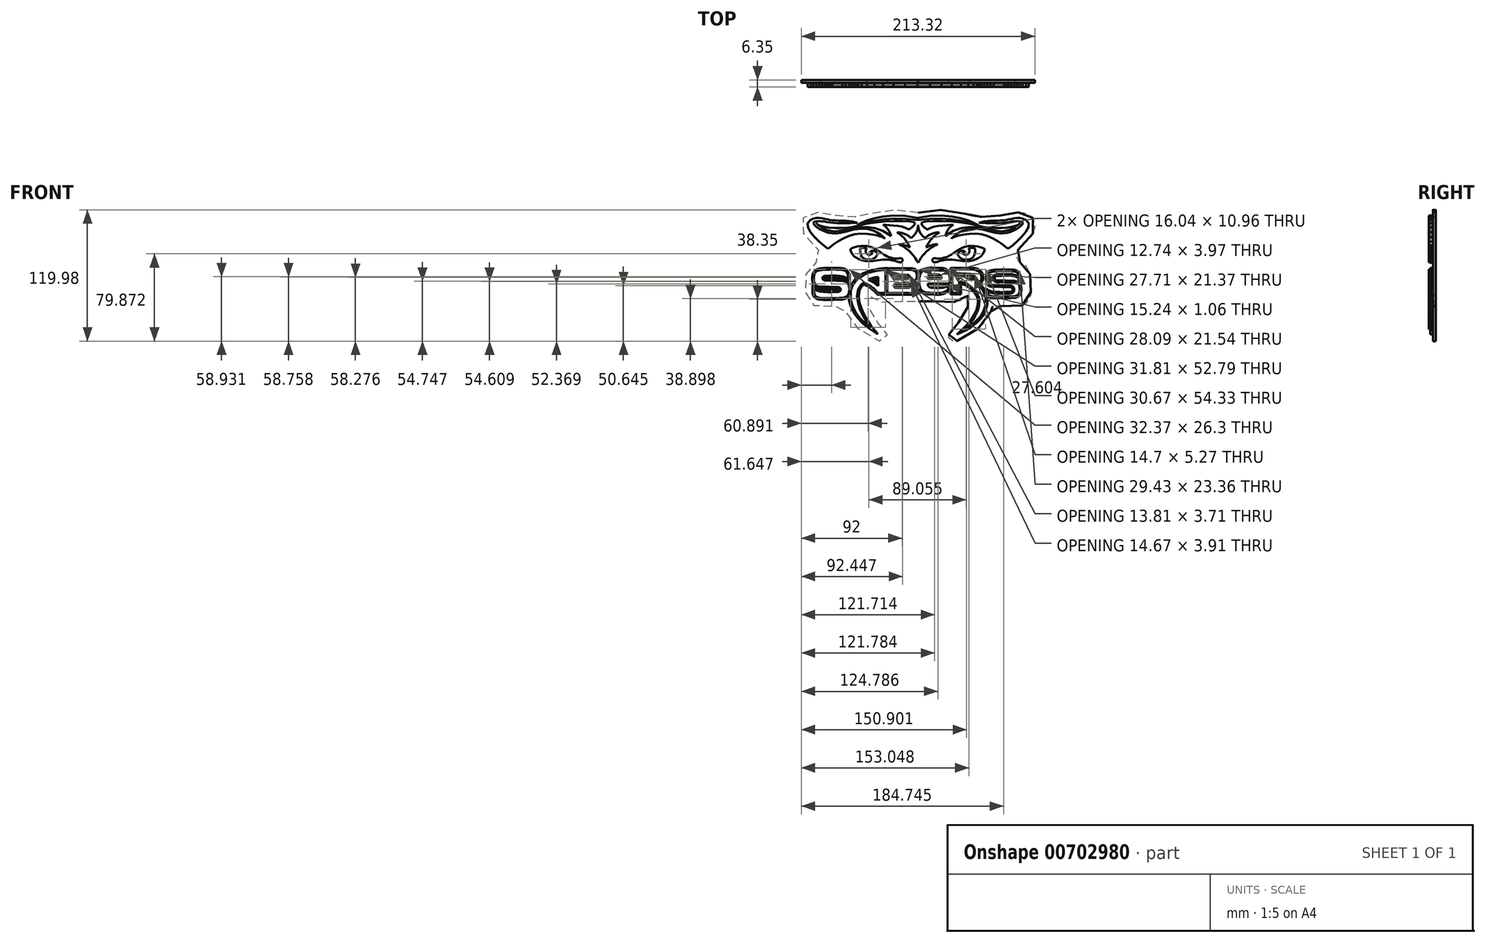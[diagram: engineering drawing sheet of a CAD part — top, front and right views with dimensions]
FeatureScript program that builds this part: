
annotation { "Feature Type Name" : "Feature", "Feature Type Description" : "" }
export const myFeature = defineFeature(function(context is Context, id is Id, definition is map)
    precondition{}
    {
        {
            var Q0;
            Q0=qCreatedBy(makeId("Front.planeOp"),FACE);
            var sketch = newSketch(context, id + "F0", { "sketchPlane" : qUnion([Q0])});
            skLineSegment(sketch, "E0", {"start": v(29.59, -9.42) * mm, "end": v(29.59, -9.4) * mm});
            skLineSegment(sketch, "E1", {"start": v(29.59, -9.4) * mm, "end": v(29.56, -9.4) * mm});
            skLineSegment(sketch, "E2", {"start": v(29.56, -9.4) * mm, "end": v(29.59, -9.42) * mm});
            skLineSegment(sketch, "E3", {"start": v(-61.99, 23.2) * mm, "end": v(-61.75, 23.63) * mm});
            skLineSegment(sketch, "E4", {"start": v(-61.75, 23.63) * mm, "end": v(-60.92, 24.2) * mm});
            skLineSegment(sketch, "E5", {"start": v(-60.92, 24.2) * mm, "end": v(-59.55, 24.82) * mm});
            skLineSegment(sketch, "E6", {"start": v(-59.55, 24.82) * mm, "end": v(-57.7, 25.43) * mm});
            skLineSegment(sketch, "E7", {"start": v(-57.7, 25.43) * mm, "end": v(-55.43, 25.95) * mm});
            skLineSegment(sketch, "E8", {"start": v(-55.43, 25.95) * mm, "end": v(-52.8, 26.3) * mm});
            skLineSegment(sketch, "E9", {"start": v(-52.8, 26.3) * mm, "end": v(-49.86, 26.41) * mm});
            skLineSegment(sketch, "E10", {"start": v(-49.86, 26.41) * mm, "end": v(-46.69, 26.2) * mm});
            skLineSegment(sketch, "E11", {"start": v(-46.69, 26.2) * mm, "end": v(-43.85, 25.66) * mm});
            skLineSegment(sketch, "E12", {"start": v(-43.85, 25.66) * mm, "end": v(-41.25, 24.77) * mm});
            skLineSegment(sketch, "E13", {"start": v(-41.25, 24.77) * mm, "end": v(-38.87, 23.64) * mm});
            skLineSegment(sketch, "E14", {"start": v(-38.87, 23.64) * mm, "end": v(-36.69, 22.36) * mm});
            skLineSegment(sketch, "E15", {"start": v(-36.69, 22.36) * mm, "end": v(-34.7, 21.02) * mm});
            skLineSegment(sketch, "E16", {"start": v(-34.7, 21.02) * mm, "end": v(-32.86, 19.73) * mm});
            skLineSegment(sketch, "E17", {"start": v(-32.86, 19.73) * mm, "end": v(-31.17, 18.56) * mm});
            skLineSegment(sketch, "E18", {"start": v(-31.17, 18.56) * mm, "end": v(-29.62, 17.63) * mm});
            skLineSegment(sketch, "E19", {"start": v(-29.62, 17.63) * mm, "end": v(-28.22, 16.96) * mm});
            skLineSegment(sketch, "E20", {"start": v(-28.22, 16.96) * mm, "end": v(-26.63, 16.34) * mm});
            skLineSegment(sketch, "E21", {"start": v(-26.63, 16.34) * mm, "end": v(-24.9, 15.8) * mm});
            skLineSegment(sketch, "E22", {"start": v(-24.9, 15.8) * mm, "end": v(-23.13, 15.35) * mm});
            skLineSegment(sketch, "E23", {"start": v(-23.13, 15.35) * mm, "end": v(-21.36, 15.03) * mm});
            skLineSegment(sketch, "E24", {"start": v(-21.36, 15.03) * mm, "end": v(-19.67, 14.88) * mm});
            skLineSegment(sketch, "E25", {"start": v(-19.67, 14.88) * mm, "end": v(-18.13, 14.9) * mm});
            skLineSegment(sketch, "E26", {"start": v(-18.13, 14.9) * mm, "end": v(-16.8, 15.15) * mm});
            skLineSegment(sketch, "E27", {"start": v(-16.8, 15.15) * mm, "end": v(-15.76, 15.32) * mm});
            skLineSegment(sketch, "E28", {"start": v(-15.76, 15.32) * mm, "end": v(-15, 15.16) * mm});
            skLineSegment(sketch, "E29", {"start": v(-15, 15.16) * mm, "end": v(-14.49, 14.75) * mm});
            skLineSegment(sketch, "E30", {"start": v(-14.49, 14.75) * mm, "end": v(-14.2, 14.18) * mm});
            skLineSegment(sketch, "E31", {"start": v(-14.2, 14.18) * mm, "end": v(-14.11, 13.54) * mm});
            skLineSegment(sketch, "E32", {"start": v(-14.11, 13.54) * mm, "end": v(-14.19, 12.9) * mm});
            skLineSegment(sketch, "E33", {"start": v(-14.19, 12.9) * mm, "end": v(-14.4, 12.34) * mm});
            skLineSegment(sketch, "E34", {"start": v(-14.4, 12.34) * mm, "end": v(-14.72, 11.97) * mm});
            skLineSegment(sketch, "E35", {"start": v(-14.72, 11.97) * mm, "end": v(-15.07, 11.73) * mm});
            skLineSegment(sketch, "E36", {"start": v(-15.07, 11.73) * mm, "end": v(-15.44, 11.57) * mm});
            skLineSegment(sketch, "E37", {"start": v(-15.44, 11.57) * mm, "end": v(-15.86, 11.48) * mm});
            skLineSegment(sketch, "E38", {"start": v(-15.86, 11.48) * mm, "end": v(-16.38, 11.48) * mm});
            skLineSegment(sketch, "E39", {"start": v(-16.38, 11.48) * mm, "end": v(-17.07, 11.59) * mm});
            skLineSegment(sketch, "E40", {"start": v(-17.07, 11.59) * mm, "end": v(-17.96, 11.81) * mm});
            skLineSegment(sketch, "E41", {"start": v(-17.96, 11.81) * mm, "end": v(-19.1, 12.16) * mm});
            skLineSegment(sketch, "E42", {"start": v(-19.1, 12.16) * mm, "end": v(-20.54, 12.66) * mm});
            skLineSegment(sketch, "E43", {"start": v(-20.54, 12.66) * mm, "end": v(-21.26, 12.89) * mm});
            skLineSegment(sketch, "E44", {"start": v(-21.26, 12.89) * mm, "end": v(-22.02, 13.1) * mm});
            skLineSegment(sketch, "E45", {"start": v(-22.02, 13.1) * mm, "end": v(-22.84, 13.27) * mm});
            skLineSegment(sketch, "E46", {"start": v(-22.84, 13.27) * mm, "end": v(-23.69, 13.44) * mm});
            skLineSegment(sketch, "E47", {"start": v(-23.69, 13.44) * mm, "end": v(-24.57, 13.59) * mm});
            skLineSegment(sketch, "E48", {"start": v(-24.57, 13.59) * mm, "end": v(-25.46, 13.72) * mm});
            skLineSegment(sketch, "E49", {"start": v(-25.46, 13.72) * mm, "end": v(-26.37, 13.84) * mm});
            skLineSegment(sketch, "E50", {"start": v(-26.37, 13.84) * mm, "end": v(-27.28, 13.95) * mm});
            skLineSegment(sketch, "E51", {"start": v(-27.28, 13.95) * mm, "end": v(-29.77, 14.12) * mm});
            skLineSegment(sketch, "E52", {"start": v(-29.77, 14.12) * mm, "end": v(-32.23, 14.04) * mm});
            skLineSegment(sketch, "E53", {"start": v(-32.23, 14.04) * mm, "end": v(-34.65, 13.8) * mm});
            skLineSegment(sketch, "E54", {"start": v(-34.65, 13.8) * mm, "end": v(-37, 13.45) * mm});
            skLineSegment(sketch, "E55", {"start": v(-37, 13.45) * mm, "end": v(-39.23, 13.08) * mm});
            skLineSegment(sketch, "E56", {"start": v(-39.23, 13.08) * mm, "end": v(-41.33, 12.75) * mm});
            skLineSegment(sketch, "E57", {"start": v(-41.33, 12.75) * mm, "end": v(-43.27, 12.54) * mm});
            skLineSegment(sketch, "E58", {"start": v(-43.27, 12.54) * mm, "end": v(-45.02, 12.5) * mm});
            skLineSegment(sketch, "E59", {"start": v(-45.02, 12.5) * mm, "end": v(-48.22, 12.8) * mm});
            skLineSegment(sketch, "E60", {"start": v(-48.22, 12.8) * mm, "end": v(-51.17, 13.4) * mm});
            skLineSegment(sketch, "E61", {"start": v(-51.17, 13.4) * mm, "end": v(-53.83, 14.28) * mm});
            skLineSegment(sketch, "E62", {"start": v(-53.83, 14.28) * mm, "end": v(-56.2, 15.46) * mm});
            skLineSegment(sketch, "E63", {"start": v(-56.2, 15.46) * mm, "end": v(-58.2, 16.93) * mm});
            skLineSegment(sketch, "E64", {"start": v(-58.2, 16.93) * mm, "end": v(-59.87, 18.71) * mm});
            skLineSegment(sketch, "E65", {"start": v(-59.87, 18.71) * mm, "end": v(-61.14, 20.8) * mm});
            skLineSegment(sketch, "E66", {"start": v(-61.14, 20.8) * mm, "end": v(-61.99, 23.2) * mm});
            skLineSegment(sketch, "E67", {"start": v(-47, 24.3) * mm, "end": v(-47.18, 24.33) * mm});
            skLineSegment(sketch, "E68", {"start": v(-47.18, 24.33) * mm, "end": v(-47.65, 24.44) * mm});
            skLineSegment(sketch, "E69", {"start": v(-47.65, 24.44) * mm, "end": v(-48.36, 24.57) * mm});
            skLineSegment(sketch, "E70", {"start": v(-48.36, 24.57) * mm, "end": v(-49.23, 24.69) * mm});
            skLineSegment(sketch, "E71", {"start": v(-49.23, 24.69) * mm, "end": v(-50.18, 24.77) * mm});
            skLineSegment(sketch, "E72", {"start": v(-50.18, 24.77) * mm, "end": v(-51.16, 24.77) * mm});
            skLineSegment(sketch, "E73", {"start": v(-51.16, 24.77) * mm, "end": v(-52.09, 24.67) * mm});
            skLineSegment(sketch, "E74", {"start": v(-52.09, 24.67) * mm, "end": v(-52.9, 24.42) * mm});
            skLineSegment(sketch, "E75", {"start": v(-52.9, 24.42) * mm, "end": v(-52.95, 24.02) * mm});
            skLineSegment(sketch, "E76", {"start": v(-52.95, 24.02) * mm, "end": v(-53.03, 22.94) * mm});
            skLineSegment(sketch, "E77", {"start": v(-53.03, 22.94) * mm, "end": v(-53, 21.4) * mm});
            skLineSegment(sketch, "E78", {"start": v(-53, 21.4) * mm, "end": v(-52.71, 19.6) * mm});
            skLineSegment(sketch, "E79", {"start": v(-52.71, 19.6) * mm, "end": v(-52.04, 17.74) * mm});
            skLineSegment(sketch, "E80", {"start": v(-52.04, 17.74) * mm, "end": v(-50.83, 16.03) * mm});
            skLineSegment(sketch, "E81", {"start": v(-50.83, 16.03) * mm, "end": v(-48.96, 14.68) * mm});
            skLineSegment(sketch, "E82", {"start": v(-48.96, 14.68) * mm, "end": v(-46.29, 13.88) * mm});
            skLineSegment(sketch, "E83", {"start": v(-46.29, 13.88) * mm, "end": v(-43.65, 13.81) * mm});
            skLineSegment(sketch, "E84", {"start": v(-43.65, 13.81) * mm, "end": v(-41.55, 14.3) * mm});
            skLineSegment(sketch, "E85", {"start": v(-41.55, 14.3) * mm, "end": v(-39.92, 15.2) * mm});
            skLineSegment(sketch, "E86", {"start": v(-39.92, 15.2) * mm, "end": v(-38.72, 16.31) * mm});
            skLineSegment(sketch, "E87", {"start": v(-38.72, 16.31) * mm, "end": v(-37.88, 17.48) * mm});
            skLineSegment(sketch, "E88", {"start": v(-37.88, 17.48) * mm, "end": v(-37.35, 18.53) * mm});
            skLineSegment(sketch, "E89", {"start": v(-37.35, 18.53) * mm, "end": v(-37.07, 19.28) * mm});
            skLineSegment(sketch, "E90", {"start": v(-37.07, 19.28) * mm, "end": v(-37, 19.57) * mm});
            skLineSegment(sketch, "E91", {"start": v(-37, 19.57) * mm, "end": v(-37.09, 19.7) * mm});
            skLineSegment(sketch, "E92", {"start": v(-37.09, 19.7) * mm, "end": v(-37.36, 20.04) * mm});
            skLineSegment(sketch, "E93", {"start": v(-37.36, 20.04) * mm, "end": v(-37.83, 20.5) * mm});
            skLineSegment(sketch, "E94", {"start": v(-37.83, 20.5) * mm, "end": v(-38.5, 21) * mm});
            skLineSegment(sketch, "E95", {"start": v(-38.5, 21) * mm, "end": v(-39.37, 21.47) * mm});
            skLineSegment(sketch, "E96", {"start": v(-39.37, 21.47) * mm, "end": v(-40.44, 21.8) * mm});
            skLineSegment(sketch, "E97", {"start": v(-40.44, 21.8) * mm, "end": v(-41.73, 21.94) * mm});
            skLineSegment(sketch, "E98", {"start": v(-41.73, 21.94) * mm, "end": v(-43.24, 21.78) * mm});
            skLineSegment(sketch, "E99", {"start": v(-43.24, 21.78) * mm, "end": v(-43.28, 21.74) * mm});
            skLineSegment(sketch, "E100", {"start": v(-43.28, 21.74) * mm, "end": v(-43.36, 21.63) * mm});
            skLineSegment(sketch, "E101", {"start": v(-43.36, 21.63) * mm, "end": v(-43.45, 21.47) * mm});
            skLineSegment(sketch, "E102", {"start": v(-43.45, 21.47) * mm, "end": v(-43.5, 21.28) * mm});
            skLineSegment(sketch, "E103", {"start": v(-43.5, 21.28) * mm, "end": v(-43.46, 21.08) * mm});
            skLineSegment(sketch, "E104", {"start": v(-43.46, 21.08) * mm, "end": v(-43.29, 20.9) * mm});
            skLineSegment(sketch, "E105", {"start": v(-43.29, 20.9) * mm, "end": v(-42.95, 20.72) * mm});
            skLineSegment(sketch, "E106", {"start": v(-42.95, 20.72) * mm, "end": v(-42.4, 20.6) * mm});
            skLineSegment(sketch, "E107", {"start": v(-42.4, 20.6) * mm, "end": v(-41.88, 20.42) * mm});
            skLineSegment(sketch, "E108", {"start": v(-41.88, 20.42) * mm, "end": v(-41.7, 20.12) * mm});
            skLineSegment(sketch, "E109", {"start": v(-41.7, 20.12) * mm, "end": v(-41.78, 19.74) * mm});
            skLineSegment(sketch, "E110", {"start": v(-41.78, 19.74) * mm, "end": v(-42.11, 19.33) * mm});
            skLineSegment(sketch, "E111", {"start": v(-42.11, 19.33) * mm, "end": v(-42.64, 18.95) * mm});
            skLineSegment(sketch, "E112", {"start": v(-42.64, 18.95) * mm, "end": v(-43.32, 18.65) * mm});
            skLineSegment(sketch, "E113", {"start": v(-43.32, 18.65) * mm, "end": v(-44.12, 18.47) * mm});
            skLineSegment(sketch, "E114", {"start": v(-44.12, 18.47) * mm, "end": v(-45, 18.47) * mm});
            skLineSegment(sketch, "E115", {"start": v(-45, 18.47) * mm, "end": v(-45.77, 18.66) * mm});
            skLineSegment(sketch, "E116", {"start": v(-45.77, 18.66) * mm, "end": v(-46.5, 19.03) * mm});
            skLineSegment(sketch, "E117", {"start": v(-46.5, 19.03) * mm, "end": v(-47.12, 19.58) * mm});
            skLineSegment(sketch, "E118", {"start": v(-47.12, 19.58) * mm, "end": v(-47.6, 20.27) * mm});
            skLineSegment(sketch, "E119", {"start": v(-47.6, 20.27) * mm, "end": v(-47.87, 21.1) * mm});
            skLineSegment(sketch, "E120", {"start": v(-47.87, 21.1) * mm, "end": v(-47.9, 22.06) * mm});
            skLineSegment(sketch, "E121", {"start": v(-47.9, 22.06) * mm, "end": v(-47.62, 23.13) * mm});
            skLineSegment(sketch, "E122", {"start": v(-47.62, 23.13) * mm, "end": v(-47, 24.3) * mm});
            skLineSegment(sketch, "E123", {"start": v(61.02, 23.2) * mm, "end": v(60.78, 23.63) * mm});
            skLineSegment(sketch, "E124", {"start": v(60.78, 23.63) * mm, "end": v(59.95, 24.2) * mm});
            skLineSegment(sketch, "E125", {"start": v(59.95, 24.2) * mm, "end": v(58.58, 24.82) * mm});
            skLineSegment(sketch, "E126", {"start": v(58.58, 24.82) * mm, "end": v(56.73, 25.43) * mm});
            skLineSegment(sketch, "E127", {"start": v(56.73, 25.43) * mm, "end": v(54.46, 25.95) * mm});
            skLineSegment(sketch, "E128", {"start": v(54.46, 25.95) * mm, "end": v(51.82, 26.3) * mm});
            skLineSegment(sketch, "E129", {"start": v(51.82, 26.3) * mm, "end": v(48.9, 26.41) * mm});
            skLineSegment(sketch, "E130", {"start": v(48.9, 26.41) * mm, "end": v(45.71, 26.2) * mm});
            skLineSegment(sketch, "E131", {"start": v(45.71, 26.2) * mm, "end": v(42.88, 25.66) * mm});
            skLineSegment(sketch, "E132", {"start": v(42.88, 25.66) * mm, "end": v(40.28, 24.77) * mm});
            skLineSegment(sketch, "E133", {"start": v(40.28, 24.77) * mm, "end": v(37.9, 23.64) * mm});
            skLineSegment(sketch, "E134", {"start": v(37.9, 23.64) * mm, "end": v(35.72, 22.36) * mm});
            skLineSegment(sketch, "E135", {"start": v(35.72, 22.36) * mm, "end": v(33.72, 21.02) * mm});
            skLineSegment(sketch, "E136", {"start": v(33.72, 21.02) * mm, "end": v(31.89, 19.73) * mm});
            skLineSegment(sketch, "E137", {"start": v(31.89, 19.73) * mm, "end": v(30.2, 18.56) * mm});
            skLineSegment(sketch, "E138", {"start": v(30.2, 18.56) * mm, "end": v(28.65, 17.63) * mm});
            skLineSegment(sketch, "E139", {"start": v(28.65, 17.63) * mm, "end": v(27.25, 16.96) * mm});
            skLineSegment(sketch, "E140", {"start": v(27.25, 16.96) * mm, "end": v(25.66, 16.34) * mm});
            skLineSegment(sketch, "E141", {"start": v(25.66, 16.34) * mm, "end": v(23.93, 15.8) * mm});
            skLineSegment(sketch, "E142", {"start": v(23.93, 15.8) * mm, "end": v(22.15, 15.35) * mm});
            skLineSegment(sketch, "E143", {"start": v(22.15, 15.35) * mm, "end": v(20.39, 15.03) * mm});
            skLineSegment(sketch, "E144", {"start": v(20.39, 15.03) * mm, "end": v(18.7, 14.88) * mm});
            skLineSegment(sketch, "E145", {"start": v(18.7, 14.88) * mm, "end": v(17.15, 14.9) * mm});
            skLineSegment(sketch, "E146", {"start": v(17.15, 14.9) * mm, "end": v(15.83, 15.15) * mm});
            skLineSegment(sketch, "E147", {"start": v(15.83, 15.15) * mm, "end": v(14.78, 15.32) * mm});
            skLineSegment(sketch, "E148", {"start": v(14.78, 15.32) * mm, "end": v(14.02, 15.16) * mm});
            skLineSegment(sketch, "E149", {"start": v(14.02, 15.16) * mm, "end": v(13.51, 14.75) * mm});
            skLineSegment(sketch, "E150", {"start": v(13.51, 14.75) * mm, "end": v(13.23, 14.18) * mm});
            skLineSegment(sketch, "E151", {"start": v(13.23, 14.18) * mm, "end": v(13.14, 13.54) * mm});
            skLineSegment(sketch, "E152", {"start": v(13.14, 13.54) * mm, "end": v(13.22, 12.9) * mm});
            skLineSegment(sketch, "E153", {"start": v(13.22, 12.9) * mm, "end": v(13.43, 12.34) * mm});
            skLineSegment(sketch, "E154", {"start": v(13.43, 12.34) * mm, "end": v(13.75, 11.97) * mm});
            skLineSegment(sketch, "E155", {"start": v(13.75, 11.97) * mm, "end": v(14.1, 11.73) * mm});
            skLineSegment(sketch, "E156", {"start": v(14.1, 11.73) * mm, "end": v(14.46, 11.57) * mm});
            skLineSegment(sketch, "E157", {"start": v(14.46, 11.57) * mm, "end": v(14.88, 11.48) * mm});
            skLineSegment(sketch, "E158", {"start": v(14.88, 11.48) * mm, "end": v(15.41, 11.48) * mm});
            skLineSegment(sketch, "E159", {"start": v(15.41, 11.48) * mm, "end": v(16.1, 11.59) * mm});
            skLineSegment(sketch, "E160", {"start": v(16.1, 11.59) * mm, "end": v(16.99, 11.81) * mm});
            skLineSegment(sketch, "E161", {"start": v(16.99, 11.81) * mm, "end": v(18.13, 12.16) * mm});
            skLineSegment(sketch, "E162", {"start": v(18.13, 12.16) * mm, "end": v(19.57, 12.66) * mm});
            skLineSegment(sketch, "E163", {"start": v(19.57, 12.66) * mm, "end": v(20.28, 12.89) * mm});
            skLineSegment(sketch, "E164", {"start": v(20.28, 12.89) * mm, "end": v(21.05, 13.1) * mm});
            skLineSegment(sketch, "E165", {"start": v(21.05, 13.1) * mm, "end": v(21.86, 13.27) * mm});
            skLineSegment(sketch, "E166", {"start": v(21.86, 13.27) * mm, "end": v(22.72, 13.44) * mm});
            skLineSegment(sketch, "E167", {"start": v(22.72, 13.44) * mm, "end": v(23.6, 13.59) * mm});
            skLineSegment(sketch, "E168", {"start": v(23.6, 13.59) * mm, "end": v(24.5, 13.72) * mm});
            skLineSegment(sketch, "E169", {"start": v(24.5, 13.72) * mm, "end": v(25.4, 13.84) * mm});
            skLineSegment(sketch, "E170", {"start": v(25.4, 13.84) * mm, "end": v(26.3, 13.95) * mm});
            skLineSegment(sketch, "E171", {"start": v(26.3, 13.95) * mm, "end": v(28.8, 14.12) * mm});
            skLineSegment(sketch, "E172", {"start": v(28.8, 14.12) * mm, "end": v(31.26, 14.04) * mm});
            skLineSegment(sketch, "E173", {"start": v(31.26, 14.04) * mm, "end": v(33.68, 13.8) * mm});
            skLineSegment(sketch, "E174", {"start": v(33.68, 13.8) * mm, "end": v(36.02, 13.45) * mm});
            skLineSegment(sketch, "E175", {"start": v(36.02, 13.45) * mm, "end": v(38.26, 13.08) * mm});
            skLineSegment(sketch, "E176", {"start": v(38.26, 13.08) * mm, "end": v(40.36, 12.75) * mm});
            skLineSegment(sketch, "E177", {"start": v(40.36, 12.75) * mm, "end": v(42.3, 12.54) * mm});
            skLineSegment(sketch, "E178", {"start": v(42.3, 12.54) * mm, "end": v(44.05, 12.5) * mm});
            skLineSegment(sketch, "E179", {"start": v(44.05, 12.5) * mm, "end": v(47.25, 12.8) * mm});
            skLineSegment(sketch, "E180", {"start": v(47.25, 12.8) * mm, "end": v(50.2, 13.4) * mm});
            skLineSegment(sketch, "E181", {"start": v(50.2, 13.4) * mm, "end": v(52.86, 14.28) * mm});
            skLineSegment(sketch, "E182", {"start": v(52.86, 14.28) * mm, "end": v(55.22, 15.46) * mm});
            skLineSegment(sketch, "E183", {"start": v(55.22, 15.46) * mm, "end": v(57.24, 16.93) * mm});
            skLineSegment(sketch, "E184", {"start": v(57.24, 16.93) * mm, "end": v(58.9, 18.71) * mm});
            skLineSegment(sketch, "E185", {"start": v(58.9, 18.71) * mm, "end": v(60.16, 20.8) * mm});
            skLineSegment(sketch, "E186", {"start": v(60.16, 20.8) * mm, "end": v(61.02, 23.2) * mm});
            skLineSegment(sketch, "E187", {"start": v(46.03, 24.3) * mm, "end": v(46.2, 24.33) * mm});
            skLineSegment(sketch, "E188", {"start": v(46.2, 24.33) * mm, "end": v(46.68, 24.44) * mm});
            skLineSegment(sketch, "E189", {"start": v(46.68, 24.44) * mm, "end": v(47.39, 24.57) * mm});
            skLineSegment(sketch, "E190", {"start": v(47.39, 24.57) * mm, "end": v(48.25, 24.69) * mm});
            skLineSegment(sketch, "E191", {"start": v(48.25, 24.69) * mm, "end": v(49.21, 24.77) * mm});
            skLineSegment(sketch, "E192", {"start": v(49.21, 24.77) * mm, "end": v(50.19, 24.77) * mm});
            skLineSegment(sketch, "E193", {"start": v(50.19, 24.77) * mm, "end": v(51.12, 24.67) * mm});
            skLineSegment(sketch, "E194", {"start": v(51.12, 24.67) * mm, "end": v(51.92, 24.42) * mm});
            skLineSegment(sketch, "E195", {"start": v(51.92, 24.42) * mm, "end": v(51.98, 24.02) * mm});
            skLineSegment(sketch, "E196", {"start": v(51.98, 24.02) * mm, "end": v(52.06, 22.94) * mm});
            skLineSegment(sketch, "E197", {"start": v(52.06, 22.94) * mm, "end": v(52.03, 21.4) * mm});
            skLineSegment(sketch, "E198", {"start": v(52.03, 21.4) * mm, "end": v(51.74, 19.6) * mm});
            skLineSegment(sketch, "E199", {"start": v(51.74, 19.6) * mm, "end": v(51.07, 17.74) * mm});
            skLineSegment(sketch, "E200", {"start": v(51.07, 17.74) * mm, "end": v(49.86, 16.03) * mm});
            skLineSegment(sketch, "E201", {"start": v(49.86, 16.03) * mm, "end": v(47.99, 14.68) * mm});
            skLineSegment(sketch, "E202", {"start": v(47.99, 14.68) * mm, "end": v(45.31, 13.88) * mm});
            skLineSegment(sketch, "E203", {"start": v(45.31, 13.88) * mm, "end": v(42.68, 13.81) * mm});
            skLineSegment(sketch, "E204", {"start": v(42.68, 13.81) * mm, "end": v(40.58, 14.3) * mm});
            skLineSegment(sketch, "E205", {"start": v(40.58, 14.3) * mm, "end": v(38.95, 15.2) * mm});
            skLineSegment(sketch, "E206", {"start": v(38.95, 15.2) * mm, "end": v(37.75, 16.31) * mm});
            skLineSegment(sketch, "E207", {"start": v(37.75, 16.31) * mm, "end": v(36.91, 17.48) * mm});
            skLineSegment(sketch, "E208", {"start": v(36.91, 17.48) * mm, "end": v(36.38, 18.53) * mm});
            skLineSegment(sketch, "E209", {"start": v(36.38, 18.53) * mm, "end": v(36.1, 19.28) * mm});
            skLineSegment(sketch, "E210", {"start": v(36.1, 19.28) * mm, "end": v(36.02, 19.57) * mm});
            skLineSegment(sketch, "E211", {"start": v(36.02, 19.57) * mm, "end": v(36.11, 19.7) * mm});
            skLineSegment(sketch, "E212", {"start": v(36.11, 19.7) * mm, "end": v(36.4, 20.04) * mm});
            skLineSegment(sketch, "E213", {"start": v(36.4, 20.04) * mm, "end": v(36.86, 20.5) * mm});
            skLineSegment(sketch, "E214", {"start": v(36.86, 20.5) * mm, "end": v(37.53, 21) * mm});
            skLineSegment(sketch, "E215", {"start": v(37.53, 21) * mm, "end": v(38.4, 21.47) * mm});
            skLineSegment(sketch, "E216", {"start": v(38.4, 21.47) * mm, "end": v(39.47, 21.8) * mm});
            skLineSegment(sketch, "E217", {"start": v(39.47, 21.8) * mm, "end": v(40.76, 21.94) * mm});
            skLineSegment(sketch, "E218", {"start": v(40.76, 21.94) * mm, "end": v(42.27, 21.78) * mm});
            skLineSegment(sketch, "E219", {"start": v(42.27, 21.78) * mm, "end": v(42.3, 21.74) * mm});
            skLineSegment(sketch, "E220", {"start": v(42.3, 21.74) * mm, "end": v(42.4, 21.63) * mm});
            skLineSegment(sketch, "E221", {"start": v(42.4, 21.63) * mm, "end": v(42.48, 21.47) * mm});
            skLineSegment(sketch, "E222", {"start": v(42.48, 21.47) * mm, "end": v(42.52, 21.28) * mm});
            skLineSegment(sketch, "E223", {"start": v(42.52, 21.28) * mm, "end": v(42.49, 21.08) * mm});
            skLineSegment(sketch, "E224", {"start": v(42.49, 21.08) * mm, "end": v(42.32, 20.9) * mm});
            skLineSegment(sketch, "E225", {"start": v(42.32, 20.9) * mm, "end": v(41.98, 20.72) * mm});
            skLineSegment(sketch, "E226", {"start": v(41.98, 20.72) * mm, "end": v(41.42, 20.6) * mm});
            skLineSegment(sketch, "E227", {"start": v(41.42, 20.6) * mm, "end": v(40.91, 20.42) * mm});
            skLineSegment(sketch, "E228", {"start": v(40.91, 20.42) * mm, "end": v(40.72, 20.12) * mm});
            skLineSegment(sketch, "E229", {"start": v(40.72, 20.12) * mm, "end": v(40.81, 19.74) * mm});
            skLineSegment(sketch, "E230", {"start": v(40.81, 19.74) * mm, "end": v(41.14, 19.33) * mm});
            skLineSegment(sketch, "E231", {"start": v(41.14, 19.33) * mm, "end": v(41.67, 18.95) * mm});
            skLineSegment(sketch, "E232", {"start": v(41.67, 18.95) * mm, "end": v(42.35, 18.65) * mm});
            skLineSegment(sketch, "E233", {"start": v(42.35, 18.65) * mm, "end": v(43.15, 18.47) * mm});
            skLineSegment(sketch, "E234", {"start": v(43.15, 18.47) * mm, "end": v(44.03, 18.47) * mm});
            skLineSegment(sketch, "E235", {"start": v(44.03, 18.47) * mm, "end": v(44.8, 18.66) * mm});
            skLineSegment(sketch, "E236", {"start": v(44.8, 18.66) * mm, "end": v(45.52, 19.03) * mm});
            skLineSegment(sketch, "E237", {"start": v(45.52, 19.03) * mm, "end": v(46.15, 19.58) * mm});
            skLineSegment(sketch, "E238", {"start": v(46.15, 19.58) * mm, "end": v(46.62, 20.27) * mm});
            skLineSegment(sketch, "E239", {"start": v(46.62, 20.27) * mm, "end": v(46.9, 21.1) * mm});
            skLineSegment(sketch, "E240", {"start": v(46.9, 21.1) * mm, "end": v(46.92, 22.06) * mm});
            skLineSegment(sketch, "E241", {"start": v(46.92, 22.06) * mm, "end": v(46.65, 23.13) * mm});
            skLineSegment(sketch, "E242", {"start": v(46.65, 23.13) * mm, "end": v(46.03, 24.3) * mm});
            skLineSegment(sketch, "E243", {"start": v(-55.59, 47.59) * mm, "end": v(-57.95, 48.29) * mm});
            skLineSegment(sketch, "E244", {"start": v(-57.95, 48.29) * mm, "end": v(-60.51, 48.8) * mm});
            skLineSegment(sketch, "E245", {"start": v(-60.51, 48.8) * mm, "end": v(-63.26, 49.16) * mm});
            skLineSegment(sketch, "E246", {"start": v(-63.26, 49.16) * mm, "end": v(-66.14, 49.4) * mm});
            skLineSegment(sketch, "E247", {"start": v(-66.14, 49.4) * mm, "end": v(-69.13, 49.57) * mm});
            skLineSegment(sketch, "E248", {"start": v(-69.13, 49.57) * mm, "end": v(-72.2, 49.68) * mm});
            skLineSegment(sketch, "E249", {"start": v(-72.2, 49.68) * mm, "end": v(-75.32, 49.78) * mm});
            skLineSegment(sketch, "E250", {"start": v(-75.32, 49.78) * mm, "end": v(-78.45, 49.9) * mm});
            skLineSegment(sketch, "E251", {"start": v(-78.45, 49.9) * mm, "end": v(-80.5, 50.17) * mm});
            skLineSegment(sketch, "E252", {"start": v(-80.5, 50.17) * mm, "end": v(-82.72, 50.67) * mm});
            skLineSegment(sketch, "E253", {"start": v(-82.72, 50.67) * mm, "end": v(-85.1, 51.25) * mm});
            skLineSegment(sketch, "E254", {"start": v(-85.1, 51.25) * mm, "end": v(-87.6, 51.77) * mm});
            skLineSegment(sketch, "E255", {"start": v(-87.6, 51.77) * mm, "end": v(-90.21, 52.08) * mm});
            skLineSegment(sketch, "E256", {"start": v(-90.21, 52.08) * mm, "end": v(-92.9, 52.03) * mm});
            skLineSegment(sketch, "E257", {"start": v(-92.9, 52.03) * mm, "end": v(-95.65, 51.47) * mm});
            skLineSegment(sketch, "E258", {"start": v(-95.65, 51.47) * mm, "end": v(-98.44, 50.25) * mm});
            skLineSegment(sketch, "E259", {"start": v(-98.44, 50.25) * mm, "end": v(-100.97, 47.25) * mm});
            skLineSegment(sketch, "E260", {"start": v(-100.97, 47.25) * mm, "end": v(-100.64, 43.38) * mm});
            skLineSegment(sketch, "E261", {"start": v(-100.64, 43.38) * mm, "end": v(-98.23, 39.02) * mm});
            skLineSegment(sketch, "E262", {"start": v(-98.23, 39.02) * mm, "end": v(-94.52, 34.57) * mm});
            skLineSegment(sketch, "E263", {"start": v(-94.52, 34.57) * mm, "end": v(-90.29, 30.43) * mm});
            skLineSegment(sketch, "E264", {"start": v(-90.29, 30.43) * mm, "end": v(-86.3, 26.98) * mm});
            skLineSegment(sketch, "E265", {"start": v(-86.3, 26.98) * mm, "end": v(-83.34, 24.62) * mm});
            skLineSegment(sketch, "E266", {"start": v(-83.34, 24.62) * mm, "end": v(-82.18, 23.75) * mm});
            skLineSegment(sketch, "E267", {"start": v(-82.18, 23.75) * mm, "end": v(-81.5, 24.36) * mm});
            skLineSegment(sketch, "E268", {"start": v(-81.5, 24.36) * mm, "end": v(-79.6, 25.96) * mm});
            skLineSegment(sketch, "E269", {"start": v(-79.6, 25.96) * mm, "end": v(-76.64, 28.23) * mm});
            skLineSegment(sketch, "E270", {"start": v(-76.64, 28.23) * mm, "end": v(-72.82, 30.82) * mm});
            skLineSegment(sketch, "E271", {"start": v(-72.82, 30.82) * mm, "end": v(-68.34, 33.4) * mm});
            skLineSegment(sketch, "E272", {"start": v(-68.34, 33.4) * mm, "end": v(-63.38, 35.65) * mm});
            skLineSegment(sketch, "E273", {"start": v(-63.38, 35.65) * mm, "end": v(-58.12, 37.22) * mm});
            skLineSegment(sketch, "E274", {"start": v(-58.12, 37.22) * mm, "end": v(-52.76, 37.78) * mm});
            skLineSegment(sketch, "E275", {"start": v(-52.76, 37.78) * mm, "end": v(-46.6, 37.52) * mm});
            skLineSegment(sketch, "E276", {"start": v(-46.6, 37.52) * mm, "end": v(-41.63, 36.97) * mm});
            skLineSegment(sketch, "E277", {"start": v(-41.63, 36.97) * mm, "end": v(-37.73, 36.22) * mm});
            skLineSegment(sketch, "E278", {"start": v(-37.73, 36.22) * mm, "end": v(-34.79, 35.38) * mm});
            skLineSegment(sketch, "E279", {"start": v(-34.79, 35.38) * mm, "end": v(-32.7, 34.54) * mm});
            skLineSegment(sketch, "E280", {"start": v(-32.7, 34.54) * mm, "end": v(-31.35, 33.82) * mm});
            skLineSegment(sketch, "E281", {"start": v(-31.35, 33.82) * mm, "end": v(-30.62, 33.31) * mm});
            skLineSegment(sketch, "E282", {"start": v(-30.62, 33.31) * mm, "end": v(-30.4, 33.12) * mm});
            skLineSegment(sketch, "E283", {"start": v(-30.4, 33.12) * mm, "end": v(-30.82, 33.64) * mm});
            skLineSegment(sketch, "E284", {"start": v(-30.82, 33.64) * mm, "end": v(-32.09, 35) * mm});
            skLineSegment(sketch, "E285", {"start": v(-32.09, 35) * mm, "end": v(-34.22, 36.82) * mm});
            skLineSegment(sketch, "E286", {"start": v(-34.22, 36.82) * mm, "end": v(-37.24, 38.8) * mm});
            skLineSegment(sketch, "E287", {"start": v(-37.24, 38.8) * mm, "end": v(-41.16, 40.6) * mm});
            skLineSegment(sketch, "E288", {"start": v(-41.16, 40.6) * mm, "end": v(-46.02, 41.86) * mm});
            skLineSegment(sketch, "E289", {"start": v(-46.02, 41.86) * mm, "end": v(-51.81, 42.25) * mm});
            skLineSegment(sketch, "E290", {"start": v(-51.81, 42.25) * mm, "end": v(-58.57, 41.44) * mm});
            skLineSegment(sketch, "E291", {"start": v(-58.57, 41.44) * mm, "end": v(-62.24, 40.6) * mm});
            skLineSegment(sketch, "E292", {"start": v(-62.24, 40.6) * mm, "end": v(-65.44, 39.78) * mm});
            skLineSegment(sketch, "E293", {"start": v(-65.44, 39.78) * mm, "end": v(-68.3, 39.03) * mm});
            skLineSegment(sketch, "E294", {"start": v(-68.3, 39.03) * mm, "end": v(-70.9, 38.43) * mm});
            skLineSegment(sketch, "E295", {"start": v(-70.9, 38.43) * mm, "end": v(-73.4, 38.01) * mm});
            skLineSegment(sketch, "E296", {"start": v(-73.4, 38.01) * mm, "end": v(-75.9, 37.84) * mm});
            skLineSegment(sketch, "E297", {"start": v(-75.9, 37.84) * mm, "end": v(-78.52, 37.98) * mm});
            skLineSegment(sketch, "E298", {"start": v(-78.52, 37.98) * mm, "end": v(-81.38, 38.49) * mm});
            skLineSegment(sketch, "E299", {"start": v(-81.38, 38.49) * mm, "end": v(-84.39, 39.39) * mm});
            skLineSegment(sketch, "E300", {"start": v(-84.39, 39.39) * mm, "end": v(-87.29, 40.6) * mm});
            skLineSegment(sketch, "E301", {"start": v(-87.29, 40.6) * mm, "end": v(-89.96, 42.01) * mm});
            skLineSegment(sketch, "E302", {"start": v(-89.96, 42.01) * mm, "end": v(-92.27, 43.51) * mm});
            skLineSegment(sketch, "E303", {"start": v(-92.27, 43.51) * mm, "end": v(-94.09, 44.99) * mm});
            skLineSegment(sketch, "E304", {"start": v(-94.09, 44.99) * mm, "end": v(-95.29, 46.33) * mm});
            skLineSegment(sketch, "E305", {"start": v(-95.29, 46.33) * mm, "end": v(-95.74, 47.41) * mm});
            skLineSegment(sketch, "E306", {"start": v(-95.74, 47.41) * mm, "end": v(-95.32, 48.14) * mm});
            skLineSegment(sketch, "E307", {"start": v(-95.32, 48.14) * mm, "end": v(-94.32, 48.57) * mm});
            skLineSegment(sketch, "E308", {"start": v(-94.32, 48.57) * mm, "end": v(-93.13, 48.88) * mm});
            skLineSegment(sketch, "E309", {"start": v(-93.13, 48.88) * mm, "end": v(-91.7, 49.05) * mm});
            skLineSegment(sketch, "E310", {"start": v(-91.7, 49.05) * mm, "end": v(-90.03, 49.08) * mm});
            skLineSegment(sketch, "E311", {"start": v(-90.03, 49.08) * mm, "end": v(-88.08, 48.98) * mm});
            skLineSegment(sketch, "E312", {"start": v(-88.08, 48.98) * mm, "end": v(-85.83, 48.75) * mm});
            skLineSegment(sketch, "E313", {"start": v(-85.83, 48.75) * mm, "end": v(-83.25, 48.38) * mm});
            skLineSegment(sketch, "E314", {"start": v(-83.25, 48.38) * mm, "end": v(-80.3, 47.87) * mm});
            skLineSegment(sketch, "E315", {"start": v(-80.3, 47.87) * mm, "end": v(-77.58, 47.55) * mm});
            skLineSegment(sketch, "E316", {"start": v(-77.58, 47.55) * mm, "end": v(-74, 47.37) * mm});
            skLineSegment(sketch, "E317", {"start": v(-74, 47.37) * mm, "end": v(-69.93, 47.3) * mm});
            skLineSegment(sketch, "E318", {"start": v(-69.93, 47.3) * mm, "end": v(-65.77, 47.33) * mm});
            skLineSegment(sketch, "E319", {"start": v(-65.77, 47.33) * mm, "end": v(-61.88, 47.4) * mm});
            skLineSegment(sketch, "E320", {"start": v(-61.88, 47.4) * mm, "end": v(-58.63, 47.48) * mm});
            skLineSegment(sketch, "E321", {"start": v(-58.63, 47.48) * mm, "end": v(-56.41, 47.55) * mm});
            skLineSegment(sketch, "E322", {"start": v(-56.41, 47.55) * mm, "end": v(-55.59, 47.59) * mm});
            skLineSegment(sketch, "E323", {"start": v(-0.49, 50.01) * mm, "end": v(10.33, 51.25) * mm});
            skLineSegment(sketch, "E324", {"start": v(10.33, 51.25) * mm, "end": v(20.56, 51.42) * mm});
            skLineSegment(sketch, "E325", {"start": v(20.56, 51.42) * mm, "end": v(29.95, 50.8) * mm});
            skLineSegment(sketch, "E326", {"start": v(29.95, 50.8) * mm, "end": v(38.22, 49.66) * mm});
            skLineSegment(sketch, "E327", {"start": v(38.22, 49.66) * mm, "end": v(45.12, 48.3) * mm});
            skLineSegment(sketch, "E328", {"start": v(45.12, 48.3) * mm, "end": v(50.37, 46.97) * mm});
            skLineSegment(sketch, "E329", {"start": v(50.37, 46.97) * mm, "end": v(53.72, 45.97) * mm});
            skLineSegment(sketch, "E330", {"start": v(53.72, 45.97) * mm, "end": v(54.9, 45.58) * mm});
            skLineSegment(sketch, "E331", {"start": v(54.9, 45.58) * mm, "end": v(53.8, 46.18) * mm});
            skLineSegment(sketch, "E332", {"start": v(53.8, 46.18) * mm, "end": v(50.67, 47.69) * mm});
            skLineSegment(sketch, "E333", {"start": v(50.67, 47.69) * mm, "end": v(45.68, 49.7) * mm});
            skLineSegment(sketch, "E334", {"start": v(45.68, 49.7) * mm, "end": v(39.02, 51.76) * mm});
            skLineSegment(sketch, "E335", {"start": v(39.02, 51.76) * mm, "end": v(30.88, 53.46) * mm});
            skLineSegment(sketch, "E336", {"start": v(30.88, 53.46) * mm, "end": v(21.46, 54.39) * mm});
            skLineSegment(sketch, "E337", {"start": v(21.46, 54.39) * mm, "end": v(10.94, 54.1) * mm});
            skLineSegment(sketch, "E338", {"start": v(10.94, 54.1) * mm, "end": v(-0.49, 52.18) * mm});
            skLineSegment(sketch, "E339", {"start": v(-0.49, 52.18) * mm, "end": v(-11.9, 54.1) * mm});
            skLineSegment(sketch, "E340", {"start": v(-11.9, 54.1) * mm, "end": v(-22.43, 54.39) * mm});
            skLineSegment(sketch, "E341", {"start": v(-22.43, 54.39) * mm, "end": v(-31.85, 53.46) * mm});
            skLineSegment(sketch, "E342", {"start": v(-31.85, 53.46) * mm, "end": v(-39.99, 51.76) * mm});
            skLineSegment(sketch, "E343", {"start": v(-39.99, 51.76) * mm, "end": v(-46.65, 49.7) * mm});
            skLineSegment(sketch, "E344", {"start": v(-46.65, 49.7) * mm, "end": v(-51.64, 47.69) * mm});
            skLineSegment(sketch, "E345", {"start": v(-51.64, 47.69) * mm, "end": v(-54.78, 46.18) * mm});
            skLineSegment(sketch, "E346", {"start": v(-54.78, 46.18) * mm, "end": v(-55.87, 45.58) * mm});
            skLineSegment(sketch, "E347", {"start": v(-55.87, 45.58) * mm, "end": v(-54.7, 45.97) * mm});
            skLineSegment(sketch, "E348", {"start": v(-54.7, 45.97) * mm, "end": v(-51.34, 46.97) * mm});
            skLineSegment(sketch, "E349", {"start": v(-51.34, 46.97) * mm, "end": v(-46.09, 48.3) * mm});
            skLineSegment(sketch, "E350", {"start": v(-46.09, 48.3) * mm, "end": v(-39.2, 49.66) * mm});
            skLineSegment(sketch, "E351", {"start": v(-39.2, 49.66) * mm, "end": v(-30.92, 50.8) * mm});
            skLineSegment(sketch, "E352", {"start": v(-30.92, 50.8) * mm, "end": v(-21.53, 51.42) * mm});
            skLineSegment(sketch, "E353", {"start": v(-21.53, 51.42) * mm, "end": v(-11.3, 51.25) * mm});
            skLineSegment(sketch, "E354", {"start": v(-11.3, 51.25) * mm, "end": v(-0.49, 50.01) * mm});
            skLineSegment(sketch, "E355", {"start": v(-93.42, 47.34) * mm, "end": v(-93.1, 47.03) * mm});
            skLineSegment(sketch, "E356", {"start": v(-93.1, 47.03) * mm, "end": v(-92.14, 46.2) * mm});
            skLineSegment(sketch, "E357", {"start": v(-92.14, 46.2) * mm, "end": v(-90.6, 45.02) * mm});
            skLineSegment(sketch, "E358", {"start": v(-90.6, 45.02) * mm, "end": v(-88.55, 43.66) * mm});
            skLineSegment(sketch, "E359", {"start": v(-88.55, 43.66) * mm, "end": v(-86.03, 42.29) * mm});
            skLineSegment(sketch, "E360", {"start": v(-86.03, 42.29) * mm, "end": v(-83.1, 41.08) * mm});
            skLineSegment(sketch, "E361", {"start": v(-83.1, 41.08) * mm, "end": v(-79.79, 40.2) * mm});
            skLineSegment(sketch, "E362", {"start": v(-79.79, 40.2) * mm, "end": v(-76.18, 39.8) * mm});
            skLineSegment(sketch, "E363", {"start": v(-76.18, 39.8) * mm, "end": v(-71.92, 40.22) * mm});
            skLineSegment(sketch, "E364", {"start": v(-71.92, 40.22) * mm, "end": v(-66.75, 41.3) * mm});
            skLineSegment(sketch, "E365", {"start": v(-66.75, 41.3) * mm, "end": v(-60.82, 42.6) * mm});
            skLineSegment(sketch, "E366", {"start": v(-60.82, 42.6) * mm, "end": v(-54.26, 43.62) * mm});
            skLineSegment(sketch, "E367", {"start": v(-54.26, 43.62) * mm, "end": v(-47.23, 43.9) * mm});
            skLineSegment(sketch, "E368", {"start": v(-47.23, 43.9) * mm, "end": v(-39.86, 43) * mm});
            skLineSegment(sketch, "E369", {"start": v(-39.86, 43) * mm, "end": v(-32.31, 40.4) * mm});
            skLineSegment(sketch, "E370", {"start": v(-32.31, 40.4) * mm, "end": v(-24.72, 35.65) * mm});
            skLineSegment(sketch, "E371", {"start": v(-24.72, 35.65) * mm, "end": v(-24.82, 35.99) * mm});
            skLineSegment(sketch, "E372", {"start": v(-24.82, 35.99) * mm, "end": v(-25.12, 36.9) * mm});
            skLineSegment(sketch, "E373", {"start": v(-25.12, 36.9) * mm, "end": v(-25.65, 38.23) * mm});
            skLineSegment(sketch, "E374", {"start": v(-25.65, 38.23) * mm, "end": v(-26.4, 39.82) * mm});
            skLineSegment(sketch, "E375", {"start": v(-26.4, 39.82) * mm, "end": v(-27.4, 41.52) * mm});
            skLineSegment(sketch, "E376", {"start": v(-27.4, 41.52) * mm, "end": v(-28.67, 43.16) * mm});
            skLineSegment(sketch, "E377", {"start": v(-28.67, 43.16) * mm, "end": v(-30.2, 44.6) * mm});
            skLineSegment(sketch, "E378", {"start": v(-30.2, 44.6) * mm, "end": v(-32, 45.65) * mm});
            skLineSegment(sketch, "E379", {"start": v(-32, 45.65) * mm, "end": v(-31.22, 45.66) * mm});
            skLineSegment(sketch, "E380", {"start": v(-31.22, 45.66) * mm, "end": v(-29.12, 45.62) * mm});
            skLineSegment(sketch, "E381", {"start": v(-29.12, 45.62) * mm, "end": v(-26.05, 45.5) * mm});
            skLineSegment(sketch, "E382", {"start": v(-26.05, 45.5) * mm, "end": v(-22.38, 45.21) * mm});
            skLineSegment(sketch, "E383", {"start": v(-22.38, 45.21) * mm, "end": v(-18.44, 44.73) * mm});
            skLineSegment(sketch, "E384", {"start": v(-18.44, 44.73) * mm, "end": v(-14.6, 43.99) * mm});
            skLineSegment(sketch, "E385", {"start": v(-14.6, 43.99) * mm, "end": v(-11.22, 42.93) * mm});
            skLineSegment(sketch, "E386", {"start": v(-11.22, 42.93) * mm, "end": v(-8.64, 41.5) * mm});
            skLineSegment(sketch, "E387", {"start": v(-8.64, 41.5) * mm, "end": v(-8.41, 41.62) * mm});
            skLineSegment(sketch, "E388", {"start": v(-8.41, 41.62) * mm, "end": v(-7.8, 41.98) * mm});
            skLineSegment(sketch, "E389", {"start": v(-7.8, 41.98) * mm, "end": v(-6.94, 42.53) * mm});
            skLineSegment(sketch, "E390", {"start": v(-6.94, 42.53) * mm, "end": v(-5.93, 43.26) * mm});
            skLineSegment(sketch, "E391", {"start": v(-5.93, 43.26) * mm, "end": v(-4.9, 44.14) * mm});
            skLineSegment(sketch, "E392", {"start": v(-4.9, 44.14) * mm, "end": v(-3.95, 45.13) * mm});
            skLineSegment(sketch, "E393", {"start": v(-3.95, 45.13) * mm, "end": v(-3.22, 46.2) * mm});
            skLineSegment(sketch, "E394", {"start": v(-3.22, 46.2) * mm, "end": v(-2.82, 47.34) * mm});
            skLineSegment(sketch, "E395", {"start": v(-2.82, 47.34) * mm, "end": v(-4.14, 48.34) * mm});
            skLineSegment(sketch, "E396", {"start": v(-4.14, 48.34) * mm, "end": v(-8.12, 49) * mm});
            skLineSegment(sketch, "E397", {"start": v(-8.12, 49) * mm, "end": v(-14.17, 49.3) * mm});
            skLineSegment(sketch, "E398", {"start": v(-14.17, 49.3) * mm, "end": v(-21.73, 49.24) * mm});
            skLineSegment(sketch, "E399", {"start": v(-21.73, 49.24) * mm, "end": v(-30.23, 48.78) * mm});
            skLineSegment(sketch, "E400", {"start": v(-30.23, 48.78) * mm, "end": v(-39.08, 47.9) * mm});
            skLineSegment(sketch, "E401", {"start": v(-39.08, 47.9) * mm, "end": v(-47.73, 46.58) * mm});
            skLineSegment(sketch, "E402", {"start": v(-47.73, 46.58) * mm, "end": v(-55.59, 44.81) * mm});
            skLineSegment(sketch, "E403", {"start": v(-55.59, 44.81) * mm, "end": v(-59.53, 43.97) * mm});
            skLineSegment(sketch, "E404", {"start": v(-59.53, 43.97) * mm, "end": v(-64.47, 43.31) * mm});
            skLineSegment(sketch, "E405", {"start": v(-64.47, 43.31) * mm, "end": v(-70.03, 42.91) * mm});
            skLineSegment(sketch, "E406", {"start": v(-70.03, 42.91) * mm, "end": v(-75.81, 42.85) * mm});
            skLineSegment(sketch, "E407", {"start": v(-75.81, 42.85) * mm, "end": v(-81.44, 43.19) * mm});
            skLineSegment(sketch, "E408", {"start": v(-81.44, 43.19) * mm, "end": v(-86.5, 44) * mm});
            skLineSegment(sketch, "E409", {"start": v(-86.5, 44) * mm, "end": v(-90.63, 45.36) * mm});
            skLineSegment(sketch, "E410", {"start": v(-90.63, 45.36) * mm, "end": v(-93.42, 47.34) * mm});
            skLineSegment(sketch, "E411", {"start": v(55.59, 47.59) * mm, "end": v(57.95, 48.29) * mm});
            skLineSegment(sketch, "E412", {"start": v(57.95, 48.29) * mm, "end": v(60.51, 48.8) * mm});
            skLineSegment(sketch, "E413", {"start": v(60.51, 48.8) * mm, "end": v(63.26, 49.16) * mm});
            skLineSegment(sketch, "E414", {"start": v(63.26, 49.16) * mm, "end": v(66.14, 49.4) * mm});
            skLineSegment(sketch, "E415", {"start": v(66.14, 49.4) * mm, "end": v(69.13, 49.57) * mm});
            skLineSegment(sketch, "E416", {"start": v(69.13, 49.57) * mm, "end": v(72.2, 49.68) * mm});
            skLineSegment(sketch, "E417", {"start": v(72.2, 49.68) * mm, "end": v(75.32, 49.78) * mm});
            skLineSegment(sketch, "E418", {"start": v(75.32, 49.78) * mm, "end": v(78.45, 49.9) * mm});
            skLineSegment(sketch, "E419", {"start": v(78.45, 49.9) * mm, "end": v(80.5, 50.17) * mm});
            skLineSegment(sketch, "E420", {"start": v(80.5, 50.17) * mm, "end": v(82.72, 50.67) * mm});
            skLineSegment(sketch, "E421", {"start": v(82.72, 50.67) * mm, "end": v(85.1, 51.25) * mm});
            skLineSegment(sketch, "E422", {"start": v(85.1, 51.25) * mm, "end": v(87.6, 51.77) * mm});
            skLineSegment(sketch, "E423", {"start": v(87.6, 51.77) * mm, "end": v(90.21, 52.08) * mm});
            skLineSegment(sketch, "E424", {"start": v(90.21, 52.08) * mm, "end": v(92.9, 52.03) * mm});
            skLineSegment(sketch, "E425", {"start": v(92.9, 52.03) * mm, "end": v(95.65, 51.47) * mm});
            skLineSegment(sketch, "E426", {"start": v(95.65, 51.47) * mm, "end": v(98.44, 50.25) * mm});
            skLineSegment(sketch, "E427", {"start": v(98.44, 50.25) * mm, "end": v(100.97, 47.25) * mm});
            skLineSegment(sketch, "E428", {"start": v(100.97, 47.25) * mm, "end": v(100.64, 43.38) * mm});
            skLineSegment(sketch, "E429", {"start": v(100.64, 43.38) * mm, "end": v(98.23, 39.02) * mm});
            skLineSegment(sketch, "E430", {"start": v(98.23, 39.02) * mm, "end": v(94.52, 34.57) * mm});
            skLineSegment(sketch, "E431", {"start": v(94.52, 34.57) * mm, "end": v(90.29, 30.43) * mm});
            skLineSegment(sketch, "E432", {"start": v(90.29, 30.43) * mm, "end": v(86.3, 26.98) * mm});
            skLineSegment(sketch, "E433", {"start": v(86.3, 26.98) * mm, "end": v(83.34, 24.62) * mm});
            skLineSegment(sketch, "E434", {"start": v(83.34, 24.62) * mm, "end": v(82.18, 23.75) * mm});
            skLineSegment(sketch, "E435", {"start": v(82.18, 23.75) * mm, "end": v(81.5, 24.36) * mm});
            skLineSegment(sketch, "E436", {"start": v(81.5, 24.36) * mm, "end": v(79.6, 25.96) * mm});
            skLineSegment(sketch, "E437", {"start": v(79.6, 25.96) * mm, "end": v(76.64, 28.23) * mm});
            skLineSegment(sketch, "E438", {"start": v(76.64, 28.23) * mm, "end": v(72.82, 30.82) * mm});
            skLineSegment(sketch, "E439", {"start": v(72.82, 30.82) * mm, "end": v(68.34, 33.4) * mm});
            skLineSegment(sketch, "E440", {"start": v(68.34, 33.4) * mm, "end": v(63.38, 35.65) * mm});
            skLineSegment(sketch, "E441", {"start": v(63.38, 35.65) * mm, "end": v(58.12, 37.22) * mm});
            skLineSegment(sketch, "E442", {"start": v(58.12, 37.22) * mm, "end": v(52.76, 37.78) * mm});
            skLineSegment(sketch, "E443", {"start": v(52.76, 37.78) * mm, "end": v(46.6, 37.52) * mm});
            skLineSegment(sketch, "E444", {"start": v(46.6, 37.52) * mm, "end": v(41.63, 36.97) * mm});
            skLineSegment(sketch, "E445", {"start": v(41.63, 36.97) * mm, "end": v(37.73, 36.22) * mm});
            skLineSegment(sketch, "E446", {"start": v(37.73, 36.22) * mm, "end": v(34.79, 35.38) * mm});
            skLineSegment(sketch, "E447", {"start": v(34.79, 35.38) * mm, "end": v(32.7, 34.54) * mm});
            skLineSegment(sketch, "E448", {"start": v(32.7, 34.54) * mm, "end": v(31.35, 33.82) * mm});
            skLineSegment(sketch, "E449", {"start": v(31.35, 33.82) * mm, "end": v(30.62, 33.31) * mm});
            skLineSegment(sketch, "E450", {"start": v(30.62, 33.31) * mm, "end": v(30.4, 33.12) * mm});
            skLineSegment(sketch, "E451", {"start": v(30.4, 33.12) * mm, "end": v(30.82, 33.64) * mm});
            skLineSegment(sketch, "E452", {"start": v(30.82, 33.64) * mm, "end": v(32.09, 35) * mm});
            skLineSegment(sketch, "E453", {"start": v(32.09, 35) * mm, "end": v(34.22, 36.82) * mm});
            skLineSegment(sketch, "E454", {"start": v(34.22, 36.82) * mm, "end": v(37.24, 38.8) * mm});
            skLineSegment(sketch, "E455", {"start": v(37.24, 38.8) * mm, "end": v(41.16, 40.6) * mm});
            skLineSegment(sketch, "E456", {"start": v(41.16, 40.6) * mm, "end": v(46.02, 41.86) * mm});
            skLineSegment(sketch, "E457", {"start": v(46.02, 41.86) * mm, "end": v(51.81, 42.25) * mm});
            skLineSegment(sketch, "E458", {"start": v(51.81, 42.25) * mm, "end": v(58.57, 41.44) * mm});
            skLineSegment(sketch, "E459", {"start": v(58.57, 41.44) * mm, "end": v(62.24, 40.6) * mm});
            skLineSegment(sketch, "E460", {"start": v(62.24, 40.6) * mm, "end": v(65.44, 39.78) * mm});
            skLineSegment(sketch, "E461", {"start": v(65.44, 39.78) * mm, "end": v(68.3, 39.03) * mm});
            skLineSegment(sketch, "E462", {"start": v(68.3, 39.03) * mm, "end": v(70.9, 38.43) * mm});
            skLineSegment(sketch, "E463", {"start": v(70.9, 38.43) * mm, "end": v(73.4, 38.01) * mm});
            skLineSegment(sketch, "E464", {"start": v(73.4, 38.01) * mm, "end": v(75.9, 37.84) * mm});
            skLineSegment(sketch, "E465", {"start": v(75.9, 37.84) * mm, "end": v(78.52, 37.98) * mm});
            skLineSegment(sketch, "E466", {"start": v(78.52, 37.98) * mm, "end": v(81.38, 38.49) * mm});
            skLineSegment(sketch, "E467", {"start": v(81.38, 38.49) * mm, "end": v(84.39, 39.39) * mm});
            skLineSegment(sketch, "E468", {"start": v(84.39, 39.39) * mm, "end": v(87.29, 40.6) * mm});
            skLineSegment(sketch, "E469", {"start": v(87.29, 40.6) * mm, "end": v(89.96, 42.01) * mm});
            skLineSegment(sketch, "E470", {"start": v(89.96, 42.01) * mm, "end": v(92.27, 43.51) * mm});
            skLineSegment(sketch, "E471", {"start": v(92.27, 43.51) * mm, "end": v(94.09, 44.99) * mm});
            skLineSegment(sketch, "E472", {"start": v(94.09, 44.99) * mm, "end": v(95.29, 46.33) * mm});
            skLineSegment(sketch, "E473", {"start": v(95.29, 46.33) * mm, "end": v(95.74, 47.41) * mm});
            skLineSegment(sketch, "E474", {"start": v(95.74, 47.41) * mm, "end": v(95.32, 48.14) * mm});
            skLineSegment(sketch, "E475", {"start": v(95.32, 48.14) * mm, "end": v(94.32, 48.57) * mm});
            skLineSegment(sketch, "E476", {"start": v(94.32, 48.57) * mm, "end": v(93.13, 48.88) * mm});
            skLineSegment(sketch, "E477", {"start": v(93.13, 48.88) * mm, "end": v(91.7, 49.05) * mm});
            skLineSegment(sketch, "E478", {"start": v(91.7, 49.05) * mm, "end": v(90.03, 49.08) * mm});
            skLineSegment(sketch, "E479", {"start": v(90.03, 49.08) * mm, "end": v(88.08, 48.98) * mm});
            skLineSegment(sketch, "E480", {"start": v(88.08, 48.98) * mm, "end": v(85.83, 48.75) * mm});
            skLineSegment(sketch, "E481", {"start": v(85.83, 48.75) * mm, "end": v(83.25, 48.38) * mm});
            skLineSegment(sketch, "E482", {"start": v(83.25, 48.38) * mm, "end": v(80.3, 47.87) * mm});
            skLineSegment(sketch, "E483", {"start": v(80.3, 47.87) * mm, "end": v(77.58, 47.55) * mm});
            skLineSegment(sketch, "E484", {"start": v(77.58, 47.55) * mm, "end": v(74, 47.37) * mm});
            skLineSegment(sketch, "E485", {"start": v(74, 47.37) * mm, "end": v(69.93, 47.3) * mm});
            skLineSegment(sketch, "E486", {"start": v(69.93, 47.3) * mm, "end": v(65.77, 47.33) * mm});
            skLineSegment(sketch, "E487", {"start": v(65.77, 47.33) * mm, "end": v(61.88, 47.4) * mm});
            skLineSegment(sketch, "E488", {"start": v(61.88, 47.4) * mm, "end": v(58.63, 47.48) * mm});
            skLineSegment(sketch, "E489", {"start": v(58.63, 47.48) * mm, "end": v(56.41, 47.55) * mm});
            skLineSegment(sketch, "E490", {"start": v(56.41, 47.55) * mm, "end": v(55.59, 47.59) * mm});
            skLineSegment(sketch, "E491", {"start": v(93.42, 47.34) * mm, "end": v(93.1, 47.03) * mm});
            skLineSegment(sketch, "E492", {"start": v(93.1, 47.03) * mm, "end": v(92.14, 46.2) * mm});
            skLineSegment(sketch, "E493", {"start": v(92.14, 46.2) * mm, "end": v(90.6, 45.02) * mm});
            skLineSegment(sketch, "E494", {"start": v(90.6, 45.02) * mm, "end": v(88.55, 43.66) * mm});
            skLineSegment(sketch, "E495", {"start": v(88.55, 43.66) * mm, "end": v(86.03, 42.29) * mm});
            skLineSegment(sketch, "E496", {"start": v(86.03, 42.29) * mm, "end": v(83.09, 41.08) * mm});
            skLineSegment(sketch, "E497", {"start": v(83.09, 41.08) * mm, "end": v(79.79, 40.2) * mm});
            skLineSegment(sketch, "E498", {"start": v(79.79, 40.2) * mm, "end": v(76.18, 39.8) * mm});
            skLineSegment(sketch, "E499", {"start": v(76.18, 39.8) * mm, "end": v(71.92, 40.22) * mm});
            skLineSegment(sketch, "E500", {"start": v(71.92, 40.22) * mm, "end": v(66.75, 41.3) * mm});
            skLineSegment(sketch, "E501", {"start": v(66.75, 41.3) * mm, "end": v(60.82, 42.6) * mm});
            skLineSegment(sketch, "E502", {"start": v(60.82, 42.6) * mm, "end": v(54.26, 43.62) * mm});
            skLineSegment(sketch, "E503", {"start": v(54.26, 43.62) * mm, "end": v(47.23, 43.9) * mm});
            skLineSegment(sketch, "E504", {"start": v(47.23, 43.9) * mm, "end": v(39.86, 43) * mm});
            skLineSegment(sketch, "E505", {"start": v(39.86, 43) * mm, "end": v(32.31, 40.4) * mm});
            skLineSegment(sketch, "E506", {"start": v(32.31, 40.4) * mm, "end": v(24.72, 35.65) * mm});
            skLineSegment(sketch, "E507", {"start": v(24.72, 35.65) * mm, "end": v(24.82, 35.99) * mm});
            skLineSegment(sketch, "E508", {"start": v(24.82, 35.99) * mm, "end": v(25.12, 36.9) * mm});
            skLineSegment(sketch, "E509", {"start": v(25.12, 36.9) * mm, "end": v(25.65, 38.23) * mm});
            skLineSegment(sketch, "E510", {"start": v(25.65, 38.23) * mm, "end": v(26.4, 39.82) * mm});
            skLineSegment(sketch, "E511", {"start": v(26.4, 39.82) * mm, "end": v(27.4, 41.52) * mm});
            skLineSegment(sketch, "E512", {"start": v(27.4, 41.52) * mm, "end": v(28.67, 43.16) * mm});
            skLineSegment(sketch, "E513", {"start": v(28.67, 43.16) * mm, "end": v(30.2, 44.6) * mm});
            skLineSegment(sketch, "E514", {"start": v(30.2, 44.6) * mm, "end": v(32, 45.65) * mm});
            skLineSegment(sketch, "E515", {"start": v(32, 45.65) * mm, "end": v(31.22, 45.66) * mm});
            skLineSegment(sketch, "E516", {"start": v(31.22, 45.66) * mm, "end": v(29.12, 45.62) * mm});
            skLineSegment(sketch, "E517", {"start": v(29.12, 45.62) * mm, "end": v(26.05, 45.5) * mm});
            skLineSegment(sketch, "E518", {"start": v(26.05, 45.5) * mm, "end": v(22.38, 45.21) * mm});
            skLineSegment(sketch, "E519", {"start": v(22.38, 45.21) * mm, "end": v(18.44, 44.73) * mm});
            skLineSegment(sketch, "E520", {"start": v(18.44, 44.73) * mm, "end": v(14.6, 43.99) * mm});
            skLineSegment(sketch, "E521", {"start": v(14.6, 43.99) * mm, "end": v(11.22, 42.93) * mm});
            skLineSegment(sketch, "E522", {"start": v(11.22, 42.93) * mm, "end": v(8.64, 41.5) * mm});
            skLineSegment(sketch, "E523", {"start": v(8.64, 41.5) * mm, "end": v(8.4, 41.62) * mm});
            skLineSegment(sketch, "E524", {"start": v(8.4, 41.62) * mm, "end": v(7.8, 41.98) * mm});
            skLineSegment(sketch, "E525", {"start": v(7.8, 41.98) * mm, "end": v(6.94, 42.53) * mm});
            skLineSegment(sketch, "E526", {"start": v(6.94, 42.53) * mm, "end": v(5.93, 43.26) * mm});
            skLineSegment(sketch, "E527", {"start": v(5.93, 43.26) * mm, "end": v(4.9, 44.14) * mm});
            skLineSegment(sketch, "E528", {"start": v(4.9, 44.14) * mm, "end": v(3.95, 45.13) * mm});
            skLineSegment(sketch, "E529", {"start": v(3.95, 45.13) * mm, "end": v(3.22, 46.2) * mm});
            skLineSegment(sketch, "E530", {"start": v(3.22, 46.2) * mm, "end": v(2.82, 47.34) * mm});
            skLineSegment(sketch, "E531", {"start": v(2.82, 47.34) * mm, "end": v(4.14, 48.34) * mm});
            skLineSegment(sketch, "E532", {"start": v(4.14, 48.34) * mm, "end": v(8.12, 49) * mm});
            skLineSegment(sketch, "E533", {"start": v(8.12, 49) * mm, "end": v(14.17, 49.3) * mm});
            skLineSegment(sketch, "E534", {"start": v(14.17, 49.3) * mm, "end": v(21.73, 49.24) * mm});
            skLineSegment(sketch, "E535", {"start": v(21.73, 49.24) * mm, "end": v(30.23, 48.78) * mm});
            skLineSegment(sketch, "E536", {"start": v(30.23, 48.78) * mm, "end": v(39.08, 47.9) * mm});
            skLineSegment(sketch, "E537", {"start": v(39.08, 47.9) * mm, "end": v(47.73, 46.58) * mm});
            skLineSegment(sketch, "E538", {"start": v(47.73, 46.58) * mm, "end": v(55.59, 44.81) * mm});
            skLineSegment(sketch, "E539", {"start": v(55.59, 44.81) * mm, "end": v(59.53, 43.97) * mm});
            skLineSegment(sketch, "E540", {"start": v(59.53, 43.97) * mm, "end": v(64.47, 43.31) * mm});
            skLineSegment(sketch, "E541", {"start": v(64.47, 43.31) * mm, "end": v(70.03, 42.91) * mm});
            skLineSegment(sketch, "E542", {"start": v(70.03, 42.91) * mm, "end": v(75.82, 42.85) * mm});
            skLineSegment(sketch, "E543", {"start": v(75.82, 42.85) * mm, "end": v(81.44, 43.19) * mm});
            skLineSegment(sketch, "E544", {"start": v(81.44, 43.19) * mm, "end": v(86.5, 44) * mm});
            skLineSegment(sketch, "E545", {"start": v(86.5, 44) * mm, "end": v(90.63, 45.36) * mm});
            skLineSegment(sketch, "E546", {"start": v(90.63, 45.36) * mm, "end": v(93.42, 47.34) * mm});
            skLineSegment(sketch, "E547", {"start": v(-7.79, 4.71) * mm, "end": v(-7.01, 4.7) * mm});
            skLineSegment(sketch, "E548", {"start": v(-7.01, 4.7) * mm, "end": v(-6.28, 4.64) * mm});
            skLineSegment(sketch, "E549", {"start": v(-6.28, 4.64) * mm, "end": v(-5.6, 4.54) * mm});
            skLineSegment(sketch, "E550", {"start": v(-5.6, 4.54) * mm, "end": v(-4.96, 4.4) * mm});
            skLineSegment(sketch, "E551", {"start": v(-4.96, 4.4) * mm, "end": v(-4.37, 4.24) * mm});
            skLineSegment(sketch, "E552", {"start": v(-4.37, 4.24) * mm, "end": v(-3.83, 4.03) * mm});
            skLineSegment(sketch, "E553", {"start": v(-3.83, 4.03) * mm, "end": v(-3.34, 3.78) * mm});
            skLineSegment(sketch, "E554", {"start": v(-3.34, 3.78) * mm, "end": v(-2.89, 3.5) * mm});
            skLineSegment(sketch, "E555", {"start": v(-2.89, 3.5) * mm, "end": v(-2.5, 3.16) * mm});
            skLineSegment(sketch, "E556", {"start": v(-2.5, 3.16) * mm, "end": v(-2.15, 2.77) * mm});
            skLineSegment(sketch, "E557", {"start": v(-2.15, 2.77) * mm, "end": v(-1.85, 2.32) * mm});
            skLineSegment(sketch, "E558", {"start": v(-1.85, 2.32) * mm, "end": v(-1.61, 1.81) * mm});
            skLineSegment(sketch, "E559", {"start": v(-1.61, 1.81) * mm, "end": v(-1.43, 1.25) * mm});
            skLineSegment(sketch, "E560", {"start": v(-1.43, 1.25) * mm, "end": v(-1.3, 0.63) * mm});
            skLineSegment(sketch, "E561", {"start": v(-1.3, 0.63) * mm, "end": v(-1.21, -0.06) * mm});
            skLineSegment(sketch, "E562", {"start": v(-1.21, -0.06) * mm, "end": v(-1.19, -0.8) * mm});
            skLineSegment(sketch, "E563", {"start": v(-1.19, -0.8) * mm, "end": v(-1.2, -1.13) * mm});
            skLineSegment(sketch, "E564", {"start": v(-1.2, -1.13) * mm, "end": v(-1.2, -1.44) * mm});
            skLineSegment(sketch, "E565", {"start": v(-1.2, -1.44) * mm, "end": v(-1.22, -1.75) * mm});
            skLineSegment(sketch, "E566", {"start": v(-1.22, -1.75) * mm, "end": v(-1.25, -2.04) * mm});
            skLineSegment(sketch, "E567", {"start": v(-1.25, -2.04) * mm, "end": v(-1.28, -2.32) * mm});
            skLineSegment(sketch, "E568", {"start": v(-1.28, -2.32) * mm, "end": v(-1.32, -2.6) * mm});
            skLineSegment(sketch, "E569", {"start": v(-1.32, -2.6) * mm, "end": v(-1.37, -2.85) * mm});
            skLineSegment(sketch, "E570", {"start": v(-1.37, -2.85) * mm, "end": v(-1.43, -3.09) * mm});
            skLineSegment(sketch, "E571", {"start": v(-1.43, -3.09) * mm, "end": v(-1.5, -3.32) * mm});
            skLineSegment(sketch, "E572", {"start": v(-1.5, -3.32) * mm, "end": v(-1.57, -3.54) * mm});
            skLineSegment(sketch, "E573", {"start": v(-1.57, -3.54) * mm, "end": v(-1.66, -3.74) * mm});
            skLineSegment(sketch, "E574", {"start": v(-1.66, -3.74) * mm, "end": v(-1.77, -3.93) * mm});
            skLineSegment(sketch, "E575", {"start": v(-1.77, -3.93) * mm, "end": v(-1.88, -4.11) * mm});
            skLineSegment(sketch, "E576", {"start": v(-1.88, -4.11) * mm, "end": v(-2, -4.28) * mm});
            skLineSegment(sketch, "E577", {"start": v(-2, -4.28) * mm, "end": v(-2.14, -4.43) * mm});
            skLineSegment(sketch, "E578", {"start": v(-2.14, -4.43) * mm, "end": v(-2.3, -4.58) * mm});
            skLineSegment(sketch, "E579", {"start": v(-2.3, -4.58) * mm, "end": v(-2.45, -4.7) * mm});
            skLineSegment(sketch, "E580", {"start": v(-2.45, -4.7) * mm, "end": v(-2.6, -4.83) * mm});
            skLineSegment(sketch, "E581", {"start": v(-2.6, -4.83) * mm, "end": v(-2.75, -4.94) * mm});
            skLineSegment(sketch, "E582", {"start": v(-2.75, -4.94) * mm, "end": v(-2.9, -5.03) * mm});
            skLineSegment(sketch, "E583", {"start": v(-2.9, -5.03) * mm, "end": v(-3.04, -5.12) * mm});
            skLineSegment(sketch, "E584", {"start": v(-3.04, -5.12) * mm, "end": v(-3.18, -5.2) * mm});
            skLineSegment(sketch, "E585", {"start": v(-3.18, -5.2) * mm, "end": v(-3.32, -5.26) * mm});
            skLineSegment(sketch, "E586", {"start": v(-3.32, -5.26) * mm, "end": v(-3.45, -5.31) * mm});
            skLineSegment(sketch, "E587", {"start": v(-3.45, -5.31) * mm, "end": v(-3.59, -5.36) * mm});
            skLineSegment(sketch, "E588", {"start": v(-3.59, -5.36) * mm, "end": v(-3.74, -5.41) * mm});
            skLineSegment(sketch, "E589", {"start": v(-3.74, -5.41) * mm, "end": v(-3.9, -5.47) * mm});
            skLineSegment(sketch, "E590", {"start": v(-3.9, -5.47) * mm, "end": v(-4.09, -5.52) * mm});
            skLineSegment(sketch, "E591", {"start": v(-4.09, -5.52) * mm, "end": v(-4.28, -5.58) * mm});
            skLineSegment(sketch, "E592", {"start": v(-4.28, -5.58) * mm, "end": v(-4.48, -5.64) * mm});
            skLineSegment(sketch, "E593", {"start": v(-4.48, -5.64) * mm, "end": v(-4.7, -5.7) * mm});
            skLineSegment(sketch, "E594", {"start": v(-4.7, -5.7) * mm, "end": v(-4.94, -5.76) * mm});
            skLineSegment(sketch, "E595", {"start": v(-4.94, -5.76) * mm, "end": v(-4.31, -5.87) * mm});
            skLineSegment(sketch, "E596", {"start": v(-4.31, -5.87) * mm, "end": v(-3.74, -6) * mm});
            skLineSegment(sketch, "E597", {"start": v(-3.74, -6) * mm, "end": v(-3.22, -6.14) * mm});
            skLineSegment(sketch, "E598", {"start": v(-3.22, -6.14) * mm, "end": v(-2.74, -6.3) * mm});
            skLineSegment(sketch, "E599", {"start": v(-2.74, -6.3) * mm, "end": v(-2.32, -6.47) * mm});
            skLineSegment(sketch, "E600", {"start": v(-2.32, -6.47) * mm, "end": v(-1.95, -6.66) * mm});
            skLineSegment(sketch, "E601", {"start": v(-1.95, -6.66) * mm, "end": v(-1.62, -6.86) * mm});
            skLineSegment(sketch, "E602", {"start": v(-1.62, -6.86) * mm, "end": v(-1.35, -7.08) * mm});
            skLineSegment(sketch, "E603", {"start": v(-1.35, -7.08) * mm, "end": v(-1.12, -7.33) * mm});
            skLineSegment(sketch, "E604", {"start": v(-1.12, -7.33) * mm, "end": v(-0.92, -7.63) * mm});
            skLineSegment(sketch, "E605", {"start": v(-0.92, -7.63) * mm, "end": v(-0.75, -7.98) * mm});
            skLineSegment(sketch, "E606", {"start": v(-0.75, -7.98) * mm, "end": v(-0.6, -8.38) * mm});
            skLineSegment(sketch, "E607", {"start": v(-0.6, -8.38) * mm, "end": v(-0.5, -8.84) * mm});
            skLineSegment(sketch, "E608", {"start": v(-0.5, -8.84) * mm, "end": v(-0.42, -9.34) * mm});
            skLineSegment(sketch, "E609", {"start": v(-0.42, -9.34) * mm, "end": v(-0.37, -9.9) * mm});
            skLineSegment(sketch, "E610", {"start": v(-0.37, -9.9) * mm, "end": v(-0.36, -10.5) * mm});
            skLineSegment(sketch, "E611", {"start": v(-0.36, -10.5) * mm, "end": v(-0.38, -11.36) * mm});
            skLineSegment(sketch, "E612", {"start": v(-0.38, -11.36) * mm, "end": v(-0.46, -12.14) * mm});
            skLineSegment(sketch, "E613", {"start": v(-0.46, -12.14) * mm, "end": v(-0.6, -12.85) * mm});
            skLineSegment(sketch, "E614", {"start": v(-0.6, -12.85) * mm, "end": v(-0.79, -13.5) * mm});
            skLineSegment(sketch, "E615", {"start": v(-0.79, -13.5) * mm, "end": v(-1.03, -14.07) * mm});
            skLineSegment(sketch, "E616", {"start": v(-1.03, -14.07) * mm, "end": v(-1.32, -14.57) * mm});
            skLineSegment(sketch, "E617", {"start": v(-1.32, -14.57) * mm, "end": v(-1.67, -15) * mm});
            skLineSegment(sketch, "E618", {"start": v(-1.67, -15) * mm, "end": v(-2.07, -15.36) * mm});
            skLineSegment(sketch, "E619", {"start": v(-2.07, -15.36) * mm, "end": v(-2.53, -15.66) * mm});
            skLineSegment(sketch, "E620", {"start": v(-2.53, -15.66) * mm, "end": v(-3.05, -15.93) * mm});
            skLineSegment(sketch, "E621", {"start": v(-3.05, -15.93) * mm, "end": v(-3.63, -16.15) * mm});
            skLineSegment(sketch, "E622", {"start": v(-3.63, -16.15) * mm, "end": v(-4.28, -16.33) * mm});
            skLineSegment(sketch, "E623", {"start": v(-4.28, -16.33) * mm, "end": v(-4.98, -16.47) * mm});
            skLineSegment(sketch, "E624", {"start": v(-4.98, -16.47) * mm, "end": v(-5.75, -16.57) * mm});
            skLineSegment(sketch, "E625", {"start": v(-5.75, -16.57) * mm, "end": v(-6.58, -16.64) * mm});
            skLineSegment(sketch, "E626", {"start": v(-6.58, -16.64) * mm, "end": v(-7.47, -16.66) * mm});
            skLineSegment(sketch, "E627", {"start": v(-7.47, -16.66) * mm, "end": v(-10.04, -16.66) * mm});
            skLineSegment(sketch, "E628", {"start": v(-10.04, -16.66) * mm, "end": v(-12.62, -16.66) * mm});
            skLineSegment(sketch, "E629", {"start": v(-12.62, -16.66) * mm, "end": v(-15.2, -16.66) * mm});
            skLineSegment(sketch, "E630", {"start": v(-15.2, -16.66) * mm, "end": v(-17.77, -16.66) * mm});
            skLineSegment(sketch, "E631", {"start": v(-17.77, -16.66) * mm, "end": v(-20.34, -16.66) * mm});
            skLineSegment(sketch, "E632", {"start": v(-20.34, -16.66) * mm, "end": v(-22.92, -16.66) * mm});
            skLineSegment(sketch, "E633", {"start": v(-22.92, -16.66) * mm, "end": v(-25.5, -16.66) * mm});
            skLineSegment(sketch, "E634", {"start": v(-25.5, -16.66) * mm, "end": v(-28.07, -16.66) * mm});
            skLineSegment(sketch, "E635", {"start": v(-28.07, -16.66) * mm, "end": v(-28.07, -13.98) * mm});
            skLineSegment(sketch, "E636", {"start": v(-28.07, -13.98) * mm, "end": v(-28.07, -11.31) * mm});
            skLineSegment(sketch, "E637", {"start": v(-28.07, -11.31) * mm, "end": v(-28.07, -8.64) * mm});
            skLineSegment(sketch, "E638", {"start": v(-28.07, -8.64) * mm, "end": v(-28.07, -5.97) * mm});
            skLineSegment(sketch, "E639", {"start": v(-28.07, -5.97) * mm, "end": v(-28.07, -3.3) * mm});
            skLineSegment(sketch, "E640", {"start": v(-28.07, -3.3) * mm, "end": v(-28.07, -0.63) * mm});
            skLineSegment(sketch, "E641", {"start": v(-28.07, -0.63) * mm, "end": v(-28.07, 2.04) * mm});
            skLineSegment(sketch, "E642", {"start": v(-28.07, 2.04) * mm, "end": v(-28.07, 4.71) * mm});
            skLineSegment(sketch, "E643", {"start": v(-28.07, 4.71) * mm, "end": v(-25.53, 4.71) * mm});
            skLineSegment(sketch, "E644", {"start": v(-25.53, 4.71) * mm, "end": v(-23, 4.71) * mm});
            skLineSegment(sketch, "E645", {"start": v(-23, 4.71) * mm, "end": v(-20.46, 4.71) * mm});
            skLineSegment(sketch, "E646", {"start": v(-20.46, 4.71) * mm, "end": v(-17.93, 4.71) * mm});
            skLineSegment(sketch, "E647", {"start": v(-17.93, 4.71) * mm, "end": v(-15.4, 4.71) * mm});
            skLineSegment(sketch, "E648", {"start": v(-15.4, 4.71) * mm, "end": v(-12.86, 4.71) * mm});
            skLineSegment(sketch, "E649", {"start": v(-12.86, 4.71) * mm, "end": v(-10.32, 4.71) * mm});
            skLineSegment(sketch, "E650", {"start": v(-10.32, 4.71) * mm, "end": v(-7.79, 4.71) * mm});
            skLineSegment(sketch, "E651", {"start": v(-7.76, -1.76) * mm, "end": v(-7.77, -1.5) * mm});
            skLineSegment(sketch, "E652", {"start": v(-7.77, -1.5) * mm, "end": v(-7.8, -1.26) * mm});
            skLineSegment(sketch, "E653", {"start": v(-7.8, -1.26) * mm, "end": v(-7.84, -1.05) * mm});
            skLineSegment(sketch, "E654", {"start": v(-7.84, -1.05) * mm, "end": v(-7.91, -0.85) * mm});
            skLineSegment(sketch, "E655", {"start": v(-7.91, -0.85) * mm, "end": v(-8, -0.68) * mm});
            skLineSegment(sketch, "E656", {"start": v(-8, -0.68) * mm, "end": v(-8.1, -0.54) * mm});
            skLineSegment(sketch, "E657", {"start": v(-8.1, -0.54) * mm, "end": v(-8.24, -0.42) * mm});
            skLineSegment(sketch, "E658", {"start": v(-8.24, -0.42) * mm, "end": v(-8.38, -0.32) * mm});
            skLineSegment(sketch, "E659", {"start": v(-8.38, -0.32) * mm, "end": v(-8.55, -0.23) * mm});
            skLineSegment(sketch, "E660", {"start": v(-8.55, -0.23) * mm, "end": v(-8.73, -0.16) * mm});
            skLineSegment(sketch, "E661", {"start": v(-8.73, -0.16) * mm, "end": v(-8.93, -0.1) * mm});
            skLineSegment(sketch, "E662", {"start": v(-8.93, -0.1) * mm, "end": v(-9.16, -0.05) * mm});
            skLineSegment(sketch, "E663", {"start": v(-9.16, -0.05) * mm, "end": v(-9.4, -0.01) * mm});
            skLineSegment(sketch, "E664", {"start": v(-9.4, -0.01) * mm, "end": v(-9.65, 0.01) * mm});
            skLineSegment(sketch, "E665", {"start": v(-9.65, 0.01) * mm, "end": v(-9.93, 0.03) * mm});
            skLineSegment(sketch, "E666", {"start": v(-9.93, 0.03) * mm, "end": v(-10.23, 0.04) * mm});
            skLineSegment(sketch, "E667", {"start": v(-10.23, 0.04) * mm, "end": v(-11.64, 0.04) * mm});
            skLineSegment(sketch, "E668", {"start": v(-11.64, 0.04) * mm, "end": v(-13.06, 0.04) * mm});
            skLineSegment(sketch, "E669", {"start": v(-13.06, 0.04) * mm, "end": v(-14.48, 0.04) * mm});
            skLineSegment(sketch, "E670", {"start": v(-14.48, 0.04) * mm, "end": v(-15.9, 0.04) * mm});
            skLineSegment(sketch, "E671", {"start": v(-15.9, 0.04) * mm, "end": v(-17.31, 0.04) * mm});
            skLineSegment(sketch, "E672", {"start": v(-17.31, 0.04) * mm, "end": v(-18.73, 0.04) * mm});
            skLineSegment(sketch, "E673", {"start": v(-18.73, 0.04) * mm, "end": v(-20.15, 0.04) * mm});
            skLineSegment(sketch, "E674", {"start": v(-20.15, 0.04) * mm, "end": v(-21.56, 0.04) * mm});
            skLineSegment(sketch, "E675", {"start": v(-21.56, 0.04) * mm, "end": v(-21.56, -0.43) * mm});
            skLineSegment(sketch, "E676", {"start": v(-21.56, -0.43) * mm, "end": v(-21.56, -0.9) * mm});
            skLineSegment(sketch, "E677", {"start": v(-21.56, -0.9) * mm, "end": v(-21.56, -1.36) * mm});
            skLineSegment(sketch, "E678", {"start": v(-21.56, -1.36) * mm, "end": v(-21.56, -1.82) * mm});
            skLineSegment(sketch, "E679", {"start": v(-21.56, -1.82) * mm, "end": v(-21.56, -2.29) * mm});
            skLineSegment(sketch, "E680", {"start": v(-21.56, -2.29) * mm, "end": v(-21.56, -2.75) * mm});
            skLineSegment(sketch, "E681", {"start": v(-21.56, -2.75) * mm, "end": v(-21.56, -3.21) * mm});
            skLineSegment(sketch, "E682", {"start": v(-21.56, -3.21) * mm, "end": v(-21.56, -3.68) * mm});
            skLineSegment(sketch, "E683", {"start": v(-21.56, -3.68) * mm, "end": v(-20.16, -3.68) * mm});
            skLineSegment(sketch, "E684", {"start": v(-20.16, -3.68) * mm, "end": v(-18.76, -3.68) * mm});
            skLineSegment(sketch, "E685", {"start": v(-18.76, -3.68) * mm, "end": v(-17.36, -3.68) * mm});
            skLineSegment(sketch, "E686", {"start": v(-17.36, -3.68) * mm, "end": v(-15.96, -3.68) * mm});
            skLineSegment(sketch, "E687", {"start": v(-15.96, -3.68) * mm, "end": v(-14.56, -3.68) * mm});
            skLineSegment(sketch, "E688", {"start": v(-14.56, -3.68) * mm, "end": v(-13.16, -3.68) * mm});
            skLineSegment(sketch, "E689", {"start": v(-13.16, -3.68) * mm, "end": v(-11.76, -3.68) * mm});
            skLineSegment(sketch, "E690", {"start": v(-11.76, -3.68) * mm, "end": v(-10.35, -3.68) * mm});
            skLineSegment(sketch, "E691", {"start": v(-10.35, -3.68) * mm, "end": v(-10.04, -3.67) * mm});
            skLineSegment(sketch, "E692", {"start": v(-10.04, -3.67) * mm, "end": v(-9.75, -3.66) * mm});
            skLineSegment(sketch, "E693", {"start": v(-9.75, -3.66) * mm, "end": v(-9.48, -3.63) * mm});
            skLineSegment(sketch, "E694", {"start": v(-9.48, -3.63) * mm, "end": v(-9.23, -3.6) * mm});
            skLineSegment(sketch, "E695", {"start": v(-9.23, -3.6) * mm, "end": v(-9, -3.54) * mm});
            skLineSegment(sketch, "E696", {"start": v(-9, -3.54) * mm, "end": v(-8.78, -3.48) * mm});
            skLineSegment(sketch, "E697", {"start": v(-8.78, -3.48) * mm, "end": v(-8.59, -3.4) * mm});
            skLineSegment(sketch, "E698", {"start": v(-8.59, -3.4) * mm, "end": v(-8.41, -3.33) * mm});
            skLineSegment(sketch, "E699", {"start": v(-8.41, -3.33) * mm, "end": v(-8.26, -3.23) * mm});
            skLineSegment(sketch, "E700", {"start": v(-8.26, -3.23) * mm, "end": v(-8.13, -3.1) * mm});
            skLineSegment(sketch, "E701", {"start": v(-8.13, -3.1) * mm, "end": v(-8.01, -2.94) * mm});
            skLineSegment(sketch, "E702", {"start": v(-8.01, -2.94) * mm, "end": v(-7.92, -2.76) * mm});
            skLineSegment(sketch, "E703", {"start": v(-7.92, -2.76) * mm, "end": v(-7.85, -2.55) * mm});
            skLineSegment(sketch, "E704", {"start": v(-7.85, -2.55) * mm, "end": v(-7.8, -2.31) * mm});
            skLineSegment(sketch, "E705", {"start": v(-7.8, -2.31) * mm, "end": v(-7.77, -2.05) * mm});
            skLineSegment(sketch, "E706", {"start": v(-7.77, -2.05) * mm, "end": v(-7.76, -1.76) * mm});
            skLineSegment(sketch, "E707", {"start": v(-6.9, -9.74) * mm, "end": v(-6.9, -9.53) * mm});
            skLineSegment(sketch, "E708", {"start": v(-6.9, -9.53) * mm, "end": v(-6.93, -9.33) * mm});
            skLineSegment(sketch, "E709", {"start": v(-6.93, -9.33) * mm, "end": v(-6.97, -9.14) * mm});
            skLineSegment(sketch, "E710", {"start": v(-6.97, -9.14) * mm, "end": v(-7.03, -8.97) * mm});
            skLineSegment(sketch, "E711", {"start": v(-7.03, -8.97) * mm, "end": v(-7.11, -8.8) * mm});
            skLineSegment(sketch, "E712", {"start": v(-7.11, -8.8) * mm, "end": v(-7.2, -8.66) * mm});
            skLineSegment(sketch, "E713", {"start": v(-7.2, -8.66) * mm, "end": v(-7.32, -8.52) * mm});
            skLineSegment(sketch, "E714", {"start": v(-7.32, -8.52) * mm, "end": v(-7.45, -8.4) * mm});
            skLineSegment(sketch, "E715", {"start": v(-7.45, -8.4) * mm, "end": v(-7.61, -8.28) * mm});
            skLineSegment(sketch, "E716", {"start": v(-7.61, -8.28) * mm, "end": v(-7.8, -8.18) * mm});
            skLineSegment(sketch, "E717", {"start": v(-7.8, -8.18) * mm, "end": v(-8.03, -8.1) * mm});
            skLineSegment(sketch, "E718", {"start": v(-8.03, -8.1) * mm, "end": v(-8.28, -8.03) * mm});
            skLineSegment(sketch, "E719", {"start": v(-8.28, -8.03) * mm, "end": v(-8.57, -7.98) * mm});
            skLineSegment(sketch, "E720", {"start": v(-8.57, -7.98) * mm, "end": v(-8.9, -7.94) * mm});
            skLineSegment(sketch, "E721", {"start": v(-8.9, -7.94) * mm, "end": v(-9.26, -7.92) * mm});
            skLineSegment(sketch, "E722", {"start": v(-9.26, -7.92) * mm, "end": v(-9.65, -7.9) * mm});
            skLineSegment(sketch, "E723", {"start": v(-9.65, -7.9) * mm, "end": v(-11.14, -7.9) * mm});
            skLineSegment(sketch, "E724", {"start": v(-11.14, -7.9) * mm, "end": v(-12.63, -7.9) * mm});
            skLineSegment(sketch, "E725", {"start": v(-12.63, -7.9) * mm, "end": v(-14.12, -7.9) * mm});
            skLineSegment(sketch, "E726", {"start": v(-14.12, -7.9) * mm, "end": v(-15.6, -7.9) * mm});
            skLineSegment(sketch, "E727", {"start": v(-15.6, -7.9) * mm, "end": v(-17.1, -7.9) * mm});
            skLineSegment(sketch, "E728", {"start": v(-17.1, -7.9) * mm, "end": v(-18.58, -7.9) * mm});
            skLineSegment(sketch, "E729", {"start": v(-18.58, -7.9) * mm, "end": v(-20.07, -7.9) * mm});
            skLineSegment(sketch, "E730", {"start": v(-20.07, -7.9) * mm, "end": v(-21.56, -7.9) * mm});
            skLineSegment(sketch, "E731", {"start": v(-21.56, -7.9) * mm, "end": v(-21.56, -8.4) * mm});
            skLineSegment(sketch, "E732", {"start": v(-21.56, -8.4) * mm, "end": v(-21.56, -8.89) * mm});
            skLineSegment(sketch, "E733", {"start": v(-21.56, -8.89) * mm, "end": v(-21.56, -9.38) * mm});
            skLineSegment(sketch, "E734", {"start": v(-21.56, -9.38) * mm, "end": v(-21.56, -9.86) * mm});
            skLineSegment(sketch, "E735", {"start": v(-21.56, -9.86) * mm, "end": v(-21.56, -10.35) * mm});
            skLineSegment(sketch, "E736", {"start": v(-21.56, -10.35) * mm, "end": v(-21.56, -10.84) * mm});
            skLineSegment(sketch, "E737", {"start": v(-21.56, -10.84) * mm, "end": v(-21.56, -11.33) * mm});
            skLineSegment(sketch, "E738", {"start": v(-21.56, -11.33) * mm, "end": v(-21.56, -11.82) * mm});
            skLineSegment(sketch, "E739", {"start": v(-21.56, -11.82) * mm, "end": v(-20.09, -11.82) * mm});
            skLineSegment(sketch, "E740", {"start": v(-20.09, -11.82) * mm, "end": v(-18.6, -11.82) * mm});
            skLineSegment(sketch, "E741", {"start": v(-18.6, -11.82) * mm, "end": v(-17.13, -11.82) * mm});
            skLineSegment(sketch, "E742", {"start": v(-17.13, -11.82) * mm, "end": v(-15.65, -11.82) * mm});
            skLineSegment(sketch, "E743", {"start": v(-15.65, -11.82) * mm, "end": v(-14.18, -11.82) * mm});
            skLineSegment(sketch, "E744", {"start": v(-14.18, -11.82) * mm, "end": v(-12.7, -11.82) * mm});
            skLineSegment(sketch, "E745", {"start": v(-12.7, -11.82) * mm, "end": v(-11.22, -11.82) * mm});
            skLineSegment(sketch, "E746", {"start": v(-11.22, -11.82) * mm, "end": v(-9.74, -11.82) * mm});
            skLineSegment(sketch, "E747", {"start": v(-9.74, -11.82) * mm, "end": v(-9.47, -11.82) * mm});
            skLineSegment(sketch, "E748", {"start": v(-9.47, -11.82) * mm, "end": v(-9.2, -11.8) * mm});
            skLineSegment(sketch, "E749", {"start": v(-9.2, -11.8) * mm, "end": v(-8.94, -11.79) * mm});
            skLineSegment(sketch, "E750", {"start": v(-8.94, -11.79) * mm, "end": v(-8.69, -11.76) * mm});
            skLineSegment(sketch, "E751", {"start": v(-8.69, -11.76) * mm, "end": v(-8.44, -11.72) * mm});
            skLineSegment(sketch, "E752", {"start": v(-8.44, -11.72) * mm, "end": v(-8.2, -11.68) * mm});
            skLineSegment(sketch, "E753", {"start": v(-8.2, -11.68) * mm, "end": v(-7.98, -11.63) * mm});
            skLineSegment(sketch, "E754", {"start": v(-7.98, -11.63) * mm, "end": v(-7.76, -11.58) * mm});
            skLineSegment(sketch, "E755", {"start": v(-7.76, -11.58) * mm, "end": v(-7.55, -11.5) * mm});
            skLineSegment(sketch, "E756", {"start": v(-7.55, -11.5) * mm, "end": v(-7.38, -11.37) * mm});
            skLineSegment(sketch, "E757", {"start": v(-7.38, -11.37) * mm, "end": v(-7.23, -11.2) * mm});
            skLineSegment(sketch, "E758", {"start": v(-7.23, -11.2) * mm, "end": v(-7.1, -11) * mm});
            skLineSegment(sketch, "E759", {"start": v(-7.1, -11) * mm, "end": v(-7.02, -10.75) * mm});
            skLineSegment(sketch, "E760", {"start": v(-7.02, -10.75) * mm, "end": v(-6.95, -10.45) * mm});
            skLineSegment(sketch, "E761", {"start": v(-6.95, -10.45) * mm, "end": v(-6.9, -10.12) * mm});
            skLineSegment(sketch, "E762", {"start": v(-6.9, -10.12) * mm, "end": v(-6.9, -9.74) * mm});
            skLineSegment(sketch, "E763", {"start": v(-7.47, -18.12) * mm, "end": v(-10.23, -18.12) * mm});
            skLineSegment(sketch, "E764", {"start": v(-10.23, -18.12) * mm, "end": v(-12.99, -18.12) * mm});
            skLineSegment(sketch, "E765", {"start": v(-12.99, -18.12) * mm, "end": v(-15.74, -18.12) * mm});
            skLineSegment(sketch, "E766", {"start": v(-15.74, -18.12) * mm, "end": v(-18.5, -18.12) * mm});
            skLineSegment(sketch, "E767", {"start": v(-18.5, -18.12) * mm, "end": v(-21.26, -18.12) * mm});
            skLineSegment(sketch, "E768", {"start": v(-21.26, -18.12) * mm, "end": v(-24.02, -18.12) * mm});
            skLineSegment(sketch, "E769", {"start": v(-24.02, -18.12) * mm, "end": v(-26.78, -18.12) * mm});
            skLineSegment(sketch, "E770", {"start": v(-26.78, -18.12) * mm, "end": v(-29.54, -18.12) * mm});
            skLineSegment(sketch, "E771", {"start": v(-29.54, -18.12) * mm, "end": v(-29.54, -15.08) * mm});
            skLineSegment(sketch, "E772", {"start": v(-29.54, -15.08) * mm, "end": v(-29.54, -12.05) * mm});
            skLineSegment(sketch, "E773", {"start": v(-29.54, -12.05) * mm, "end": v(-29.54, -9) * mm});
            skLineSegment(sketch, "E774", {"start": v(-29.54, -9) * mm, "end": v(-29.54, -5.97) * mm});
            skLineSegment(sketch, "E775", {"start": v(-29.54, -5.97) * mm, "end": v(-29.54, -2.93) * mm});
            skLineSegment(sketch, "E776", {"start": v(-29.54, -2.93) * mm, "end": v(-29.54, 0.1) * mm});
            skLineSegment(sketch, "E777", {"start": v(-29.54, 0.1) * mm, "end": v(-29.54, 3.14) * mm});
            skLineSegment(sketch, "E778", {"start": v(-29.54, 3.14) * mm, "end": v(-29.54, 6.18) * mm});
            skLineSegment(sketch, "E779", {"start": v(-29.54, 6.18) * mm, "end": v(-26.82, 6.18) * mm});
            skLineSegment(sketch, "E780", {"start": v(-26.82, 6.18) * mm, "end": v(-24.1, 6.18) * mm});
            skLineSegment(sketch, "E781", {"start": v(-24.1, 6.18) * mm, "end": v(-21.38, 6.18) * mm});
            skLineSegment(sketch, "E782", {"start": v(-21.38, 6.18) * mm, "end": v(-18.66, 6.18) * mm});
            skLineSegment(sketch, "E783", {"start": v(-18.66, 6.18) * mm, "end": v(-15.94, 6.18) * mm});
            skLineSegment(sketch, "E784", {"start": v(-15.94, 6.18) * mm, "end": v(-13.23, 6.18) * mm});
            skLineSegment(sketch, "E785", {"start": v(-13.23, 6.18) * mm, "end": v(-10.5, 6.18) * mm});
            skLineSegment(sketch, "E786", {"start": v(-10.5, 6.18) * mm, "end": v(-7.79, 6.18) * mm});
            skLineSegment(sketch, "E787", {"start": v(-7.79, 6.18) * mm, "end": v(-6.9, 6.16) * mm});
            skLineSegment(sketch, "E788", {"start": v(-6.9, 6.16) * mm, "end": v(-6.06, 6.09) * mm});
            skLineSegment(sketch, "E789", {"start": v(-6.06, 6.09) * mm, "end": v(-5.26, 5.97) * mm});
            skLineSegment(sketch, "E790", {"start": v(-5.26, 5.97) * mm, "end": v(-4.52, 5.8) * mm});
            skLineSegment(sketch, "E791", {"start": v(-4.52, 5.8) * mm, "end": v(-3.82, 5.6) * mm});
            skLineSegment(sketch, "E792", {"start": v(-3.82, 5.6) * mm, "end": v(-3.17, 5.34) * mm});
            skLineSegment(sketch, "E793", {"start": v(-3.17, 5.34) * mm, "end": v(-2.58, 5.04) * mm});
            skLineSegment(sketch, "E794", {"start": v(-2.58, 5.04) * mm, "end": v(-2.03, 4.69) * mm});
            skLineSegment(sketch, "E795", {"start": v(-2.03, 4.69) * mm, "end": v(-1.5, 4.24) * mm});
            skLineSegment(sketch, "E796", {"start": v(-1.5, 4.24) * mm, "end": v(-1.03, 3.73) * mm});
            skLineSegment(sketch, "E797", {"start": v(-1.03, 3.73) * mm, "end": v(-0.63, 3.14) * mm});
            skLineSegment(sketch, "E798", {"start": v(-0.63, 3.14) * mm, "end": v(-0.3, 2.49) * mm});
            skLineSegment(sketch, "E799", {"start": v(-0.3, 2.49) * mm, "end": v(-0.05, 1.77) * mm});
            skLineSegment(sketch, "E800", {"start": v(-0.05, 1.77) * mm, "end": v(0.13, 0.98) * mm});
            skLineSegment(sketch, "E801", {"start": v(0.13, 0.98) * mm, "end": v(0.24, 0.12) * mm});
            skLineSegment(sketch, "E802", {"start": v(0.24, 0.12) * mm, "end": v(0.28, -0.8) * mm});
            skLineSegment(sketch, "E803", {"start": v(0.28, -0.8) * mm, "end": v(0.27, -1.17) * mm});
            skLineSegment(sketch, "E804", {"start": v(0.27, -1.17) * mm, "end": v(0.26, -1.53) * mm});
            skLineSegment(sketch, "E805", {"start": v(0.26, -1.53) * mm, "end": v(0.24, -1.88) * mm});
            skLineSegment(sketch, "E806", {"start": v(0.24, -1.88) * mm, "end": v(0.2, -2.22) * mm});
            skLineSegment(sketch, "E807", {"start": v(0.2, -2.22) * mm, "end": v(0.17, -2.54) * mm});
            skLineSegment(sketch, "E808", {"start": v(0.17, -2.54) * mm, "end": v(0.12, -2.86) * mm});
            skLineSegment(sketch, "E809", {"start": v(0.12, -2.86) * mm, "end": v(0.06, -3.16) * mm});
            skLineSegment(sketch, "E810", {"start": v(0.06, -3.16) * mm, "end": v(0, -3.45) * mm});
            skLineSegment(sketch, "E811", {"start": v(0, -3.45) * mm, "end": v(-0.1, -3.74) * mm});
            skLineSegment(sketch, "E812", {"start": v(-0.1, -3.74) * mm, "end": v(-0.2, -4.03) * mm});
            skLineSegment(sketch, "E813", {"start": v(-0.2, -4.03) * mm, "end": v(-0.3, -4.3) * mm});
            skLineSegment(sketch, "E814", {"start": v(-0.3, -4.3) * mm, "end": v(-0.43, -4.56) * mm});
            skLineSegment(sketch, "E815", {"start": v(-0.43, -4.56) * mm, "end": v(-0.58, -4.8) * mm});
            skLineSegment(sketch, "E816", {"start": v(-0.58, -4.8) * mm, "end": v(-0.74, -5.03) * mm});
            skLineSegment(sketch, "E817", {"start": v(-0.74, -5.03) * mm, "end": v(-0.9, -5.25) * mm});
            skLineSegment(sketch, "E818", {"start": v(-0.9, -5.25) * mm, "end": v(-1.1, -5.46) * mm});
            skLineSegment(sketch, "E819", {"start": v(-1.1, -5.46) * mm, "end": v(-1, -5.52) * mm});
            skLineSegment(sketch, "E820", {"start": v(-1, -5.52) * mm, "end": v(-0.9, -5.58) * mm});
            skLineSegment(sketch, "E821", {"start": v(-0.9, -5.58) * mm, "end": v(-0.8, -5.65) * mm});
            skLineSegment(sketch, "E822", {"start": v(-0.8, -5.65) * mm, "end": v(-0.7, -5.71) * mm});
            skLineSegment(sketch, "E823", {"start": v(-0.7, -5.71) * mm, "end": v(-0.62, -5.78) * mm});
            skLineSegment(sketch, "E824", {"start": v(-0.62, -5.78) * mm, "end": v(-0.53, -5.85) * mm});
            skLineSegment(sketch, "E825", {"start": v(-0.53, -5.85) * mm, "end": v(-0.45, -5.92) * mm});
            skLineSegment(sketch, "E826", {"start": v(-0.45, -5.92) * mm, "end": v(-0.37, -5.99) * mm});
            skLineSegment(sketch, "E827", {"start": v(-0.37, -5.99) * mm, "end": v(-0.02, -6.35) * mm});
            skLineSegment(sketch, "E828", {"start": v(-0.02, -6.35) * mm, "end": v(0.28, -6.77) * mm});
            skLineSegment(sketch, "E829", {"start": v(0.28, -6.77) * mm, "end": v(0.54, -7.25) * mm});
            skLineSegment(sketch, "E830", {"start": v(0.54, -7.25) * mm, "end": v(0.74, -7.78) * mm});
            skLineSegment(sketch, "E831", {"start": v(0.74, -7.78) * mm, "end": v(0.9, -8.37) * mm});
            skLineSegment(sketch, "E832", {"start": v(0.9, -8.37) * mm, "end": v(1.02, -9.02) * mm});
            skLineSegment(sketch, "E833", {"start": v(1.02, -9.02) * mm, "end": v(1.09, -9.73) * mm});
            skLineSegment(sketch, "E834", {"start": v(1.09, -9.73) * mm, "end": v(1.11, -10.5) * mm});
            skLineSegment(sketch, "E835", {"start": v(1.11, -10.5) * mm, "end": v(1.07, -11.53) * mm});
            skLineSegment(sketch, "E836", {"start": v(1.07, -11.53) * mm, "end": v(0.97, -12.48) * mm});
            skLineSegment(sketch, "E837", {"start": v(0.97, -12.48) * mm, "end": v(0.79, -13.36) * mm});
            skLineSegment(sketch, "E838", {"start": v(0.79, -13.36) * mm, "end": v(0.53, -14.15) * mm});
            skLineSegment(sketch, "E839", {"start": v(0.53, -14.15) * mm, "end": v(0.2, -14.87) * mm});
            skLineSegment(sketch, "E840", {"start": v(0.2, -14.87) * mm, "end": v(-0.18, -15.5) * mm});
            skLineSegment(sketch, "E841", {"start": v(-0.18, -15.5) * mm, "end": v(-0.65, -16.06) * mm});
            skLineSegment(sketch, "E842", {"start": v(-0.65, -16.06) * mm, "end": v(-1.18, -16.53) * mm});
            skLineSegment(sketch, "E843", {"start": v(-1.18, -16.53) * mm, "end": v(-1.75, -16.9) * mm});
            skLineSegment(sketch, "E844", {"start": v(-1.75, -16.9) * mm, "end": v(-2.37, -17.23) * mm});
            skLineSegment(sketch, "E845", {"start": v(-2.37, -17.23) * mm, "end": v(-3.06, -17.5) * mm});
            skLineSegment(sketch, "E846", {"start": v(-3.06, -17.5) * mm, "end": v(-3.8, -17.73) * mm});
            skLineSegment(sketch, "E847", {"start": v(-3.8, -17.73) * mm, "end": v(-4.62, -17.9) * mm});
            skLineSegment(sketch, "E848", {"start": v(-4.62, -17.9) * mm, "end": v(-5.5, -18.02) * mm});
            skLineSegment(sketch, "E849", {"start": v(-5.5, -18.02) * mm, "end": v(-6.45, -18.1) * mm});
            skLineSegment(sketch, "E850", {"start": v(-6.45, -18.1) * mm, "end": v(-7.47, -18.12) * mm});
            skLineSegment(sketch, "E851", {"start": v(-26.6, -15.19) * mm, "end": v(-24.21, -15.19) * mm});
            skLineSegment(sketch, "E852", {"start": v(-24.21, -15.19) * mm, "end": v(-21.82, -15.19) * mm});
            skLineSegment(sketch, "E853", {"start": v(-21.82, -15.19) * mm, "end": v(-19.43, -15.19) * mm});
            skLineSegment(sketch, "E854", {"start": v(-19.43, -15.19) * mm, "end": v(-17.04, -15.19) * mm});
            skLineSegment(sketch, "E855", {"start": v(-17.04, -15.19) * mm, "end": v(-14.64, -15.19) * mm});
            skLineSegment(sketch, "E856", {"start": v(-14.64, -15.19) * mm, "end": v(-12.25, -15.19) * mm});
            skLineSegment(sketch, "E857", {"start": v(-12.25, -15.19) * mm, "end": v(-9.86, -15.19) * mm});
            skLineSegment(sketch, "E858", {"start": v(-9.86, -15.19) * mm, "end": v(-7.47, -15.19) * mm});
            skLineSegment(sketch, "E859", {"start": v(-7.47, -15.19) * mm, "end": v(-6.71, -15.17) * mm});
            skLineSegment(sketch, "E860", {"start": v(-6.71, -15.17) * mm, "end": v(-6, -15.12) * mm});
            skLineSegment(sketch, "E861", {"start": v(-6, -15.12) * mm, "end": v(-5.35, -15.04) * mm});
            skLineSegment(sketch, "E862", {"start": v(-5.35, -15.04) * mm, "end": v(-4.75, -14.93) * mm});
            skLineSegment(sketch, "E863", {"start": v(-4.75, -14.93) * mm, "end": v(-4.21, -14.8) * mm});
            skLineSegment(sketch, "E864", {"start": v(-4.21, -14.8) * mm, "end": v(-3.73, -14.62) * mm});
            skLineSegment(sketch, "E865", {"start": v(-3.73, -14.62) * mm, "end": v(-3.31, -14.42) * mm});
            skLineSegment(sketch, "E866", {"start": v(-3.31, -14.42) * mm, "end": v(-2.96, -14.19) * mm});
            skLineSegment(sketch, "E867", {"start": v(-2.96, -14.19) * mm, "end": v(-2.64, -13.88) * mm});
            skLineSegment(sketch, "E868", {"start": v(-2.64, -13.88) * mm, "end": v(-2.38, -13.5) * mm});
            skLineSegment(sketch, "E869", {"start": v(-2.38, -13.5) * mm, "end": v(-2.19, -13.05) * mm});
            skLineSegment(sketch, "E870", {"start": v(-2.19, -13.05) * mm, "end": v(-2.04, -12.56) * mm});
            skLineSegment(sketch, "E871", {"start": v(-2.04, -12.56) * mm, "end": v(-1.94, -12.05) * mm});
            skLineSegment(sketch, "E872", {"start": v(-1.94, -12.05) * mm, "end": v(-1.87, -11.53) * mm});
            skLineSegment(sketch, "E873", {"start": v(-1.87, -11.53) * mm, "end": v(-1.84, -11) * mm});
            skLineSegment(sketch, "E874", {"start": v(-1.84, -11) * mm, "end": v(-1.83, -10.5) * mm});
            skLineSegment(sketch, "E875", {"start": v(-1.83, -10.5) * mm, "end": v(-1.84, -10.02) * mm});
            skLineSegment(sketch, "E876", {"start": v(-1.84, -10.02) * mm, "end": v(-1.87, -9.59) * mm});
            skLineSegment(sketch, "E877", {"start": v(-1.87, -9.59) * mm, "end": v(-1.92, -9.21) * mm});
            skLineSegment(sketch, "E878", {"start": v(-1.92, -9.21) * mm, "end": v(-1.99, -8.9) * mm});
            skLineSegment(sketch, "E879", {"start": v(-1.99, -8.9) * mm, "end": v(-2.06, -8.64) * mm});
            skLineSegment(sketch, "E880", {"start": v(-2.06, -8.64) * mm, "end": v(-2.15, -8.43) * mm});
            skLineSegment(sketch, "E881", {"start": v(-2.15, -8.43) * mm, "end": v(-2.24, -8.27) * mm});
            skLineSegment(sketch, "E882", {"start": v(-2.24, -8.27) * mm, "end": v(-2.33, -8.17) * mm});
            skLineSegment(sketch, "E883", {"start": v(-2.33, -8.17) * mm, "end": v(-2.45, -8.07) * mm});
            skLineSegment(sketch, "E884", {"start": v(-2.45, -8.07) * mm, "end": v(-2.62, -7.96) * mm});
            skLineSegment(sketch, "E885", {"start": v(-2.62, -7.96) * mm, "end": v(-2.84, -7.84) * mm});
            skLineSegment(sketch, "E886", {"start": v(-2.84, -7.84) * mm, "end": v(-3.14, -7.72) * mm});
            skLineSegment(sketch, "E887", {"start": v(-3.14, -7.72) * mm, "end": v(-3.51, -7.59) * mm});
            skLineSegment(sketch, "E888", {"start": v(-3.51, -7.59) * mm, "end": v(-3.97, -7.46) * mm});
            skLineSegment(sketch, "E889", {"start": v(-3.97, -7.46) * mm, "end": v(-4.52, -7.33) * mm});
            skLineSegment(sketch, "E890", {"start": v(-4.52, -7.33) * mm, "end": v(-5.17, -7.21) * mm});
            skLineSegment(sketch, "E891", {"start": v(-5.17, -7.21) * mm, "end": v(-5.19, -6.85) * mm});
            skLineSegment(sketch, "E892", {"start": v(-5.19, -6.85) * mm, "end": v(-5.2, -6.5) * mm});
            skLineSegment(sketch, "E893", {"start": v(-5.2, -6.5) * mm, "end": v(-5.22, -6.14) * mm});
            skLineSegment(sketch, "E894", {"start": v(-5.22, -6.14) * mm, "end": v(-5.24, -5.78) * mm});
            skLineSegment(sketch, "E895", {"start": v(-5.24, -5.78) * mm, "end": v(-5.26, -5.42) * mm});
            skLineSegment(sketch, "E896", {"start": v(-5.26, -5.42) * mm, "end": v(-5.28, -5.06) * mm});
            skLineSegment(sketch, "E897", {"start": v(-5.28, -5.06) * mm, "end": v(-5.3, -4.7) * mm});
            skLineSegment(sketch, "E898", {"start": v(-5.3, -4.7) * mm, "end": v(-5.31, -4.34) * mm});
            skLineSegment(sketch, "E899", {"start": v(-5.31, -4.34) * mm, "end": v(-5.06, -4.28) * mm});
            skLineSegment(sketch, "E900", {"start": v(-5.06, -4.28) * mm, "end": v(-4.83, -4.21) * mm});
            skLineSegment(sketch, "E901", {"start": v(-4.83, -4.21) * mm, "end": v(-4.63, -4.15) * mm});
            skLineSegment(sketch, "E902", {"start": v(-4.63, -4.15) * mm, "end": v(-4.45, -4.1) * mm});
            skLineSegment(sketch, "E903", {"start": v(-4.45, -4.1) * mm, "end": v(-4.3, -4.05) * mm});
            skLineSegment(sketch, "E904", {"start": v(-4.3, -4.05) * mm, "end": v(-4.16, -4) * mm});
            skLineSegment(sketch, "E905", {"start": v(-4.16, -4) * mm, "end": v(-4.04, -3.97) * mm});
            skLineSegment(sketch, "E906", {"start": v(-4.04, -3.97) * mm, "end": v(-3.95, -3.93) * mm});
            skLineSegment(sketch, "E907", {"start": v(-3.95, -3.93) * mm, "end": v(-3.9, -3.92) * mm});
            skLineSegment(sketch, "E908", {"start": v(-3.9, -3.92) * mm, "end": v(-3.85, -3.9) * mm});
            skLineSegment(sketch, "E909", {"start": v(-3.85, -3.9) * mm, "end": v(-3.78, -3.86) * mm});
            skLineSegment(sketch, "E910", {"start": v(-3.78, -3.86) * mm, "end": v(-3.7, -3.8) * mm});
            skLineSegment(sketch, "E911", {"start": v(-3.7, -3.8) * mm, "end": v(-3.61, -3.75) * mm});
            skLineSegment(sketch, "E912", {"start": v(-3.61, -3.75) * mm, "end": v(-3.5, -3.67) * mm});
            skLineSegment(sketch, "E913", {"start": v(-3.5, -3.67) * mm, "end": v(-3.4, -3.58) * mm});
            skLineSegment(sketch, "E914", {"start": v(-3.4, -3.58) * mm, "end": v(-3.26, -3.47) * mm});
            skLineSegment(sketch, "E915", {"start": v(-3.26, -3.47) * mm, "end": v(-3.2, -3.4) * mm});
            skLineSegment(sketch, "E916", {"start": v(-3.2, -3.4) * mm, "end": v(-3.13, -3.33) * mm});
            skLineSegment(sketch, "E917", {"start": v(-3.13, -3.33) * mm, "end": v(-3.07, -3.25) * mm});
            skLineSegment(sketch, "E918", {"start": v(-3.07, -3.25) * mm, "end": v(-3.02, -3.16) * mm});
            skLineSegment(sketch, "E919", {"start": v(-3.02, -3.16) * mm, "end": v(-2.97, -3.06) * mm});
            skLineSegment(sketch, "E920", {"start": v(-2.97, -3.06) * mm, "end": v(-2.92, -2.96) * mm});
            skLineSegment(sketch, "E921", {"start": v(-2.92, -2.96) * mm, "end": v(-2.88, -2.85) * mm});
            skLineSegment(sketch, "E922", {"start": v(-2.88, -2.85) * mm, "end": v(-2.85, -2.72) * mm});
            skLineSegment(sketch, "E923", {"start": v(-2.85, -2.72) * mm, "end": v(-2.8, -2.53) * mm});
            skLineSegment(sketch, "E924", {"start": v(-2.8, -2.53) * mm, "end": v(-2.77, -2.32) * mm});
            skLineSegment(sketch, "E925", {"start": v(-2.77, -2.32) * mm, "end": v(-2.73, -2.1) * mm});
            skLineSegment(sketch, "E926", {"start": v(-2.73, -2.1) * mm, "end": v(-2.7, -1.86) * mm});
            skLineSegment(sketch, "E927", {"start": v(-2.7, -1.86) * mm, "end": v(-2.68, -1.6) * mm});
            skLineSegment(sketch, "E928", {"start": v(-2.68, -1.6) * mm, "end": v(-2.67, -1.35) * mm});
            skLineSegment(sketch, "E929", {"start": v(-2.67, -1.35) * mm, "end": v(-2.66, -1.08) * mm});
            skLineSegment(sketch, "E930", {"start": v(-2.66, -1.08) * mm, "end": v(-2.66, -0.8) * mm});
            skLineSegment(sketch, "E931", {"start": v(-2.66, -0.8) * mm, "end": v(-2.67, -0.24) * mm});
            skLineSegment(sketch, "E932", {"start": v(-2.67, -0.24) * mm, "end": v(-2.72, 0.27) * mm});
            skLineSegment(sketch, "E933", {"start": v(-2.72, 0.27) * mm, "end": v(-2.8, 0.73) * mm});
            skLineSegment(sketch, "E934", {"start": v(-2.8, 0.73) * mm, "end": v(-2.93, 1.14) * mm});
            skLineSegment(sketch, "E935", {"start": v(-2.93, 1.14) * mm, "end": v(-3.08, 1.5) * mm});
            skLineSegment(sketch, "E936", {"start": v(-3.08, 1.5) * mm, "end": v(-3.27, 1.82) * mm});
            skLineSegment(sketch, "E937", {"start": v(-3.27, 1.82) * mm, "end": v(-3.49, 2.08) * mm});
            skLineSegment(sketch, "E938", {"start": v(-3.49, 2.08) * mm, "end": v(-3.74, 2.3) * mm});
            skLineSegment(sketch, "E939", {"start": v(-3.74, 2.3) * mm, "end": v(-4.1, 2.52) * mm});
            skLineSegment(sketch, "E940", {"start": v(-4.1, 2.52) * mm, "end": v(-4.49, 2.71) * mm});
            skLineSegment(sketch, "E941", {"start": v(-4.49, 2.71) * mm, "end": v(-4.93, 2.88) * mm});
            skLineSegment(sketch, "E942", {"start": v(-4.93, 2.88) * mm, "end": v(-5.41, 3) * mm});
            skLineSegment(sketch, "E943", {"start": v(-5.41, 3) * mm, "end": v(-5.94, 3.11) * mm});
            skLineSegment(sketch, "E944", {"start": v(-5.94, 3.11) * mm, "end": v(-6.52, 3.19) * mm});
            skLineSegment(sketch, "E945", {"start": v(-6.52, 3.19) * mm, "end": v(-7.13, 3.23) * mm});
            skLineSegment(sketch, "E946", {"start": v(-7.13, 3.23) * mm, "end": v(-7.79, 3.25) * mm});
            skLineSegment(sketch, "E947", {"start": v(-7.79, 3.25) * mm, "end": v(-10.14, 3.25) * mm});
            skLineSegment(sketch, "E948", {"start": v(-10.14, 3.25) * mm, "end": v(-12.5, 3.25) * mm});
            skLineSegment(sketch, "E949", {"start": v(-12.5, 3.25) * mm, "end": v(-14.84, 3.25) * mm});
            skLineSegment(sketch, "E950", {"start": v(-14.84, 3.25) * mm, "end": v(-17.2, 3.25) * mm});
            skLineSegment(sketch, "E951", {"start": v(-17.2, 3.25) * mm, "end": v(-19.55, 3.25) * mm});
            skLineSegment(sketch, "E952", {"start": v(-19.55, 3.25) * mm, "end": v(-21.9, 3.25) * mm});
            skLineSegment(sketch, "E953", {"start": v(-21.9, 3.25) * mm, "end": v(-24.25, 3.25) * mm});
            skLineSegment(sketch, "E954", {"start": v(-24.25, 3.25) * mm, "end": v(-26.6, 3.25) * mm});
            skLineSegment(sketch, "E955", {"start": v(-26.6, 3.25) * mm, "end": v(-26.6, 0.94) * mm});
            skLineSegment(sketch, "E956", {"start": v(-26.6, 0.94) * mm, "end": v(-26.6, -1.36) * mm});
            skLineSegment(sketch, "E957", {"start": v(-26.6, -1.36) * mm, "end": v(-26.6, -3.67) * mm});
            skLineSegment(sketch, "E958", {"start": v(-26.6, -3.67) * mm, "end": v(-26.6, -5.97) * mm});
            skLineSegment(sketch, "E959", {"start": v(-26.6, -5.97) * mm, "end": v(-26.6, -8.28) * mm});
            skLineSegment(sketch, "E960", {"start": v(-26.6, -8.28) * mm, "end": v(-26.6, -10.58) * mm});
            skLineSegment(sketch, "E961", {"start": v(-26.6, -10.58) * mm, "end": v(-26.6, -12.88) * mm});
            skLineSegment(sketch, "E962", {"start": v(-26.6, -12.88) * mm, "end": v(-26.6, -15.19) * mm});
            skLineSegment(sketch, "E963", {"start": v(-9.74, -13.29) * mm, "end": v(-11.4, -13.29) * mm});
            skLineSegment(sketch, "E964", {"start": v(-11.4, -13.29) * mm, "end": v(-13.07, -13.29) * mm});
            skLineSegment(sketch, "E965", {"start": v(-13.07, -13.29) * mm, "end": v(-14.73, -13.29) * mm});
            skLineSegment(sketch, "E966", {"start": v(-14.73, -13.29) * mm, "end": v(-16.39, -13.29) * mm});
            skLineSegment(sketch, "E967", {"start": v(-16.39, -13.29) * mm, "end": v(-18.05, -13.29) * mm});
            skLineSegment(sketch, "E968", {"start": v(-18.05, -13.29) * mm, "end": v(-19.7, -13.29) * mm});
            skLineSegment(sketch, "E969", {"start": v(-19.7, -13.29) * mm, "end": v(-21.37, -13.29) * mm});
            skLineSegment(sketch, "E970", {"start": v(-21.37, -13.29) * mm, "end": v(-23.03, -13.29) * mm});
            skLineSegment(sketch, "E971", {"start": v(-23.03, -13.29) * mm, "end": v(-23.03, -12.43) * mm});
            skLineSegment(sketch, "E972", {"start": v(-23.03, -12.43) * mm, "end": v(-23.03, -11.58) * mm});
            skLineSegment(sketch, "E973", {"start": v(-23.03, -11.58) * mm, "end": v(-23.03, -10.72) * mm});
            skLineSegment(sketch, "E974", {"start": v(-23.03, -10.72) * mm, "end": v(-23.03, -9.86) * mm});
            skLineSegment(sketch, "E975", {"start": v(-23.03, -9.86) * mm, "end": v(-23.03, -9) * mm});
            skLineSegment(sketch, "E976", {"start": v(-23.03, -9) * mm, "end": v(-23.03, -8.15) * mm});
            skLineSegment(sketch, "E977", {"start": v(-23.03, -8.15) * mm, "end": v(-23.03, -7.3) * mm});
            skLineSegment(sketch, "E978", {"start": v(-23.03, -7.3) * mm, "end": v(-23.03, -6.44) * mm});
            skLineSegment(sketch, "E979", {"start": v(-23.03, -6.44) * mm, "end": v(-21.36, -6.44) * mm});
            skLineSegment(sketch, "E980", {"start": v(-21.36, -6.44) * mm, "end": v(-19.69, -6.44) * mm});
            skLineSegment(sketch, "E981", {"start": v(-19.69, -6.44) * mm, "end": v(-18.01, -6.44) * mm});
            skLineSegment(sketch, "E982", {"start": v(-18.01, -6.44) * mm, "end": v(-16.34, -6.44) * mm});
            skLineSegment(sketch, "E983", {"start": v(-16.34, -6.44) * mm, "end": v(-14.67, -6.44) * mm});
            skLineSegment(sketch, "E984", {"start": v(-14.67, -6.44) * mm, "end": v(-13, -6.44) * mm});
            skLineSegment(sketch, "E985", {"start": v(-13, -6.44) * mm, "end": v(-11.32, -6.44) * mm});
            skLineSegment(sketch, "E986", {"start": v(-11.32, -6.44) * mm, "end": v(-9.65, -6.44) * mm});
            skLineSegment(sketch, "E987", {"start": v(-9.65, -6.44) * mm, "end": v(-9.11, -6.45) * mm});
            skLineSegment(sketch, "E988", {"start": v(-9.11, -6.45) * mm, "end": v(-8.62, -6.5) * mm});
            skLineSegment(sketch, "E989", {"start": v(-8.62, -6.5) * mm, "end": v(-8.17, -6.56) * mm});
            skLineSegment(sketch, "E990", {"start": v(-8.17, -6.56) * mm, "end": v(-7.76, -6.65) * mm});
            skLineSegment(sketch, "E991", {"start": v(-7.76, -6.65) * mm, "end": v(-7.4, -6.76) * mm});
            skLineSegment(sketch, "E992", {"start": v(-7.4, -6.76) * mm, "end": v(-7.06, -6.9) * mm});
            skLineSegment(sketch, "E993", {"start": v(-7.06, -6.9) * mm, "end": v(-6.76, -7.08) * mm});
            skLineSegment(sketch, "E994", {"start": v(-6.76, -7.08) * mm, "end": v(-6.5, -7.28) * mm});
            skLineSegment(sketch, "E995", {"start": v(-6.5, -7.28) * mm, "end": v(-6.31, -7.45) * mm});
            skLineSegment(sketch, "E996", {"start": v(-6.31, -7.45) * mm, "end": v(-6.12, -7.66) * mm});
            skLineSegment(sketch, "E997", {"start": v(-6.12, -7.66) * mm, "end": v(-5.94, -7.9) * mm});
            skLineSegment(sketch, "E998", {"start": v(-5.94, -7.9) * mm, "end": v(-5.78, -8.19) * mm});
            skLineSegment(sketch, "E999", {"start": v(-5.78, -8.19) * mm, "end": v(-5.64, -8.5) * mm});
            skLineSegment(sketch, "E1000", {"start": v(-5.64, -8.5) * mm, "end": v(-5.53, -8.87) * mm});
            skLineSegment(sketch, "E1001", {"start": v(-5.53, -8.87) * mm, "end": v(-5.45, -9.28) * mm});
            skLineSegment(sketch, "E1002", {"start": v(-5.45, -9.28) * mm, "end": v(-5.43, -9.74) * mm});
            skLineSegment(sketch, "E1003", {"start": v(-5.43, -9.74) * mm, "end": v(-5.48, -10.55) * mm});
            skLineSegment(sketch, "E1004", {"start": v(-5.48, -10.55) * mm, "end": v(-5.63, -11.22) * mm});
            skLineSegment(sketch, "E1005", {"start": v(-5.63, -11.22) * mm, "end": v(-5.85, -11.75) * mm});
            skLineSegment(sketch, "E1006", {"start": v(-5.85, -11.75) * mm, "end": v(-6.12, -12.18) * mm});
            skLineSegment(sketch, "E1007", {"start": v(-6.12, -12.18) * mm, "end": v(-6.43, -12.5) * mm});
            skLineSegment(sketch, "E1008", {"start": v(-6.43, -12.5) * mm, "end": v(-6.76, -12.73) * mm});
            skLineSegment(sketch, "E1009", {"start": v(-6.76, -12.73) * mm, "end": v(-7.08, -12.9) * mm});
            skLineSegment(sketch, "E1010", {"start": v(-7.08, -12.9) * mm, "end": v(-7.37, -13) * mm});
            skLineSegment(sketch, "E1011", {"start": v(-7.37, -13) * mm, "end": v(-7.63, -13.06) * mm});
            skLineSegment(sketch, "E1012", {"start": v(-7.63, -13.06) * mm, "end": v(-7.9, -13.12) * mm});
            skLineSegment(sketch, "E1013", {"start": v(-7.9, -13.12) * mm, "end": v(-8.2, -13.17) * mm});
            skLineSegment(sketch, "E1014", {"start": v(-8.2, -13.17) * mm, "end": v(-8.49, -13.21) * mm});
            skLineSegment(sketch, "E1015", {"start": v(-8.49, -13.21) * mm, "end": v(-8.8, -13.25) * mm});
            skLineSegment(sketch, "E1016", {"start": v(-8.8, -13.25) * mm, "end": v(-9.1, -13.27) * mm});
            skLineSegment(sketch, "E1017", {"start": v(-9.1, -13.27) * mm, "end": v(-9.42, -13.28) * mm});
            skLineSegment(sketch, "E1018", {"start": v(-9.42, -13.28) * mm, "end": v(-9.74, -13.29) * mm});
            skLineSegment(sketch, "E1019", {"start": v(-20.1, -10.35) * mm, "end": v(-18.8, -10.35) * mm});
            skLineSegment(sketch, "E1020", {"start": v(-18.8, -10.35) * mm, "end": v(-17.5, -10.35) * mm});
            skLineSegment(sketch, "E1021", {"start": v(-17.5, -10.35) * mm, "end": v(-16.21, -10.35) * mm});
            skLineSegment(sketch, "E1022", {"start": v(-16.21, -10.35) * mm, "end": v(-14.92, -10.35) * mm});
            skLineSegment(sketch, "E1023", {"start": v(-14.92, -10.35) * mm, "end": v(-13.63, -10.35) * mm});
            skLineSegment(sketch, "E1024", {"start": v(-13.63, -10.35) * mm, "end": v(-12.33, -10.35) * mm});
            skLineSegment(sketch, "E1025", {"start": v(-12.33, -10.35) * mm, "end": v(-11.04, -10.35) * mm});
            skLineSegment(sketch, "E1026", {"start": v(-11.04, -10.35) * mm, "end": v(-9.74, -10.35) * mm});
            skLineSegment(sketch, "E1027", {"start": v(-9.74, -10.35) * mm, "end": v(-9.56, -10.35) * mm});
            skLineSegment(sketch, "E1028", {"start": v(-9.56, -10.35) * mm, "end": v(-9.38, -10.34) * mm});
            skLineSegment(sketch, "E1029", {"start": v(-9.38, -10.34) * mm, "end": v(-9.2, -10.33) * mm});
            skLineSegment(sketch, "E1030", {"start": v(-9.2, -10.33) * mm, "end": v(-9.03, -10.32) * mm});
            skLineSegment(sketch, "E1031", {"start": v(-9.03, -10.32) * mm, "end": v(-8.86, -10.3) * mm});
            skLineSegment(sketch, "E1032", {"start": v(-8.86, -10.3) * mm, "end": v(-8.7, -10.28) * mm});
            skLineSegment(sketch, "E1033", {"start": v(-8.7, -10.28) * mm, "end": v(-8.55, -10.25) * mm});
            skLineSegment(sketch, "E1034", {"start": v(-8.55, -10.25) * mm, "end": v(-8.4, -10.22) * mm});
            skLineSegment(sketch, "E1035", {"start": v(-8.4, -10.22) * mm, "end": v(-8.39, -10.18) * mm});
            skLineSegment(sketch, "E1036", {"start": v(-8.39, -10.18) * mm, "end": v(-8.38, -10.14) * mm});
            skLineSegment(sketch, "E1037", {"start": v(-8.38, -10.14) * mm, "end": v(-8.38, -10.09) * mm});
            skLineSegment(sketch, "E1038", {"start": v(-8.38, -10.09) * mm, "end": v(-8.37, -10.03) * mm});
            skLineSegment(sketch, "E1039", {"start": v(-8.37, -10.03) * mm, "end": v(-8.37, -9.97) * mm});
            skLineSegment(sketch, "E1040", {"start": v(-8.37, -9.97) * mm, "end": v(-8.36, -9.9) * mm});
            skLineSegment(sketch, "E1041", {"start": v(-8.36, -9.9) * mm, "end": v(-8.36, -9.82) * mm});
            skLineSegment(sketch, "E1042", {"start": v(-8.36, -9.82) * mm, "end": v(-8.36, -9.74) * mm});
            skLineSegment(sketch, "E1043", {"start": v(-8.36, -9.74) * mm, "end": v(-8.36, -9.71) * mm});
            skLineSegment(sketch, "E1044", {"start": v(-8.36, -9.71) * mm, "end": v(-8.36, -9.69) * mm});
            skLineSegment(sketch, "E1045", {"start": v(-8.36, -9.69) * mm, "end": v(-8.36, -9.66) * mm});
            skLineSegment(sketch, "E1046", {"start": v(-8.36, -9.66) * mm, "end": v(-8.37, -9.63) * mm});
            skLineSegment(sketch, "E1047", {"start": v(-8.37, -9.63) * mm, "end": v(-8.37, -9.6) * mm});
            skLineSegment(sketch, "E1048", {"start": v(-8.37, -9.6) * mm, "end": v(-8.38, -9.57) * mm});
            skLineSegment(sketch, "E1049", {"start": v(-8.38, -9.57) * mm, "end": v(-8.38, -9.54) * mm});
            skLineSegment(sketch, "E1050", {"start": v(-8.38, -9.54) * mm, "end": v(-8.4, -9.52) * mm});
            skLineSegment(sketch, "E1051", {"start": v(-8.4, -9.52) * mm, "end": v(-8.44, -9.5) * mm});
            skLineSegment(sketch, "E1052", {"start": v(-8.44, -9.5) * mm, "end": v(-8.5, -9.48) * mm});
            skLineSegment(sketch, "E1053", {"start": v(-8.5, -9.48) * mm, "end": v(-8.6, -9.46) * mm});
            skLineSegment(sketch, "E1054", {"start": v(-8.6, -9.46) * mm, "end": v(-8.74, -9.44) * mm});
            skLineSegment(sketch, "E1055", {"start": v(-8.74, -9.44) * mm, "end": v(-8.9, -9.41) * mm});
            skLineSegment(sketch, "E1056", {"start": v(-8.9, -9.41) * mm, "end": v(-9.11, -9.4) * mm});
            skLineSegment(sketch, "E1057", {"start": v(-9.11, -9.4) * mm, "end": v(-9.36, -9.38) * mm});
            skLineSegment(sketch, "E1058", {"start": v(-9.36, -9.38) * mm, "end": v(-9.65, -9.38) * mm});
            skLineSegment(sketch, "E1059", {"start": v(-9.65, -9.38) * mm, "end": v(-10.95, -9.38) * mm});
            skLineSegment(sketch, "E1060", {"start": v(-10.95, -9.38) * mm, "end": v(-12.26, -9.38) * mm});
            skLineSegment(sketch, "E1061", {"start": v(-12.26, -9.38) * mm, "end": v(-13.57, -9.38) * mm});
            skLineSegment(sketch, "E1062", {"start": v(-13.57, -9.38) * mm, "end": v(-14.87, -9.38) * mm});
            skLineSegment(sketch, "E1063", {"start": v(-14.87, -9.38) * mm, "end": v(-16.18, -9.38) * mm});
            skLineSegment(sketch, "E1064", {"start": v(-16.18, -9.38) * mm, "end": v(-17.48, -9.38) * mm});
            skLineSegment(sketch, "E1065", {"start": v(-17.48, -9.38) * mm, "end": v(-18.8, -9.38) * mm});
            skLineSegment(sketch, "E1066", {"start": v(-18.8, -9.38) * mm, "end": v(-20.1, -9.38) * mm});
            skLineSegment(sketch, "E1067", {"start": v(-20.1, -9.38) * mm, "end": v(-20.1, -9.5) * mm});
            skLineSegment(sketch, "E1068", {"start": v(-20.1, -9.5) * mm, "end": v(-20.1, -9.62) * mm});
            skLineSegment(sketch, "E1069", {"start": v(-20.1, -9.62) * mm, "end": v(-20.1, -9.74) * mm});
            skLineSegment(sketch, "E1070", {"start": v(-20.1, -9.74) * mm, "end": v(-20.1, -9.86) * mm});
            skLineSegment(sketch, "E1071", {"start": v(-20.1, -9.86) * mm, "end": v(-20.1, -9.99) * mm});
            skLineSegment(sketch, "E1072", {"start": v(-20.1, -9.99) * mm, "end": v(-20.1, -10.1) * mm});
            skLineSegment(sketch, "E1073", {"start": v(-20.1, -10.1) * mm, "end": v(-20.1, -10.23) * mm});
            skLineSegment(sketch, "E1074", {"start": v(-20.1, -10.23) * mm, "end": v(-20.1, -10.35) * mm});
            skLineSegment(sketch, "E1075", {"start": v(-10.35, -5.15) * mm, "end": v(-11.94, -5.15) * mm});
            skLineSegment(sketch, "E1076", {"start": v(-11.94, -5.15) * mm, "end": v(-13.52, -5.15) * mm});
            skLineSegment(sketch, "E1077", {"start": v(-13.52, -5.15) * mm, "end": v(-15.1, -5.15) * mm});
            skLineSegment(sketch, "E1078", {"start": v(-15.1, -5.15) * mm, "end": v(-16.7, -5.15) * mm});
            skLineSegment(sketch, "E1079", {"start": v(-16.7, -5.15) * mm, "end": v(-18.28, -5.15) * mm});
            skLineSegment(sketch, "E1080", {"start": v(-18.28, -5.15) * mm, "end": v(-19.86, -5.15) * mm});
            skLineSegment(sketch, "E1081", {"start": v(-19.86, -5.15) * mm, "end": v(-21.45, -5.15) * mm});
            skLineSegment(sketch, "E1082", {"start": v(-21.45, -5.15) * mm, "end": v(-23.03, -5.15) * mm});
            skLineSegment(sketch, "E1083", {"start": v(-23.03, -5.15) * mm, "end": v(-23.03, -4.32) * mm});
            skLineSegment(sketch, "E1084", {"start": v(-23.03, -4.32) * mm, "end": v(-23.03, -3.49) * mm});
            skLineSegment(sketch, "E1085", {"start": v(-23.03, -3.49) * mm, "end": v(-23.03, -2.65) * mm});
            skLineSegment(sketch, "E1086", {"start": v(-23.03, -2.65) * mm, "end": v(-23.03, -1.82) * mm});
            skLineSegment(sketch, "E1087", {"start": v(-23.03, -1.82) * mm, "end": v(-23.03, -1) * mm});
            skLineSegment(sketch, "E1088", {"start": v(-23.03, -1) * mm, "end": v(-23.03, -0.16) * mm});
            skLineSegment(sketch, "E1089", {"start": v(-23.03, -0.16) * mm, "end": v(-23.03, 0.67) * mm});
            skLineSegment(sketch, "E1090", {"start": v(-23.03, 0.67) * mm, "end": v(-23.03, 1.5) * mm});
            skLineSegment(sketch, "E1091", {"start": v(-23.03, 1.5) * mm, "end": v(-21.43, 1.5) * mm});
            skLineSegment(sketch, "E1092", {"start": v(-21.43, 1.5) * mm, "end": v(-19.83, 1.5) * mm});
            skLineSegment(sketch, "E1093", {"start": v(-19.83, 1.5) * mm, "end": v(-18.23, 1.5) * mm});
            skLineSegment(sketch, "E1094", {"start": v(-18.23, 1.5) * mm, "end": v(-16.63, 1.5) * mm});
            skLineSegment(sketch, "E1095", {"start": v(-16.63, 1.5) * mm, "end": v(-15.03, 1.5) * mm});
            skLineSegment(sketch, "E1096", {"start": v(-15.03, 1.5) * mm, "end": v(-13.43, 1.5) * mm});
            skLineSegment(sketch, "E1097", {"start": v(-13.43, 1.5) * mm, "end": v(-11.83, 1.5) * mm});
            skLineSegment(sketch, "E1098", {"start": v(-11.83, 1.5) * mm, "end": v(-10.23, 1.5) * mm});
            skLineSegment(sketch, "E1099", {"start": v(-10.23, 1.5) * mm, "end": v(-9.83, 1.5) * mm});
            skLineSegment(sketch, "E1100", {"start": v(-9.83, 1.5) * mm, "end": v(-9.46, 1.47) * mm});
            skLineSegment(sketch, "E1101", {"start": v(-9.46, 1.47) * mm, "end": v(-9.11, 1.43) * mm});
            skLineSegment(sketch, "E1102", {"start": v(-9.11, 1.43) * mm, "end": v(-8.78, 1.37) * mm});
            skLineSegment(sketch, "E1103", {"start": v(-8.78, 1.37) * mm, "end": v(-8.47, 1.3) * mm});
            skLineSegment(sketch, "E1104", {"start": v(-8.47, 1.3) * mm, "end": v(-8.18, 1.2) * mm});
            skLineSegment(sketch, "E1105", {"start": v(-8.18, 1.2) * mm, "end": v(-7.91, 1.09) * mm});
            skLineSegment(sketch, "E1106", {"start": v(-7.91, 1.09) * mm, "end": v(-7.66, 0.96) * mm});
            skLineSegment(sketch, "E1107", {"start": v(-7.66, 0.96) * mm, "end": v(-7.42, 0.81) * mm});
            skLineSegment(sketch, "E1108", {"start": v(-7.42, 0.81) * mm, "end": v(-7.18, 0.62) * mm});
            skLineSegment(sketch, "E1109", {"start": v(-7.18, 0.62) * mm, "end": v(-6.95, 0.37) * mm});
            skLineSegment(sketch, "E1110", {"start": v(-6.95, 0.37) * mm, "end": v(-6.74, 0.07) * mm});
            skLineSegment(sketch, "E1111", {"start": v(-6.74, 0.07) * mm, "end": v(-6.56, -0.28) * mm});
            skLineSegment(sketch, "E1112", {"start": v(-6.56, -0.28) * mm, "end": v(-6.42, -0.7) * mm});
            skLineSegment(sketch, "E1113", {"start": v(-6.42, -0.7) * mm, "end": v(-6.32, -1.2) * mm});
            skLineSegment(sketch, "E1114", {"start": v(-6.32, -1.2) * mm, "end": v(-6.29, -1.76) * mm});
            skLineSegment(sketch, "E1115", {"start": v(-6.29, -1.76) * mm, "end": v(-6.32, -2.36) * mm});
            skLineSegment(sketch, "E1116", {"start": v(-6.32, -2.36) * mm, "end": v(-6.42, -2.89) * mm});
            skLineSegment(sketch, "E1117", {"start": v(-6.42, -2.89) * mm, "end": v(-6.57, -3.33) * mm});
            skLineSegment(sketch, "E1118", {"start": v(-6.57, -3.33) * mm, "end": v(-6.76, -3.7) * mm});
            skLineSegment(sketch, "E1119", {"start": v(-6.76, -3.7) * mm, "end": v(-6.98, -4.02) * mm});
            skLineSegment(sketch, "E1120", {"start": v(-6.98, -4.02) * mm, "end": v(-7.22, -4.27) * mm});
            skLineSegment(sketch, "E1121", {"start": v(-7.22, -4.27) * mm, "end": v(-7.47, -4.47) * mm});
            skLineSegment(sketch, "E1122", {"start": v(-7.47, -4.47) * mm, "end": v(-7.72, -4.62) * mm});
            skLineSegment(sketch, "E1123", {"start": v(-7.72, -4.62) * mm, "end": v(-7.98, -4.75) * mm});
            skLineSegment(sketch, "E1124", {"start": v(-7.98, -4.75) * mm, "end": v(-8.25, -4.85) * mm});
            skLineSegment(sketch, "E1125", {"start": v(-8.25, -4.85) * mm, "end": v(-8.55, -4.94) * mm});
            skLineSegment(sketch, "E1126", {"start": v(-8.55, -4.94) * mm, "end": v(-8.87, -5.02) * mm});
            skLineSegment(sketch, "E1127", {"start": v(-8.87, -5.02) * mm, "end": v(-9.2, -5.07) * mm});
            skLineSegment(sketch, "E1128", {"start": v(-9.2, -5.07) * mm, "end": v(-9.57, -5.12) * mm});
            skLineSegment(sketch, "E1129", {"start": v(-9.57, -5.12) * mm, "end": v(-9.95, -5.14) * mm});
            skLineSegment(sketch, "E1130", {"start": v(-9.95, -5.14) * mm, "end": v(-10.35, -5.15) * mm});
            skLineSegment(sketch, "E1131", {"start": v(-20.1, -2.21) * mm, "end": v(-18.88, -2.21) * mm});
            skLineSegment(sketch, "E1132", {"start": v(-18.88, -2.21) * mm, "end": v(-17.66, -2.21) * mm});
            skLineSegment(sketch, "E1133", {"start": v(-17.66, -2.21) * mm, "end": v(-16.44, -2.21) * mm});
            skLineSegment(sketch, "E1134", {"start": v(-16.44, -2.21) * mm, "end": v(-15.23, -2.21) * mm});
            skLineSegment(sketch, "E1135", {"start": v(-15.23, -2.21) * mm, "end": v(-14, -2.21) * mm});
            skLineSegment(sketch, "E1136", {"start": v(-14, -2.21) * mm, "end": v(-12.79, -2.21) * mm});
            skLineSegment(sketch, "E1137", {"start": v(-12.79, -2.21) * mm, "end": v(-11.57, -2.21) * mm});
            skLineSegment(sketch, "E1138", {"start": v(-11.57, -2.21) * mm, "end": v(-10.35, -2.21) * mm});
            skLineSegment(sketch, "E1139", {"start": v(-10.35, -2.21) * mm, "end": v(-10.14, -2.2) * mm});
            skLineSegment(sketch, "E1140", {"start": v(-10.14, -2.2) * mm, "end": v(-9.95, -2.2) * mm});
            skLineSegment(sketch, "E1141", {"start": v(-9.95, -2.2) * mm, "end": v(-9.79, -2.19) * mm});
            skLineSegment(sketch, "E1142", {"start": v(-9.79, -2.19) * mm, "end": v(-9.64, -2.17) * mm});
            skLineSegment(sketch, "E1143", {"start": v(-9.64, -2.17) * mm, "end": v(-9.52, -2.15) * mm});
            skLineSegment(sketch, "E1144", {"start": v(-9.52, -2.15) * mm, "end": v(-9.41, -2.13) * mm});
            skLineSegment(sketch, "E1145", {"start": v(-9.41, -2.13) * mm, "end": v(-9.32, -2.11) * mm});
            skLineSegment(sketch, "E1146", {"start": v(-9.32, -2.11) * mm, "end": v(-9.25, -2.1) * mm});
            skLineSegment(sketch, "E1147", {"start": v(-9.25, -2.1) * mm, "end": v(-9.24, -2.06) * mm});
            skLineSegment(sketch, "E1148", {"start": v(-9.24, -2.06) * mm, "end": v(-9.24, -2.03) * mm});
            skLineSegment(sketch, "E1149", {"start": v(-9.24, -2.03) * mm, "end": v(-9.23, -2) * mm});
            skLineSegment(sketch, "E1150", {"start": v(-9.23, -2) * mm, "end": v(-9.23, -1.96) * mm});
            skLineSegment(sketch, "E1151", {"start": v(-9.23, -1.96) * mm, "end": v(-9.23, -1.91) * mm});
            skLineSegment(sketch, "E1152", {"start": v(-9.23, -1.91) * mm, "end": v(-9.23, -1.87) * mm});
            skLineSegment(sketch, "E1153", {"start": v(-9.23, -1.87) * mm, "end": v(-9.22, -1.81) * mm});
            skLineSegment(sketch, "E1154", {"start": v(-9.22, -1.81) * mm, "end": v(-9.22, -1.76) * mm});
            skLineSegment(sketch, "E1155", {"start": v(-9.22, -1.76) * mm, "end": v(-9.22, -1.72) * mm});
            skLineSegment(sketch, "E1156", {"start": v(-9.22, -1.72) * mm, "end": v(-9.22, -1.7) * mm});
            skLineSegment(sketch, "E1157", {"start": v(-9.22, -1.7) * mm, "end": v(-9.23, -1.66) * mm});
            skLineSegment(sketch, "E1158", {"start": v(-9.23, -1.66) * mm, "end": v(-9.23, -1.63) * mm});
            skLineSegment(sketch, "E1159", {"start": v(-9.23, -1.63) * mm, "end": v(-9.23, -1.6) * mm});
            skLineSegment(sketch, "E1160", {"start": v(-9.23, -1.6) * mm, "end": v(-9.23, -1.58) * mm});
            skLineSegment(sketch, "E1161", {"start": v(-9.23, -1.58) * mm, "end": v(-9.23, -1.56) * mm});
            skLineSegment(sketch, "E1162", {"start": v(-9.23, -1.56) * mm, "end": v(-9.24, -1.54) * mm});
            skLineSegment(sketch, "E1163", {"start": v(-9.24, -1.54) * mm, "end": v(-9.3, -1.52) * mm});
            skLineSegment(sketch, "E1164", {"start": v(-9.3, -1.52) * mm, "end": v(-9.38, -1.5) * mm});
            skLineSegment(sketch, "E1165", {"start": v(-9.38, -1.5) * mm, "end": v(-9.48, -1.48) * mm});
            skLineSegment(sketch, "E1166", {"start": v(-9.48, -1.48) * mm, "end": v(-9.6, -1.47) * mm});
            skLineSegment(sketch, "E1167", {"start": v(-9.6, -1.47) * mm, "end": v(-9.72, -1.45) * mm});
            skLineSegment(sketch, "E1168", {"start": v(-9.72, -1.45) * mm, "end": v(-9.87, -1.44) * mm});
            skLineSegment(sketch, "E1169", {"start": v(-9.87, -1.44) * mm, "end": v(-10.04, -1.43) * mm});
            skLineSegment(sketch, "E1170", {"start": v(-10.04, -1.43) * mm, "end": v(-10.23, -1.43) * mm});
            skLineSegment(sketch, "E1171", {"start": v(-10.23, -1.43) * mm, "end": v(-11.46, -1.43) * mm});
            skLineSegment(sketch, "E1172", {"start": v(-11.46, -1.43) * mm, "end": v(-12.7, -1.43) * mm});
            skLineSegment(sketch, "E1173", {"start": v(-12.7, -1.43) * mm, "end": v(-13.93, -1.43) * mm});
            skLineSegment(sketch, "E1174", {"start": v(-13.93, -1.43) * mm, "end": v(-15.16, -1.43) * mm});
            skLineSegment(sketch, "E1175", {"start": v(-15.16, -1.43) * mm, "end": v(-16.4, -1.43) * mm});
            skLineSegment(sketch, "E1176", {"start": v(-16.4, -1.43) * mm, "end": v(-17.63, -1.43) * mm});
            skLineSegment(sketch, "E1177", {"start": v(-17.63, -1.43) * mm, "end": v(-18.86, -1.43) * mm});
            skLineSegment(sketch, "E1178", {"start": v(-18.86, -1.43) * mm, "end": v(-20.1, -1.43) * mm});
            skLineSegment(sketch, "E1179", {"start": v(-20.1, -1.43) * mm, "end": v(-20.1, -1.53) * mm});
            skLineSegment(sketch, "E1180", {"start": v(-20.1, -1.53) * mm, "end": v(-20.1, -1.63) * mm});
            skLineSegment(sketch, "E1181", {"start": v(-20.1, -1.63) * mm, "end": v(-20.1, -1.72) * mm});
            skLineSegment(sketch, "E1182", {"start": v(-20.1, -1.72) * mm, "end": v(-20.1, -1.82) * mm});
            skLineSegment(sketch, "E1183", {"start": v(-20.1, -1.82) * mm, "end": v(-20.1, -1.92) * mm});
            skLineSegment(sketch, "E1184", {"start": v(-20.1, -1.92) * mm, "end": v(-20.1, -2.02) * mm});
            skLineSegment(sketch, "E1185", {"start": v(-20.1, -2.02) * mm, "end": v(-20.1, -2.11) * mm});
            skLineSegment(sketch, "E1186", {"start": v(-20.1, -2.11) * mm, "end": v(-20.1, -2.21) * mm});
            skLineSegment(sketch, "E1187", {"start": v(-29.86, 4.71) * mm, "end": v(-29.86, 2.04) * mm});
            skLineSegment(sketch, "E1188", {"start": v(-29.86, 2.04) * mm, "end": v(-29.86, -0.63) * mm});
            skLineSegment(sketch, "E1189", {"start": v(-29.86, -0.63) * mm, "end": v(-29.86, -3.3) * mm});
            skLineSegment(sketch, "E1190", {"start": v(-29.86, -3.3) * mm, "end": v(-29.86, -5.97) * mm});
            skLineSegment(sketch, "E1191", {"start": v(-29.86, -5.97) * mm, "end": v(-29.86, -8.64) * mm});
            skLineSegment(sketch, "E1192", {"start": v(-29.86, -8.64) * mm, "end": v(-29.86, -11.31) * mm});
            skLineSegment(sketch, "E1193", {"start": v(-29.86, -11.31) * mm, "end": v(-29.86, -13.98) * mm});
            skLineSegment(sketch, "E1194", {"start": v(-29.86, -13.98) * mm, "end": v(-29.86, -16.66) * mm});
            skLineSegment(sketch, "E1195", {"start": v(-29.86, -16.66) * mm, "end": v(-30.68, -16.66) * mm});
            skLineSegment(sketch, "E1196", {"start": v(-30.68, -16.66) * mm, "end": v(-31.49, -16.66) * mm});
            skLineSegment(sketch, "E1197", {"start": v(-31.49, -16.66) * mm, "end": v(-32.3, -16.66) * mm});
            skLineSegment(sketch, "E1198", {"start": v(-32.3, -16.66) * mm, "end": v(-33.11, -16.66) * mm});
            skLineSegment(sketch, "E1199", {"start": v(-33.11, -16.66) * mm, "end": v(-33.93, -16.66) * mm});
            skLineSegment(sketch, "E1200", {"start": v(-33.93, -16.66) * mm, "end": v(-34.74, -16.66) * mm});
            skLineSegment(sketch, "E1201", {"start": v(-34.74, -16.66) * mm, "end": v(-35.55, -16.66) * mm});
            skLineSegment(sketch, "E1202", {"start": v(-35.55, -16.66) * mm, "end": v(-36.36, -16.66) * mm});
            skLineSegment(sketch, "E1203", {"start": v(-36.36, -16.66) * mm, "end": v(-36.46, -16.53) * mm});
            skLineSegment(sketch, "E1204", {"start": v(-36.46, -16.53) * mm, "end": v(-36.75, -16.17) * mm});
            skLineSegment(sketch, "E1205", {"start": v(-36.75, -16.17) * mm, "end": v(-37.26, -15.6) * mm});
            skLineSegment(sketch, "E1206", {"start": v(-37.26, -15.6) * mm, "end": v(-38, -14.84) * mm});
            skLineSegment(sketch, "E1207", {"start": v(-38, -14.84) * mm, "end": v(-38.99, -13.9) * mm});
            skLineSegment(sketch, "E1208", {"start": v(-38.99, -13.9) * mm, "end": v(-40.22, -12.82) * mm});
            skLineSegment(sketch, "E1209", {"start": v(-40.22, -12.82) * mm, "end": v(-41.73, -11.6) * mm});
            skLineSegment(sketch, "E1210", {"start": v(-41.73, -11.6) * mm, "end": v(-43.52, -10.3) * mm});
            skLineSegment(sketch, "E1211", {"start": v(-43.52, -10.3) * mm, "end": v(-44.57, -9.6) * mm});
            skLineSegment(sketch, "E1212", {"start": v(-44.57, -9.6) * mm, "end": v(-45.64, -8.96) * mm});
            skLineSegment(sketch, "E1213", {"start": v(-45.64, -8.96) * mm, "end": v(-46.67, -8.4) * mm});
            skLineSegment(sketch, "E1214", {"start": v(-46.67, -8.4) * mm, "end": v(-47.63, -7.9) * mm});
            skLineSegment(sketch, "E1215", {"start": v(-47.63, -7.9) * mm, "end": v(-48.45, -7.51) * mm});
            skLineSegment(sketch, "E1216", {"start": v(-48.45, -7.51) * mm, "end": v(-49.1, -7.22) * mm});
            skLineSegment(sketch, "E1217", {"start": v(-49.1, -7.22) * mm, "end": v(-49.52, -7.03) * mm});
            skLineSegment(sketch, "E1218", {"start": v(-49.52, -7.03) * mm, "end": v(-49.68, -6.97) * mm});
            skLineSegment(sketch, "E1219", {"start": v(-49.68, -6.97) * mm, "end": v(-51.26, -8.34) * mm});
            skLineSegment(sketch, "E1220", {"start": v(-51.26, -8.34) * mm, "end": v(-52.5, -9.66) * mm});
            skLineSegment(sketch, "E1221", {"start": v(-52.5, -9.66) * mm, "end": v(-53.42, -10.88) * mm});
            skLineSegment(sketch, "E1222", {"start": v(-53.42, -10.88) * mm, "end": v(-54.08, -11.97) * mm});
            skLineSegment(sketch, "E1223", {"start": v(-54.08, -11.97) * mm, "end": v(-54.52, -12.88) * mm});
            skLineSegment(sketch, "E1224", {"start": v(-54.52, -12.88) * mm, "end": v(-54.78, -13.58) * mm});
            skLineSegment(sketch, "E1225", {"start": v(-54.78, -13.58) * mm, "end": v(-54.9, -14.03) * mm});
            skLineSegment(sketch, "E1226", {"start": v(-54.9, -14.03) * mm, "end": v(-54.94, -14.2) * mm});
            skLineSegment(sketch, "E1227", {"start": v(-54.94, -14.2) * mm, "end": v(-55.7, -19.72) * mm});
            skLineSegment(sketch, "E1228", {"start": v(-55.7, -19.72) * mm, "end": v(-54.99, -25.47) * mm});
            skLineSegment(sketch, "E1229", {"start": v(-54.99, -25.47) * mm, "end": v(-53.23, -31.15) * mm});
            skLineSegment(sketch, "E1230", {"start": v(-53.23, -31.15) * mm, "end": v(-50.84, -36.46) * mm});
            skLineSegment(sketch, "E1231", {"start": v(-50.84, -36.46) * mm, "end": v(-48.25, -41.1) * mm});
            skLineSegment(sketch, "E1232", {"start": v(-48.25, -41.1) * mm, "end": v(-45.88, -44.78) * mm});
            skLineSegment(sketch, "E1233", {"start": v(-45.88, -44.78) * mm, "end": v(-44.15, -47.2) * mm});
            skLineSegment(sketch, "E1234", {"start": v(-44.15, -47.2) * mm, "end": v(-43.47, -48.08) * mm});
            skLineSegment(sketch, "E1235", {"start": v(-43.47, -48.08) * mm, "end": v(-44.34, -47.48) * mm});
            skLineSegment(sketch, "E1236", {"start": v(-44.34, -47.48) * mm, "end": v(-46.6, -45.75) * mm});
            skLineSegment(sketch, "E1237", {"start": v(-46.6, -45.75) * mm, "end": v(-49.77, -42.98) * mm});
            skLineSegment(sketch, "E1238", {"start": v(-49.77, -42.98) * mm, "end": v(-53.34, -39.26) * mm});
            skLineSegment(sketch, "E1239", {"start": v(-53.34, -39.26) * mm, "end": v(-56.8, -34.67) * mm});
            skLineSegment(sketch, "E1240", {"start": v(-56.8, -34.67) * mm, "end": v(-59.69, -29.32) * mm});
            skLineSegment(sketch, "E1241", {"start": v(-59.69, -29.32) * mm, "end": v(-61.47, -23.28) * mm});
            skLineSegment(sketch, "E1242", {"start": v(-61.47, -23.28) * mm, "end": v(-61.67, -16.66) * mm});
            skLineSegment(sketch, "E1243", {"start": v(-61.67, -16.66) * mm, "end": v(-61.45, -15.12) * mm});
            skLineSegment(sketch, "E1244", {"start": v(-61.45, -15.12) * mm, "end": v(-61.07, -13.42) * mm});
            skLineSegment(sketch, "E1245", {"start": v(-61.07, -13.42) * mm, "end": v(-60.48, -11.58) * mm});
            skLineSegment(sketch, "E1246", {"start": v(-60.48, -11.58) * mm, "end": v(-59.63, -9.66) * mm});
            skLineSegment(sketch, "E1247", {"start": v(-59.63, -9.66) * mm, "end": v(-58.47, -7.68) * mm});
            skLineSegment(sketch, "E1248", {"start": v(-58.47, -7.68) * mm, "end": v(-56.95, -5.7) * mm});
            skLineSegment(sketch, "E1249", {"start": v(-56.95, -5.7) * mm, "end": v(-55.01, -3.76) * mm});
            skLineSegment(sketch, "E1250", {"start": v(-55.01, -3.76) * mm, "end": v(-52.62, -1.9) * mm});
            skLineSegment(sketch, "E1251", {"start": v(-52.62, -1.9) * mm, "end": v(-49.02, 0.19) * mm});
            skLineSegment(sketch, "E1252", {"start": v(-49.02, 0.19) * mm, "end": v(-45.21, 1.78) * mm});
            skLineSegment(sketch, "E1253", {"start": v(-45.21, 1.78) * mm, "end": v(-41.4, 2.95) * mm});
            skLineSegment(sketch, "E1254", {"start": v(-41.4, 2.95) * mm, "end": v(-37.82, 3.76) * mm});
            skLineSegment(sketch, "E1255", {"start": v(-37.82, 3.76) * mm, "end": v(-34.66, 4.27) * mm});
            skLineSegment(sketch, "E1256", {"start": v(-34.66, 4.27) * mm, "end": v(-32.14, 4.56) * mm});
            skLineSegment(sketch, "E1257", {"start": v(-32.14, 4.56) * mm, "end": v(-30.47, 4.69) * mm});
            skLineSegment(sketch, "E1258", {"start": v(-30.47, 4.69) * mm, "end": v(-29.86, 4.71) * mm});
            skLineSegment(sketch, "E1259", {"start": v(-36.36, -1.87) * mm, "end": v(-36.88, -1.93) * mm});
            skLineSegment(sketch, "E1260", {"start": v(-36.88, -1.93) * mm, "end": v(-37.4, -2) * mm});
            skLineSegment(sketch, "E1261", {"start": v(-37.4, -2) * mm, "end": v(-37.95, -2.07) * mm});
            skLineSegment(sketch, "E1262", {"start": v(-37.95, -2.07) * mm, "end": v(-38.5, -2.16) * mm});
            skLineSegment(sketch, "E1263", {"start": v(-38.5, -2.16) * mm, "end": v(-39.05, -2.26) * mm});
            skLineSegment(sketch, "E1264", {"start": v(-39.05, -2.26) * mm, "end": v(-39.61, -2.37) * mm});
            skLineSegment(sketch, "E1265", {"start": v(-39.61, -2.37) * mm, "end": v(-40.18, -2.5) * mm});
            skLineSegment(sketch, "E1266", {"start": v(-40.18, -2.5) * mm, "end": v(-40.75, -2.63) * mm});
            skLineSegment(sketch, "E1267", {"start": v(-40.75, -2.63) * mm, "end": v(-41.36, -2.8) * mm});
            skLineSegment(sketch, "E1268", {"start": v(-41.36, -2.8) * mm, "end": v(-41.97, -2.97) * mm});
            skLineSegment(sketch, "E1269", {"start": v(-41.97, -2.97) * mm, "end": v(-42.59, -3.16) * mm});
            skLineSegment(sketch, "E1270", {"start": v(-42.59, -3.16) * mm, "end": v(-43.2, -3.37) * mm});
            skLineSegment(sketch, "E1271", {"start": v(-43.2, -3.37) * mm, "end": v(-43.81, -3.6) * mm});
            skLineSegment(sketch, "E1272", {"start": v(-43.81, -3.6) * mm, "end": v(-44.42, -3.85) * mm});
            skLineSegment(sketch, "E1273", {"start": v(-44.42, -3.85) * mm, "end": v(-45.03, -4.12) * mm});
            skLineSegment(sketch, "E1274", {"start": v(-45.03, -4.12) * mm, "end": v(-45.63, -4.4) * mm});
            skLineSegment(sketch, "E1275", {"start": v(-45.63, -4.4) * mm, "end": v(-45.63, -4.4) * mm});
            skLineSegment(sketch, "E1276", {"start": v(-45.63, -4.4) * mm, "end": v(-45.62, -4.4) * mm});
            skLineSegment(sketch, "E1277", {"start": v(-45.62, -4.4) * mm, "end": v(-45.62, -4.41) * mm});
            skLineSegment(sketch, "E1278", {"start": v(-45.62, -4.41) * mm, "end": v(-45.62, -4.41) * mm});
            skLineSegment(sketch, "E1279", {"start": v(-45.62, -4.41) * mm, "end": v(-45.61, -4.41) * mm});
            skLineSegment(sketch, "E1280", {"start": v(-45.61, -4.41) * mm, "end": v(-45.61, -4.42) * mm});
            skLineSegment(sketch, "E1281", {"start": v(-45.61, -4.42) * mm, "end": v(-44.96, -4.7) * mm});
            skLineSegment(sketch, "E1282", {"start": v(-44.96, -4.7) * mm, "end": v(-44.26, -5.03) * mm});
            skLineSegment(sketch, "E1283", {"start": v(-44.26, -5.03) * mm, "end": v(-43.53, -5.4) * mm});
            skLineSegment(sketch, "E1284", {"start": v(-43.53, -5.4) * mm, "end": v(-42.76, -5.78) * mm});
            skLineSegment(sketch, "E1285", {"start": v(-42.76, -5.78) * mm, "end": v(-41.98, -6.2) * mm});
            skLineSegment(sketch, "E1286", {"start": v(-41.98, -6.2) * mm, "end": v(-41.2, -6.65) * mm});
            skLineSegment(sketch, "E1287", {"start": v(-41.2, -6.65) * mm, "end": v(-40.4, -7.13) * mm});
            skLineSegment(sketch, "E1288", {"start": v(-40.4, -7.13) * mm, "end": v(-39.61, -7.64) * mm});
            skLineSegment(sketch, "E1289", {"start": v(-39.61, -7.64) * mm, "end": v(-39.23, -7.9) * mm});
            skLineSegment(sketch, "E1290", {"start": v(-39.23, -7.9) * mm, "end": v(-38.84, -8.19) * mm});
            skLineSegment(sketch, "E1291", {"start": v(-38.84, -8.19) * mm, "end": v(-38.44, -8.49) * mm});
            skLineSegment(sketch, "E1292", {"start": v(-38.44, -8.49) * mm, "end": v(-38.04, -8.8) * mm});
            skLineSegment(sketch, "E1293", {"start": v(-38.04, -8.8) * mm, "end": v(-37.64, -9.13) * mm});
            skLineSegment(sketch, "E1294", {"start": v(-37.64, -9.13) * mm, "end": v(-37.23, -9.48) * mm});
            skLineSegment(sketch, "E1295", {"start": v(-37.23, -9.48) * mm, "end": v(-36.81, -9.83) * mm});
            skLineSegment(sketch, "E1296", {"start": v(-36.81, -9.83) * mm, "end": v(-36.4, -10.19) * mm});
            skLineSegment(sketch, "E1297", {"start": v(-36.4, -10.19) * mm, "end": v(-36.4, -10.19) * mm});
            skLineSegment(sketch, "E1298", {"start": v(-36.4, -10.19) * mm, "end": v(-36.39, -10.19) * mm});
            skLineSegment(sketch, "E1299", {"start": v(-36.39, -10.19) * mm, "end": v(-36.38, -10.19) * mm});
            skLineSegment(sketch, "E1300", {"start": v(-36.38, -10.19) * mm, "end": v(-36.38, -10.19) * mm});
            skLineSegment(sketch, "E1301", {"start": v(-36.38, -10.19) * mm, "end": v(-36.37, -10.19) * mm});
            skLineSegment(sketch, "E1302", {"start": v(-36.37, -10.19) * mm, "end": v(-36.37, -10.19) * mm});
            skLineSegment(sketch, "E1303", {"start": v(-36.37, -10.19) * mm, "end": v(-36.36, -10.19) * mm});
            skLineSegment(sketch, "E1304", {"start": v(-36.36, -10.19) * mm, "end": v(-36.36, -9.15) * mm});
            skLineSegment(sketch, "E1305", {"start": v(-36.36, -9.15) * mm, "end": v(-36.36, -8.1) * mm});
            skLineSegment(sketch, "E1306", {"start": v(-36.36, -8.1) * mm, "end": v(-36.36, -7.07) * mm});
            skLineSegment(sketch, "E1307", {"start": v(-36.36, -7.07) * mm, "end": v(-36.36, -6.03) * mm});
            skLineSegment(sketch, "E1308", {"start": v(-36.36, -6.03) * mm, "end": v(-36.36, -4.99) * mm});
            skLineSegment(sketch, "E1309", {"start": v(-36.36, -4.99) * mm, "end": v(-36.36, -3.95) * mm});
            skLineSegment(sketch, "E1310", {"start": v(-36.36, -3.95) * mm, "end": v(-36.36, -2.9) * mm});
            skLineSegment(sketch, "E1311", {"start": v(-36.36, -2.9) * mm, "end": v(-36.36, -1.87) * mm});
            skLineSegment(sketch, "E1312", {"start": v(-36.65, -54.22) * mm, "end": v(-37.6, -53.61) * mm});
            skLineSegment(sketch, "E1313", {"start": v(-37.6, -53.61) * mm, "end": v(-38.56, -53) * mm});
            skLineSegment(sketch, "E1314", {"start": v(-38.56, -53) * mm, "end": v(-39.5, -52.38) * mm});
            skLineSegment(sketch, "E1315", {"start": v(-39.5, -52.38) * mm, "end": v(-40.46, -51.77) * mm});
            skLineSegment(sketch, "E1316", {"start": v(-40.46, -51.77) * mm, "end": v(-41.41, -51.15) * mm});
            skLineSegment(sketch, "E1317", {"start": v(-41.41, -51.15) * mm, "end": v(-42.37, -50.54) * mm});
            skLineSegment(sketch, "E1318", {"start": v(-42.37, -50.54) * mm, "end": v(-43.32, -49.92) * mm});
            skLineSegment(sketch, "E1319", {"start": v(-43.32, -49.92) * mm, "end": v(-44.27, -49.31) * mm});
            skLineSegment(sketch, "E1320", {"start": v(-44.27, -49.31) * mm, "end": v(-45.41, -48.52) * mm});
            skLineSegment(sketch, "E1321", {"start": v(-45.41, -48.52) * mm, "end": v(-47.87, -46.63) * mm});
            skLineSegment(sketch, "E1322", {"start": v(-47.87, -46.63) * mm, "end": v(-51.17, -43.7) * mm});
            skLineSegment(sketch, "E1323", {"start": v(-51.17, -43.7) * mm, "end": v(-54.81, -39.84) * mm});
            skLineSegment(sketch, "E1324", {"start": v(-54.81, -39.84) * mm, "end": v(-58.32, -35.1) * mm});
            skLineSegment(sketch, "E1325", {"start": v(-58.32, -35.1) * mm, "end": v(-61.2, -29.58) * mm});
            skLineSegment(sketch, "E1326", {"start": v(-61.2, -29.58) * mm, "end": v(-62.96, -23.35) * mm});
            skLineSegment(sketch, "E1327", {"start": v(-62.96, -23.35) * mm, "end": v(-63.13, -16.5) * mm});
            skLineSegment(sketch, "E1328", {"start": v(-63.13, -16.5) * mm, "end": v(-62.74, -14.09) * mm});
            skLineSegment(sketch, "E1329", {"start": v(-62.74, -14.09) * mm, "end": v(-62.11, -11.8) * mm});
            skLineSegment(sketch, "E1330", {"start": v(-62.11, -11.8) * mm, "end": v(-61.25, -9.63) * mm});
            skLineSegment(sketch, "E1331", {"start": v(-61.25, -9.63) * mm, "end": v(-60.15, -7.6) * mm});
            skLineSegment(sketch, "E1332", {"start": v(-60.15, -7.6) * mm, "end": v(-58.83, -5.67) * mm});
            skLineSegment(sketch, "E1333", {"start": v(-58.83, -5.67) * mm, "end": v(-57.27, -3.88) * mm});
            skLineSegment(sketch, "E1334", {"start": v(-57.27, -3.88) * mm, "end": v(-55.47, -2.22) * mm});
            skLineSegment(sketch, "E1335", {"start": v(-55.47, -2.22) * mm, "end": v(-53.45, -0.69) * mm});
            skLineSegment(sketch, "E1336", {"start": v(-53.45, -0.69) * mm, "end": v(-49.77, 1.45) * mm});
            skLineSegment(sketch, "E1337", {"start": v(-49.77, 1.45) * mm, "end": v(-45.9, 3.1) * mm});
            skLineSegment(sketch, "E1338", {"start": v(-45.9, 3.1) * mm, "end": v(-42.03, 4.31) * mm});
            skLineSegment(sketch, "E1339", {"start": v(-42.03, 4.31) * mm, "end": v(-38.37, 5.16) * mm});
            skLineSegment(sketch, "E1340", {"start": v(-38.37, 5.16) * mm, "end": v(-35.13, 5.7) * mm});
            skLineSegment(sketch, "E1341", {"start": v(-35.13, 5.7) * mm, "end": v(-32.5, 6) * mm});
            skLineSegment(sketch, "E1342", {"start": v(-32.5, 6) * mm, "end": v(-30.7, 6.14) * mm});
            skLineSegment(sketch, "E1343", {"start": v(-30.7, 6.14) * mm, "end": v(-29.9, 6.18) * mm});
            skLineSegment(sketch, "E1344", {"start": v(-29.9, 6.18) * mm, "end": v(-29.71, 6.18) * mm});
            skLineSegment(sketch, "E1345", {"start": v(-29.71, 6.18) * mm, "end": v(-29.53, 6.19) * mm});
            skLineSegment(sketch, "E1346", {"start": v(-29.53, 6.19) * mm, "end": v(-29.34, 6.2) * mm});
            skLineSegment(sketch, "E1347", {"start": v(-29.34, 6.2) * mm, "end": v(-29.15, 6.2) * mm});
            skLineSegment(sketch, "E1348", {"start": v(-29.15, 6.2) * mm, "end": v(-28.96, 6.2) * mm});
            skLineSegment(sketch, "E1349", {"start": v(-28.96, 6.2) * mm, "end": v(-28.77, 6.2) * mm});
            skLineSegment(sketch, "E1350", {"start": v(-28.77, 6.2) * mm, "end": v(-28.59, 6.21) * mm});
            skLineSegment(sketch, "E1351", {"start": v(-28.59, 6.21) * mm, "end": v(-28.4, 6.22) * mm});
            skLineSegment(sketch, "E1352", {"start": v(-28.4, 6.22) * mm, "end": v(-28.4, 3.18) * mm});
            skLineSegment(sketch, "E1353", {"start": v(-28.4, 3.18) * mm, "end": v(-28.4, 0.13) * mm});
            skLineSegment(sketch, "E1354", {"start": v(-28.4, 0.13) * mm, "end": v(-28.4, -2.9) * mm});
            skLineSegment(sketch, "E1355", {"start": v(-28.4, -2.9) * mm, "end": v(-28.4, -5.95) * mm});
            skLineSegment(sketch, "E1356", {"start": v(-28.4, -5.95) * mm, "end": v(-28.4, -9) * mm});
            skLineSegment(sketch, "E1357", {"start": v(-28.4, -9) * mm, "end": v(-28.4, -12.04) * mm});
            skLineSegment(sketch, "E1358", {"start": v(-28.4, -12.04) * mm, "end": v(-28.4, -15.08) * mm});
            skLineSegment(sketch, "E1359", {"start": v(-28.4, -15.08) * mm, "end": v(-28.4, -18.12) * mm});
            skLineSegment(sketch, "E1360", {"start": v(-28.4, -18.12) * mm, "end": v(-29.49, -18.12) * mm});
            skLineSegment(sketch, "E1361", {"start": v(-29.49, -18.12) * mm, "end": v(-30.57, -18.12) * mm});
            skLineSegment(sketch, "E1362", {"start": v(-30.57, -18.12) * mm, "end": v(-31.66, -18.12) * mm});
            skLineSegment(sketch, "E1363", {"start": v(-31.66, -18.12) * mm, "end": v(-32.75, -18.12) * mm});
            skLineSegment(sketch, "E1364", {"start": v(-32.75, -18.12) * mm, "end": v(-33.84, -18.12) * mm});
            skLineSegment(sketch, "E1365", {"start": v(-33.84, -18.12) * mm, "end": v(-34.93, -18.12) * mm});
            skLineSegment(sketch, "E1366", {"start": v(-34.93, -18.12) * mm, "end": v(-36.02, -18.12) * mm});
            skLineSegment(sketch, "E1367", {"start": v(-36.02, -18.12) * mm, "end": v(-37.1, -18.12) * mm});
            skLineSegment(sketch, "E1368", {"start": v(-37.1, -18.12) * mm, "end": v(-37.16, -18.05) * mm});
            skLineSegment(sketch, "E1369", {"start": v(-37.16, -18.05) * mm, "end": v(-37.22, -17.97) * mm});
            skLineSegment(sketch, "E1370", {"start": v(-37.22, -17.97) * mm, "end": v(-37.27, -17.9) * mm});
            skLineSegment(sketch, "E1371", {"start": v(-37.27, -17.9) * mm, "end": v(-37.33, -17.82) * mm});
            skLineSegment(sketch, "E1372", {"start": v(-37.33, -17.82) * mm, "end": v(-37.38, -17.75) * mm});
            skLineSegment(sketch, "E1373", {"start": v(-37.38, -17.75) * mm, "end": v(-37.44, -17.67) * mm});
            skLineSegment(sketch, "E1374", {"start": v(-37.44, -17.67) * mm, "end": v(-37.5, -17.6) * mm});
            skLineSegment(sketch, "E1375", {"start": v(-37.5, -17.6) * mm, "end": v(-37.55, -17.52) * mm});
            skLineSegment(sketch, "E1376", {"start": v(-37.55, -17.52) * mm, "end": v(-37.65, -17.4) * mm});
            skLineSegment(sketch, "E1377", {"start": v(-37.65, -17.4) * mm, "end": v(-37.94, -17.05) * mm});
            skLineSegment(sketch, "E1378", {"start": v(-37.94, -17.05) * mm, "end": v(-38.43, -16.5) * mm});
            skLineSegment(sketch, "E1379", {"start": v(-38.43, -16.5) * mm, "end": v(-39.14, -15.78) * mm});
            skLineSegment(sketch, "E1380", {"start": v(-39.14, -15.78) * mm, "end": v(-40.08, -14.9) * mm});
            skLineSegment(sketch, "E1381", {"start": v(-40.08, -14.9) * mm, "end": v(-41.25, -13.87) * mm});
            skLineSegment(sketch, "E1382", {"start": v(-41.25, -13.87) * mm, "end": v(-42.68, -12.73) * mm});
            skLineSegment(sketch, "E1383", {"start": v(-42.68, -12.73) * mm, "end": v(-44.37, -11.5) * mm});
            skLineSegment(sketch, "E1384", {"start": v(-44.37, -11.5) * mm, "end": v(-45.06, -11.03) * mm});
            skLineSegment(sketch, "E1385", {"start": v(-45.06, -11.03) * mm, "end": v(-45.76, -10.59) * mm});
            skLineSegment(sketch, "E1386", {"start": v(-45.76, -10.59) * mm, "end": v(-46.47, -10.18) * mm});
            skLineSegment(sketch, "E1387", {"start": v(-46.47, -10.18) * mm, "end": v(-47.16, -9.8) * mm});
            skLineSegment(sketch, "E1388", {"start": v(-47.16, -9.8) * mm, "end": v(-47.82, -9.46) * mm});
            skLineSegment(sketch, "E1389", {"start": v(-47.82, -9.46) * mm, "end": v(-48.43, -9.15) * mm});
            skLineSegment(sketch, "E1390", {"start": v(-48.43, -9.15) * mm, "end": v(-48.97, -8.89) * mm});
            skLineSegment(sketch, "E1391", {"start": v(-48.97, -8.89) * mm, "end": v(-49.44, -8.67) * mm});
            skLineSegment(sketch, "E1392", {"start": v(-49.44, -8.67) * mm, "end": v(-50.63, -9.78) * mm});
            skLineSegment(sketch, "E1393", {"start": v(-50.63, -9.78) * mm, "end": v(-51.56, -10.84) * mm});
            skLineSegment(sketch, "E1394", {"start": v(-51.56, -10.84) * mm, "end": v(-52.27, -11.81) * mm});
            skLineSegment(sketch, "E1395", {"start": v(-52.27, -11.81) * mm, "end": v(-52.79, -12.67) * mm});
            skLineSegment(sketch, "E1396", {"start": v(-52.79, -12.67) * mm, "end": v(-53.14, -13.39) * mm});
            skLineSegment(sketch, "E1397", {"start": v(-53.14, -13.39) * mm, "end": v(-53.35, -13.94) * mm});
            skLineSegment(sketch, "E1398", {"start": v(-53.35, -13.94) * mm, "end": v(-53.46, -14.3) * mm});
            skLineSegment(sketch, "E1399", {"start": v(-53.46, -14.3) * mm, "end": v(-53.49, -14.43) * mm});
            skLineSegment(sketch, "E1400", {"start": v(-53.49, -14.43) * mm, "end": v(-53.5, -14.45) * mm});
            skLineSegment(sketch, "E1401", {"start": v(-53.5, -14.45) * mm, "end": v(-53.5, -14.47) * mm});
            skLineSegment(sketch, "E1402", {"start": v(-53.5, -14.47) * mm, "end": v(-53.5, -14.5) * mm});
            skLineSegment(sketch, "E1403", {"start": v(-53.5, -14.5) * mm, "end": v(-53.51, -14.52) * mm});
            skLineSegment(sketch, "E1404", {"start": v(-53.51, -14.52) * mm, "end": v(-53.52, -14.55) * mm});
            skLineSegment(sketch, "E1405", {"start": v(-53.52, -14.55) * mm, "end": v(-53.52, -14.57) * mm});
            skLineSegment(sketch, "E1406", {"start": v(-53.52, -14.57) * mm, "end": v(-53.53, -14.6) * mm});
            skLineSegment(sketch, "E1407", {"start": v(-53.53, -14.6) * mm, "end": v(-53.53, -14.62) * mm});
            skLineSegment(sketch, "E1408", {"start": v(-53.53, -14.62) * mm, "end": v(-54.23, -19.83) * mm});
            skLineSegment(sketch, "E1409", {"start": v(-54.23, -19.83) * mm, "end": v(-53.53, -25.29) * mm});
            skLineSegment(sketch, "E1410", {"start": v(-53.53, -25.29) * mm, "end": v(-51.83, -30.7) * mm});
            skLineSegment(sketch, "E1411", {"start": v(-51.83, -30.7) * mm, "end": v(-49.52, -35.8) * mm});
            skLineSegment(sketch, "E1412", {"start": v(-49.52, -35.8) * mm, "end": v(-47.02, -40.29) * mm});
            skLineSegment(sketch, "E1413", {"start": v(-47.02, -40.29) * mm, "end": v(-44.72, -43.86) * mm});
            skLineSegment(sketch, "E1414", {"start": v(-44.72, -43.86) * mm, "end": v(-43.02, -46.25) * mm});
            skLineSegment(sketch, "E1415", {"start": v(-43.02, -46.25) * mm, "end": v(-42.33, -47.16) * mm});
            skLineSegment(sketch, "E1416", {"start": v(-42.33, -47.16) * mm, "end": v(-41.62, -48.04) * mm});
            skLineSegment(sketch, "E1417", {"start": v(-41.62, -48.04) * mm, "end": v(-40.91, -48.92) * mm});
            skLineSegment(sketch, "E1418", {"start": v(-40.91, -48.92) * mm, "end": v(-40.2, -49.8) * mm});
            skLineSegment(sketch, "E1419", {"start": v(-40.2, -49.8) * mm, "end": v(-39.5, -50.7) * mm});
            skLineSegment(sketch, "E1420", {"start": v(-39.5, -50.7) * mm, "end": v(-38.78, -51.57) * mm});
            skLineSegment(sketch, "E1421", {"start": v(-38.78, -51.57) * mm, "end": v(-38.07, -52.46) * mm});
            skLineSegment(sketch, "E1422", {"start": v(-38.07, -52.46) * mm, "end": v(-37.36, -53.34) * mm});
            skLineSegment(sketch, "E1423", {"start": v(-37.36, -53.34) * mm, "end": v(-36.65, -54.22) * mm});
            skLineSegment(sketch, "E1424", {"start": v(-31.33, 3.15) * mm, "end": v(-33, 3) * mm});
            skLineSegment(sketch, "E1425", {"start": v(-33, 3) * mm, "end": v(-35.12, 2.72) * mm});
            skLineSegment(sketch, "E1426", {"start": v(-35.12, 2.72) * mm, "end": v(-37.61, 2.3) * mm});
            skLineSegment(sketch, "E1427", {"start": v(-37.61, 2.3) * mm, "end": v(-40.36, 1.7) * mm});
            skLineSegment(sketch, "E1428", {"start": v(-40.36, 1.7) * mm, "end": v(-43.26, 0.88) * mm});
            skLineSegment(sketch, "E1429", {"start": v(-43.26, 0.88) * mm, "end": v(-46.2, -0.17) * mm});
            skLineSegment(sketch, "E1430", {"start": v(-46.2, -0.17) * mm, "end": v(-49.08, -1.49) * mm});
            skLineSegment(sketch, "E1431", {"start": v(-49.08, -1.49) * mm, "end": v(-51.8, -3.1) * mm});
            skLineSegment(sketch, "E1432", {"start": v(-51.8, -3.1) * mm, "end": v(-53.55, -4.44) * mm});
            skLineSegment(sketch, "E1433", {"start": v(-53.55, -4.44) * mm, "end": v(-55.11, -5.89) * mm});
            skLineSegment(sketch, "E1434", {"start": v(-55.11, -5.89) * mm, "end": v(-56.47, -7.44) * mm});
            skLineSegment(sketch, "E1435", {"start": v(-56.47, -7.44) * mm, "end": v(-57.63, -9.1) * mm});
            skLineSegment(sketch, "E1436", {"start": v(-57.63, -9.1) * mm, "end": v(-58.58, -10.87) * mm});
            skLineSegment(sketch, "E1437", {"start": v(-58.58, -10.87) * mm, "end": v(-59.33, -12.75) * mm});
            skLineSegment(sketch, "E1438", {"start": v(-59.33, -12.75) * mm, "end": v(-59.87, -14.73) * mm});
            skLineSegment(sketch, "E1439", {"start": v(-59.87, -14.73) * mm, "end": v(-60.21, -16.82) * mm});
            skLineSegment(sketch, "E1440", {"start": v(-60.21, -16.82) * mm, "end": v(-60.32, -20.37) * mm});
            skLineSegment(sketch, "E1441", {"start": v(-60.32, -20.37) * mm, "end": v(-59.88, -23.77) * mm});
            skLineSegment(sketch, "E1442", {"start": v(-59.88, -23.77) * mm, "end": v(-58.99, -27) * mm});
            skLineSegment(sketch, "E1443", {"start": v(-58.99, -27) * mm, "end": v(-57.72, -30.05) * mm});
            skLineSegment(sketch, "E1444", {"start": v(-57.72, -30.05) * mm, "end": v(-56.17, -32.9) * mm});
            skLineSegment(sketch, "E1445", {"start": v(-56.17, -32.9) * mm, "end": v(-54.4, -35.53) * mm});
            skLineSegment(sketch, "E1446", {"start": v(-54.4, -35.53) * mm, "end": v(-52.51, -37.92) * mm});
            skLineSegment(sketch, "E1447", {"start": v(-52.51, -37.92) * mm, "end": v(-50.58, -40.07) * mm});
            skLineSegment(sketch, "E1448", {"start": v(-50.58, -40.07) * mm, "end": v(-52.12, -37.23) * mm});
            skLineSegment(sketch, "E1449", {"start": v(-52.12, -37.23) * mm, "end": v(-53.59, -34.15) * mm});
            skLineSegment(sketch, "E1450", {"start": v(-53.59, -34.15) * mm, "end": v(-54.9, -30.89) * mm});
            skLineSegment(sketch, "E1451", {"start": v(-54.9, -30.89) * mm, "end": v(-56, -27.5) * mm});
            skLineSegment(sketch, "E1452", {"start": v(-56, -27.5) * mm, "end": v(-56.77, -24.05) * mm});
            skLineSegment(sketch, "E1453", {"start": v(-56.77, -24.05) * mm, "end": v(-57.14, -20.58) * mm});
            skLineSegment(sketch, "E1454", {"start": v(-57.14, -20.58) * mm, "end": v(-57.04, -17.16) * mm});
            skLineSegment(sketch, "E1455", {"start": v(-57.04, -17.16) * mm, "end": v(-56.36, -13.84) * mm});
            skLineSegment(sketch, "E1456", {"start": v(-56.36, -13.84) * mm, "end": v(-56.26, -13.43) * mm});
            skLineSegment(sketch, "E1457", {"start": v(-56.26, -13.43) * mm, "end": v(-56.05, -12.78) * mm});
            skLineSegment(sketch, "E1458", {"start": v(-56.05, -12.78) * mm, "end": v(-55.7, -11.93) * mm});
            skLineSegment(sketch, "E1459", {"start": v(-55.7, -11.93) * mm, "end": v(-55.16, -10.9) * mm});
            skLineSegment(sketch, "E1460", {"start": v(-55.16, -10.9) * mm, "end": v(-54.42, -9.75) * mm});
            skLineSegment(sketch, "E1461", {"start": v(-54.42, -9.75) * mm, "end": v(-53.43, -8.5) * mm});
            skLineSegment(sketch, "E1462", {"start": v(-53.43, -8.5) * mm, "end": v(-52.16, -7.17) * mm});
            skLineSegment(sketch, "E1463", {"start": v(-52.16, -7.17) * mm, "end": v(-50.58, -5.81) * mm});
            skLineSegment(sketch, "E1464", {"start": v(-50.58, -5.81) * mm, "end": v(-50.5, -5.75) * mm});
            skLineSegment(sketch, "E1465", {"start": v(-50.5, -5.75) * mm, "end": v(-50.41, -5.68) * mm});
            skLineSegment(sketch, "E1466", {"start": v(-50.41, -5.68) * mm, "end": v(-50.33, -5.62) * mm});
            skLineSegment(sketch, "E1467", {"start": v(-50.33, -5.62) * mm, "end": v(-50.24, -5.55) * mm});
            skLineSegment(sketch, "E1468", {"start": v(-50.24, -5.55) * mm, "end": v(-50.16, -5.49) * mm});
            skLineSegment(sketch, "E1469", {"start": v(-50.16, -5.49) * mm, "end": v(-50.08, -5.42) * mm});
            skLineSegment(sketch, "E1470", {"start": v(-50.08, -5.42) * mm, "end": v(-50, -5.35) * mm});
            skLineSegment(sketch, "E1471", {"start": v(-50, -5.35) * mm, "end": v(-49.9, -5.29) * mm});
            skLineSegment(sketch, "E1472", {"start": v(-49.9, -5.29) * mm, "end": v(-49.81, -5.33) * mm});
            skLineSegment(sketch, "E1473", {"start": v(-49.81, -5.33) * mm, "end": v(-49.71, -5.37) * mm});
            skLineSegment(sketch, "E1474", {"start": v(-49.71, -5.37) * mm, "end": v(-49.61, -5.41) * mm});
            skLineSegment(sketch, "E1475", {"start": v(-49.61, -5.41) * mm, "end": v(-49.52, -5.45) * mm});
            skLineSegment(sketch, "E1476", {"start": v(-49.52, -5.45) * mm, "end": v(-49.42, -5.5) * mm});
            skLineSegment(sketch, "E1477", {"start": v(-49.42, -5.5) * mm, "end": v(-49.32, -5.53) * mm});
            skLineSegment(sketch, "E1478", {"start": v(-49.32, -5.53) * mm, "end": v(-49.22, -5.57) * mm});
            skLineSegment(sketch, "E1479", {"start": v(-49.22, -5.57) * mm, "end": v(-49.12, -5.61) * mm});
            skLineSegment(sketch, "E1480", {"start": v(-49.12, -5.61) * mm, "end": v(-48.92, -5.7) * mm});
            skLineSegment(sketch, "E1481", {"start": v(-48.92, -5.7) * mm, "end": v(-48.45, -5.9) * mm});
            skLineSegment(sketch, "E1482", {"start": v(-48.45, -5.9) * mm, "end": v(-47.77, -6.21) * mm});
            skLineSegment(sketch, "E1483", {"start": v(-47.77, -6.21) * mm, "end": v(-46.91, -6.63) * mm});
            skLineSegment(sketch, "E1484", {"start": v(-46.91, -6.63) * mm, "end": v(-45.93, -7.13) * mm});
            skLineSegment(sketch, "E1485", {"start": v(-45.93, -7.13) * mm, "end": v(-44.86, -7.71) * mm});
            skLineSegment(sketch, "E1486", {"start": v(-44.86, -7.71) * mm, "end": v(-43.77, -8.37) * mm});
            skLineSegment(sketch, "E1487", {"start": v(-43.77, -8.37) * mm, "end": v(-42.68, -9.1) * mm});
            skLineSegment(sketch, "E1488", {"start": v(-42.68, -9.1) * mm, "end": v(-41.28, -10.1) * mm});
            skLineSegment(sketch, "E1489", {"start": v(-41.28, -10.1) * mm, "end": v(-40.05, -11.07) * mm});
            skLineSegment(sketch, "E1490", {"start": v(-40.05, -11.07) * mm, "end": v(-38.96, -11.96) * mm});
            skLineSegment(sketch, "E1491", {"start": v(-38.96, -11.96) * mm, "end": v(-38.03, -12.79) * mm});
            skLineSegment(sketch, "E1492", {"start": v(-38.03, -12.79) * mm, "end": v(-37.24, -13.53) * mm});
            skLineSegment(sketch, "E1493", {"start": v(-37.24, -13.53) * mm, "end": v(-36.58, -14.19) * mm});
            skLineSegment(sketch, "E1494", {"start": v(-36.58, -14.19) * mm, "end": v(-36.06, -14.74) * mm});
            skLineSegment(sketch, "E1495", {"start": v(-36.06, -14.74) * mm, "end": v(-35.66, -15.19) * mm});
            skLineSegment(sketch, "E1496", {"start": v(-35.66, -15.19) * mm, "end": v(-35.12, -15.19) * mm});
            skLineSegment(sketch, "E1497", {"start": v(-35.12, -15.19) * mm, "end": v(-34.58, -15.19) * mm});
            skLineSegment(sketch, "E1498", {"start": v(-34.58, -15.19) * mm, "end": v(-34.04, -15.19) * mm});
            skLineSegment(sketch, "E1499", {"start": v(-34.04, -15.19) * mm, "end": v(-33.5, -15.19) * mm});
            skLineSegment(sketch, "E1500", {"start": v(-33.5, -15.19) * mm, "end": v(-32.96, -15.19) * mm});
            skLineSegment(sketch, "E1501", {"start": v(-32.96, -15.19) * mm, "end": v(-32.42, -15.19) * mm});
            skLineSegment(sketch, "E1502", {"start": v(-32.42, -15.19) * mm, "end": v(-31.87, -15.19) * mm});
            skLineSegment(sketch, "E1503", {"start": v(-31.87, -15.19) * mm, "end": v(-31.33, -15.19) * mm});
            skLineSegment(sketch, "E1504", {"start": v(-31.33, -15.19) * mm, "end": v(-31.33, -12.9) * mm});
            skLineSegment(sketch, "E1505", {"start": v(-31.33, -12.9) * mm, "end": v(-31.33, -10.6) * mm});
            skLineSegment(sketch, "E1506", {"start": v(-31.33, -10.6) * mm, "end": v(-31.33, -8.3) * mm});
            skLineSegment(sketch, "E1507", {"start": v(-31.33, -8.3) * mm, "end": v(-31.33, -6.02) * mm});
            skLineSegment(sketch, "E1508", {"start": v(-31.33, -6.02) * mm, "end": v(-31.33, -3.72) * mm});
            skLineSegment(sketch, "E1509", {"start": v(-31.33, -3.72) * mm, "end": v(-31.33, -1.43) * mm});
            skLineSegment(sketch, "E1510", {"start": v(-31.33, -1.43) * mm, "end": v(-31.33, 0.86) * mm});
            skLineSegment(sketch, "E1511", {"start": v(-31.33, 0.86) * mm, "end": v(-31.33, 3.15) * mm});
            skLineSegment(sketch, "E1512", {"start": v(-34.9, -11.65) * mm, "end": v(-35.15, -11.65) * mm});
            skLineSegment(sketch, "E1513", {"start": v(-35.15, -11.65) * mm, "end": v(-35.4, -11.65) * mm});
            skLineSegment(sketch, "E1514", {"start": v(-35.4, -11.65) * mm, "end": v(-35.67, -11.65) * mm});
            skLineSegment(sketch, "E1515", {"start": v(-35.67, -11.65) * mm, "end": v(-35.92, -11.65) * mm});
            skLineSegment(sketch, "E1516", {"start": v(-35.92, -11.65) * mm, "end": v(-36.18, -11.65) * mm});
            skLineSegment(sketch, "E1517", {"start": v(-36.18, -11.65) * mm, "end": v(-36.44, -11.65) * mm});
            skLineSegment(sketch, "E1518", {"start": v(-36.44, -11.65) * mm, "end": v(-36.7, -11.65) * mm});
            skLineSegment(sketch, "E1519", {"start": v(-36.7, -11.65) * mm, "end": v(-36.95, -11.65) * mm});
            skLineSegment(sketch, "E1520", {"start": v(-36.95, -11.65) * mm, "end": v(-37, -11.6) * mm});
            skLineSegment(sketch, "E1521", {"start": v(-37, -11.6) * mm, "end": v(-37.06, -11.56) * mm});
            skLineSegment(sketch, "E1522", {"start": v(-37.06, -11.56) * mm, "end": v(-37.11, -11.52) * mm});
            skLineSegment(sketch, "E1523", {"start": v(-37.11, -11.52) * mm, "end": v(-37.16, -11.47) * mm});
            skLineSegment(sketch, "E1524", {"start": v(-37.16, -11.47) * mm, "end": v(-37.22, -11.43) * mm});
            skLineSegment(sketch, "E1525", {"start": v(-37.22, -11.43) * mm, "end": v(-37.27, -11.38) * mm});
            skLineSegment(sketch, "E1526", {"start": v(-37.27, -11.38) * mm, "end": v(-37.32, -11.33) * mm});
            skLineSegment(sketch, "E1527", {"start": v(-37.32, -11.33) * mm, "end": v(-37.37, -11.29) * mm});
            skLineSegment(sketch, "E1528", {"start": v(-37.37, -11.29) * mm, "end": v(-37.8, -10.91) * mm});
            skLineSegment(sketch, "E1529", {"start": v(-37.8, -10.91) * mm, "end": v(-38.22, -10.55) * mm});
            skLineSegment(sketch, "E1530", {"start": v(-38.22, -10.55) * mm, "end": v(-38.63, -10.22) * mm});
            skLineSegment(sketch, "E1531", {"start": v(-38.63, -10.22) * mm, "end": v(-39.02, -9.9) * mm});
            skLineSegment(sketch, "E1532", {"start": v(-39.02, -9.9) * mm, "end": v(-39.4, -9.61) * mm});
            skLineSegment(sketch, "E1533", {"start": v(-39.4, -9.61) * mm, "end": v(-39.75, -9.34) * mm});
            skLineSegment(sketch, "E1534", {"start": v(-39.75, -9.34) * mm, "end": v(-40.1, -9.1) * mm});
            skLineSegment(sketch, "E1535", {"start": v(-40.1, -9.1) * mm, "end": v(-40.43, -8.86) * mm});
            skLineSegment(sketch, "E1536", {"start": v(-40.43, -8.86) * mm, "end": v(-41.2, -8.36) * mm});
            skLineSegment(sketch, "E1537", {"start": v(-41.2, -8.36) * mm, "end": v(-41.98, -7.9) * mm});
            skLineSegment(sketch, "E1538", {"start": v(-41.98, -7.9) * mm, "end": v(-42.75, -7.45) * mm});
            skLineSegment(sketch, "E1539", {"start": v(-42.75, -7.45) * mm, "end": v(-43.51, -7.04) * mm});
            skLineSegment(sketch, "E1540", {"start": v(-43.51, -7.04) * mm, "end": v(-44.25, -6.67) * mm});
            skLineSegment(sketch, "E1541", {"start": v(-44.25, -6.67) * mm, "end": v(-44.95, -6.33) * mm});
            skLineSegment(sketch, "E1542", {"start": v(-44.95, -6.33) * mm, "end": v(-45.6, -6.03) * mm});
            skLineSegment(sketch, "E1543", {"start": v(-45.6, -6.03) * mm, "end": v(-46.2, -5.76) * mm});
            skLineSegment(sketch, "E1544", {"start": v(-46.2, -5.76) * mm, "end": v(-46.21, -5.75) * mm});
            skLineSegment(sketch, "E1545", {"start": v(-46.21, -5.75) * mm, "end": v(-46.22, -5.75) * mm});
            skLineSegment(sketch, "E1546", {"start": v(-46.22, -5.75) * mm, "end": v(-46.23, -5.74) * mm});
            skLineSegment(sketch, "E1547", {"start": v(-46.23, -5.74) * mm, "end": v(-46.24, -5.74) * mm});
            skLineSegment(sketch, "E1548", {"start": v(-46.24, -5.74) * mm, "end": v(-46.25, -5.73) * mm});
            skLineSegment(sketch, "E1549", {"start": v(-46.25, -5.73) * mm, "end": v(-46.26, -5.73) * mm});
            skLineSegment(sketch, "E1550", {"start": v(-46.26, -5.73) * mm, "end": v(-46.27, -5.73) * mm});
            skLineSegment(sketch, "E1551", {"start": v(-46.27, -5.73) * mm, "end": v(-46.28, -5.72) * mm});
            skLineSegment(sketch, "E1552", {"start": v(-46.28, -5.72) * mm, "end": v(-46.6, -5.56) * mm});
            skLineSegment(sketch, "E1553", {"start": v(-46.6, -5.56) * mm, "end": v(-46.93, -5.4) * mm});
            skLineSegment(sketch, "E1554", {"start": v(-46.93, -5.4) * mm, "end": v(-47.25, -5.23) * mm});
            skLineSegment(sketch, "E1555", {"start": v(-47.25, -5.23) * mm, "end": v(-47.57, -5.06) * mm});
            skLineSegment(sketch, "E1556", {"start": v(-47.57, -5.06) * mm, "end": v(-47.9, -4.9) * mm});
            skLineSegment(sketch, "E1557", {"start": v(-47.9, -4.9) * mm, "end": v(-48.22, -4.73) * mm});
            skLineSegment(sketch, "E1558", {"start": v(-48.22, -4.73) * mm, "end": v(-48.54, -4.57) * mm});
            skLineSegment(sketch, "E1559", {"start": v(-48.54, -4.57) * mm, "end": v(-48.86, -4.4) * mm});
            skLineSegment(sketch, "E1560", {"start": v(-48.86, -4.4) * mm, "end": v(-48.54, -4.24) * mm});
            skLineSegment(sketch, "E1561", {"start": v(-48.54, -4.24) * mm, "end": v(-48.22, -4.07) * mm});
            skLineSegment(sketch, "E1562", {"start": v(-48.22, -4.07) * mm, "end": v(-47.9, -3.91) * mm});
            skLineSegment(sketch, "E1563", {"start": v(-47.9, -3.91) * mm, "end": v(-47.57, -3.75) * mm});
            skLineSegment(sketch, "E1564", {"start": v(-47.57, -3.75) * mm, "end": v(-47.25, -3.58) * mm});
            skLineSegment(sketch, "E1565", {"start": v(-47.25, -3.58) * mm, "end": v(-46.93, -3.42) * mm});
            skLineSegment(sketch, "E1566", {"start": v(-46.93, -3.42) * mm, "end": v(-46.6, -3.26) * mm});
            skLineSegment(sketch, "E1567", {"start": v(-46.6, -3.26) * mm, "end": v(-46.29, -3.1) * mm});
            skLineSegment(sketch, "E1568", {"start": v(-46.29, -3.1) * mm, "end": v(-45.7, -2.8) * mm});
            skLineSegment(sketch, "E1569", {"start": v(-45.7, -2.8) * mm, "end": v(-45.08, -2.54) * mm});
            skLineSegment(sketch, "E1570", {"start": v(-45.08, -2.54) * mm, "end": v(-44.46, -2.28) * mm});
            skLineSegment(sketch, "E1571", {"start": v(-44.46, -2.28) * mm, "end": v(-43.81, -2.04) * mm});
            skLineSegment(sketch, "E1572", {"start": v(-43.81, -2.04) * mm, "end": v(-43.16, -1.8) * mm});
            skLineSegment(sketch, "E1573", {"start": v(-43.16, -1.8) * mm, "end": v(-42.49, -1.6) * mm});
            skLineSegment(sketch, "E1574", {"start": v(-42.49, -1.6) * mm, "end": v(-41.8, -1.4) * mm});
            skLineSegment(sketch, "E1575", {"start": v(-41.8, -1.4) * mm, "end": v(-41.1, -1.21) * mm});
            skLineSegment(sketch, "E1576", {"start": v(-41.1, -1.21) * mm, "end": v(-40.56, -1.08) * mm});
            skLineSegment(sketch, "E1577", {"start": v(-40.56, -1.08) * mm, "end": v(-40, -0.96) * mm});
            skLineSegment(sketch, "E1578", {"start": v(-40, -0.96) * mm, "end": v(-39.44, -0.84) * mm});
            skLineSegment(sketch, "E1579", {"start": v(-39.44, -0.84) * mm, "end": v(-38.87, -0.74) * mm});
            skLineSegment(sketch, "E1580", {"start": v(-38.87, -0.74) * mm, "end": v(-38.3, -0.64) * mm});
            skLineSegment(sketch, "E1581", {"start": v(-38.3, -0.64) * mm, "end": v(-37.7, -0.56) * mm});
            skLineSegment(sketch, "E1582", {"start": v(-37.7, -0.56) * mm, "end": v(-37.11, -0.48) * mm});
            skLineSegment(sketch, "E1583", {"start": v(-37.11, -0.48) * mm, "end": v(-36.51, -0.41) * mm});
            skLineSegment(sketch, "E1584", {"start": v(-36.51, -0.41) * mm, "end": v(-36.31, -0.4) * mm});
            skLineSegment(sketch, "E1585", {"start": v(-36.31, -0.4) * mm, "end": v(-36.1, -0.37) * mm});
            skLineSegment(sketch, "E1586", {"start": v(-36.1, -0.37) * mm, "end": v(-35.9, -0.35) * mm});
            skLineSegment(sketch, "E1587", {"start": v(-35.9, -0.35) * mm, "end": v(-35.7, -0.33) * mm});
            skLineSegment(sketch, "E1588", {"start": v(-35.7, -0.33) * mm, "end": v(-35.5, -0.3) * mm});
            skLineSegment(sketch, "E1589", {"start": v(-35.5, -0.3) * mm, "end": v(-35.3, -0.28) * mm});
            skLineSegment(sketch, "E1590", {"start": v(-35.3, -0.28) * mm, "end": v(-35.1, -0.26) * mm});
            skLineSegment(sketch, "E1591", {"start": v(-35.1, -0.26) * mm, "end": v(-34.9, -0.24) * mm});
            skLineSegment(sketch, "E1592", {"start": v(-34.9, -0.24) * mm, "end": v(-34.9, -1.67) * mm});
            skLineSegment(sketch, "E1593", {"start": v(-34.9, -1.67) * mm, "end": v(-34.9, -3.1) * mm});
            skLineSegment(sketch, "E1594", {"start": v(-34.9, -3.1) * mm, "end": v(-34.9, -4.52) * mm});
            skLineSegment(sketch, "E1595", {"start": v(-34.9, -4.52) * mm, "end": v(-34.9, -5.95) * mm});
            skLineSegment(sketch, "E1596", {"start": v(-34.9, -5.95) * mm, "end": v(-34.9, -7.37) * mm});
            skLineSegment(sketch, "E1597", {"start": v(-34.9, -7.37) * mm, "end": v(-34.9, -8.8) * mm});
            skLineSegment(sketch, "E1598", {"start": v(-34.9, -8.8) * mm, "end": v(-34.9, -10.23) * mm});
            skLineSegment(sketch, "E1599", {"start": v(-34.9, -10.23) * mm, "end": v(-34.9, -11.65) * mm});
            skLineSegment(sketch, "E1600", {"start": v(-42, -4.52) * mm, "end": v(-41.62, -4.73) * mm});
            skLineSegment(sketch, "E1601", {"start": v(-41.62, -4.73) * mm, "end": v(-41.22, -4.95) * mm});
            skLineSegment(sketch, "E1602", {"start": v(-41.22, -4.95) * mm, "end": v(-40.81, -5.18) * mm});
            skLineSegment(sketch, "E1603", {"start": v(-40.81, -5.18) * mm, "end": v(-40.4, -5.41) * mm});
            skLineSegment(sketch, "E1604", {"start": v(-40.4, -5.41) * mm, "end": v(-40, -5.65) * mm});
            skLineSegment(sketch, "E1605", {"start": v(-40, -5.65) * mm, "end": v(-39.6, -5.9) * mm});
            skLineSegment(sketch, "E1606", {"start": v(-39.6, -5.9) * mm, "end": v(-39.2, -6.16) * mm});
            skLineSegment(sketch, "E1607", {"start": v(-39.2, -6.16) * mm, "end": v(-38.8, -6.43) * mm});
            skLineSegment(sketch, "E1608", {"start": v(-38.8, -6.43) * mm, "end": v(-38.68, -6.5) * mm});
            skLineSegment(sketch, "E1609", {"start": v(-38.68, -6.5) * mm, "end": v(-38.56, -6.59) * mm});
            skLineSegment(sketch, "E1610", {"start": v(-38.56, -6.59) * mm, "end": v(-38.44, -6.67) * mm});
            skLineSegment(sketch, "E1611", {"start": v(-38.44, -6.67) * mm, "end": v(-38.32, -6.75) * mm});
            skLineSegment(sketch, "E1612", {"start": v(-38.32, -6.75) * mm, "end": v(-38.2, -6.84) * mm});
            skLineSegment(sketch, "E1613", {"start": v(-38.2, -6.84) * mm, "end": v(-38.08, -6.93) * mm});
            skLineSegment(sketch, "E1614", {"start": v(-38.08, -6.93) * mm, "end": v(-37.95, -7.02) * mm});
            skLineSegment(sketch, "E1615", {"start": v(-37.95, -7.02) * mm, "end": v(-37.83, -7.11) * mm});
            skLineSegment(sketch, "E1616", {"start": v(-37.83, -7.11) * mm, "end": v(-37.83, -6.67) * mm});
            skLineSegment(sketch, "E1617", {"start": v(-37.83, -6.67) * mm, "end": v(-37.83, -6.22) * mm});
            skLineSegment(sketch, "E1618", {"start": v(-37.83, -6.22) * mm, "end": v(-37.83, -5.77) * mm});
            skLineSegment(sketch, "E1619", {"start": v(-37.83, -5.77) * mm, "end": v(-37.83, -5.33) * mm});
            skLineSegment(sketch, "E1620", {"start": v(-37.83, -5.33) * mm, "end": v(-37.83, -4.88) * mm});
            skLineSegment(sketch, "E1621", {"start": v(-37.83, -4.88) * mm, "end": v(-37.83, -4.43) * mm});
            skLineSegment(sketch, "E1622", {"start": v(-37.83, -4.43) * mm, "end": v(-37.83, -3.99) * mm});
            skLineSegment(sketch, "E1623", {"start": v(-37.83, -3.99) * mm, "end": v(-37.83, -3.54) * mm});
            skLineSegment(sketch, "E1624", {"start": v(-37.83, -3.54) * mm, "end": v(-38.16, -3.6) * mm});
            skLineSegment(sketch, "E1625", {"start": v(-38.16, -3.6) * mm, "end": v(-38.49, -3.65) * mm});
            skLineSegment(sketch, "E1626", {"start": v(-38.49, -3.65) * mm, "end": v(-38.81, -3.71) * mm});
            skLineSegment(sketch, "E1627", {"start": v(-38.81, -3.71) * mm, "end": v(-39.13, -3.77) * mm});
            skLineSegment(sketch, "E1628", {"start": v(-39.13, -3.77) * mm, "end": v(-39.45, -3.84) * mm});
            skLineSegment(sketch, "E1629", {"start": v(-39.45, -3.84) * mm, "end": v(-39.77, -3.9) * mm});
            skLineSegment(sketch, "E1630", {"start": v(-39.77, -3.9) * mm, "end": v(-40.08, -3.98) * mm});
            skLineSegment(sketch, "E1631", {"start": v(-40.08, -3.98) * mm, "end": v(-40.39, -4.06) * mm});
            skLineSegment(sketch, "E1632", {"start": v(-40.39, -4.06) * mm, "end": v(-40.6, -4.1) * mm});
            skLineSegment(sketch, "E1633", {"start": v(-40.6, -4.1) * mm, "end": v(-40.8, -4.16) * mm});
            skLineSegment(sketch, "E1634", {"start": v(-40.8, -4.16) * mm, "end": v(-41, -4.22) * mm});
            skLineSegment(sketch, "E1635", {"start": v(-41, -4.22) * mm, "end": v(-41.21, -4.28) * mm});
            skLineSegment(sketch, "E1636", {"start": v(-41.21, -4.28) * mm, "end": v(-41.41, -4.33) * mm});
            skLineSegment(sketch, "E1637", {"start": v(-41.41, -4.33) * mm, "end": v(-41.61, -4.4) * mm});
            skLineSegment(sketch, "E1638", {"start": v(-41.61, -4.4) * mm, "end": v(-41.81, -4.46) * mm});
            skLineSegment(sketch, "E1639", {"start": v(-41.81, -4.46) * mm, "end": v(-42, -4.52) * mm});
            skLineSegment(sketch, "E1640", {"start": v(17.56, -16.6) * mm, "end": v(16.63, -16.57) * mm});
            skLineSegment(sketch, "E1641", {"start": v(16.63, -16.57) * mm, "end": v(15.7, -16.54) * mm});
            skLineSegment(sketch, "E1642", {"start": v(15.7, -16.54) * mm, "end": v(14.79, -16.5) * mm});
            skLineSegment(sketch, "E1643", {"start": v(14.79, -16.5) * mm, "end": v(13.86, -16.47) * mm});
            skLineSegment(sketch, "E1644", {"start": v(13.86, -16.47) * mm, "end": v(12.94, -16.44) * mm});
            skLineSegment(sketch, "E1645", {"start": v(12.94, -16.44) * mm, "end": v(12.01, -16.4) * mm});
            skLineSegment(sketch, "E1646", {"start": v(12.01, -16.4) * mm, "end": v(11.1, -16.37) * mm});
            skLineSegment(sketch, "E1647", {"start": v(11.1, -16.37) * mm, "end": v(10.17, -16.34) * mm});
            skLineSegment(sketch, "E1648", {"start": v(10.17, -16.34) * mm, "end": v(8.9, -16.3) * mm});
            skLineSegment(sketch, "E1649", {"start": v(8.9, -16.3) * mm, "end": v(7.73, -16.17) * mm});
            skLineSegment(sketch, "E1650", {"start": v(7.73, -16.17) * mm, "end": v(6.66, -15.96) * mm});
            skLineSegment(sketch, "E1651", {"start": v(6.66, -15.96) * mm, "end": v(5.7, -15.66) * mm});
            skLineSegment(sketch, "E1652", {"start": v(5.7, -15.66) * mm, "end": v(4.85, -15.28) * mm});
            skLineSegment(sketch, "E1653", {"start": v(4.85, -15.28) * mm, "end": v(4.1, -14.82) * mm});
            skLineSegment(sketch, "E1654", {"start": v(4.1, -14.82) * mm, "end": v(3.47, -14.27) * mm});
            skLineSegment(sketch, "E1655", {"start": v(3.47, -14.27) * mm, "end": v(2.94, -13.64) * mm});
            skLineSegment(sketch, "E1656", {"start": v(2.94, -13.64) * mm, "end": v(2.49, -12.92) * mm});
            skLineSegment(sketch, "E1657", {"start": v(2.49, -12.92) * mm, "end": v(2.1, -12.1) * mm});
            skLineSegment(sketch, "E1658", {"start": v(2.1, -12.1) * mm, "end": v(1.76, -11.2) * mm});
            skLineSegment(sketch, "E1659", {"start": v(1.76, -11.2) * mm, "end": v(1.5, -10.2) * mm});
            skLineSegment(sketch, "E1660", {"start": v(1.5, -10.2) * mm, "end": v(1.28, -9.1) * mm});
            skLineSegment(sketch, "E1661", {"start": v(1.28, -9.1) * mm, "end": v(1.13, -7.9) * mm});
            skLineSegment(sketch, "E1662", {"start": v(1.13, -7.9) * mm, "end": v(1.04, -6.62) * mm});
            skLineSegment(sketch, "E1663", {"start": v(1.04, -6.62) * mm, "end": v(1.01, -5.24) * mm});
            skLineSegment(sketch, "E1664", {"start": v(1.01, -5.24) * mm, "end": v(1.04, -3.98) * mm});
            skLineSegment(sketch, "E1665", {"start": v(1.04, -3.98) * mm, "end": v(1.14, -2.8) * mm});
            skLineSegment(sketch, "E1666", {"start": v(1.14, -2.8) * mm, "end": v(1.3, -1.72) * mm});
            skLineSegment(sketch, "E1667", {"start": v(1.3, -1.72) * mm, "end": v(1.52, -0.72) * mm});
            skLineSegment(sketch, "E1668", {"start": v(1.52, -0.72) * mm, "end": v(1.8, 0.2) * mm});
            skLineSegment(sketch, "E1669", {"start": v(1.8, 0.2) * mm, "end": v(2.16, 1.01) * mm});
            skLineSegment(sketch, "E1670", {"start": v(2.16, 1.01) * mm, "end": v(2.57, 1.75) * mm});
            skLineSegment(sketch, "E1671", {"start": v(2.57, 1.75) * mm, "end": v(3.05, 2.4) * mm});
            skLineSegment(sketch, "E1672", {"start": v(3.05, 2.4) * mm, "end": v(3.6, 2.96) * mm});
            skLineSegment(sketch, "E1673", {"start": v(3.6, 2.96) * mm, "end": v(4.25, 3.45) * mm});
            skLineSegment(sketch, "E1674", {"start": v(4.25, 3.45) * mm, "end": v(5, 3.86) * mm});
            skLineSegment(sketch, "E1675", {"start": v(5, 3.86) * mm, "end": v(5.83, 4.2) * mm});
            skLineSegment(sketch, "E1676", {"start": v(5.83, 4.2) * mm, "end": v(6.77, 4.47) * mm});
            skLineSegment(sketch, "E1677", {"start": v(6.77, 4.47) * mm, "end": v(7.8, 4.66) * mm});
            skLineSegment(sketch, "E1678", {"start": v(7.8, 4.66) * mm, "end": v(8.91, 4.77) * mm});
            skLineSegment(sketch, "E1679", {"start": v(8.91, 4.77) * mm, "end": v(10.13, 4.8) * mm});
            skLineSegment(sketch, "E1680", {"start": v(10.13, 4.8) * mm, "end": v(11.03, 4.82) * mm});
            skLineSegment(sketch, "E1681", {"start": v(11.03, 4.82) * mm, "end": v(11.94, 4.84) * mm});
            skLineSegment(sketch, "E1682", {"start": v(11.94, 4.84) * mm, "end": v(12.85, 4.86) * mm});
            skLineSegment(sketch, "E1683", {"start": v(12.85, 4.86) * mm, "end": v(13.75, 4.87) * mm});
            skLineSegment(sketch, "E1684", {"start": v(13.75, 4.87) * mm, "end": v(14.66, 4.89) * mm});
            skLineSegment(sketch, "E1685", {"start": v(14.66, 4.89) * mm, "end": v(15.57, 4.9) * mm});
            skLineSegment(sketch, "E1686", {"start": v(15.57, 4.9) * mm, "end": v(16.47, 4.92) * mm});
            skLineSegment(sketch, "E1687", {"start": v(16.47, 4.92) * mm, "end": v(17.38, 4.94) * mm});
            skLineSegment(sketch, "E1688", {"start": v(17.38, 4.94) * mm, "end": v(18.18, 4.93) * mm});
            skLineSegment(sketch, "E1689", {"start": v(18.18, 4.93) * mm, "end": v(18.95, 4.92) * mm});
            skLineSegment(sketch, "E1690", {"start": v(18.95, 4.92) * mm, "end": v(19.68, 4.89) * mm});
            skLineSegment(sketch, "E1691", {"start": v(19.68, 4.89) * mm, "end": v(20.38, 4.85) * mm});
            skLineSegment(sketch, "E1692", {"start": v(20.38, 4.85) * mm, "end": v(21.04, 4.8) * mm});
            skLineSegment(sketch, "E1693", {"start": v(21.04, 4.8) * mm, "end": v(21.67, 4.74) * mm});
            skLineSegment(sketch, "E1694", {"start": v(21.67, 4.74) * mm, "end": v(22.26, 4.67) * mm});
            skLineSegment(sketch, "E1695", {"start": v(22.26, 4.67) * mm, "end": v(22.82, 4.59) * mm});
            skLineSegment(sketch, "E1696", {"start": v(22.82, 4.59) * mm, "end": v(23.35, 4.48) * mm});
            skLineSegment(sketch, "E1697", {"start": v(23.35, 4.48) * mm, "end": v(23.86, 4.35) * mm});
            skLineSegment(sketch, "E1698", {"start": v(23.86, 4.35) * mm, "end": v(24.36, 4.19) * mm});
            skLineSegment(sketch, "E1699", {"start": v(24.36, 4.19) * mm, "end": v(24.83, 4) * mm});
            skLineSegment(sketch, "E1700", {"start": v(24.83, 4) * mm, "end": v(25.29, 3.78) * mm});
            skLineSegment(sketch, "E1701", {"start": v(25.29, 3.78) * mm, "end": v(25.72, 3.53) * mm});
            skLineSegment(sketch, "E1702", {"start": v(25.72, 3.53) * mm, "end": v(26.14, 3.25) * mm});
            skLineSegment(sketch, "E1703", {"start": v(26.14, 3.25) * mm, "end": v(26.53, 2.95) * mm});
            skLineSegment(sketch, "E1704", {"start": v(26.53, 2.95) * mm, "end": v(26.9, 2.62) * mm});
            skLineSegment(sketch, "E1705", {"start": v(26.9, 2.62) * mm, "end": v(27.24, 2.27) * mm});
            skLineSegment(sketch, "E1706", {"start": v(27.24, 2.27) * mm, "end": v(27.55, 1.9) * mm});
            skLineSegment(sketch, "E1707", {"start": v(27.55, 1.9) * mm, "end": v(27.82, 1.51) * mm});
            skLineSegment(sketch, "E1708", {"start": v(27.82, 1.51) * mm, "end": v(28.06, 1.1) * mm});
            skLineSegment(sketch, "E1709", {"start": v(28.06, 1.1) * mm, "end": v(28.27, 0.68) * mm});
            skLineSegment(sketch, "E1710", {"start": v(28.27, 0.68) * mm, "end": v(28.45, 0.23) * mm});
            skLineSegment(sketch, "E1711", {"start": v(28.45, 0.23) * mm, "end": v(28.6, -0.24) * mm});
            skLineSegment(sketch, "E1712", {"start": v(28.6, -0.24) * mm, "end": v(28.71, -0.73) * mm});
            skLineSegment(sketch, "E1713", {"start": v(28.71, -0.73) * mm, "end": v(28.81, -1.27) * mm});
            skLineSegment(sketch, "E1714", {"start": v(28.81, -1.27) * mm, "end": v(28.9, -1.85) * mm});
            skLineSegment(sketch, "E1715", {"start": v(28.9, -1.85) * mm, "end": v(28.97, -2.45) * mm});
            skLineSegment(sketch, "E1716", {"start": v(28.97, -2.45) * mm, "end": v(29.03, -3.06) * mm});
            skLineSegment(sketch, "E1717", {"start": v(29.03, -3.06) * mm, "end": v(29.07, -3.68) * mm});
            skLineSegment(sketch, "E1718", {"start": v(29.07, -3.68) * mm, "end": v(29.09, -4.3) * mm});
            skLineSegment(sketch, "E1719", {"start": v(29.09, -4.3) * mm, "end": v(29.1, -4.92) * mm});
            skLineSegment(sketch, "E1720", {"start": v(29.1, -4.92) * mm, "end": v(29.1, -5.06) * mm});
            skLineSegment(sketch, "E1721", {"start": v(29.1, -5.06) * mm, "end": v(29.1, -5.2) * mm});
            skLineSegment(sketch, "E1722", {"start": v(29.1, -5.2) * mm, "end": v(29.1, -5.34) * mm});
            skLineSegment(sketch, "E1723", {"start": v(29.1, -5.34) * mm, "end": v(29.1, -5.48) * mm});
            skLineSegment(sketch, "E1724", {"start": v(29.1, -5.48) * mm, "end": v(29.1, -5.63) * mm});
            skLineSegment(sketch, "E1725", {"start": v(29.1, -5.63) * mm, "end": v(29.09, -5.79) * mm});
            skLineSegment(sketch, "E1726", {"start": v(29.09, -5.79) * mm, "end": v(29.08, -5.95) * mm});
            skLineSegment(sketch, "E1727", {"start": v(29.08, -5.95) * mm, "end": v(29.08, -6.11) * mm});
            skLineSegment(sketch, "E1728", {"start": v(29.08, -6.11) * mm, "end": v(29.07, -6.3) * mm});
            skLineSegment(sketch, "E1729", {"start": v(29.07, -6.3) * mm, "end": v(29.07, -6.5) * mm});
            skLineSegment(sketch, "E1730", {"start": v(29.07, -6.5) * mm, "end": v(29.07, -6.74) * mm});
            skLineSegment(sketch, "E1731", {"start": v(29.07, -6.74) * mm, "end": v(29.06, -6.98) * mm});
            skLineSegment(sketch, "E1732", {"start": v(29.06, -6.98) * mm, "end": v(29.06, -7.23) * mm});
            skLineSegment(sketch, "E1733", {"start": v(29.06, -7.23) * mm, "end": v(29.06, -7.48) * mm});
            skLineSegment(sketch, "E1734", {"start": v(29.06, -7.48) * mm, "end": v(29.06, -7.72) * mm});
            skLineSegment(sketch, "E1735", {"start": v(29.06, -7.72) * mm, "end": v(29.06, -7.94) * mm});
            skLineSegment(sketch, "E1736", {"start": v(29.06, -7.94) * mm, "end": v(26.52, -7.94) * mm});
            skLineSegment(sketch, "E1737", {"start": v(26.52, -7.94) * mm, "end": v(24, -7.94) * mm});
            skLineSegment(sketch, "E1738", {"start": v(24, -7.94) * mm, "end": v(21.46, -7.94) * mm});
            skLineSegment(sketch, "E1739", {"start": v(21.46, -7.94) * mm, "end": v(18.93, -7.94) * mm});
            skLineSegment(sketch, "E1740", {"start": v(18.93, -7.94) * mm, "end": v(16.4, -7.94) * mm});
            skLineSegment(sketch, "E1741", {"start": v(16.4, -7.94) * mm, "end": v(13.86, -7.94) * mm});
            skLineSegment(sketch, "E1742", {"start": v(13.86, -7.94) * mm, "end": v(11.33, -7.94) * mm});
            skLineSegment(sketch, "E1743", {"start": v(11.33, -7.94) * mm, "end": v(8.8, -7.94) * mm});
            skLineSegment(sketch, "E1744", {"start": v(8.8, -7.94) * mm, "end": v(8.8, -8.5) * mm});
            skLineSegment(sketch, "E1745", {"start": v(8.8, -8.5) * mm, "end": v(8.85, -8.96) * mm});
            skLineSegment(sketch, "E1746", {"start": v(8.85, -8.96) * mm, "end": v(8.92, -9.35) * mm});
            skLineSegment(sketch, "E1747", {"start": v(8.92, -9.35) * mm, "end": v(9.01, -9.68) * mm});
            skLineSegment(sketch, "E1748", {"start": v(9.01, -9.68) * mm, "end": v(9.13, -9.97) * mm});
            skLineSegment(sketch, "E1749", {"start": v(9.13, -9.97) * mm, "end": v(9.29, -10.22) * mm});
            skLineSegment(sketch, "E1750", {"start": v(9.29, -10.22) * mm, "end": v(9.47, -10.46) * mm});
            skLineSegment(sketch, "E1751", {"start": v(9.47, -10.46) * mm, "end": v(9.68, -10.7) * mm});
            skLineSegment(sketch, "E1752", {"start": v(9.68, -10.7) * mm, "end": v(10.11, -11.05) * mm});
            skLineSegment(sketch, "E1753", {"start": v(10.11, -11.05) * mm, "end": v(10.6, -11.33) * mm});
            skLineSegment(sketch, "E1754", {"start": v(10.6, -11.33) * mm, "end": v(11.13, -11.53) * mm});
            skLineSegment(sketch, "E1755", {"start": v(11.13, -11.53) * mm, "end": v(11.64, -11.68) * mm});
            skLineSegment(sketch, "E1756", {"start": v(11.64, -11.68) * mm, "end": v(12.1, -11.77) * mm});
            skLineSegment(sketch, "E1757", {"start": v(12.1, -11.77) * mm, "end": v(12.48, -11.82) * mm});
            skLineSegment(sketch, "E1758", {"start": v(12.48, -11.82) * mm, "end": v(12.73, -11.84) * mm});
            skLineSegment(sketch, "E1759", {"start": v(12.73, -11.84) * mm, "end": v(12.82, -11.84) * mm});
            skLineSegment(sketch, "E1760", {"start": v(12.82, -11.84) * mm, "end": v(13.37, -11.86) * mm});
            skLineSegment(sketch, "E1761", {"start": v(13.37, -11.86) * mm, "end": v(13.9, -11.87) * mm});
            skLineSegment(sketch, "E1762", {"start": v(13.9, -11.87) * mm, "end": v(14.45, -11.88) * mm});
            skLineSegment(sketch, "E1763", {"start": v(14.45, -11.88) * mm, "end": v(15, -11.89) * mm});
            skLineSegment(sketch, "E1764", {"start": v(15, -11.89) * mm, "end": v(15.54, -11.9) * mm});
            skLineSegment(sketch, "E1765", {"start": v(15.54, -11.9) * mm, "end": v(16.09, -11.9) * mm});
            skLineSegment(sketch, "E1766", {"start": v(16.09, -11.9) * mm, "end": v(16.63, -11.92) * mm});
            skLineSegment(sketch, "E1767", {"start": v(16.63, -11.92) * mm, "end": v(17.17, -11.93) * mm});
            skLineSegment(sketch, "E1768", {"start": v(17.17, -11.93) * mm, "end": v(17.34, -11.93) * mm});
            skLineSegment(sketch, "E1769", {"start": v(17.34, -11.93) * mm, "end": v(17.8, -11.93) * mm});
            skLineSegment(sketch, "E1770", {"start": v(17.8, -11.93) * mm, "end": v(18.5, -11.92) * mm});
            skLineSegment(sketch, "E1771", {"start": v(18.5, -11.92) * mm, "end": v(19.38, -11.9) * mm});
            skLineSegment(sketch, "E1772", {"start": v(19.38, -11.9) * mm, "end": v(20.4, -11.84) * mm});
            skLineSegment(sketch, "E1773", {"start": v(20.4, -11.84) * mm, "end": v(21.48, -11.76) * mm});
            skLineSegment(sketch, "E1774", {"start": v(21.48, -11.76) * mm, "end": v(22.6, -11.63) * mm});
            skLineSegment(sketch, "E1775", {"start": v(22.6, -11.63) * mm, "end": v(23.67, -11.47) * mm});
            skLineSegment(sketch, "E1776", {"start": v(23.67, -11.47) * mm, "end": v(25.02, -11.17) * mm});
            skLineSegment(sketch, "E1777", {"start": v(25.02, -11.17) * mm, "end": v(26.12, -10.83) * mm});
            skLineSegment(sketch, "E1778", {"start": v(26.12, -10.83) * mm, "end": v(26.98, -10.49) * mm});
            skLineSegment(sketch, "E1779", {"start": v(26.98, -10.49) * mm, "end": v(27.63, -10.15) * mm});
            skLineSegment(sketch, "E1780", {"start": v(27.63, -10.15) * mm, "end": v(28.1, -9.86) * mm});
            skLineSegment(sketch, "E1781", {"start": v(28.1, -9.86) * mm, "end": v(28.4, -9.61) * mm});
            skLineSegment(sketch, "E1782", {"start": v(28.4, -9.61) * mm, "end": v(28.56, -9.45) * mm});
            skLineSegment(sketch, "E1783", {"start": v(28.56, -9.45) * mm, "end": v(28.6, -9.4) * mm});
            skLineSegment(sketch, "E1784", {"start": v(28.6, -9.4) * mm, "end": v(28.58, -9.55) * mm});
            skLineSegment(sketch, "E1785", {"start": v(28.58, -9.55) * mm, "end": v(28.48, -10) * mm});
            skLineSegment(sketch, "E1786", {"start": v(28.48, -10) * mm, "end": v(28.3, -10.65) * mm});
            skLineSegment(sketch, "E1787", {"start": v(28.3, -10.65) * mm, "end": v(28, -11.44) * mm});
            skLineSegment(sketch, "E1788", {"start": v(28, -11.44) * mm, "end": v(27.58, -12.32) * mm});
            skLineSegment(sketch, "E1789", {"start": v(27.58, -12.32) * mm, "end": v(27.02, -13.22) * mm});
            skLineSegment(sketch, "E1790", {"start": v(27.02, -13.22) * mm, "end": v(26.3, -14.06) * mm});
            skLineSegment(sketch, "E1791", {"start": v(26.3, -14.06) * mm, "end": v(25.4, -14.78) * mm});
            skLineSegment(sketch, "E1792", {"start": v(25.4, -14.78) * mm, "end": v(24.62, -15.23) * mm});
            skLineSegment(sketch, "E1793", {"start": v(24.62, -15.23) * mm, "end": v(23.82, -15.62) * mm});
            skLineSegment(sketch, "E1794", {"start": v(23.82, -15.62) * mm, "end": v(22.99, -15.93) * mm});
            skLineSegment(sketch, "E1795", {"start": v(22.99, -15.93) * mm, "end": v(22.09, -16.18) * mm});
            skLineSegment(sketch, "E1796", {"start": v(22.09, -16.18) * mm, "end": v(21.12, -16.37) * mm});
            skLineSegment(sketch, "E1797", {"start": v(21.12, -16.37) * mm, "end": v(20.05, -16.5) * mm});
            skLineSegment(sketch, "E1798", {"start": v(20.05, -16.5) * mm, "end": v(18.87, -16.58) * mm});
            skLineSegment(sketch, "E1799", {"start": v(18.87, -16.58) * mm, "end": v(17.56, -16.6) * mm});
            skLineSegment(sketch, "E1800", {"start": v(13.93, 0.34) * mm, "end": v(13.34, 0.33) * mm});
            skLineSegment(sketch, "E1801", {"start": v(13.34, 0.33) * mm, "end": v(12.78, 0.3) * mm});
            skLineSegment(sketch, "E1802", {"start": v(12.78, 0.3) * mm, "end": v(12.25, 0.27) * mm});
            skLineSegment(sketch, "E1803", {"start": v(12.25, 0.27) * mm, "end": v(11.76, 0.21) * mm});
            skLineSegment(sketch, "E1804", {"start": v(11.76, 0.21) * mm, "end": v(11.3, 0.14) * mm});
            skLineSegment(sketch, "E1805", {"start": v(11.3, 0.14) * mm, "end": v(10.88, 0.05) * mm});
            skLineSegment(sketch, "E1806", {"start": v(10.88, 0.05) * mm, "end": v(10.48, -0.05) * mm});
            skLineSegment(sketch, "E1807", {"start": v(10.48, -0.05) * mm, "end": v(10.13, -0.17) * mm});
            skLineSegment(sketch, "E1808", {"start": v(10.13, -0.17) * mm, "end": v(9.8, -0.34) * mm});
            skLineSegment(sketch, "E1809", {"start": v(9.8, -0.34) * mm, "end": v(9.53, -0.57) * mm});
            skLineSegment(sketch, "E1810", {"start": v(9.53, -0.57) * mm, "end": v(9.29, -0.88) * mm});
            skLineSegment(sketch, "E1811", {"start": v(9.29, -0.88) * mm, "end": v(9.1, -1.24) * mm});
            skLineSegment(sketch, "E1812", {"start": v(9.1, -1.24) * mm, "end": v(8.95, -1.64) * mm});
            skLineSegment(sketch, "E1813", {"start": v(8.95, -1.64) * mm, "end": v(8.84, -2.09) * mm});
            skLineSegment(sketch, "E1814", {"start": v(8.84, -2.09) * mm, "end": v(8.78, -2.56) * mm});
            skLineSegment(sketch, "E1815", {"start": v(8.78, -2.56) * mm, "end": v(8.75, -3.06) * mm});
            skLineSegment(sketch, "E1816", {"start": v(8.75, -3.06) * mm, "end": v(8.76, -3.13) * mm});
            skLineSegment(sketch, "E1817", {"start": v(8.76, -3.13) * mm, "end": v(8.77, -3.2) * mm});
            skLineSegment(sketch, "E1818", {"start": v(8.77, -3.2) * mm, "end": v(8.77, -3.28) * mm});
            skLineSegment(sketch, "E1819", {"start": v(8.77, -3.28) * mm, "end": v(8.78, -3.35) * mm});
            skLineSegment(sketch, "E1820", {"start": v(8.78, -3.35) * mm, "end": v(8.78, -3.42) * mm});
            skLineSegment(sketch, "E1821", {"start": v(8.78, -3.42) * mm, "end": v(8.79, -3.5) * mm});
            skLineSegment(sketch, "E1822", {"start": v(8.79, -3.5) * mm, "end": v(8.8, -3.56) * mm});
            skLineSegment(sketch, "E1823", {"start": v(8.8, -3.56) * mm, "end": v(8.8, -3.64) * mm});
            skLineSegment(sketch, "E1824", {"start": v(8.8, -3.64) * mm, "end": v(10.38, -3.64) * mm});
            skLineSegment(sketch, "E1825", {"start": v(10.38, -3.64) * mm, "end": v(11.97, -3.64) * mm});
            skLineSegment(sketch, "E1826", {"start": v(11.97, -3.64) * mm, "end": v(13.56, -3.64) * mm});
            skLineSegment(sketch, "E1827", {"start": v(13.56, -3.64) * mm, "end": v(15.14, -3.64) * mm});
            skLineSegment(sketch, "E1828", {"start": v(15.14, -3.64) * mm, "end": v(16.73, -3.64) * mm});
            skLineSegment(sketch, "E1829", {"start": v(16.73, -3.64) * mm, "end": v(18.32, -3.64) * mm});
            skLineSegment(sketch, "E1830", {"start": v(18.32, -3.64) * mm, "end": v(19.9, -3.64) * mm});
            skLineSegment(sketch, "E1831", {"start": v(19.9, -3.64) * mm, "end": v(21.5, -3.64) * mm});
            skLineSegment(sketch, "E1832", {"start": v(21.5, -3.64) * mm, "end": v(21.48, -3.08) * mm});
            skLineSegment(sketch, "E1833", {"start": v(21.48, -3.08) * mm, "end": v(21.42, -2.55) * mm});
            skLineSegment(sketch, "E1834", {"start": v(21.42, -2.55) * mm, "end": v(21.34, -2.05) * mm});
            skLineSegment(sketch, "E1835", {"start": v(21.34, -2.05) * mm, "end": v(21.22, -1.6) * mm});
            skLineSegment(sketch, "E1836", {"start": v(21.22, -1.6) * mm, "end": v(21.06, -1.2) * mm});
            skLineSegment(sketch, "E1837", {"start": v(21.06, -1.2) * mm, "end": v(20.87, -0.84) * mm});
            skLineSegment(sketch, "E1838", {"start": v(20.87, -0.84) * mm, "end": v(20.64, -0.56) * mm});
            skLineSegment(sketch, "E1839", {"start": v(20.64, -0.56) * mm, "end": v(20.39, -0.35) * mm});
            skLineSegment(sketch, "E1840", {"start": v(20.39, -0.35) * mm, "end": v(20.09, -0.19) * mm});
            skLineSegment(sketch, "E1841", {"start": v(20.09, -0.19) * mm, "end": v(19.75, -0.05) * mm});
            skLineSegment(sketch, "E1842", {"start": v(19.75, -0.05) * mm, "end": v(19.36, 0.07) * mm});
            skLineSegment(sketch, "E1843", {"start": v(19.36, 0.07) * mm, "end": v(18.94, 0.17) * mm});
            skLineSegment(sketch, "E1844", {"start": v(18.94, 0.17) * mm, "end": v(18.47, 0.24) * mm});
            skLineSegment(sketch, "E1845", {"start": v(18.47, 0.24) * mm, "end": v(17.96, 0.3) * mm});
            skLineSegment(sketch, "E1846", {"start": v(17.96, 0.3) * mm, "end": v(17.4, 0.33) * mm});
            skLineSegment(sketch, "E1847", {"start": v(17.4, 0.33) * mm, "end": v(16.8, 0.34) * mm});
            skLineSegment(sketch, "E1848", {"start": v(16.8, 0.34) * mm, "end": v(16.44, 0.34) * mm});
            skLineSegment(sketch, "E1849", {"start": v(16.44, 0.34) * mm, "end": v(16.08, 0.34) * mm});
            skLineSegment(sketch, "E1850", {"start": v(16.08, 0.34) * mm, "end": v(15.72, 0.34) * mm});
            skLineSegment(sketch, "E1851", {"start": v(15.72, 0.34) * mm, "end": v(15.36, 0.34) * mm});
            skLineSegment(sketch, "E1852", {"start": v(15.36, 0.34) * mm, "end": v(15, 0.34) * mm});
            skLineSegment(sketch, "E1853", {"start": v(15, 0.34) * mm, "end": v(14.65, 0.34) * mm});
            skLineSegment(sketch, "E1854", {"start": v(14.65, 0.34) * mm, "end": v(14.29, 0.34) * mm});
            skLineSegment(sketch, "E1855", {"start": v(14.29, 0.34) * mm, "end": v(13.93, 0.34) * mm});
            skLineSegment(sketch, "E1856", {"start": v(17.56, -18.07) * mm, "end": v(17.55, -18.07) * mm});
            skLineSegment(sketch, "E1857", {"start": v(17.55, -18.07) * mm, "end": v(17.54, -18.07) * mm});
            skLineSegment(sketch, "E1858", {"start": v(17.54, -18.07) * mm, "end": v(17.54, -18.07) * mm});
            skLineSegment(sketch, "E1859", {"start": v(17.54, -18.07) * mm, "end": v(17.53, -18.07) * mm});
            skLineSegment(sketch, "E1860", {"start": v(17.53, -18.07) * mm, "end": v(17.52, -18.07) * mm});
            skLineSegment(sketch, "E1861", {"start": v(17.52, -18.07) * mm, "end": v(17.52, -18.07) * mm});
            skLineSegment(sketch, "E1862", {"start": v(17.52, -18.07) * mm, "end": v(17.5, -18.07) * mm});
            skLineSegment(sketch, "E1863", {"start": v(17.5, -18.07) * mm, "end": v(17.5, -18.07) * mm});
            skLineSegment(sketch, "E1864", {"start": v(17.5, -18.07) * mm, "end": v(16.58, -18.04) * mm});
            skLineSegment(sketch, "E1865", {"start": v(16.58, -18.04) * mm, "end": v(15.66, -18) * mm});
            skLineSegment(sketch, "E1866", {"start": v(15.66, -18) * mm, "end": v(14.74, -17.97) * mm});
            skLineSegment(sketch, "E1867", {"start": v(14.74, -17.97) * mm, "end": v(13.82, -17.94) * mm});
            skLineSegment(sketch, "E1868", {"start": v(13.82, -17.94) * mm, "end": v(12.9, -17.9) * mm});
            skLineSegment(sketch, "E1869", {"start": v(12.9, -17.9) * mm, "end": v(11.98, -17.87) * mm});
            skLineSegment(sketch, "E1870", {"start": v(11.98, -17.87) * mm, "end": v(11.06, -17.84) * mm});
            skLineSegment(sketch, "E1871", {"start": v(11.06, -17.84) * mm, "end": v(10.14, -17.8) * mm});
            skLineSegment(sketch, "E1872", {"start": v(10.14, -17.8) * mm, "end": v(8.7, -17.75) * mm});
            skLineSegment(sketch, "E1873", {"start": v(8.7, -17.75) * mm, "end": v(7.36, -17.6) * mm});
            skLineSegment(sketch, "E1874", {"start": v(7.36, -17.6) * mm, "end": v(6.13, -17.33) * mm});
            skLineSegment(sketch, "E1875", {"start": v(6.13, -17.33) * mm, "end": v(5.02, -16.97) * mm});
            skLineSegment(sketch, "E1876", {"start": v(5.02, -16.97) * mm, "end": v(4.03, -16.5) * mm});
            skLineSegment(sketch, "E1877", {"start": v(4.03, -16.5) * mm, "end": v(3.15, -15.93) * mm});
            skLineSegment(sketch, "E1878", {"start": v(3.15, -15.93) * mm, "end": v(2.39, -15.26) * mm});
            skLineSegment(sketch, "E1879", {"start": v(2.39, -15.26) * mm, "end": v(1.74, -14.5) * mm});
            skLineSegment(sketch, "E1880", {"start": v(1.74, -14.5) * mm, "end": v(1.22, -13.67) * mm});
            skLineSegment(sketch, "E1881", {"start": v(1.22, -13.67) * mm, "end": v(0.77, -12.76) * mm});
            skLineSegment(sketch, "E1882", {"start": v(0.77, -12.76) * mm, "end": v(0.4, -11.75) * mm});
            skLineSegment(sketch, "E1883", {"start": v(0.4, -11.75) * mm, "end": v(0.09, -10.65) * mm});
            skLineSegment(sketch, "E1884", {"start": v(0.09, -10.65) * mm, "end": v(-0.15, -9.44) * mm});
            skLineSegment(sketch, "E1885", {"start": v(-0.15, -9.44) * mm, "end": v(-0.32, -8.14) * mm});
            skLineSegment(sketch, "E1886", {"start": v(-0.32, -8.14) * mm, "end": v(-0.42, -6.74) * mm});
            skLineSegment(sketch, "E1887", {"start": v(-0.42, -6.74) * mm, "end": v(-0.46, -5.24) * mm});
            skLineSegment(sketch, "E1888", {"start": v(-0.46, -5.24) * mm, "end": v(-0.42, -3.83) * mm});
            skLineSegment(sketch, "E1889", {"start": v(-0.42, -3.83) * mm, "end": v(-0.3, -2.53) * mm});
            skLineSegment(sketch, "E1890", {"start": v(-0.3, -2.53) * mm, "end": v(-0.13, -1.32) * mm});
            skLineSegment(sketch, "E1891", {"start": v(-0.13, -1.32) * mm, "end": v(0.13, -0.21) * mm});
            skLineSegment(sketch, "E1892", {"start": v(0.13, -0.21) * mm, "end": v(0.47, 0.81) * mm});
            skLineSegment(sketch, "E1893", {"start": v(0.47, 0.81) * mm, "end": v(0.88, 1.74) * mm});
            skLineSegment(sketch, "E1894", {"start": v(0.88, 1.74) * mm, "end": v(1.36, 2.58) * mm});
            skLineSegment(sketch, "E1895", {"start": v(1.36, 2.58) * mm, "end": v(1.92, 3.34) * mm});
            skLineSegment(sketch, "E1896", {"start": v(1.92, 3.34) * mm, "end": v(2.6, 4.03) * mm});
            skLineSegment(sketch, "E1897", {"start": v(2.6, 4.03) * mm, "end": v(3.37, 4.62) * mm});
            skLineSegment(sketch, "E1898", {"start": v(3.37, 4.62) * mm, "end": v(4.24, 5.12) * mm});
            skLineSegment(sketch, "E1899", {"start": v(4.24, 5.12) * mm, "end": v(5.22, 5.54) * mm});
            skLineSegment(sketch, "E1900", {"start": v(5.22, 5.54) * mm, "end": v(6.3, 5.86) * mm});
            skLineSegment(sketch, "E1901", {"start": v(6.3, 5.86) * mm, "end": v(7.47, 6.1) * mm});
            skLineSegment(sketch, "E1902", {"start": v(7.47, 6.1) * mm, "end": v(8.75, 6.23) * mm});
            skLineSegment(sketch, "E1903", {"start": v(8.75, 6.23) * mm, "end": v(10.13, 6.27) * mm});
            skLineSegment(sketch, "E1904", {"start": v(10.13, 6.27) * mm, "end": v(11.03, 6.3) * mm});
            skLineSegment(sketch, "E1905", {"start": v(11.03, 6.3) * mm, "end": v(11.93, 6.3) * mm});
            skLineSegment(sketch, "E1906", {"start": v(11.93, 6.3) * mm, "end": v(12.84, 6.32) * mm});
            skLineSegment(sketch, "E1907", {"start": v(12.84, 6.32) * mm, "end": v(13.74, 6.34) * mm});
            skLineSegment(sketch, "E1908", {"start": v(13.74, 6.34) * mm, "end": v(14.64, 6.36) * mm});
            skLineSegment(sketch, "E1909", {"start": v(14.64, 6.36) * mm, "end": v(15.55, 6.37) * mm});
            skLineSegment(sketch, "E1910", {"start": v(15.55, 6.37) * mm, "end": v(16.45, 6.39) * mm});
            skLineSegment(sketch, "E1911", {"start": v(16.45, 6.39) * mm, "end": v(17.35, 6.4) * mm});
            skLineSegment(sketch, "E1912", {"start": v(17.35, 6.4) * mm, "end": v(17.35, 6.4) * mm});
            skLineSegment(sketch, "E1913", {"start": v(17.35, 6.4) * mm, "end": v(17.36, 6.4) * mm});
            skLineSegment(sketch, "E1914", {"start": v(17.36, 6.4) * mm, "end": v(17.36, 6.4) * mm});
            skLineSegment(sketch, "E1915", {"start": v(17.36, 6.4) * mm, "end": v(18.2, 6.4) * mm});
            skLineSegment(sketch, "E1916", {"start": v(18.2, 6.4) * mm, "end": v(19.02, 6.38) * mm});
            skLineSegment(sketch, "E1917", {"start": v(19.02, 6.38) * mm, "end": v(19.78, 6.35) * mm});
            skLineSegment(sketch, "E1918", {"start": v(19.78, 6.35) * mm, "end": v(20.5, 6.31) * mm});
            skLineSegment(sketch, "E1919", {"start": v(20.5, 6.31) * mm, "end": v(21.2, 6.26) * mm});
            skLineSegment(sketch, "E1920", {"start": v(21.2, 6.26) * mm, "end": v(21.85, 6.2) * mm});
            skLineSegment(sketch, "E1921", {"start": v(21.85, 6.2) * mm, "end": v(22.47, 6.12) * mm});
            skLineSegment(sketch, "E1922", {"start": v(22.47, 6.12) * mm, "end": v(23.06, 6.03) * mm});
            skLineSegment(sketch, "E1923", {"start": v(23.06, 6.03) * mm, "end": v(23.68, 5.91) * mm});
            skLineSegment(sketch, "E1924", {"start": v(23.68, 5.91) * mm, "end": v(24.3, 5.75) * mm});
            skLineSegment(sketch, "E1925", {"start": v(24.3, 5.75) * mm, "end": v(24.88, 5.56) * mm});
            skLineSegment(sketch, "E1926", {"start": v(24.88, 5.56) * mm, "end": v(25.44, 5.33) * mm});
            skLineSegment(sketch, "E1927", {"start": v(25.44, 5.33) * mm, "end": v(25.98, 5.07) * mm});
            skLineSegment(sketch, "E1928", {"start": v(25.98, 5.07) * mm, "end": v(26.5, 4.77) * mm});
            skLineSegment(sketch, "E1929", {"start": v(26.5, 4.77) * mm, "end": v(27, 4.44) * mm});
            skLineSegment(sketch, "E1930", {"start": v(27, 4.44) * mm, "end": v(27.47, 4.07) * mm});
            skLineSegment(sketch, "E1931", {"start": v(27.47, 4.07) * mm, "end": v(27.93, 3.67) * mm});
            skLineSegment(sketch, "E1932", {"start": v(27.93, 3.67) * mm, "end": v(28.34, 3.24) * mm});
            skLineSegment(sketch, "E1933", {"start": v(28.34, 3.24) * mm, "end": v(28.72, 2.78) * mm});
            skLineSegment(sketch, "E1934", {"start": v(28.72, 2.78) * mm, "end": v(29.06, 2.3) * mm});
            skLineSegment(sketch, "E1935", {"start": v(29.06, 2.3) * mm, "end": v(29.36, 1.8) * mm});
            skLineSegment(sketch, "E1936", {"start": v(29.36, 1.8) * mm, "end": v(29.61, 1.27) * mm});
            skLineSegment(sketch, "E1937", {"start": v(29.61, 1.27) * mm, "end": v(29.83, 0.72) * mm});
            skLineSegment(sketch, "E1938", {"start": v(29.83, 0.72) * mm, "end": v(30, 0.14) * mm});
            skLineSegment(sketch, "E1939", {"start": v(30, 0.14) * mm, "end": v(30.13, -0.38) * mm});
            skLineSegment(sketch, "E1940", {"start": v(30.13, -0.38) * mm, "end": v(30.25, -0.94) * mm});
            skLineSegment(sketch, "E1941", {"start": v(30.25, -0.94) * mm, "end": v(30.34, -1.54) * mm});
            skLineSegment(sketch, "E1942", {"start": v(30.34, -1.54) * mm, "end": v(30.42, -2.17) * mm});
            skLineSegment(sketch, "E1943", {"start": v(30.42, -2.17) * mm, "end": v(30.48, -2.83) * mm});
            skLineSegment(sketch, "E1944", {"start": v(30.48, -2.83) * mm, "end": v(30.53, -3.52) * mm});
            skLineSegment(sketch, "E1945", {"start": v(30.53, -3.52) * mm, "end": v(30.56, -4.21) * mm});
            skLineSegment(sketch, "E1946", {"start": v(30.56, -4.21) * mm, "end": v(30.57, -4.92) * mm});
            skLineSegment(sketch, "E1947", {"start": v(30.57, -4.92) * mm, "end": v(30.56, -5.06) * mm});
            skLineSegment(sketch, "E1948", {"start": v(30.56, -5.06) * mm, "end": v(30.56, -5.2) * mm});
            skLineSegment(sketch, "E1949", {"start": v(30.56, -5.2) * mm, "end": v(30.56, -5.35) * mm});
            skLineSegment(sketch, "E1950", {"start": v(30.56, -5.35) * mm, "end": v(30.56, -5.5) * mm});
            skLineSegment(sketch, "E1951", {"start": v(30.56, -5.5) * mm, "end": v(30.56, -5.67) * mm});
            skLineSegment(sketch, "E1952", {"start": v(30.56, -5.67) * mm, "end": v(30.55, -5.83) * mm});
            skLineSegment(sketch, "E1953", {"start": v(30.55, -5.83) * mm, "end": v(30.55, -6) * mm});
            skLineSegment(sketch, "E1954", {"start": v(30.55, -6) * mm, "end": v(30.54, -6.17) * mm});
            skLineSegment(sketch, "E1955", {"start": v(30.54, -6.17) * mm, "end": v(30.54, -6.34) * mm});
            skLineSegment(sketch, "E1956", {"start": v(30.54, -6.34) * mm, "end": v(30.54, -6.54) * mm});
            skLineSegment(sketch, "E1957", {"start": v(30.54, -6.54) * mm, "end": v(30.53, -6.77) * mm});
            skLineSegment(sketch, "E1958", {"start": v(30.53, -6.77) * mm, "end": v(30.53, -7) * mm});
            skLineSegment(sketch, "E1959", {"start": v(30.53, -7) * mm, "end": v(30.53, -7.25) * mm});
            skLineSegment(sketch, "E1960", {"start": v(30.53, -7.25) * mm, "end": v(30.53, -7.5) * mm});
            skLineSegment(sketch, "E1961", {"start": v(30.53, -7.5) * mm, "end": v(30.52, -7.72) * mm});
            skLineSegment(sketch, "E1962", {"start": v(30.52, -7.72) * mm, "end": v(30.52, -7.94) * mm});
            skLineSegment(sketch, "E1963", {"start": v(30.52, -7.94) * mm, "end": v(30.52, -8.12) * mm});
            skLineSegment(sketch, "E1964", {"start": v(30.52, -8.12) * mm, "end": v(30.52, -8.3) * mm});
            skLineSegment(sketch, "E1965", {"start": v(30.52, -8.3) * mm, "end": v(30.52, -8.49) * mm});
            skLineSegment(sketch, "E1966", {"start": v(30.52, -8.49) * mm, "end": v(30.52, -8.67) * mm});
            skLineSegment(sketch, "E1967", {"start": v(30.52, -8.67) * mm, "end": v(30.52, -8.85) * mm});
            skLineSegment(sketch, "E1968", {"start": v(30.52, -8.85) * mm, "end": v(30.52, -9.04) * mm});
            skLineSegment(sketch, "E1969", {"start": v(30.52, -9.04) * mm, "end": v(30.52, -9.22) * mm});
            skLineSegment(sketch, "E1970", {"start": v(30.52, -9.22) * mm, "end": v(30.52, -9.4) * mm});
            skLineSegment(sketch, "E1971", {"start": v(30.52, -9.4) * mm, "end": v(30.4, -9.4) * mm});
            skLineSegment(sketch, "E1972", {"start": v(30.4, -9.4) * mm, "end": v(30.28, -9.4) * mm});
            skLineSegment(sketch, "E1973", {"start": v(30.28, -9.4) * mm, "end": v(30.16, -9.4) * mm});
            skLineSegment(sketch, "E1974", {"start": v(30.16, -9.4) * mm, "end": v(30.04, -9.4) * mm});
            skLineSegment(sketch, "E1975", {"start": v(30.04, -9.4) * mm, "end": v(29.92, -9.4) * mm});
            skLineSegment(sketch, "E1976", {"start": v(29.92, -9.4) * mm, "end": v(29.8, -9.4) * mm});
            skLineSegment(sketch, "E1977", {"start": v(29.8, -9.4) * mm, "end": v(29.68, -9.4) * mm});
            skLineSegment(sketch, "E1978", {"start": v(29.68, -9.4) * mm, "end": v(29.56, -9.4) * mm});
            skLineSegment(sketch, "E1979", {"start": v(29.56, -9.4) * mm, "end": v(29.62, -9.43) * mm});
            skLineSegment(sketch, "E1980", {"start": v(29.62, -9.43) * mm, "end": v(29.68, -9.45) * mm});
            skLineSegment(sketch, "E1981", {"start": v(29.68, -9.45) * mm, "end": v(29.75, -9.48) * mm});
            skLineSegment(sketch, "E1982", {"start": v(29.75, -9.48) * mm, "end": v(29.8, -9.5) * mm});
            skLineSegment(sketch, "E1983", {"start": v(29.8, -9.5) * mm, "end": v(29.87, -9.53) * mm});
            skLineSegment(sketch, "E1984", {"start": v(29.87, -9.53) * mm, "end": v(29.93, -9.56) * mm});
            skLineSegment(sketch, "E1985", {"start": v(29.93, -9.56) * mm, "end": v(30, -9.58) * mm});
            skLineSegment(sketch, "E1986", {"start": v(30, -9.58) * mm, "end": v(30.06, -9.6) * mm});
            skLineSegment(sketch, "E1987", {"start": v(30.06, -9.6) * mm, "end": v(30.01, -9.85) * mm});
            skLineSegment(sketch, "E1988", {"start": v(30.01, -9.85) * mm, "end": v(29.9, -10.4) * mm});
            skLineSegment(sketch, "E1989", {"start": v(29.9, -10.4) * mm, "end": v(29.66, -11.17) * mm});
            skLineSegment(sketch, "E1990", {"start": v(29.66, -11.17) * mm, "end": v(29.3, -12.1) * mm});
            skLineSegment(sketch, "E1991", {"start": v(29.3, -12.1) * mm, "end": v(28.8, -13.13) * mm});
            skLineSegment(sketch, "E1992", {"start": v(28.8, -13.13) * mm, "end": v(28.13, -14.17) * mm});
            skLineSegment(sketch, "E1993", {"start": v(28.13, -14.17) * mm, "end": v(27.27, -15.16) * mm});
            skLineSegment(sketch, "E1994", {"start": v(27.27, -15.16) * mm, "end": v(26.18, -16.02) * mm});
            skLineSegment(sketch, "E1995", {"start": v(26.18, -16.02) * mm, "end": v(25.3, -16.53) * mm});
            skLineSegment(sketch, "E1996", {"start": v(25.3, -16.53) * mm, "end": v(24.4, -16.96) * mm});
            skLineSegment(sketch, "E1997", {"start": v(24.4, -16.96) * mm, "end": v(23.47, -17.32) * mm});
            skLineSegment(sketch, "E1998", {"start": v(23.47, -17.32) * mm, "end": v(22.46, -17.6) * mm});
            skLineSegment(sketch, "E1999", {"start": v(22.46, -17.6) * mm, "end": v(21.39, -17.81) * mm});
            skLineSegment(sketch, "E2000", {"start": v(21.39, -17.81) * mm, "end": v(20.22, -17.96) * mm});
            skLineSegment(sketch, "E2001", {"start": v(20.22, -17.96) * mm, "end": v(18.95, -18.04) * mm});
            skLineSegment(sketch, "E2002", {"start": v(18.95, -18.04) * mm, "end": v(17.56, -18.07) * mm});
            skLineSegment(sketch, "E2003", {"start": v(17.38, 3.47) * mm, "end": v(16.48, 3.45) * mm});
            skLineSegment(sketch, "E2004", {"start": v(16.48, 3.45) * mm, "end": v(15.57, 3.44) * mm});
            skLineSegment(sketch, "E2005", {"start": v(15.57, 3.44) * mm, "end": v(14.67, 3.42) * mm});
            skLineSegment(sketch, "E2006", {"start": v(14.67, 3.42) * mm, "end": v(13.77, 3.4) * mm});
            skLineSegment(sketch, "E2007", {"start": v(13.77, 3.4) * mm, "end": v(12.86, 3.39) * mm});
            skLineSegment(sketch, "E2008", {"start": v(12.86, 3.39) * mm, "end": v(11.96, 3.37) * mm});
            skLineSegment(sketch, "E2009", {"start": v(11.96, 3.37) * mm, "end": v(11.06, 3.36) * mm});
            skLineSegment(sketch, "E2010", {"start": v(11.06, 3.36) * mm, "end": v(10.15, 3.34) * mm});
            skLineSegment(sketch, "E2011", {"start": v(10.15, 3.34) * mm, "end": v(9.1, 3.3) * mm});
            skLineSegment(sketch, "E2012", {"start": v(9.1, 3.3) * mm, "end": v(8.13, 3.22) * mm});
            skLineSegment(sketch, "E2013", {"start": v(8.13, 3.22) * mm, "end": v(7.25, 3.07) * mm});
            skLineSegment(sketch, "E2014", {"start": v(7.25, 3.07) * mm, "end": v(6.46, 2.86) * mm});
            skLineSegment(sketch, "E2015", {"start": v(6.46, 2.86) * mm, "end": v(5.76, 2.6) * mm});
            skLineSegment(sketch, "E2016", {"start": v(5.76, 2.6) * mm, "end": v(5.14, 2.27) * mm});
            skLineSegment(sketch, "E2017", {"start": v(5.14, 2.27) * mm, "end": v(4.61, 1.9) * mm});
            skLineSegment(sketch, "E2018", {"start": v(4.61, 1.9) * mm, "end": v(4.17, 1.45) * mm});
            skLineSegment(sketch, "E2019", {"start": v(4.17, 1.45) * mm, "end": v(3.77, 0.9) * mm});
            skLineSegment(sketch, "E2020", {"start": v(3.77, 0.9) * mm, "end": v(3.43, 0.28) * mm});
            skLineSegment(sketch, "E2021", {"start": v(3.43, 0.28) * mm, "end": v(3.14, -0.43) * mm});
            skLineSegment(sketch, "E2022", {"start": v(3.14, -0.43) * mm, "end": v(2.9, -1.23) * mm});
            skLineSegment(sketch, "E2023", {"start": v(2.9, -1.23) * mm, "end": v(2.72, -2.1) * mm});
            skLineSegment(sketch, "E2024", {"start": v(2.72, -2.1) * mm, "end": v(2.58, -3.07) * mm});
            skLineSegment(sketch, "E2025", {"start": v(2.58, -3.07) * mm, "end": v(2.5, -4.11) * mm});
            skLineSegment(sketch, "E2026", {"start": v(2.5, -4.11) * mm, "end": v(2.48, -5.24) * mm});
            skLineSegment(sketch, "E2027", {"start": v(2.48, -5.24) * mm, "end": v(2.5, -6.5) * mm});
            skLineSegment(sketch, "E2028", {"start": v(2.5, -6.5) * mm, "end": v(2.58, -7.67) * mm});
            skLineSegment(sketch, "E2029", {"start": v(2.58, -7.67) * mm, "end": v(2.71, -8.75) * mm});
            skLineSegment(sketch, "E2030", {"start": v(2.71, -8.75) * mm, "end": v(2.9, -9.74) * mm});
            skLineSegment(sketch, "E2031", {"start": v(2.9, -9.74) * mm, "end": v(3.13, -10.64) * mm});
            skLineSegment(sketch, "E2032", {"start": v(3.13, -10.64) * mm, "end": v(3.41, -11.45) * mm});
            skLineSegment(sketch, "E2033", {"start": v(3.41, -11.45) * mm, "end": v(3.75, -12.17) * mm});
            skLineSegment(sketch, "E2034", {"start": v(3.75, -12.17) * mm, "end": v(4.13, -12.79) * mm});
            skLineSegment(sketch, "E2035", {"start": v(4.13, -12.79) * mm, "end": v(4.55, -13.28) * mm});
            skLineSegment(sketch, "E2036", {"start": v(4.55, -13.28) * mm, "end": v(5.07, -13.7) * mm});
            skLineSegment(sketch, "E2037", {"start": v(5.07, -13.7) * mm, "end": v(5.68, -14.05) * mm});
            skLineSegment(sketch, "E2038", {"start": v(5.68, -14.05) * mm, "end": v(6.39, -14.35) * mm});
            skLineSegment(sketch, "E2039", {"start": v(6.39, -14.35) * mm, "end": v(7.19, -14.58) * mm});
            skLineSegment(sketch, "E2040", {"start": v(7.19, -14.58) * mm, "end": v(8.09, -14.74) * mm});
            skLineSegment(sketch, "E2041", {"start": v(8.09, -14.74) * mm, "end": v(9.08, -14.84) * mm});
            skLineSegment(sketch, "E2042", {"start": v(9.08, -14.84) * mm, "end": v(10.17, -14.87) * mm});
            skLineSegment(sketch, "E2043", {"start": v(10.17, -14.87) * mm, "end": v(10.17, -14.87) * mm});
            skLineSegment(sketch, "E2044", {"start": v(10.17, -14.87) * mm, "end": v(10.18, -14.87) * mm});
            skLineSegment(sketch, "E2045", {"start": v(10.18, -14.87) * mm, "end": v(10.19, -14.87) * mm});
            skLineSegment(sketch, "E2046", {"start": v(10.19, -14.87) * mm, "end": v(10.2, -14.87) * mm});
            skLineSegment(sketch, "E2047", {"start": v(10.2, -14.87) * mm, "end": v(10.2, -14.87) * mm});
            skLineSegment(sketch, "E2048", {"start": v(10.2, -14.87) * mm, "end": v(10.21, -14.87) * mm});
            skLineSegment(sketch, "E2049", {"start": v(10.21, -14.87) * mm, "end": v(10.22, -14.87) * mm});
            skLineSegment(sketch, "E2050", {"start": v(10.22, -14.87) * mm, "end": v(11.14, -14.9) * mm});
            skLineSegment(sketch, "E2051", {"start": v(11.14, -14.9) * mm, "end": v(12.06, -14.94) * mm});
            skLineSegment(sketch, "E2052", {"start": v(12.06, -14.94) * mm, "end": v(12.98, -14.97) * mm});
            skLineSegment(sketch, "E2053", {"start": v(12.98, -14.97) * mm, "end": v(13.9, -15) * mm});
            skLineSegment(sketch, "E2054", {"start": v(13.9, -15) * mm, "end": v(14.82, -15.04) * mm});
            skLineSegment(sketch, "E2055", {"start": v(14.82, -15.04) * mm, "end": v(15.74, -15.07) * mm});
            skLineSegment(sketch, "E2056", {"start": v(15.74, -15.07) * mm, "end": v(16.66, -15.1) * mm});
            skLineSegment(sketch, "E2057", {"start": v(16.66, -15.1) * mm, "end": v(17.58, -15.14) * mm});
            skLineSegment(sketch, "E2058", {"start": v(17.58, -15.14) * mm, "end": v(18.76, -15.11) * mm});
            skLineSegment(sketch, "E2059", {"start": v(18.76, -15.11) * mm, "end": v(19.82, -15.05) * mm});
            skLineSegment(sketch, "E2060", {"start": v(19.82, -15.05) * mm, "end": v(20.78, -14.94) * mm});
            skLineSegment(sketch, "E2061", {"start": v(20.78, -14.94) * mm, "end": v(21.65, -14.77) * mm});
            skLineSegment(sketch, "E2062", {"start": v(21.65, -14.77) * mm, "end": v(22.46, -14.56) * mm});
            skLineSegment(sketch, "E2063", {"start": v(22.46, -14.56) * mm, "end": v(23.2, -14.28) * mm});
            skLineSegment(sketch, "E2064", {"start": v(23.2, -14.28) * mm, "end": v(23.92, -13.94) * mm});
            skLineSegment(sketch, "E2065", {"start": v(23.92, -13.94) * mm, "end": v(24.6, -13.54) * mm});
            skLineSegment(sketch, "E2066", {"start": v(24.6, -13.54) * mm, "end": v(24.77, -13.43) * mm});
            skLineSegment(sketch, "E2067", {"start": v(24.77, -13.43) * mm, "end": v(24.92, -13.31) * mm});
            skLineSegment(sketch, "E2068", {"start": v(24.92, -13.31) * mm, "end": v(25.07, -13.2) * mm});
            skLineSegment(sketch, "E2069", {"start": v(25.07, -13.2) * mm, "end": v(25.22, -13.06) * mm});
            skLineSegment(sketch, "E2070", {"start": v(25.22, -13.06) * mm, "end": v(25.35, -12.93) * mm});
            skLineSegment(sketch, "E2071", {"start": v(25.35, -12.93) * mm, "end": v(25.48, -12.78) * mm});
            skLineSegment(sketch, "E2072", {"start": v(25.48, -12.78) * mm, "end": v(25.61, -12.64) * mm});
            skLineSegment(sketch, "E2073", {"start": v(25.61, -12.64) * mm, "end": v(25.73, -12.5) * mm});
            skLineSegment(sketch, "E2074", {"start": v(25.73, -12.5) * mm, "end": v(25.53, -12.55) * mm});
            skLineSegment(sketch, "E2075", {"start": v(25.53, -12.55) * mm, "end": v(25.32, -12.6) * mm});
            skLineSegment(sketch, "E2076", {"start": v(25.32, -12.6) * mm, "end": v(25.1, -12.66) * mm});
            skLineSegment(sketch, "E2077", {"start": v(25.1, -12.66) * mm, "end": v(24.88, -12.71) * mm});
            skLineSegment(sketch, "E2078", {"start": v(24.88, -12.71) * mm, "end": v(24.65, -12.76) * mm});
            skLineSegment(sketch, "E2079", {"start": v(24.65, -12.76) * mm, "end": v(24.42, -12.81) * mm});
            skLineSegment(sketch, "E2080", {"start": v(24.42, -12.81) * mm, "end": v(24.18, -12.86) * mm});
            skLineSegment(sketch, "E2081", {"start": v(24.18, -12.86) * mm, "end": v(23.93, -12.9) * mm});
            skLineSegment(sketch, "E2082", {"start": v(23.93, -12.9) * mm, "end": v(22.99, -13.06) * mm});
            skLineSegment(sketch, "E2083", {"start": v(22.99, -13.06) * mm, "end": v(22, -13.18) * mm});
            skLineSegment(sketch, "E2084", {"start": v(22, -13.18) * mm, "end": v(21.04, -13.26) * mm});
            skLineSegment(sketch, "E2085", {"start": v(21.04, -13.26) * mm, "end": v(20.1, -13.33) * mm});
            skLineSegment(sketch, "E2086", {"start": v(20.1, -13.33) * mm, "end": v(19.25, -13.36) * mm});
            skLineSegment(sketch, "E2087", {"start": v(19.25, -13.36) * mm, "end": v(18.5, -13.39) * mm});
            skLineSegment(sketch, "E2088", {"start": v(18.5, -13.39) * mm, "end": v(17.88, -13.4) * mm});
            skLineSegment(sketch, "E2089", {"start": v(17.88, -13.4) * mm, "end": v(17.44, -13.4) * mm});
            skLineSegment(sketch, "E2090", {"start": v(17.44, -13.4) * mm, "end": v(17.38, -13.4) * mm});
            skLineSegment(sketch, "E2091", {"start": v(17.38, -13.4) * mm, "end": v(17.32, -13.4) * mm});
            skLineSegment(sketch, "E2092", {"start": v(17.32, -13.4) * mm, "end": v(17.27, -13.4) * mm});
            skLineSegment(sketch, "E2093", {"start": v(17.27, -13.4) * mm, "end": v(17.23, -13.4) * mm});
            skLineSegment(sketch, "E2094", {"start": v(17.23, -13.4) * mm, "end": v(17.2, -13.4) * mm});
            skLineSegment(sketch, "E2095", {"start": v(17.2, -13.4) * mm, "end": v(17.17, -13.4) * mm});
            skLineSegment(sketch, "E2096", {"start": v(17.17, -13.4) * mm, "end": v(17.16, -13.4) * mm});
            skLineSegment(sketch, "E2097", {"start": v(17.16, -13.4) * mm, "end": v(17.15, -13.4) * mm});
            skLineSegment(sketch, "E2098", {"start": v(17.15, -13.4) * mm, "end": v(16.6, -13.39) * mm});
            skLineSegment(sketch, "E2099", {"start": v(16.6, -13.39) * mm, "end": v(16.06, -13.38) * mm});
            skLineSegment(sketch, "E2100", {"start": v(16.06, -13.38) * mm, "end": v(15.52, -13.37) * mm});
            skLineSegment(sketch, "E2101", {"start": v(15.52, -13.37) * mm, "end": v(14.97, -13.36) * mm});
            skLineSegment(sketch, "E2102", {"start": v(14.97, -13.36) * mm, "end": v(14.43, -13.35) * mm});
            skLineSegment(sketch, "E2103", {"start": v(14.43, -13.35) * mm, "end": v(13.88, -13.33) * mm});
            skLineSegment(sketch, "E2104", {"start": v(13.88, -13.33) * mm, "end": v(13.34, -13.32) * mm});
            skLineSegment(sketch, "E2105", {"start": v(13.34, -13.32) * mm, "end": v(12.8, -13.31) * mm});
            skLineSegment(sketch, "E2106", {"start": v(12.8, -13.31) * mm, "end": v(12.58, -13.3) * mm});
            skLineSegment(sketch, "E2107", {"start": v(12.58, -13.3) * mm, "end": v(12.21, -13.26) * mm});
            skLineSegment(sketch, "E2108", {"start": v(12.21, -13.26) * mm, "end": v(11.71, -13.19) * mm});
            skLineSegment(sketch, "E2109", {"start": v(11.71, -13.19) * mm, "end": v(11.12, -13.06) * mm});
            skLineSegment(sketch, "E2110", {"start": v(11.12, -13.06) * mm, "end": v(10.48, -12.86) * mm});
            skLineSegment(sketch, "E2111", {"start": v(10.48, -12.86) * mm, "end": v(9.82, -12.58) * mm});
            skLineSegment(sketch, "E2112", {"start": v(9.82, -12.58) * mm, "end": v(9.19, -12.2) * mm});
            skLineSegment(sketch, "E2113", {"start": v(9.19, -12.2) * mm, "end": v(8.62, -11.7) * mm});
            skLineSegment(sketch, "E2114", {"start": v(8.62, -11.7) * mm, "end": v(8.28, -11.33) * mm});
            skLineSegment(sketch, "E2115", {"start": v(8.28, -11.33) * mm, "end": v(8, -10.94) * mm});
            skLineSegment(sketch, "E2116", {"start": v(8, -10.94) * mm, "end": v(7.78, -10.55) * mm});
            skLineSegment(sketch, "E2117", {"start": v(7.78, -10.55) * mm, "end": v(7.6, -10.12) * mm});
            skLineSegment(sketch, "E2118", {"start": v(7.6, -10.12) * mm, "end": v(7.48, -9.66) * mm});
            skLineSegment(sketch, "E2119", {"start": v(7.48, -9.66) * mm, "end": v(7.4, -9.15) * mm});
            skLineSegment(sketch, "E2120", {"start": v(7.4, -9.15) * mm, "end": v(7.34, -8.58) * mm});
            skLineSegment(sketch, "E2121", {"start": v(7.34, -8.58) * mm, "end": v(7.33, -7.94) * mm});
            skLineSegment(sketch, "E2122", {"start": v(7.33, -7.94) * mm, "end": v(7.33, -7.75) * mm});
            skLineSegment(sketch, "E2123", {"start": v(7.33, -7.75) * mm, "end": v(7.33, -7.57) * mm});
            skLineSegment(sketch, "E2124", {"start": v(7.33, -7.57) * mm, "end": v(7.33, -7.39) * mm});
            skLineSegment(sketch, "E2125", {"start": v(7.33, -7.39) * mm, "end": v(7.33, -7.2) * mm});
            skLineSegment(sketch, "E2126", {"start": v(7.33, -7.2) * mm, "end": v(7.33, -7.02) * mm});
            skLineSegment(sketch, "E2127", {"start": v(7.33, -7.02) * mm, "end": v(7.33, -6.84) * mm});
            skLineSegment(sketch, "E2128", {"start": v(7.33, -6.84) * mm, "end": v(7.33, -6.65) * mm});
            skLineSegment(sketch, "E2129", {"start": v(7.33, -6.65) * mm, "end": v(7.33, -6.47) * mm});
            skLineSegment(sketch, "E2130", {"start": v(7.33, -6.47) * mm, "end": v(9.86, -6.47) * mm});
            skLineSegment(sketch, "E2131", {"start": v(9.86, -6.47) * mm, "end": v(12.4, -6.47) * mm});
            skLineSegment(sketch, "E2132", {"start": v(12.4, -6.47) * mm, "end": v(14.93, -6.47) * mm});
            skLineSegment(sketch, "E2133", {"start": v(14.93, -6.47) * mm, "end": v(17.46, -6.47) * mm});
            skLineSegment(sketch, "E2134", {"start": v(17.46, -6.47) * mm, "end": v(20, -6.47) * mm});
            skLineSegment(sketch, "E2135", {"start": v(20, -6.47) * mm, "end": v(22.53, -6.47) * mm});
            skLineSegment(sketch, "E2136", {"start": v(22.53, -6.47) * mm, "end": v(25.07, -6.47) * mm});
            skLineSegment(sketch, "E2137", {"start": v(25.07, -6.47) * mm, "end": v(27.6, -6.47) * mm});
            skLineSegment(sketch, "E2138", {"start": v(27.6, -6.47) * mm, "end": v(27.6, -6.42) * mm});
            skLineSegment(sketch, "E2139", {"start": v(27.6, -6.42) * mm, "end": v(27.6, -6.36) * mm});
            skLineSegment(sketch, "E2140", {"start": v(27.6, -6.36) * mm, "end": v(27.6, -6.3) * mm});
            skLineSegment(sketch, "E2141", {"start": v(27.6, -6.3) * mm, "end": v(27.6, -6.26) * mm});
            skLineSegment(sketch, "E2142", {"start": v(27.6, -6.26) * mm, "end": v(27.6, -6.2) * mm});
            skLineSegment(sketch, "E2143", {"start": v(27.6, -6.2) * mm, "end": v(27.6, -6.16) * mm});
            skLineSegment(sketch, "E2144", {"start": v(27.6, -6.16) * mm, "end": v(27.6, -6.11) * mm});
            skLineSegment(sketch, "E2145", {"start": v(27.6, -6.11) * mm, "end": v(27.6, -6.07) * mm});
            skLineSegment(sketch, "E2146", {"start": v(27.6, -6.07) * mm, "end": v(27.62, -5.9) * mm});
            skLineSegment(sketch, "E2147", {"start": v(27.62, -5.9) * mm, "end": v(27.62, -5.76) * mm});
            skLineSegment(sketch, "E2148", {"start": v(27.62, -5.76) * mm, "end": v(27.62, -5.6) * mm});
            skLineSegment(sketch, "E2149", {"start": v(27.62, -5.6) * mm, "end": v(27.63, -5.46) * mm});
            skLineSegment(sketch, "E2150", {"start": v(27.63, -5.46) * mm, "end": v(27.63, -5.32) * mm});
            skLineSegment(sketch, "E2151", {"start": v(27.63, -5.32) * mm, "end": v(27.63, -5.18) * mm});
            skLineSegment(sketch, "E2152", {"start": v(27.63, -5.18) * mm, "end": v(27.63, -5.05) * mm});
            skLineSegment(sketch, "E2153", {"start": v(27.63, -5.05) * mm, "end": v(27.63, -4.92) * mm});
            skLineSegment(sketch, "E2154", {"start": v(27.63, -4.92) * mm, "end": v(27.62, -4.32) * mm});
            skLineSegment(sketch, "E2155", {"start": v(27.62, -4.32) * mm, "end": v(27.6, -3.72) * mm});
            skLineSegment(sketch, "E2156", {"start": v(27.6, -3.72) * mm, "end": v(27.56, -3.13) * mm});
            skLineSegment(sketch, "E2157", {"start": v(27.56, -3.13) * mm, "end": v(27.5, -2.56) * mm});
            skLineSegment(sketch, "E2158", {"start": v(27.5, -2.56) * mm, "end": v(27.44, -2.02) * mm});
            skLineSegment(sketch, "E2159", {"start": v(27.44, -2.02) * mm, "end": v(27.36, -1.5) * mm});
            skLineSegment(sketch, "E2160", {"start": v(27.36, -1.5) * mm, "end": v(27.27, -1.04) * mm});
            skLineSegment(sketch, "E2161", {"start": v(27.27, -1.04) * mm, "end": v(27.17, -0.61) * mm});
            skLineSegment(sketch, "E2162", {"start": v(27.17, -0.61) * mm, "end": v(27.06, -0.26) * mm});
            skLineSegment(sketch, "E2163", {"start": v(27.06, -0.26) * mm, "end": v(26.93, 0.08) * mm});
            skLineSegment(sketch, "E2164", {"start": v(26.93, 0.08) * mm, "end": v(26.77, 0.4) * mm});
            skLineSegment(sketch, "E2165", {"start": v(26.77, 0.4) * mm, "end": v(26.59, 0.72) * mm});
            skLineSegment(sketch, "E2166", {"start": v(26.59, 0.72) * mm, "end": v(26.38, 1.01) * mm});
            skLineSegment(sketch, "E2167", {"start": v(26.38, 1.01) * mm, "end": v(26.15, 1.3) * mm});
            skLineSegment(sketch, "E2168", {"start": v(26.15, 1.3) * mm, "end": v(25.89, 1.56) * mm});
            skLineSegment(sketch, "E2169", {"start": v(25.89, 1.56) * mm, "end": v(25.6, 1.81) * mm});
            skLineSegment(sketch, "E2170", {"start": v(25.6, 1.81) * mm, "end": v(25.28, 2.06) * mm});
            skLineSegment(sketch, "E2171", {"start": v(25.28, 2.06) * mm, "end": v(24.94, 2.29) * mm});
            skLineSegment(sketch, "E2172", {"start": v(24.94, 2.29) * mm, "end": v(24.6, 2.49) * mm});
            skLineSegment(sketch, "E2173", {"start": v(24.6, 2.49) * mm, "end": v(24.22, 2.66) * mm});
            skLineSegment(sketch, "E2174", {"start": v(24.22, 2.66) * mm, "end": v(23.84, 2.82) * mm});
            skLineSegment(sketch, "E2175", {"start": v(23.84, 2.82) * mm, "end": v(23.44, 2.95) * mm});
            skLineSegment(sketch, "E2176", {"start": v(23.44, 2.95) * mm, "end": v(23.02, 3.05) * mm});
            skLineSegment(sketch, "E2177", {"start": v(23.02, 3.05) * mm, "end": v(22.58, 3.14) * mm});
            skLineSegment(sketch, "E2178", {"start": v(22.58, 3.14) * mm, "end": v(22.06, 3.22) * mm});
            skLineSegment(sketch, "E2179", {"start": v(22.06, 3.22) * mm, "end": v(21.5, 3.28) * mm});
            skLineSegment(sketch, "E2180", {"start": v(21.5, 3.28) * mm, "end": v(20.9, 3.34) * mm});
            skLineSegment(sketch, "E2181", {"start": v(20.9, 3.34) * mm, "end": v(20.27, 3.39) * mm});
            skLineSegment(sketch, "E2182", {"start": v(20.27, 3.39) * mm, "end": v(19.6, 3.42) * mm});
            skLineSegment(sketch, "E2183", {"start": v(19.6, 3.42) * mm, "end": v(18.9, 3.45) * mm});
            skLineSegment(sketch, "E2184", {"start": v(18.9, 3.45) * mm, "end": v(18.15, 3.46) * mm});
            skLineSegment(sketch, "E2185", {"start": v(18.15, 3.46) * mm, "end": v(17.38, 3.47) * mm});
            skLineSegment(sketch, "E2186", {"start": v(10.5, -9.4) * mm, "end": v(10.53, -9.44) * mm});
            skLineSegment(sketch, "E2187", {"start": v(10.53, -9.44) * mm, "end": v(10.56, -9.47) * mm});
            skLineSegment(sketch, "E2188", {"start": v(10.56, -9.47) * mm, "end": v(10.59, -9.5) * mm});
            skLineSegment(sketch, "E2189", {"start": v(10.59, -9.5) * mm, "end": v(10.61, -9.54) * mm});
            skLineSegment(sketch, "E2190", {"start": v(10.61, -9.54) * mm, "end": v(10.65, -9.58) * mm});
            skLineSegment(sketch, "E2191", {"start": v(10.65, -9.58) * mm, "end": v(10.68, -9.61) * mm});
            skLineSegment(sketch, "E2192", {"start": v(10.68, -9.61) * mm, "end": v(10.71, -9.65) * mm});
            skLineSegment(sketch, "E2193", {"start": v(10.71, -9.65) * mm, "end": v(10.75, -9.68) * mm});
            skLineSegment(sketch, "E2194", {"start": v(10.75, -9.68) * mm, "end": v(10.93, -9.84) * mm});
            skLineSegment(sketch, "E2195", {"start": v(10.93, -9.84) * mm, "end": v(11.16, -9.97) * mm});
            skLineSegment(sketch, "E2196", {"start": v(11.16, -9.97) * mm, "end": v(11.44, -10.09) * mm});
            skLineSegment(sketch, "E2197", {"start": v(11.44, -10.09) * mm, "end": v(11.73, -10.18) * mm});
            skLineSegment(sketch, "E2198", {"start": v(11.73, -10.18) * mm, "end": v(12.04, -10.26) * mm});
            skLineSegment(sketch, "E2199", {"start": v(12.04, -10.26) * mm, "end": v(12.34, -10.32) * mm});
            skLineSegment(sketch, "E2200", {"start": v(12.34, -10.32) * mm, "end": v(12.62, -10.36) * mm});
            skLineSegment(sketch, "E2201", {"start": v(12.62, -10.36) * mm, "end": v(12.88, -10.38) * mm});
            skLineSegment(sketch, "E2202", {"start": v(12.88, -10.38) * mm, "end": v(13.45, -10.39) * mm});
            skLineSegment(sketch, "E2203", {"start": v(13.45, -10.39) * mm, "end": v(14.02, -10.4) * mm});
            skLineSegment(sketch, "E2204", {"start": v(14.02, -10.4) * mm, "end": v(14.59, -10.41) * mm});
            skLineSegment(sketch, "E2205", {"start": v(14.59, -10.41) * mm, "end": v(15.16, -10.42) * mm});
            skLineSegment(sketch, "E2206", {"start": v(15.16, -10.42) * mm, "end": v(15.73, -10.43) * mm});
            skLineSegment(sketch, "E2207", {"start": v(15.73, -10.43) * mm, "end": v(16.3, -10.44) * mm});
            skLineSegment(sketch, "E2208", {"start": v(16.3, -10.44) * mm, "end": v(16.87, -10.45) * mm});
            skLineSegment(sketch, "E2209", {"start": v(16.87, -10.45) * mm, "end": v(17.44, -10.47) * mm});
            skLineSegment(sketch, "E2210", {"start": v(17.44, -10.47) * mm, "end": v(17.85, -10.46) * mm});
            skLineSegment(sketch, "E2211", {"start": v(17.85, -10.46) * mm, "end": v(18.42, -10.45) * mm});
            skLineSegment(sketch, "E2212", {"start": v(18.42, -10.45) * mm, "end": v(19.11, -10.43) * mm});
            skLineSegment(sketch, "E2213", {"start": v(19.11, -10.43) * mm, "end": v(19.9, -10.4) * mm});
            skLineSegment(sketch, "E2214", {"start": v(19.9, -10.4) * mm, "end": v(20.76, -10.34) * mm});
            skLineSegment(sketch, "E2215", {"start": v(20.76, -10.34) * mm, "end": v(21.65, -10.27) * mm});
            skLineSegment(sketch, "E2216", {"start": v(21.65, -10.27) * mm, "end": v(22.54, -10.16) * mm});
            skLineSegment(sketch, "E2217", {"start": v(22.54, -10.16) * mm, "end": v(23.4, -10.02) * mm});
            skLineSegment(sketch, "E2218", {"start": v(23.4, -10.02) * mm, "end": v(23.76, -9.95) * mm});
            skLineSegment(sketch, "E2219", {"start": v(23.76, -9.95) * mm, "end": v(24.1, -9.88) * mm});
            skLineSegment(sketch, "E2220", {"start": v(24.1, -9.88) * mm, "end": v(24.42, -9.8) * mm});
            skLineSegment(sketch, "E2221", {"start": v(24.42, -9.8) * mm, "end": v(24.72, -9.73) * mm});
            skLineSegment(sketch, "E2222", {"start": v(24.72, -9.73) * mm, "end": v(25, -9.65) * mm});
            skLineSegment(sketch, "E2223", {"start": v(25, -9.65) * mm, "end": v(25.27, -9.57) * mm});
            skLineSegment(sketch, "E2224", {"start": v(25.27, -9.57) * mm, "end": v(25.52, -9.49) * mm});
            skLineSegment(sketch, "E2225", {"start": v(25.52, -9.49) * mm, "end": v(25.75, -9.4) * mm});
            skLineSegment(sketch, "E2226", {"start": v(25.75, -9.4) * mm, "end": v(23.84, -9.4) * mm});
            skLineSegment(sketch, "E2227", {"start": v(23.84, -9.4) * mm, "end": v(21.94, -9.4) * mm});
            skLineSegment(sketch, "E2228", {"start": v(21.94, -9.4) * mm, "end": v(20.03, -9.4) * mm});
            skLineSegment(sketch, "E2229", {"start": v(20.03, -9.4) * mm, "end": v(18.13, -9.4) * mm});
            skLineSegment(sketch, "E2230", {"start": v(18.13, -9.4) * mm, "end": v(16.22, -9.4) * mm});
            skLineSegment(sketch, "E2231", {"start": v(16.22, -9.4) * mm, "end": v(14.32, -9.4) * mm});
            skLineSegment(sketch, "E2232", {"start": v(14.32, -9.4) * mm, "end": v(12.41, -9.4) * mm});
            skLineSegment(sketch, "E2233", {"start": v(12.41, -9.4) * mm, "end": v(10.5, -9.4) * mm});
            skLineSegment(sketch, "E2234", {"start": v(22.96, -5.1) * mm, "end": v(21.02, -5.1) * mm});
            skLineSegment(sketch, "E2235", {"start": v(21.02, -5.1) * mm, "end": v(19.08, -5.1) * mm});
            skLineSegment(sketch, "E2236", {"start": v(19.08, -5.1) * mm, "end": v(17.14, -5.1) * mm});
            skLineSegment(sketch, "E2237", {"start": v(17.14, -5.1) * mm, "end": v(15.2, -5.1) * mm});
            skLineSegment(sketch, "E2238", {"start": v(15.2, -5.1) * mm, "end": v(13.25, -5.1) * mm});
            skLineSegment(sketch, "E2239", {"start": v(13.25, -5.1) * mm, "end": v(11.31, -5.1) * mm});
            skLineSegment(sketch, "E2240", {"start": v(11.31, -5.1) * mm, "end": v(9.37, -5.1) * mm});
            skLineSegment(sketch, "E2241", {"start": v(9.37, -5.1) * mm, "end": v(7.43, -5.1) * mm});
            skLineSegment(sketch, "E2242", {"start": v(7.43, -5.1) * mm, "end": v(7.41, -4.85) * mm});
            skLineSegment(sketch, "E2243", {"start": v(7.41, -4.85) * mm, "end": v(7.4, -4.6) * mm});
            skLineSegment(sketch, "E2244", {"start": v(7.4, -4.6) * mm, "end": v(7.38, -4.34) * mm});
            skLineSegment(sketch, "E2245", {"start": v(7.38, -4.34) * mm, "end": v(7.36, -4.08) * mm});
            skLineSegment(sketch, "E2246", {"start": v(7.36, -4.08) * mm, "end": v(7.34, -3.83) * mm});
            skLineSegment(sketch, "E2247", {"start": v(7.34, -3.83) * mm, "end": v(7.32, -3.57) * mm});
            skLineSegment(sketch, "E2248", {"start": v(7.32, -3.57) * mm, "end": v(7.3, -3.32) * mm});
            skLineSegment(sketch, "E2249", {"start": v(7.3, -3.32) * mm, "end": v(7.29, -3.06) * mm});
            skLineSegment(sketch, "E2250", {"start": v(7.29, -3.06) * mm, "end": v(7.33, -2.29) * mm});
            skLineSegment(sketch, "E2251", {"start": v(7.33, -2.29) * mm, "end": v(7.45, -1.57) * mm});
            skLineSegment(sketch, "E2252", {"start": v(7.45, -1.57) * mm, "end": v(7.64, -0.92) * mm});
            skLineSegment(sketch, "E2253", {"start": v(7.64, -0.92) * mm, "end": v(7.9, -0.33) * mm});
            skLineSegment(sketch, "E2254", {"start": v(7.9, -0.33) * mm, "end": v(8.24, 0.18) * mm});
            skLineSegment(sketch, "E2255", {"start": v(8.24, 0.18) * mm, "end": v(8.64, 0.61) * mm});
            skLineSegment(sketch, "E2256", {"start": v(8.64, 0.61) * mm, "end": v(9.1, 0.95) * mm});
            skLineSegment(sketch, "E2257", {"start": v(9.1, 0.95) * mm, "end": v(9.62, 1.2) * mm});
            skLineSegment(sketch, "E2258", {"start": v(9.62, 1.2) * mm, "end": v(10.04, 1.35) * mm});
            skLineSegment(sketch, "E2259", {"start": v(10.04, 1.35) * mm, "end": v(10.5, 1.47) * mm});
            skLineSegment(sketch, "E2260", {"start": v(10.5, 1.47) * mm, "end": v(10.98, 1.57) * mm});
            skLineSegment(sketch, "E2261", {"start": v(10.98, 1.57) * mm, "end": v(11.5, 1.66) * mm});
            skLineSegment(sketch, "E2262", {"start": v(11.5, 1.66) * mm, "end": v(12.05, 1.72) * mm});
            skLineSegment(sketch, "E2263", {"start": v(12.05, 1.72) * mm, "end": v(12.64, 1.77) * mm});
            skLineSegment(sketch, "E2264", {"start": v(12.64, 1.77) * mm, "end": v(13.26, 1.8) * mm});
            skLineSegment(sketch, "E2265", {"start": v(13.26, 1.8) * mm, "end": v(13.93, 1.8) * mm});
            skLineSegment(sketch, "E2266", {"start": v(13.93, 1.8) * mm, "end": v(14.29, 1.8) * mm});
            skLineSegment(sketch, "E2267", {"start": v(14.29, 1.8) * mm, "end": v(14.65, 1.8) * mm});
            skLineSegment(sketch, "E2268", {"start": v(14.65, 1.8) * mm, "end": v(15, 1.8) * mm});
            skLineSegment(sketch, "E2269", {"start": v(15, 1.8) * mm, "end": v(15.36, 1.8) * mm});
            skLineSegment(sketch, "E2270", {"start": v(15.36, 1.8) * mm, "end": v(15.72, 1.8) * mm});
            skLineSegment(sketch, "E2271", {"start": v(15.72, 1.8) * mm, "end": v(16.08, 1.8) * mm});
            skLineSegment(sketch, "E2272", {"start": v(16.08, 1.8) * mm, "end": v(16.44, 1.8) * mm});
            skLineSegment(sketch, "E2273", {"start": v(16.44, 1.8) * mm, "end": v(16.8, 1.8) * mm});
            skLineSegment(sketch, "E2274", {"start": v(16.8, 1.8) * mm, "end": v(17.5, 1.8) * mm});
            skLineSegment(sketch, "E2275", {"start": v(17.5, 1.8) * mm, "end": v(18.17, 1.75) * mm});
            skLineSegment(sketch, "E2276", {"start": v(18.17, 1.75) * mm, "end": v(18.78, 1.68) * mm});
            skLineSegment(sketch, "E2277", {"start": v(18.78, 1.68) * mm, "end": v(19.34, 1.58) * mm});
            skLineSegment(sketch, "E2278", {"start": v(19.34, 1.58) * mm, "end": v(19.86, 1.45) * mm});
            skLineSegment(sketch, "E2279", {"start": v(19.86, 1.45) * mm, "end": v(20.34, 1.3) * mm});
            skLineSegment(sketch, "E2280", {"start": v(20.34, 1.3) * mm, "end": v(20.77, 1.11) * mm});
            skLineSegment(sketch, "E2281", {"start": v(20.77, 1.11) * mm, "end": v(21.16, 0.9) * mm});
            skLineSegment(sketch, "E2282", {"start": v(21.16, 0.9) * mm, "end": v(21.69, 0.48) * mm});
            skLineSegment(sketch, "E2283", {"start": v(21.69, 0.48) * mm, "end": v(22.1, -0.04) * mm});
            skLineSegment(sketch, "E2284", {"start": v(22.1, -0.04) * mm, "end": v(22.42, -0.62) * mm});
            skLineSegment(sketch, "E2285", {"start": v(22.42, -0.62) * mm, "end": v(22.65, -1.25) * mm});
            skLineSegment(sketch, "E2286", {"start": v(22.65, -1.25) * mm, "end": v(22.8, -1.9) * mm});
            skLineSegment(sketch, "E2287", {"start": v(22.8, -1.9) * mm, "end": v(22.9, -2.52) * mm});
            skLineSegment(sketch, "E2288", {"start": v(22.9, -2.52) * mm, "end": v(22.95, -3.11) * mm});
            skLineSegment(sketch, "E2289", {"start": v(22.95, -3.11) * mm, "end": v(22.96, -3.64) * mm});
            skLineSegment(sketch, "E2290", {"start": v(22.96, -3.64) * mm, "end": v(22.96, -3.82) * mm});
            skLineSegment(sketch, "E2291", {"start": v(22.96, -3.82) * mm, "end": v(22.96, -4) * mm});
            skLineSegment(sketch, "E2292", {"start": v(22.96, -4) * mm, "end": v(22.96, -4.19) * mm});
            skLineSegment(sketch, "E2293", {"start": v(22.96, -4.19) * mm, "end": v(22.96, -4.37) * mm});
            skLineSegment(sketch, "E2294", {"start": v(22.96, -4.37) * mm, "end": v(22.96, -4.55) * mm});
            skLineSegment(sketch, "E2295", {"start": v(22.96, -4.55) * mm, "end": v(22.96, -4.74) * mm});
            skLineSegment(sketch, "E2296", {"start": v(22.96, -4.74) * mm, "end": v(22.96, -4.92) * mm});
            skLineSegment(sketch, "E2297", {"start": v(22.96, -4.92) * mm, "end": v(22.96, -5.1) * mm});
            skLineSegment(sketch, "E2298", {"start": v(10.32, -2.17) * mm, "end": v(11.51, -2.17) * mm});
            skLineSegment(sketch, "E2299", {"start": v(11.51, -2.17) * mm, "end": v(12.7, -2.17) * mm});
            skLineSegment(sketch, "E2300", {"start": v(12.7, -2.17) * mm, "end": v(13.9, -2.17) * mm});
            skLineSegment(sketch, "E2301", {"start": v(13.9, -2.17) * mm, "end": v(15.09, -2.17) * mm});
            skLineSegment(sketch, "E2302", {"start": v(15.09, -2.17) * mm, "end": v(16.28, -2.17) * mm});
            skLineSegment(sketch, "E2303", {"start": v(16.28, -2.17) * mm, "end": v(17.47, -2.17) * mm});
            skLineSegment(sketch, "E2304", {"start": v(17.47, -2.17) * mm, "end": v(18.66, -2.17) * mm});
            skLineSegment(sketch, "E2305", {"start": v(18.66, -2.17) * mm, "end": v(19.85, -2.17) * mm});
            skLineSegment(sketch, "E2306", {"start": v(19.85, -2.17) * mm, "end": v(19.82, -2.05) * mm});
            skLineSegment(sketch, "E2307", {"start": v(19.82, -2.05) * mm, "end": v(19.78, -1.95) * mm});
            skLineSegment(sketch, "E2308", {"start": v(19.78, -1.95) * mm, "end": v(19.75, -1.85) * mm});
            skLineSegment(sketch, "E2309", {"start": v(19.75, -1.85) * mm, "end": v(19.71, -1.77) * mm});
            skLineSegment(sketch, "E2310", {"start": v(19.71, -1.77) * mm, "end": v(19.68, -1.7) * mm});
            skLineSegment(sketch, "E2311", {"start": v(19.68, -1.7) * mm, "end": v(19.65, -1.65) * mm});
            skLineSegment(sketch, "E2312", {"start": v(19.65, -1.65) * mm, "end": v(19.62, -1.6) * mm});
            skLineSegment(sketch, "E2313", {"start": v(19.62, -1.6) * mm, "end": v(19.59, -1.58) * mm});
            skLineSegment(sketch, "E2314", {"start": v(19.59, -1.58) * mm, "end": v(19.47, -1.51) * mm});
            skLineSegment(sketch, "E2315", {"start": v(19.47, -1.51) * mm, "end": v(19.3, -1.44) * mm});
            skLineSegment(sketch, "E2316", {"start": v(19.3, -1.44) * mm, "end": v(19.07, -1.37) * mm});
            skLineSegment(sketch, "E2317", {"start": v(19.07, -1.37) * mm, "end": v(18.77, -1.3) * mm});
            skLineSegment(sketch, "E2318", {"start": v(18.77, -1.3) * mm, "end": v(18.4, -1.23) * mm});
            skLineSegment(sketch, "E2319", {"start": v(18.4, -1.23) * mm, "end": v(17.96, -1.18) * mm});
            skLineSegment(sketch, "E2320", {"start": v(17.96, -1.18) * mm, "end": v(17.43, -1.14) * mm});
            skLineSegment(sketch, "E2321", {"start": v(17.43, -1.14) * mm, "end": v(16.8, -1.13) * mm});
            skLineSegment(sketch, "E2322", {"start": v(16.8, -1.13) * mm, "end": v(16.44, -1.13) * mm});
            skLineSegment(sketch, "E2323", {"start": v(16.44, -1.13) * mm, "end": v(16.08, -1.13) * mm});
            skLineSegment(sketch, "E2324", {"start": v(16.08, -1.13) * mm, "end": v(15.72, -1.13) * mm});
            skLineSegment(sketch, "E2325", {"start": v(15.72, -1.13) * mm, "end": v(15.36, -1.13) * mm});
            skLineSegment(sketch, "E2326", {"start": v(15.36, -1.13) * mm, "end": v(15, -1.13) * mm});
            skLineSegment(sketch, "E2327", {"start": v(15, -1.13) * mm, "end": v(14.65, -1.13) * mm});
            skLineSegment(sketch, "E2328", {"start": v(14.65, -1.13) * mm, "end": v(14.29, -1.13) * mm});
            skLineSegment(sketch, "E2329", {"start": v(14.29, -1.13) * mm, "end": v(13.93, -1.13) * mm});
            skLineSegment(sketch, "E2330", {"start": v(13.93, -1.13) * mm, "end": v(13.3, -1.14) * mm});
            skLineSegment(sketch, "E2331", {"start": v(13.3, -1.14) * mm, "end": v(12.73, -1.17) * mm});
            skLineSegment(sketch, "E2332", {"start": v(12.73, -1.17) * mm, "end": v(12.23, -1.21) * mm});
            skLineSegment(sketch, "E2333", {"start": v(12.23, -1.21) * mm, "end": v(11.8, -1.27) * mm});
            skLineSegment(sketch, "E2334", {"start": v(11.8, -1.27) * mm, "end": v(11.43, -1.33) * mm});
            skLineSegment(sketch, "E2335", {"start": v(11.43, -1.33) * mm, "end": v(11.11, -1.4) * mm});
            skLineSegment(sketch, "E2336", {"start": v(11.11, -1.4) * mm, "end": v(10.85, -1.47) * mm});
            skLineSegment(sketch, "E2337", {"start": v(10.85, -1.47) * mm, "end": v(10.64, -1.55) * mm});
            skLineSegment(sketch, "E2338", {"start": v(10.64, -1.55) * mm, "end": v(10.61, -1.56) * mm});
            skLineSegment(sketch, "E2339", {"start": v(10.61, -1.56) * mm, "end": v(10.58, -1.6) * mm});
            skLineSegment(sketch, "E2340", {"start": v(10.58, -1.6) * mm, "end": v(10.54, -1.64) * mm});
            skLineSegment(sketch, "E2341", {"start": v(10.54, -1.64) * mm, "end": v(10.5, -1.71) * mm});
            skLineSegment(sketch, "E2342", {"start": v(10.5, -1.71) * mm, "end": v(10.45, -1.8) * mm});
            skLineSegment(sketch, "E2343", {"start": v(10.45, -1.8) * mm, "end": v(10.4, -1.9) * mm});
            skLineSegment(sketch, "E2344", {"start": v(10.4, -1.9) * mm, "end": v(10.36, -2.03) * mm});
            skLineSegment(sketch, "E2345", {"start": v(10.36, -2.03) * mm, "end": v(10.32, -2.17) * mm});
            skLineSegment(sketch, "E2346", {"start": v(54.06, -8.58) * mm, "end": v(54.36, -8.81) * mm});
            skLineSegment(sketch, "E2347", {"start": v(54.36, -8.81) * mm, "end": v(55.13, -9.48) * mm});
            skLineSegment(sketch, "E2348", {"start": v(55.13, -9.48) * mm, "end": v(56.25, -10.55) * mm});
            skLineSegment(sketch, "E2349", {"start": v(56.25, -10.55) * mm, "end": v(57.56, -12) * mm});
            skLineSegment(sketch, "E2350", {"start": v(57.56, -12) * mm, "end": v(58.9, -13.8) * mm});
            skLineSegment(sketch, "E2351", {"start": v(58.9, -13.8) * mm, "end": v(60.15, -15.9) * mm});
            skLineSegment(sketch, "E2352", {"start": v(60.15, -15.9) * mm, "end": v(61.13, -18.3) * mm});
            skLineSegment(sketch, "E2353", {"start": v(61.13, -18.3) * mm, "end": v(61.72, -20.94) * mm});
            skLineSegment(sketch, "E2354", {"start": v(61.72, -20.94) * mm, "end": v(61.56, -27.43) * mm});
            skLineSegment(sketch, "E2355", {"start": v(61.56, -27.43) * mm, "end": v(59.73, -33.12) * mm});
            skLineSegment(sketch, "E2356", {"start": v(59.73, -33.12) * mm, "end": v(56.76, -38) * mm});
            skLineSegment(sketch, "E2357", {"start": v(56.76, -38) * mm, "end": v(53.17, -42.05) * mm});
            skLineSegment(sketch, "E2358", {"start": v(53.17, -42.05) * mm, "end": v(49.47, -45.23) * mm});
            skLineSegment(sketch, "E2359", {"start": v(49.47, -45.23) * mm, "end": v(46.18, -47.53) * mm});
            skLineSegment(sketch, "E2360", {"start": v(46.18, -47.53) * mm, "end": v(43.83, -48.93) * mm});
            skLineSegment(sketch, "E2361", {"start": v(43.83, -48.93) * mm, "end": v(42.93, -49.4) * mm});
            skLineSegment(sketch, "E2362", {"start": v(42.93, -49.4) * mm, "end": v(43.53, -48.83) * mm});
            skLineSegment(sketch, "E2363", {"start": v(43.53, -48.83) * mm, "end": v(45.1, -47.2) * mm});
            skLineSegment(sketch, "E2364", {"start": v(45.1, -47.2) * mm, "end": v(47.3, -44.68) * mm});
            skLineSegment(sketch, "E2365", {"start": v(47.3, -44.68) * mm, "end": v(49.8, -41.39) * mm});
            skLineSegment(sketch, "E2366", {"start": v(49.8, -41.39) * mm, "end": v(52.25, -37.46) * mm});
            skLineSegment(sketch, "E2367", {"start": v(52.25, -37.46) * mm, "end": v(54.33, -33.04) * mm});
            skLineSegment(sketch, "E2368", {"start": v(54.33, -33.04) * mm, "end": v(55.7, -28.27) * mm});
            skLineSegment(sketch, "E2369", {"start": v(55.7, -28.27) * mm, "end": v(56.02, -23.28) * mm});
            skLineSegment(sketch, "E2370", {"start": v(56.02, -23.28) * mm, "end": v(55.9, -22.3) * mm});
            skLineSegment(sketch, "E2371", {"start": v(55.9, -22.3) * mm, "end": v(55.62, -21.13) * mm});
            skLineSegment(sketch, "E2372", {"start": v(55.62, -21.13) * mm, "end": v(55.16, -19.8) * mm});
            skLineSegment(sketch, "E2373", {"start": v(55.16, -19.8) * mm, "end": v(54.48, -18.35) * mm});
            skLineSegment(sketch, "E2374", {"start": v(54.48, -18.35) * mm, "end": v(53.54, -16.78) * mm});
            skLineSegment(sketch, "E2375", {"start": v(53.54, -16.78) * mm, "end": v(52.3, -15.12) * mm});
            skLineSegment(sketch, "E2376", {"start": v(52.3, -15.12) * mm, "end": v(50.75, -13.38) * mm});
            skLineSegment(sketch, "E2377", {"start": v(50.75, -13.38) * mm, "end": v(48.83, -11.6) * mm});
            skLineSegment(sketch, "E2378", {"start": v(48.83, -11.6) * mm, "end": v(47.46, -10.53) * mm});
            skLineSegment(sketch, "E2379", {"start": v(47.46, -10.53) * mm, "end": v(46.01, -9.54) * mm});
            skLineSegment(sketch, "E2380", {"start": v(46.01, -9.54) * mm, "end": v(44.52, -8.65) * mm});
            skLineSegment(sketch, "E2381", {"start": v(44.52, -8.65) * mm, "end": v(43.02, -7.88) * mm});
            skLineSegment(sketch, "E2382", {"start": v(43.02, -7.88) * mm, "end": v(41.54, -7.24) * mm});
            skLineSegment(sketch, "E2383", {"start": v(41.54, -7.24) * mm, "end": v(40.12, -6.73) * mm});
            skLineSegment(sketch, "E2384", {"start": v(40.12, -6.73) * mm, "end": v(38.78, -6.37) * mm});
            skLineSegment(sketch, "E2385", {"start": v(38.78, -6.37) * mm, "end": v(37.56, -6.17) * mm});
            skLineSegment(sketch, "E2386", {"start": v(37.56, -6.17) * mm, "end": v(37.56, -7.45) * mm});
            skLineSegment(sketch, "E2387", {"start": v(37.56, -7.45) * mm, "end": v(37.56, -8.73) * mm});
            skLineSegment(sketch, "E2388", {"start": v(37.56, -8.73) * mm, "end": v(37.56, -10.02) * mm});
            skLineSegment(sketch, "E2389", {"start": v(37.56, -10.02) * mm, "end": v(37.56, -11.3) * mm});
            skLineSegment(sketch, "E2390", {"start": v(37.56, -11.3) * mm, "end": v(37.55, -12.58) * mm});
            skLineSegment(sketch, "E2391", {"start": v(37.55, -12.58) * mm, "end": v(37.55, -13.87) * mm});
            skLineSegment(sketch, "E2392", {"start": v(37.55, -13.87) * mm, "end": v(37.55, -15.15) * mm});
            skLineSegment(sketch, "E2393", {"start": v(37.55, -15.15) * mm, "end": v(37.55, -16.43) * mm});
            skLineSegment(sketch, "E2394", {"start": v(37.55, -16.43) * mm, "end": v(36.74, -16.43) * mm});
            skLineSegment(sketch, "E2395", {"start": v(36.74, -16.43) * mm, "end": v(35.93, -16.43) * mm});
            skLineSegment(sketch, "E2396", {"start": v(35.93, -16.43) * mm, "end": v(35.12, -16.43) * mm});
            skLineSegment(sketch, "E2397", {"start": v(35.12, -16.43) * mm, "end": v(34.3, -16.43) * mm});
            skLineSegment(sketch, "E2398", {"start": v(34.3, -16.43) * mm, "end": v(33.5, -16.43) * mm});
            skLineSegment(sketch, "E2399", {"start": v(33.5, -16.43) * mm, "end": v(32.68, -16.43) * mm});
            skLineSegment(sketch, "E2400", {"start": v(32.68, -16.43) * mm, "end": v(31.87, -16.43) * mm});
            skLineSegment(sketch, "E2401", {"start": v(31.87, -16.43) * mm, "end": v(31.06, -16.43) * mm});
            skLineSegment(sketch, "E2402", {"start": v(31.06, -16.43) * mm, "end": v(31.06, -13.76) * mm});
            skLineSegment(sketch, "E2403", {"start": v(31.06, -13.76) * mm, "end": v(31.06, -11.09) * mm});
            skLineSegment(sketch, "E2404", {"start": v(31.06, -11.09) * mm, "end": v(31.06, -8.42) * mm});
            skLineSegment(sketch, "E2405", {"start": v(31.06, -8.42) * mm, "end": v(31.06, -5.75) * mm});
            skLineSegment(sketch, "E2406", {"start": v(31.06, -5.75) * mm, "end": v(31.06, -3.08) * mm});
            skLineSegment(sketch, "E2407", {"start": v(31.06, -3.08) * mm, "end": v(31.06, -0.4) * mm});
            skLineSegment(sketch, "E2408", {"start": v(31.06, -0.4) * mm, "end": v(31.06, 2.27) * mm});
            skLineSegment(sketch, "E2409", {"start": v(31.06, 2.27) * mm, "end": v(31.06, 4.94) * mm});
            skLineSegment(sketch, "E2410", {"start": v(31.06, 4.94) * mm, "end": v(33.4, 4.94) * mm});
            skLineSegment(sketch, "E2411", {"start": v(33.4, 4.94) * mm, "end": v(35.76, 4.94) * mm});
            skLineSegment(sketch, "E2412", {"start": v(35.76, 4.94) * mm, "end": v(38.11, 4.94) * mm});
            skLineSegment(sketch, "E2413", {"start": v(38.11, 4.94) * mm, "end": v(40.47, 4.94) * mm});
            skLineSegment(sketch, "E2414", {"start": v(40.47, 4.94) * mm, "end": v(42.82, 4.94) * mm});
            skLineSegment(sketch, "E2415", {"start": v(42.82, 4.94) * mm, "end": v(45.17, 4.94) * mm});
            skLineSegment(sketch, "E2416", {"start": v(45.17, 4.94) * mm, "end": v(47.52, 4.94) * mm});
            skLineSegment(sketch, "E2417", {"start": v(47.52, 4.94) * mm, "end": v(49.88, 4.94) * mm});
            skLineSegment(sketch, "E2418", {"start": v(49.88, 4.94) * mm, "end": v(50.22, 4.91) * mm});
            skLineSegment(sketch, "E2419", {"start": v(50.22, 4.91) * mm, "end": v(51.13, 4.8) * mm});
            skLineSegment(sketch, "E2420", {"start": v(51.13, 4.8) * mm, "end": v(52.42, 4.5) * mm});
            skLineSegment(sketch, "E2421", {"start": v(52.42, 4.5) * mm, "end": v(53.9, 3.96) * mm});
            skLineSegment(sketch, "E2422", {"start": v(53.9, 3.96) * mm, "end": v(55.38, 3.1) * mm});
            skLineSegment(sketch, "E2423", {"start": v(55.38, 3.1) * mm, "end": v(56.67, 1.83) * mm});
            skLineSegment(sketch, "E2424", {"start": v(56.67, 1.83) * mm, "end": v(57.58, 0.09) * mm});
            skLineSegment(sketch, "E2425", {"start": v(57.58, 0.09) * mm, "end": v(57.92, -2.2) * mm});
            skLineSegment(sketch, "E2426", {"start": v(57.92, -2.2) * mm, "end": v(57.76, -3.74) * mm});
            skLineSegment(sketch, "E2427", {"start": v(57.76, -3.74) * mm, "end": v(57.32, -5.06) * mm});
            skLineSegment(sketch, "E2428", {"start": v(57.32, -5.06) * mm, "end": v(56.7, -6.16) * mm});
            skLineSegment(sketch, "E2429", {"start": v(56.7, -6.16) * mm, "end": v(56, -7.04) * mm});
            skLineSegment(sketch, "E2430", {"start": v(56, -7.04) * mm, "end": v(55.28, -7.73) * mm});
            skLineSegment(sketch, "E2431", {"start": v(55.28, -7.73) * mm, "end": v(54.67, -8.2) * mm});
            skLineSegment(sketch, "E2432", {"start": v(54.67, -8.2) * mm, "end": v(54.23, -8.5) * mm});
            skLineSegment(sketch, "E2433", {"start": v(54.23, -8.5) * mm, "end": v(54.06, -8.58) * mm});
            skLineSegment(sketch, "E2434", {"start": v(36.89, 0.33) * mm, "end": v(38.45, -0.33) * mm});
            skLineSegment(sketch, "E2435", {"start": v(38.45, -0.33) * mm, "end": v(40, -0.99) * mm});
            skLineSegment(sketch, "E2436", {"start": v(40, -0.99) * mm, "end": v(41.57, -1.64) * mm});
            skLineSegment(sketch, "E2437", {"start": v(41.57, -1.64) * mm, "end": v(43.12, -2.3) * mm});
            skLineSegment(sketch, "E2438", {"start": v(43.12, -2.3) * mm, "end": v(44.68, -2.96) * mm});
            skLineSegment(sketch, "E2439", {"start": v(44.68, -2.96) * mm, "end": v(46.24, -3.62) * mm});
            skLineSegment(sketch, "E2440", {"start": v(46.24, -3.62) * mm, "end": v(47.8, -4.28) * mm});
            skLineSegment(sketch, "E2441", {"start": v(47.8, -4.28) * mm, "end": v(49.36, -4.94) * mm});
            skLineSegment(sketch, "E2442", {"start": v(49.36, -4.94) * mm, "end": v(49.45, -4.9) * mm});
            skLineSegment(sketch, "E2443", {"start": v(49.45, -4.9) * mm, "end": v(49.7, -4.8) * mm});
            skLineSegment(sketch, "E2444", {"start": v(49.7, -4.8) * mm, "end": v(50.04, -4.6) * mm});
            skLineSegment(sketch, "E2445", {"start": v(50.04, -4.6) * mm, "end": v(50.43, -4.31) * mm});
            skLineSegment(sketch, "E2446", {"start": v(50.43, -4.31) * mm, "end": v(50.84, -3.93) * mm});
            skLineSegment(sketch, "E2447", {"start": v(50.84, -3.93) * mm, "end": v(51.2, -3.45) * mm});
            skLineSegment(sketch, "E2448", {"start": v(51.2, -3.45) * mm, "end": v(51.46, -2.85) * mm});
            skLineSegment(sketch, "E2449", {"start": v(51.46, -2.85) * mm, "end": v(51.6, -2.14) * mm});
            skLineSegment(sketch, "E2450", {"start": v(51.6, -2.14) * mm, "end": v(51.4, -1.31) * mm});
            skLineSegment(sketch, "E2451", {"start": v(51.4, -1.31) * mm, "end": v(50.78, -0.7) * mm});
            skLineSegment(sketch, "E2452", {"start": v(50.78, -0.7) * mm, "end": v(49.88, -0.25) * mm});
            skLineSegment(sketch, "E2453", {"start": v(49.88, -0.25) * mm, "end": v(48.84, 0.04) * mm});
            skLineSegment(sketch, "E2454", {"start": v(48.84, 0.04) * mm, "end": v(47.8, 0.21) * mm});
            skLineSegment(sketch, "E2455", {"start": v(47.8, 0.21) * mm, "end": v(46.88, 0.3) * mm});
            skLineSegment(sketch, "E2456", {"start": v(46.88, 0.3) * mm, "end": v(46.22, 0.33) * mm});
            skLineSegment(sketch, "E2457", {"start": v(46.22, 0.33) * mm, "end": v(45.98, 0.33) * mm});
            skLineSegment(sketch, "E2458", {"start": v(45.98, 0.33) * mm, "end": v(44.84, 0.33) * mm});
            skLineSegment(sketch, "E2459", {"start": v(44.84, 0.33) * mm, "end": v(43.7, 0.33) * mm});
            skLineSegment(sketch, "E2460", {"start": v(43.7, 0.33) * mm, "end": v(42.57, 0.33) * mm});
            skLineSegment(sketch, "E2461", {"start": v(42.57, 0.33) * mm, "end": v(41.43, 0.33) * mm});
            skLineSegment(sketch, "E2462", {"start": v(41.43, 0.33) * mm, "end": v(40.3, 0.33) * mm});
            skLineSegment(sketch, "E2463", {"start": v(40.3, 0.33) * mm, "end": v(39.16, 0.33) * mm});
            skLineSegment(sketch, "E2464", {"start": v(39.16, 0.33) * mm, "end": v(38.03, 0.33) * mm});
            skLineSegment(sketch, "E2465", {"start": v(38.03, 0.33) * mm, "end": v(36.89, 0.33) * mm});
            skLineSegment(sketch, "E2466", {"start": v(35.24, -54.42) * mm, "end": v(36.07, -53.66) * mm});
            skLineSegment(sketch, "E2467", {"start": v(36.07, -53.66) * mm, "end": v(36.91, -52.9) * mm});
            skLineSegment(sketch, "E2468", {"start": v(36.91, -52.9) * mm, "end": v(37.75, -52.13) * mm});
            skLineSegment(sketch, "E2469", {"start": v(37.75, -52.13) * mm, "end": v(38.6, -51.37) * mm});
            skLineSegment(sketch, "E2470", {"start": v(38.6, -51.37) * mm, "end": v(39.43, -50.6) * mm});
            skLineSegment(sketch, "E2471", {"start": v(39.43, -50.6) * mm, "end": v(40.27, -49.84) * mm});
            skLineSegment(sketch, "E2472", {"start": v(40.27, -49.84) * mm, "end": v(41.1, -49.08) * mm});
            skLineSegment(sketch, "E2473", {"start": v(41.1, -49.08) * mm, "end": v(41.95, -48.31) * mm});
            skLineSegment(sketch, "E2474", {"start": v(41.95, -48.31) * mm, "end": v(42.55, -47.73) * mm});
            skLineSegment(sketch, "E2475", {"start": v(42.55, -47.73) * mm, "end": v(44.08, -46.14) * mm});
            skLineSegment(sketch, "E2476", {"start": v(44.08, -46.14) * mm, "end": v(46.2, -43.7) * mm});
            skLineSegment(sketch, "E2477", {"start": v(46.2, -43.7) * mm, "end": v(48.6, -40.52) * mm});
            skLineSegment(sketch, "E2478", {"start": v(48.6, -40.52) * mm, "end": v(50.95, -36.77) * mm});
            skLineSegment(sketch, "E2479", {"start": v(50.95, -36.77) * mm, "end": v(52.94, -32.57) * mm});
            skLineSegment(sketch, "E2480", {"start": v(52.94, -32.57) * mm, "end": v(54.25, -28.06) * mm});
            skLineSegment(sketch, "E2481", {"start": v(54.25, -28.06) * mm, "end": v(54.56, -23.38) * mm});
            skLineSegment(sketch, "E2482", {"start": v(54.56, -23.38) * mm, "end": v(54.49, -22.77) * mm});
            skLineSegment(sketch, "E2483", {"start": v(54.49, -22.77) * mm, "end": v(54.3, -21.9) * mm});
            skLineSegment(sketch, "E2484", {"start": v(54.3, -21.9) * mm, "end": v(53.96, -20.79) * mm});
            skLineSegment(sketch, "E2485", {"start": v(53.96, -20.79) * mm, "end": v(53.4, -19.47) * mm});
            skLineSegment(sketch, "E2486", {"start": v(53.4, -19.47) * mm, "end": v(52.56, -17.97) * mm});
            skLineSegment(sketch, "E2487", {"start": v(52.56, -17.97) * mm, "end": v(51.4, -16.33) * mm});
            skLineSegment(sketch, "E2488", {"start": v(51.4, -16.33) * mm, "end": v(49.85, -14.57) * mm});
            skLineSegment(sketch, "E2489", {"start": v(49.85, -14.57) * mm, "end": v(47.88, -12.72) * mm});
            skLineSegment(sketch, "E2490", {"start": v(47.88, -12.72) * mm, "end": v(46.78, -11.85) * mm});
            skLineSegment(sketch, "E2491", {"start": v(46.78, -11.85) * mm, "end": v(45.65, -11.05) * mm});
            skLineSegment(sketch, "E2492", {"start": v(45.65, -11.05) * mm, "end": v(44.5, -10.32) * mm});
            skLineSegment(sketch, "E2493", {"start": v(44.5, -10.32) * mm, "end": v(43.34, -9.68) * mm});
            skLineSegment(sketch, "E2494", {"start": v(43.34, -9.68) * mm, "end": v(42.2, -9.12) * mm});
            skLineSegment(sketch, "E2495", {"start": v(42.2, -9.12) * mm, "end": v(41.09, -8.64) * mm});
            skLineSegment(sketch, "E2496", {"start": v(41.09, -8.64) * mm, "end": v(40.02, -8.25) * mm});
            skLineSegment(sketch, "E2497", {"start": v(40.02, -8.25) * mm, "end": v(39.03, -7.94) * mm});
            skLineSegment(sketch, "E2498", {"start": v(39.03, -7.94) * mm, "end": v(39.03, -9.19) * mm});
            skLineSegment(sketch, "E2499", {"start": v(39.03, -9.19) * mm, "end": v(39.02, -10.43) * mm});
            skLineSegment(sketch, "E2500", {"start": v(39.02, -10.43) * mm, "end": v(39.02, -11.68) * mm});
            skLineSegment(sketch, "E2501", {"start": v(39.02, -11.68) * mm, "end": v(39.02, -12.92) * mm});
            skLineSegment(sketch, "E2502", {"start": v(39.02, -12.92) * mm, "end": v(39.02, -14.17) * mm});
            skLineSegment(sketch, "E2503", {"start": v(39.02, -14.17) * mm, "end": v(39.02, -15.4) * mm});
            skLineSegment(sketch, "E2504", {"start": v(39.02, -15.4) * mm, "end": v(39.02, -16.65) * mm});
            skLineSegment(sketch, "E2505", {"start": v(39.02, -16.65) * mm, "end": v(39.02, -17.9) * mm});
            skLineSegment(sketch, "E2506", {"start": v(39.02, -17.9) * mm, "end": v(37.84, -17.9) * mm});
            skLineSegment(sketch, "E2507", {"start": v(37.84, -17.9) * mm, "end": v(36.66, -17.9) * mm});
            skLineSegment(sketch, "E2508", {"start": v(36.66, -17.9) * mm, "end": v(35.48, -17.9) * mm});
            skLineSegment(sketch, "E2509", {"start": v(35.48, -17.9) * mm, "end": v(34.3, -17.9) * mm});
            skLineSegment(sketch, "E2510", {"start": v(34.3, -17.9) * mm, "end": v(33.12, -17.9) * mm});
            skLineSegment(sketch, "E2511", {"start": v(33.12, -17.9) * mm, "end": v(31.95, -17.9) * mm});
            skLineSegment(sketch, "E2512", {"start": v(31.95, -17.9) * mm, "end": v(30.77, -17.9) * mm});
            skLineSegment(sketch, "E2513", {"start": v(30.77, -17.9) * mm, "end": v(29.59, -17.9) * mm});
            skLineSegment(sketch, "E2514", {"start": v(29.59, -17.9) * mm, "end": v(29.59, -14.86) * mm});
            skLineSegment(sketch, "E2515", {"start": v(29.59, -14.86) * mm, "end": v(29.59, -11.82) * mm});
            skLineSegment(sketch, "E2516", {"start": v(29.59, -11.82) * mm, "end": v(29.59, -8.78) * mm});
            skLineSegment(sketch, "E2517", {"start": v(29.59, -8.78) * mm, "end": v(29.59, -5.75) * mm});
            skLineSegment(sketch, "E2518", {"start": v(29.59, -5.75) * mm, "end": v(29.59, -2.7) * mm});
            skLineSegment(sketch, "E2519", {"start": v(29.59, -2.7) * mm, "end": v(29.59, 0.33) * mm});
            skLineSegment(sketch, "E2520", {"start": v(29.59, 0.33) * mm, "end": v(29.59, 3.37) * mm});
            skLineSegment(sketch, "E2521", {"start": v(29.59, 3.37) * mm, "end": v(29.59, 6.4) * mm});
            skLineSegment(sketch, "E2522", {"start": v(29.59, 6.4) * mm, "end": v(32.13, 6.4) * mm});
            skLineSegment(sketch, "E2523", {"start": v(32.13, 6.4) * mm, "end": v(34.67, 6.4) * mm});
            skLineSegment(sketch, "E2524", {"start": v(34.67, 6.4) * mm, "end": v(37.21, 6.4) * mm});
            skLineSegment(sketch, "E2525", {"start": v(37.21, 6.4) * mm, "end": v(39.75, 6.4) * mm});
            skLineSegment(sketch, "E2526", {"start": v(39.75, 6.4) * mm, "end": v(42.3, 6.4) * mm});
            skLineSegment(sketch, "E2527", {"start": v(42.3, 6.4) * mm, "end": v(44.84, 6.4) * mm});
            skLineSegment(sketch, "E2528", {"start": v(44.84, 6.4) * mm, "end": v(47.38, 6.4) * mm});
            skLineSegment(sketch, "E2529", {"start": v(47.38, 6.4) * mm, "end": v(49.92, 6.4) * mm});
            skLineSegment(sketch, "E2530", {"start": v(49.92, 6.4) * mm, "end": v(51.27, 6.28) * mm});
            skLineSegment(sketch, "E2531", {"start": v(51.27, 6.28) * mm, "end": v(52.78, 5.95) * mm});
            skLineSegment(sketch, "E2532", {"start": v(52.78, 5.95) * mm, "end": v(54.35, 5.38) * mm});
            skLineSegment(sketch, "E2533", {"start": v(54.35, 5.38) * mm, "end": v(55.88, 4.54) * mm});
            skLineSegment(sketch, "E2534", {"start": v(55.88, 4.54) * mm, "end": v(57.26, 3.4) * mm});
            skLineSegment(sketch, "E2535", {"start": v(57.26, 3.4) * mm, "end": v(58.37, 1.91) * mm});
            skLineSegment(sketch, "E2536", {"start": v(58.37, 1.91) * mm, "end": v(59.12, 0.05) * mm});
            skLineSegment(sketch, "E2537", {"start": v(59.12, 0.05) * mm, "end": v(59.4, -2.2) * mm});
            skLineSegment(sketch, "E2538", {"start": v(59.4, -2.2) * mm, "end": v(59.32, -3.34) * mm});
            skLineSegment(sketch, "E2539", {"start": v(59.32, -3.34) * mm, "end": v(59.12, -4.38) * mm});
            skLineSegment(sketch, "E2540", {"start": v(59.12, -4.38) * mm, "end": v(58.8, -5.32) * mm});
            skLineSegment(sketch, "E2541", {"start": v(58.8, -5.32) * mm, "end": v(58.41, -6.17) * mm});
            skLineSegment(sketch, "E2542", {"start": v(58.41, -6.17) * mm, "end": v(57.95, -6.93) * mm});
            skLineSegment(sketch, "E2543", {"start": v(57.95, -6.93) * mm, "end": v(57.46, -7.6) * mm});
            skLineSegment(sketch, "E2544", {"start": v(57.46, -7.6) * mm, "end": v(56.94, -8.18) * mm});
            skLineSegment(sketch, "E2545", {"start": v(56.94, -8.18) * mm, "end": v(56.43, -8.67) * mm});
            skLineSegment(sketch, "E2546", {"start": v(56.43, -8.67) * mm, "end": v(57.32, -9.54) * mm});
            skLineSegment(sketch, "E2547", {"start": v(57.32, -9.54) * mm, "end": v(58.3, -10.61) * mm});
            skLineSegment(sketch, "E2548", {"start": v(58.3, -10.61) * mm, "end": v(59.34, -11.88) * mm});
            skLineSegment(sketch, "E2549", {"start": v(59.34, -11.88) * mm, "end": v(60.36, -13.33) * mm});
            skLineSegment(sketch, "E2550", {"start": v(60.36, -13.33) * mm, "end": v(61.31, -14.95) * mm});
            skLineSegment(sketch, "E2551", {"start": v(61.31, -14.95) * mm, "end": v(62.14, -16.74) * mm});
            skLineSegment(sketch, "E2552", {"start": v(62.14, -16.74) * mm, "end": v(62.78, -18.68) * mm});
            skLineSegment(sketch, "E2553", {"start": v(62.78, -18.68) * mm, "end": v(63.18, -20.76) * mm});
            skLineSegment(sketch, "E2554", {"start": v(63.18, -20.76) * mm, "end": v(63.37, -23.72) * mm});
            skLineSegment(sketch, "E2555", {"start": v(63.37, -23.72) * mm, "end": v(63.2, -26.63) * mm});
            skLineSegment(sketch, "E2556", {"start": v(63.2, -26.63) * mm, "end": v(62.7, -29.47) * mm});
            skLineSegment(sketch, "E2557", {"start": v(62.7, -29.47) * mm, "end": v(61.84, -32.23) * mm});
            skLineSegment(sketch, "E2558", {"start": v(61.84, -32.23) * mm, "end": v(60.64, -34.9) * mm});
            skLineSegment(sketch, "E2559", {"start": v(60.64, -34.9) * mm, "end": v(59.11, -37.49) * mm});
            skLineSegment(sketch, "E2560", {"start": v(59.11, -37.49) * mm, "end": v(57.25, -39.97) * mm});
            skLineSegment(sketch, "E2561", {"start": v(57.25, -39.97) * mm, "end": v(55.06, -42.33) * mm});
            skLineSegment(sketch, "E2562", {"start": v(55.06, -42.33) * mm, "end": v(53.23, -44) * mm});
            skLineSegment(sketch, "E2563", {"start": v(53.23, -44) * mm, "end": v(51.31, -45.55) * mm});
            skLineSegment(sketch, "E2564", {"start": v(51.31, -45.55) * mm, "end": v(49.4, -46.97) * mm});
            skLineSegment(sketch, "E2565", {"start": v(49.4, -46.97) * mm, "end": v(47.62, -48.21) * mm});
            skLineSegment(sketch, "E2566", {"start": v(47.62, -48.21) * mm, "end": v(46.03, -49.24) * mm});
            skLineSegment(sketch, "E2567", {"start": v(46.03, -49.24) * mm, "end": v(44.76, -50.03) * mm});
            skLineSegment(sketch, "E2568", {"start": v(44.76, -50.03) * mm, "end": v(43.9, -50.54) * mm});
            skLineSegment(sketch, "E2569", {"start": v(43.9, -50.54) * mm, "end": v(43.53, -50.74) * mm});
            skLineSegment(sketch, "E2570", {"start": v(43.53, -50.74) * mm, "end": v(42.5, -51.2) * mm});
            skLineSegment(sketch, "E2571", {"start": v(42.5, -51.2) * mm, "end": v(41.46, -51.66) * mm});
            skLineSegment(sketch, "E2572", {"start": v(41.46, -51.66) * mm, "end": v(40.42, -52.12) * mm});
            skLineSegment(sketch, "E2573", {"start": v(40.42, -52.12) * mm, "end": v(39.38, -52.58) * mm});
            skLineSegment(sketch, "E2574", {"start": v(39.38, -52.58) * mm, "end": v(38.35, -53.04) * mm});
            skLineSegment(sketch, "E2575", {"start": v(38.35, -53.04) * mm, "end": v(37.3, -53.5) * mm});
            skLineSegment(sketch, "E2576", {"start": v(37.3, -53.5) * mm, "end": v(36.27, -53.96) * mm});
            skLineSegment(sketch, "E2577", {"start": v(36.27, -53.96) * mm, "end": v(35.24, -54.42) * mm});
            skLineSegment(sketch, "E2578", {"start": v(36.1, -4.54) * mm, "end": v(36.3, -4.56) * mm});
            skLineSegment(sketch, "E2579", {"start": v(36.3, -4.56) * mm, "end": v(36.5, -4.58) * mm});
            skLineSegment(sketch, "E2580", {"start": v(36.5, -4.58) * mm, "end": v(36.7, -4.6) * mm});
            skLineSegment(sketch, "E2581", {"start": v(36.7, -4.6) * mm, "end": v(36.9, -4.62) * mm});
            skLineSegment(sketch, "E2582", {"start": v(36.9, -4.62) * mm, "end": v(37.1, -4.65) * mm});
            skLineSegment(sketch, "E2583", {"start": v(37.1, -4.65) * mm, "end": v(37.3, -4.67) * mm});
            skLineSegment(sketch, "E2584", {"start": v(37.3, -4.67) * mm, "end": v(37.51, -4.69) * mm});
            skLineSegment(sketch, "E2585", {"start": v(37.51, -4.69) * mm, "end": v(37.71, -4.7) * mm});
            skLineSegment(sketch, "E2586", {"start": v(37.71, -4.7) * mm, "end": v(39.1, -4.94) * mm});
            skLineSegment(sketch, "E2587", {"start": v(39.1, -4.94) * mm, "end": v(40.6, -5.34) * mm});
            skLineSegment(sketch, "E2588", {"start": v(40.6, -5.34) * mm, "end": v(42.15, -5.9) * mm});
            skLineSegment(sketch, "E2589", {"start": v(42.15, -5.9) * mm, "end": v(43.74, -6.6) * mm});
            skLineSegment(sketch, "E2590", {"start": v(43.74, -6.6) * mm, "end": v(45.33, -7.43) * mm});
            skLineSegment(sketch, "E2591", {"start": v(45.33, -7.43) * mm, "end": v(46.9, -8.36) * mm});
            skLineSegment(sketch, "E2592", {"start": v(46.9, -8.36) * mm, "end": v(48.38, -9.39) * mm});
            skLineSegment(sketch, "E2593", {"start": v(48.38, -9.39) * mm, "end": v(49.78, -10.49) * mm});
            skLineSegment(sketch, "E2594", {"start": v(49.78, -10.49) * mm, "end": v(52, -12.56) * mm});
            skLineSegment(sketch, "E2595", {"start": v(52, -12.56) * mm, "end": v(53.74, -14.56) * mm});
            skLineSegment(sketch, "E2596", {"start": v(53.74, -14.56) * mm, "end": v(55.08, -16.45) * mm});
            skLineSegment(sketch, "E2597", {"start": v(55.08, -16.45) * mm, "end": v(56.05, -18.2) * mm});
            skLineSegment(sketch, "E2598", {"start": v(56.05, -18.2) * mm, "end": v(56.73, -19.8) * mm});
            skLineSegment(sketch, "E2599", {"start": v(56.73, -19.8) * mm, "end": v(57.15, -21.17) * mm});
            skLineSegment(sketch, "E2600", {"start": v(57.15, -21.17) * mm, "end": v(57.39, -22.32) * mm});
            skLineSegment(sketch, "E2601", {"start": v(57.39, -22.32) * mm, "end": v(57.48, -23.2) * mm});
            skLineSegment(sketch, "E2602", {"start": v(57.48, -23.2) * mm, "end": v(57.5, -25.76) * mm});
            skLineSegment(sketch, "E2603", {"start": v(57.5, -25.76) * mm, "end": v(57.26, -28.25) * mm});
            skLineSegment(sketch, "E2604", {"start": v(57.26, -28.25) * mm, "end": v(56.78, -30.66) * mm});
            skLineSegment(sketch, "E2605", {"start": v(56.78, -30.66) * mm, "end": v(56.11, -32.97) * mm});
            skLineSegment(sketch, "E2606", {"start": v(56.11, -32.97) * mm, "end": v(55.28, -35.17) * mm});
            skLineSegment(sketch, "E2607", {"start": v(55.28, -35.17) * mm, "end": v(54.33, -37.25) * mm});
            skLineSegment(sketch, "E2608", {"start": v(54.33, -37.25) * mm, "end": v(53.28, -39.2) * mm});
            skLineSegment(sketch, "E2609", {"start": v(53.28, -39.2) * mm, "end": v(52.18, -41) * mm});
            skLineSegment(sketch, "E2610", {"start": v(52.18, -41) * mm, "end": v(52.3, -40.9) * mm});
            skLineSegment(sketch, "E2611", {"start": v(52.3, -40.9) * mm, "end": v(52.4, -40.8) * mm});
            skLineSegment(sketch, "E2612", {"start": v(52.4, -40.8) * mm, "end": v(52.52, -40.7) * mm});
            skLineSegment(sketch, "E2613", {"start": v(52.52, -40.7) * mm, "end": v(52.63, -40.59) * mm});
            skLineSegment(sketch, "E2614", {"start": v(52.63, -40.59) * mm, "end": v(52.74, -40.48) * mm});
            skLineSegment(sketch, "E2615", {"start": v(52.74, -40.48) * mm, "end": v(52.85, -40.38) * mm});
            skLineSegment(sketch, "E2616", {"start": v(52.85, -40.38) * mm, "end": v(52.96, -40.27) * mm});
            skLineSegment(sketch, "E2617", {"start": v(52.96, -40.27) * mm, "end": v(53.07, -40.16) * mm});
            skLineSegment(sketch, "E2618", {"start": v(53.07, -40.16) * mm, "end": v(55.03, -38.05) * mm});
            skLineSegment(sketch, "E2619", {"start": v(55.03, -38.05) * mm, "end": v(56.7, -35.85) * mm});
            skLineSegment(sketch, "E2620", {"start": v(56.7, -35.85) * mm, "end": v(58.05, -33.58) * mm});
            skLineSegment(sketch, "E2621", {"start": v(58.05, -33.58) * mm, "end": v(59.1, -31.23) * mm});
            skLineSegment(sketch, "E2622", {"start": v(59.1, -31.23) * mm, "end": v(59.85, -28.8) * mm});
            skLineSegment(sketch, "E2623", {"start": v(59.85, -28.8) * mm, "end": v(60.3, -26.3) * mm});
            skLineSegment(sketch, "E2624", {"start": v(60.3, -26.3) * mm, "end": v(60.43, -23.74) * mm});
            skLineSegment(sketch, "E2625", {"start": v(60.43, -23.74) * mm, "end": v(60.26, -21.11) * mm});
            skLineSegment(sketch, "E2626", {"start": v(60.26, -21.11) * mm, "end": v(59.73, -18.73) * mm});
            skLineSegment(sketch, "E2627", {"start": v(59.73, -18.73) * mm, "end": v(58.83, -16.55) * mm});
            skLineSegment(sketch, "E2628", {"start": v(58.83, -16.55) * mm, "end": v(57.69, -14.62) * mm});
            skLineSegment(sketch, "E2629", {"start": v(57.69, -14.62) * mm, "end": v(56.45, -12.97) * mm});
            skLineSegment(sketch, "E2630", {"start": v(56.45, -12.97) * mm, "end": v(55.24, -11.63) * mm});
            skLineSegment(sketch, "E2631", {"start": v(55.24, -11.63) * mm, "end": v(54.2, -10.62) * mm});
            skLineSegment(sketch, "E2632", {"start": v(54.2, -10.62) * mm, "end": v(53.48, -10) * mm});
            skLineSegment(sketch, "E2633", {"start": v(53.48, -10) * mm, "end": v(53.2, -9.76) * mm});
            skLineSegment(sketch, "E2634", {"start": v(53.2, -9.76) * mm, "end": v(52.95, -9.59) * mm});
            skLineSegment(sketch, "E2635", {"start": v(52.95, -9.59) * mm, "end": v(52.72, -9.41) * mm});
            skLineSegment(sketch, "E2636", {"start": v(52.72, -9.41) * mm, "end": v(52.48, -9.24) * mm});
            skLineSegment(sketch, "E2637", {"start": v(52.48, -9.24) * mm, "end": v(52.24, -9.06) * mm});
            skLineSegment(sketch, "E2638", {"start": v(52.24, -9.06) * mm, "end": v(52, -8.88) * mm});
            skLineSegment(sketch, "E2639", {"start": v(52, -8.88) * mm, "end": v(51.77, -8.7) * mm});
            skLineSegment(sketch, "E2640", {"start": v(51.77, -8.7) * mm, "end": v(51.53, -8.53) * mm});
            skLineSegment(sketch, "E2641", {"start": v(51.53, -8.53) * mm, "end": v(51.3, -8.36) * mm});
            skLineSegment(sketch, "E2642", {"start": v(51.3, -8.36) * mm, "end": v(51.56, -8.22) * mm});
            skLineSegment(sketch, "E2643", {"start": v(51.56, -8.22) * mm, "end": v(51.82, -8.09) * mm});
            skLineSegment(sketch, "E2644", {"start": v(51.82, -8.09) * mm, "end": v(52.08, -7.95) * mm});
            skLineSegment(sketch, "E2645", {"start": v(52.08, -7.95) * mm, "end": v(52.34, -7.82) * mm});
            skLineSegment(sketch, "E2646", {"start": v(52.34, -7.82) * mm, "end": v(52.6, -7.68) * mm});
            skLineSegment(sketch, "E2647", {"start": v(52.6, -7.68) * mm, "end": v(52.87, -7.55) * mm});
            skLineSegment(sketch, "E2648", {"start": v(52.87, -7.55) * mm, "end": v(53.13, -7.41) * mm});
            skLineSegment(sketch, "E2649", {"start": v(53.13, -7.41) * mm, "end": v(53.4, -7.28) * mm});
            skLineSegment(sketch, "E2650", {"start": v(53.4, -7.28) * mm, "end": v(53.56, -7.18) * mm});
            skLineSegment(sketch, "E2651", {"start": v(53.56, -7.18) * mm, "end": v(53.92, -6.94) * mm});
            skLineSegment(sketch, "E2652", {"start": v(53.92, -6.94) * mm, "end": v(54.41, -6.55) * mm});
            skLineSegment(sketch, "E2653", {"start": v(54.41, -6.55) * mm, "end": v(54.97, -6) * mm});
            skLineSegment(sketch, "E2654", {"start": v(54.97, -6) * mm, "end": v(55.52, -5.3) * mm});
            skLineSegment(sketch, "E2655", {"start": v(55.52, -5.3) * mm, "end": v(56, -4.43) * mm});
            skLineSegment(sketch, "E2656", {"start": v(56, -4.43) * mm, "end": v(56.33, -3.4) * mm});
            skLineSegment(sketch, "E2657", {"start": v(56.33, -3.4) * mm, "end": v(56.46, -2.2) * mm});
            skLineSegment(sketch, "E2658", {"start": v(56.46, -2.2) * mm, "end": v(56.2, -0.43) * mm});
            skLineSegment(sketch, "E2659", {"start": v(56.2, -0.43) * mm, "end": v(55.49, 0.93) * mm});
            skLineSegment(sketch, "E2660", {"start": v(55.49, 0.93) * mm, "end": v(54.49, 1.93) * mm});
            skLineSegment(sketch, "E2661", {"start": v(54.49, 1.93) * mm, "end": v(53.33, 2.63) * mm});
            skLineSegment(sketch, "E2662", {"start": v(53.33, 2.63) * mm, "end": v(52.14, 3.07) * mm});
            skLineSegment(sketch, "E2663", {"start": v(52.14, 3.07) * mm, "end": v(51.08, 3.33) * mm});
            skLineSegment(sketch, "E2664", {"start": v(51.08, 3.33) * mm, "end": v(50.27, 3.44) * mm});
            skLineSegment(sketch, "E2665", {"start": v(50.27, 3.44) * mm, "end": v(49.85, 3.47) * mm});
            skLineSegment(sketch, "E2666", {"start": v(49.85, 3.47) * mm, "end": v(47.69, 3.47) * mm});
            skLineSegment(sketch, "E2667", {"start": v(47.69, 3.47) * mm, "end": v(45.52, 3.47) * mm});
            skLineSegment(sketch, "E2668", {"start": v(45.52, 3.47) * mm, "end": v(43.35, 3.47) * mm});
            skLineSegment(sketch, "E2669", {"start": v(43.35, 3.47) * mm, "end": v(41.19, 3.47) * mm});
            skLineSegment(sketch, "E2670", {"start": v(41.19, 3.47) * mm, "end": v(39.02, 3.47) * mm});
            skLineSegment(sketch, "E2671", {"start": v(39.02, 3.47) * mm, "end": v(36.86, 3.47) * mm});
            skLineSegment(sketch, "E2672", {"start": v(36.86, 3.47) * mm, "end": v(34.69, 3.47) * mm});
            skLineSegment(sketch, "E2673", {"start": v(34.69, 3.47) * mm, "end": v(32.52, 3.47) * mm});
            skLineSegment(sketch, "E2674", {"start": v(32.52, 3.47) * mm, "end": v(32.52, 3.26) * mm});
            skLineSegment(sketch, "E2675", {"start": v(32.52, 3.26) * mm, "end": v(32.52, 3.05) * mm});
            skLineSegment(sketch, "E2676", {"start": v(32.52, 3.05) * mm, "end": v(32.52, 2.84) * mm});
            skLineSegment(sketch, "E2677", {"start": v(32.52, 2.84) * mm, "end": v(32.52, 2.64) * mm});
            skLineSegment(sketch, "E2678", {"start": v(32.52, 2.64) * mm, "end": v(32.52, 2.43) * mm});
            skLineSegment(sketch, "E2679", {"start": v(32.52, 2.43) * mm, "end": v(32.52, 2.22) * mm});
            skLineSegment(sketch, "E2680", {"start": v(32.52, 2.22) * mm, "end": v(32.52, 2) * mm});
            skLineSegment(sketch, "E2681", {"start": v(32.52, 2) * mm, "end": v(32.52, 1.8) * mm});
            skLineSegment(sketch, "E2682", {"start": v(32.52, 1.8) * mm, "end": v(34.2, 1.8) * mm});
            skLineSegment(sketch, "E2683", {"start": v(34.2, 1.8) * mm, "end": v(35.89, 1.8) * mm});
            skLineSegment(sketch, "E2684", {"start": v(35.89, 1.8) * mm, "end": v(37.57, 1.8) * mm});
            skLineSegment(sketch, "E2685", {"start": v(37.57, 1.8) * mm, "end": v(39.25, 1.8) * mm});
            skLineSegment(sketch, "E2686", {"start": v(39.25, 1.8) * mm, "end": v(40.93, 1.8) * mm});
            skLineSegment(sketch, "E2687", {"start": v(40.93, 1.8) * mm, "end": v(42.61, 1.8) * mm});
            skLineSegment(sketch, "E2688", {"start": v(42.61, 1.8) * mm, "end": v(44.3, 1.8) * mm});
            skLineSegment(sketch, "E2689", {"start": v(44.3, 1.8) * mm, "end": v(45.98, 1.8) * mm});
            skLineSegment(sketch, "E2690", {"start": v(45.98, 1.8) * mm, "end": v(46.5, 1.8) * mm});
            skLineSegment(sketch, "E2691", {"start": v(46.5, 1.8) * mm, "end": v(47.19, 1.75) * mm});
            skLineSegment(sketch, "E2692", {"start": v(47.19, 1.75) * mm, "end": v(48.01, 1.67) * mm});
            skLineSegment(sketch, "E2693", {"start": v(48.01, 1.67) * mm, "end": v(48.92, 1.52) * mm});
            skLineSegment(sketch, "E2694", {"start": v(48.92, 1.52) * mm, "end": v(49.84, 1.3) * mm});
            skLineSegment(sketch, "E2695", {"start": v(49.84, 1.3) * mm, "end": v(50.74, 0.98) * mm});
            skLineSegment(sketch, "E2696", {"start": v(50.74, 0.98) * mm, "end": v(51.56, 0.55) * mm});
            skLineSegment(sketch, "E2697", {"start": v(51.56, 0.55) * mm, "end": v(52.24, -0.02) * mm});
            skLineSegment(sketch, "E2698", {"start": v(52.24, -0.02) * mm, "end": v(52.44, -0.25) * mm});
            skLineSegment(sketch, "E2699", {"start": v(52.44, -0.25) * mm, "end": v(52.62, -0.5) * mm});
            skLineSegment(sketch, "E2700", {"start": v(52.62, -0.5) * mm, "end": v(52.77, -0.77) * mm});
            skLineSegment(sketch, "E2701", {"start": v(52.77, -0.77) * mm, "end": v(52.88, -1.04) * mm});
            skLineSegment(sketch, "E2702", {"start": v(52.88, -1.04) * mm, "end": v(52.97, -1.33) * mm});
            skLineSegment(sketch, "E2703", {"start": v(52.97, -1.33) * mm, "end": v(53.03, -1.62) * mm});
            skLineSegment(sketch, "E2704", {"start": v(53.03, -1.62) * mm, "end": v(53.06, -1.92) * mm});
            skLineSegment(sketch, "E2705", {"start": v(53.06, -1.92) * mm, "end": v(53.06, -2.23) * mm});
            skLineSegment(sketch, "E2706", {"start": v(53.06, -2.23) * mm, "end": v(52.93, -3.07) * mm});
            skLineSegment(sketch, "E2707", {"start": v(52.93, -3.07) * mm, "end": v(52.66, -3.82) * mm});
            skLineSegment(sketch, "E2708", {"start": v(52.66, -3.82) * mm, "end": v(52.28, -4.47) * mm});
            skLineSegment(sketch, "E2709", {"start": v(52.28, -4.47) * mm, "end": v(51.83, -5.02) * mm});
            skLineSegment(sketch, "E2710", {"start": v(51.83, -5.02) * mm, "end": v(51.32, -5.48) * mm});
            skLineSegment(sketch, "E2711", {"start": v(51.32, -5.48) * mm, "end": v(50.8, -5.85) * mm});
            skLineSegment(sketch, "E2712", {"start": v(50.8, -5.85) * mm, "end": v(50.3, -6.13) * mm});
            skLineSegment(sketch, "E2713", {"start": v(50.3, -6.13) * mm, "end": v(49.85, -6.33) * mm});
            skLineSegment(sketch, "E2714", {"start": v(49.85, -6.33) * mm, "end": v(49.78, -6.35) * mm});
            skLineSegment(sketch, "E2715", {"start": v(49.78, -6.35) * mm, "end": v(49.72, -6.37) * mm});
            skLineSegment(sketch, "E2716", {"start": v(49.72, -6.37) * mm, "end": v(49.65, -6.4) * mm});
            skLineSegment(sketch, "E2717", {"start": v(49.65, -6.4) * mm, "end": v(49.58, -6.42) * mm});
            skLineSegment(sketch, "E2718", {"start": v(49.58, -6.42) * mm, "end": v(49.52, -6.44) * mm});
            skLineSegment(sketch, "E2719", {"start": v(49.52, -6.44) * mm, "end": v(49.45, -6.47) * mm});
            skLineSegment(sketch, "E2720", {"start": v(49.45, -6.47) * mm, "end": v(49.38, -6.5) * mm});
            skLineSegment(sketch, "E2721", {"start": v(49.38, -6.5) * mm, "end": v(49.31, -6.51) * mm});
            skLineSegment(sketch, "E2722", {"start": v(49.31, -6.51) * mm, "end": v(47.22, -5.63) * mm});
            skLineSegment(sketch, "E2723", {"start": v(47.22, -5.63) * mm, "end": v(45.12, -4.74) * mm});
            skLineSegment(sketch, "E2724", {"start": v(45.12, -4.74) * mm, "end": v(43.02, -3.85) * mm});
            skLineSegment(sketch, "E2725", {"start": v(43.02, -3.85) * mm, "end": v(40.92, -2.96) * mm});
            skLineSegment(sketch, "E2726", {"start": v(40.92, -2.96) * mm, "end": v(38.82, -2.08) * mm});
            skLineSegment(sketch, "E2727", {"start": v(38.82, -2.08) * mm, "end": v(36.72, -1.19) * mm});
            skLineSegment(sketch, "E2728", {"start": v(36.72, -1.19) * mm, "end": v(34.62, -0.3) * mm});
            skLineSegment(sketch, "E2729", {"start": v(34.62, -0.3) * mm, "end": v(32.52, 0.59) * mm});
            skLineSegment(sketch, "E2730", {"start": v(32.52, 0.59) * mm, "end": v(32.52, -1.36) * mm});
            skLineSegment(sketch, "E2731", {"start": v(32.52, -1.36) * mm, "end": v(32.52, -3.3) * mm});
            skLineSegment(sketch, "E2732", {"start": v(32.52, -3.3) * mm, "end": v(32.52, -5.24) * mm});
            skLineSegment(sketch, "E2733", {"start": v(32.52, -5.24) * mm, "end": v(32.52, -7.19) * mm});
            skLineSegment(sketch, "E2734", {"start": v(32.52, -7.19) * mm, "end": v(32.52, -9.13) * mm});
            skLineSegment(sketch, "E2735", {"start": v(32.52, -9.13) * mm, "end": v(32.52, -11.08) * mm});
            skLineSegment(sketch, "E2736", {"start": v(32.52, -11.08) * mm, "end": v(32.52, -13.02) * mm});
            skLineSegment(sketch, "E2737", {"start": v(32.52, -13.02) * mm, "end": v(32.52, -14.96) * mm});
            skLineSegment(sketch, "E2738", {"start": v(32.52, -14.96) * mm, "end": v(32.97, -14.96) * mm});
            skLineSegment(sketch, "E2739", {"start": v(32.97, -14.96) * mm, "end": v(33.41, -14.96) * mm});
            skLineSegment(sketch, "E2740", {"start": v(33.41, -14.96) * mm, "end": v(33.86, -14.96) * mm});
            skLineSegment(sketch, "E2741", {"start": v(33.86, -14.96) * mm, "end": v(34.3, -14.96) * mm});
            skLineSegment(sketch, "E2742", {"start": v(34.3, -14.96) * mm, "end": v(34.75, -14.96) * mm});
            skLineSegment(sketch, "E2743", {"start": v(34.75, -14.96) * mm, "end": v(35.2, -14.96) * mm});
            skLineSegment(sketch, "E2744", {"start": v(35.2, -14.96) * mm, "end": v(35.64, -14.96) * mm});
            skLineSegment(sketch, "E2745", {"start": v(35.64, -14.96) * mm, "end": v(36.09, -14.96) * mm});
            skLineSegment(sketch, "E2746", {"start": v(36.09, -14.96) * mm, "end": v(36.09, -13.66) * mm});
            skLineSegment(sketch, "E2747", {"start": v(36.09, -13.66) * mm, "end": v(36.09, -12.36) * mm});
            skLineSegment(sketch, "E2748", {"start": v(36.09, -12.36) * mm, "end": v(36.09, -11.05) * mm});
            skLineSegment(sketch, "E2749", {"start": v(36.09, -11.05) * mm, "end": v(36.1, -9.75) * mm});
            skLineSegment(sketch, "E2750", {"start": v(36.1, -9.75) * mm, "end": v(36.1, -8.45) * mm});
            skLineSegment(sketch, "E2751", {"start": v(36.1, -8.45) * mm, "end": v(36.1, -7.15) * mm});
            skLineSegment(sketch, "E2752", {"start": v(36.1, -7.15) * mm, "end": v(36.1, -5.84) * mm});
            skLineSegment(sketch, "E2753", {"start": v(36.1, -5.84) * mm, "end": v(36.1, -4.54) * mm});
            skLineSegment(sketch, "E2754", {"start": v(44.12, -1.13) * mm, "end": v(44.77, -1.4) * mm});
            skLineSegment(sketch, "E2755", {"start": v(44.77, -1.4) * mm, "end": v(45.42, -1.68) * mm});
            skLineSegment(sketch, "E2756", {"start": v(45.42, -1.68) * mm, "end": v(46.07, -1.96) * mm});
            skLineSegment(sketch, "E2757", {"start": v(46.07, -1.96) * mm, "end": v(46.72, -2.23) * mm});
            skLineSegment(sketch, "E2758", {"start": v(46.72, -2.23) * mm, "end": v(47.36, -2.5) * mm});
            skLineSegment(sketch, "E2759", {"start": v(47.36, -2.5) * mm, "end": v(48.01, -2.78) * mm});
            skLineSegment(sketch, "E2760", {"start": v(48.01, -2.78) * mm, "end": v(48.66, -3.05) * mm});
            skLineSegment(sketch, "E2761", {"start": v(48.66, -3.05) * mm, "end": v(49.3, -3.33) * mm});
            skLineSegment(sketch, "E2762", {"start": v(49.3, -3.33) * mm, "end": v(49.45, -3.23) * mm});
            skLineSegment(sketch, "E2763", {"start": v(49.45, -3.23) * mm, "end": v(49.6, -3.12) * mm});
            skLineSegment(sketch, "E2764", {"start": v(49.6, -3.12) * mm, "end": v(49.76, -3) * mm});
            skLineSegment(sketch, "E2765", {"start": v(49.76, -3) * mm, "end": v(49.9, -2.85) * mm});
            skLineSegment(sketch, "E2766", {"start": v(49.9, -2.85) * mm, "end": v(50.03, -2.69) * mm});
            skLineSegment(sketch, "E2767", {"start": v(50.03, -2.69) * mm, "end": v(50.11, -2.5) * mm});
            skLineSegment(sketch, "E2768", {"start": v(50.11, -2.5) * mm, "end": v(50.15, -2.3) * mm});
            skLineSegment(sketch, "E2769", {"start": v(50.15, -2.3) * mm, "end": v(50.13, -2.06) * mm});
            skLineSegment(sketch, "E2770", {"start": v(50.13, -2.06) * mm, "end": v(50.02, -1.82) * mm});
            skLineSegment(sketch, "E2771", {"start": v(50.02, -1.82) * mm, "end": v(49.74, -1.62) * mm});
            skLineSegment(sketch, "E2772", {"start": v(49.74, -1.62) * mm, "end": v(49.33, -1.46) * mm});
            skLineSegment(sketch, "E2773", {"start": v(49.33, -1.46) * mm, "end": v(48.8, -1.33) * mm});
            skLineSegment(sketch, "E2774", {"start": v(48.8, -1.33) * mm, "end": v(48.18, -1.24) * mm});
            skLineSegment(sketch, "E2775", {"start": v(48.18, -1.24) * mm, "end": v(47.49, -1.18) * mm});
            skLineSegment(sketch, "E2776", {"start": v(47.49, -1.18) * mm, "end": v(46.75, -1.15) * mm});
            skLineSegment(sketch, "E2777", {"start": v(46.75, -1.15) * mm, "end": v(46, -1.13) * mm});
            skLineSegment(sketch, "E2778", {"start": v(46, -1.13) * mm, "end": v(45.76, -1.13) * mm});
            skLineSegment(sketch, "E2779", {"start": v(45.76, -1.13) * mm, "end": v(45.53, -1.13) * mm});
            skLineSegment(sketch, "E2780", {"start": v(45.53, -1.13) * mm, "end": v(45.3, -1.13) * mm});
            skLineSegment(sketch, "E2781", {"start": v(45.3, -1.13) * mm, "end": v(45.06, -1.13) * mm});
            skLineSegment(sketch, "E2782", {"start": v(45.06, -1.13) * mm, "end": v(44.83, -1.13) * mm});
            skLineSegment(sketch, "E2783", {"start": v(44.83, -1.13) * mm, "end": v(44.6, -1.13) * mm});
            skLineSegment(sketch, "E2784", {"start": v(44.6, -1.13) * mm, "end": v(44.36, -1.13) * mm});
            skLineSegment(sketch, "E2785", {"start": v(44.36, -1.13) * mm, "end": v(44.12, -1.13) * mm});
            skLineSegment(sketch, "E2786", {"start": v(-83.25, -15.71) * mm, "end": v(-82.79, -15.72) * mm});
            skLineSegment(sketch, "E2787", {"start": v(-82.79, -15.72) * mm, "end": v(-82.32, -15.72) * mm});
            skLineSegment(sketch, "E2788", {"start": v(-82.32, -15.72) * mm, "end": v(-81.86, -15.73) * mm});
            skLineSegment(sketch, "E2789", {"start": v(-81.86, -15.73) * mm, "end": v(-81.4, -15.73) * mm});
            skLineSegment(sketch, "E2790", {"start": v(-81.4, -15.73) * mm, "end": v(-80.93, -15.74) * mm});
            skLineSegment(sketch, "E2791", {"start": v(-80.93, -15.74) * mm, "end": v(-80.47, -15.74) * mm});
            skLineSegment(sketch, "E2792", {"start": v(-80.47, -15.74) * mm, "end": v(-80, -15.75) * mm});
            skLineSegment(sketch, "E2793", {"start": v(-80, -15.75) * mm, "end": v(-79.54, -15.75) * mm});
            skLineSegment(sketch, "E2794", {"start": v(-79.54, -15.75) * mm, "end": v(-78.88, -15.73) * mm});
            skLineSegment(sketch, "E2795", {"start": v(-78.88, -15.73) * mm, "end": v(-78.23, -15.71) * mm});
            skLineSegment(sketch, "E2796", {"start": v(-78.23, -15.71) * mm, "end": v(-77.57, -15.7) * mm});
            skLineSegment(sketch, "E2797", {"start": v(-77.57, -15.7) * mm, "end": v(-76.91, -15.67) * mm});
            skLineSegment(sketch, "E2798", {"start": v(-76.91, -15.67) * mm, "end": v(-76.25, -15.65) * mm});
            skLineSegment(sketch, "E2799", {"start": v(-76.25, -15.65) * mm, "end": v(-75.6, -15.64) * mm});
            skLineSegment(sketch, "E2800", {"start": v(-75.6, -15.64) * mm, "end": v(-74.94, -15.62) * mm});
            skLineSegment(sketch, "E2801", {"start": v(-74.94, -15.62) * mm, "end": v(-74.28, -15.6) * mm});
            skLineSegment(sketch, "E2802", {"start": v(-74.28, -15.6) * mm, "end": v(-73.76, -15.59) * mm});
            skLineSegment(sketch, "E2803", {"start": v(-73.76, -15.59) * mm, "end": v(-73.3, -15.56) * mm});
            skLineSegment(sketch, "E2804", {"start": v(-73.3, -15.56) * mm, "end": v(-72.87, -15.52) * mm});
            skLineSegment(sketch, "E2805", {"start": v(-72.87, -15.52) * mm, "end": v(-72.5, -15.46) * mm});
            skLineSegment(sketch, "E2806", {"start": v(-72.5, -15.46) * mm, "end": v(-72.16, -15.39) * mm});
            skLineSegment(sketch, "E2807", {"start": v(-72.16, -15.39) * mm, "end": v(-71.88, -15.3) * mm});
            skLineSegment(sketch, "E2808", {"start": v(-71.88, -15.3) * mm, "end": v(-71.65, -15.18) * mm});
            skLineSegment(sketch, "E2809", {"start": v(-71.65, -15.18) * mm, "end": v(-71.46, -15.06) * mm});
            skLineSegment(sketch, "E2810", {"start": v(-71.46, -15.06) * mm, "end": v(-71.3, -14.91) * mm});
            skLineSegment(sketch, "E2811", {"start": v(-71.3, -14.91) * mm, "end": v(-71.17, -14.75) * mm});
            skLineSegment(sketch, "E2812", {"start": v(-71.17, -14.75) * mm, "end": v(-71.06, -14.56) * mm});
            skLineSegment(sketch, "E2813", {"start": v(-71.06, -14.56) * mm, "end": v(-70.96, -14.36) * mm});
            skLineSegment(sketch, "E2814", {"start": v(-70.96, -14.36) * mm, "end": v(-70.9, -14.14) * mm});
            skLineSegment(sketch, "E2815", {"start": v(-70.9, -14.14) * mm, "end": v(-70.84, -13.9) * mm});
            skLineSegment(sketch, "E2816", {"start": v(-70.84, -13.9) * mm, "end": v(-70.81, -13.63) * mm});
            skLineSegment(sketch, "E2817", {"start": v(-70.81, -13.63) * mm, "end": v(-70.8, -13.35) * mm});
            skLineSegment(sketch, "E2818", {"start": v(-70.8, -13.35) * mm, "end": v(-70.81, -13.1) * mm});
            skLineSegment(sketch, "E2819", {"start": v(-70.81, -13.1) * mm, "end": v(-70.85, -12.86) * mm});
            skLineSegment(sketch, "E2820", {"start": v(-70.85, -12.86) * mm, "end": v(-70.9, -12.63) * mm});
            skLineSegment(sketch, "E2821", {"start": v(-70.9, -12.63) * mm, "end": v(-70.99, -12.42) * mm});
            skLineSegment(sketch, "E2822", {"start": v(-70.99, -12.42) * mm, "end": v(-71.1, -12.22) * mm});
            skLineSegment(sketch, "E2823", {"start": v(-71.1, -12.22) * mm, "end": v(-71.23, -12.03) * mm});
            skLineSegment(sketch, "E2824", {"start": v(-71.23, -12.03) * mm, "end": v(-71.38, -11.85) * mm});
            skLineSegment(sketch, "E2825", {"start": v(-71.38, -11.85) * mm, "end": v(-71.56, -11.7) * mm});
            skLineSegment(sketch, "E2826", {"start": v(-71.56, -11.7) * mm, "end": v(-71.76, -11.55) * mm});
            skLineSegment(sketch, "E2827", {"start": v(-71.76, -11.55) * mm, "end": v(-72.02, -11.42) * mm});
            skLineSegment(sketch, "E2828", {"start": v(-72.02, -11.42) * mm, "end": v(-72.31, -11.31) * mm});
            skLineSegment(sketch, "E2829", {"start": v(-72.31, -11.31) * mm, "end": v(-72.65, -11.23) * mm});
            skLineSegment(sketch, "E2830", {"start": v(-72.65, -11.23) * mm, "end": v(-73.03, -11.16) * mm});
            skLineSegment(sketch, "E2831", {"start": v(-73.03, -11.16) * mm, "end": v(-73.46, -11.1) * mm});
            skLineSegment(sketch, "E2832", {"start": v(-73.46, -11.1) * mm, "end": v(-73.92, -11.08) * mm});
            skLineSegment(sketch, "E2833", {"start": v(-73.92, -11.08) * mm, "end": v(-74.43, -11.07) * mm});
            skLineSegment(sketch, "E2834", {"start": v(-74.43, -11.07) * mm, "end": v(-74.6, -11.07) * mm});
            skLineSegment(sketch, "E2835", {"start": v(-74.6, -11.07) * mm, "end": v(-74.75, -11.07) * mm});
            skLineSegment(sketch, "E2836", {"start": v(-74.75, -11.07) * mm, "end": v(-74.91, -11.07) * mm});
            skLineSegment(sketch, "E2837", {"start": v(-74.91, -11.07) * mm, "end": v(-75.07, -11.07) * mm});
            skLineSegment(sketch, "E2838", {"start": v(-75.07, -11.07) * mm, "end": v(-75.23, -11.07) * mm});
            skLineSegment(sketch, "E2839", {"start": v(-75.23, -11.07) * mm, "end": v(-75.4, -11.07) * mm});
            skLineSegment(sketch, "E2840", {"start": v(-75.4, -11.07) * mm, "end": v(-75.55, -11.07) * mm});
            skLineSegment(sketch, "E2841", {"start": v(-75.55, -11.07) * mm, "end": v(-75.71, -11.07) * mm});
            skLineSegment(sketch, "E2842", {"start": v(-75.71, -11.07) * mm, "end": v(-77.33, -11.04) * mm});
            skLineSegment(sketch, "E2843", {"start": v(-77.33, -11.04) * mm, "end": v(-78.94, -11) * mm});
            skLineSegment(sketch, "E2844", {"start": v(-78.94, -11) * mm, "end": v(-80.56, -10.97) * mm});
            skLineSegment(sketch, "E2845", {"start": v(-80.56, -10.97) * mm, "end": v(-82.17, -10.94) * mm});
            skLineSegment(sketch, "E2846", {"start": v(-82.17, -10.94) * mm, "end": v(-83.79, -10.9) * mm});
            skLineSegment(sketch, "E2847", {"start": v(-83.79, -10.9) * mm, "end": v(-85.4, -10.87) * mm});
            skLineSegment(sketch, "E2848", {"start": v(-85.4, -10.87) * mm, "end": v(-87.01, -10.83) * mm});
            skLineSegment(sketch, "E2849", {"start": v(-87.01, -10.83) * mm, "end": v(-88.63, -10.8) * mm});
            skLineSegment(sketch, "E2850", {"start": v(-88.63, -10.8) * mm, "end": v(-89.5, -10.77) * mm});
            skLineSegment(sketch, "E2851", {"start": v(-89.5, -10.77) * mm, "end": v(-90.31, -10.69) * mm});
            skLineSegment(sketch, "E2852", {"start": v(-90.31, -10.69) * mm, "end": v(-91.05, -10.54) * mm});
            skLineSegment(sketch, "E2853", {"start": v(-91.05, -10.54) * mm, "end": v(-91.73, -10.34) * mm});
            skLineSegment(sketch, "E2854", {"start": v(-91.73, -10.34) * mm, "end": v(-92.33, -10.08) * mm});
            skLineSegment(sketch, "E2855", {"start": v(-92.33, -10.08) * mm, "end": v(-92.87, -9.77) * mm});
            skLineSegment(sketch, "E2856", {"start": v(-92.87, -9.77) * mm, "end": v(-93.35, -9.4) * mm});
            skLineSegment(sketch, "E2857", {"start": v(-93.35, -9.4) * mm, "end": v(-93.75, -8.96) * mm});
            skLineSegment(sketch, "E2858", {"start": v(-93.75, -8.96) * mm, "end": v(-94.1, -8.47) * mm});
            skLineSegment(sketch, "E2859", {"start": v(-94.1, -8.47) * mm, "end": v(-94.4, -7.92) * mm});
            skLineSegment(sketch, "E2860", {"start": v(-94.4, -7.92) * mm, "end": v(-94.66, -7.31) * mm});
            skLineSegment(sketch, "E2861", {"start": v(-94.66, -7.31) * mm, "end": v(-94.87, -6.64) * mm});
            skLineSegment(sketch, "E2862", {"start": v(-94.87, -6.64) * mm, "end": v(-95.03, -5.9) * mm});
            skLineSegment(sketch, "E2863", {"start": v(-95.03, -5.9) * mm, "end": v(-95.15, -5.11) * mm});
            skLineSegment(sketch, "E2864", {"start": v(-95.15, -5.11) * mm, "end": v(-95.22, -4.26) * mm});
            skLineSegment(sketch, "E2865", {"start": v(-95.22, -4.26) * mm, "end": v(-95.24, -3.34) * mm});
            skLineSegment(sketch, "E2866", {"start": v(-95.24, -3.34) * mm, "end": v(-95.22, -2.56) * mm});
            skLineSegment(sketch, "E2867", {"start": v(-95.22, -2.56) * mm, "end": v(-95.18, -1.82) * mm});
            skLineSegment(sketch, "E2868", {"start": v(-95.18, -1.82) * mm, "end": v(-95.1, -1.13) * mm});
            skLineSegment(sketch, "E2869", {"start": v(-95.1, -1.13) * mm, "end": v(-95, -0.49) * mm});
            skLineSegment(sketch, "E2870", {"start": v(-95, -0.49) * mm, "end": v(-94.87, 0.12) * mm});
            skLineSegment(sketch, "E2871", {"start": v(-94.87, 0.12) * mm, "end": v(-94.7, 0.67) * mm});
            skLineSegment(sketch, "E2872", {"start": v(-94.7, 0.67) * mm, "end": v(-94.52, 1.18) * mm});
            skLineSegment(sketch, "E2873", {"start": v(-94.52, 1.18) * mm, "end": v(-94.3, 1.65) * mm});
            skLineSegment(sketch, "E2874", {"start": v(-94.3, 1.65) * mm, "end": v(-94.03, 2.08) * mm});
            skLineSegment(sketch, "E2875", {"start": v(-94.03, 2.08) * mm, "end": v(-93.72, 2.47) * mm});
            skLineSegment(sketch, "E2876", {"start": v(-93.72, 2.47) * mm, "end": v(-93.36, 2.82) * mm});
            skLineSegment(sketch, "E2877", {"start": v(-93.36, 2.82) * mm, "end": v(-92.96, 3.14) * mm});
            skLineSegment(sketch, "E2878", {"start": v(-92.96, 3.14) * mm, "end": v(-92.5, 3.43) * mm});
            skLineSegment(sketch, "E2879", {"start": v(-92.5, 3.43) * mm, "end": v(-92, 3.68) * mm});
            skLineSegment(sketch, "E2880", {"start": v(-92, 3.68) * mm, "end": v(-91.45, 3.9) * mm});
            skLineSegment(sketch, "E2881", {"start": v(-91.45, 3.9) * mm, "end": v(-90.85, 4.07) * mm});
            skLineSegment(sketch, "E2882", {"start": v(-90.85, 4.07) * mm, "end": v(-90.2, 4.22) * mm});
            skLineSegment(sketch, "E2883", {"start": v(-90.2, 4.22) * mm, "end": v(-89.5, 4.35) * mm});
            skLineSegment(sketch, "E2884", {"start": v(-89.5, 4.35) * mm, "end": v(-88.76, 4.47) * mm});
            skLineSegment(sketch, "E2885", {"start": v(-88.76, 4.47) * mm, "end": v(-87.97, 4.58) * mm});
            skLineSegment(sketch, "E2886", {"start": v(-87.97, 4.58) * mm, "end": v(-87.13, 4.66) * mm});
            skLineSegment(sketch, "E2887", {"start": v(-87.13, 4.66) * mm, "end": v(-86.24, 4.73) * mm});
            skLineSegment(sketch, "E2888", {"start": v(-86.24, 4.73) * mm, "end": v(-85.3, 4.78) * mm});
            skLineSegment(sketch, "E2889", {"start": v(-85.3, 4.78) * mm, "end": v(-84.32, 4.82) * mm});
            skLineSegment(sketch, "E2890", {"start": v(-84.32, 4.82) * mm, "end": v(-83.35, 4.85) * mm});
            skLineSegment(sketch, "E2891", {"start": v(-83.35, 4.85) * mm, "end": v(-82.46, 4.87) * mm});
            skLineSegment(sketch, "E2892", {"start": v(-82.46, 4.87) * mm, "end": v(-81.66, 4.9) * mm});
            skLineSegment(sketch, "E2893", {"start": v(-81.66, 4.9) * mm, "end": v(-80.94, 4.9) * mm});
            skLineSegment(sketch, "E2894", {"start": v(-80.94, 4.9) * mm, "end": v(-80.3, 4.92) * mm});
            skLineSegment(sketch, "E2895", {"start": v(-80.3, 4.92) * mm, "end": v(-79.74, 4.93) * mm});
            skLineSegment(sketch, "E2896", {"start": v(-79.74, 4.93) * mm, "end": v(-79.27, 4.94) * mm});
            skLineSegment(sketch, "E2897", {"start": v(-79.27, 4.94) * mm, "end": v(-78.88, 4.94) * mm});
            skLineSegment(sketch, "E2898", {"start": v(-78.88, 4.94) * mm, "end": v(-78.2, 4.93) * mm});
            skLineSegment(sketch, "E2899", {"start": v(-78.2, 4.93) * mm, "end": v(-77.5, 4.92) * mm});
            skLineSegment(sketch, "E2900", {"start": v(-77.5, 4.92) * mm, "end": v(-76.82, 4.9) * mm});
            skLineSegment(sketch, "E2901", {"start": v(-76.82, 4.9) * mm, "end": v(-76.14, 4.9) * mm});
            skLineSegment(sketch, "E2902", {"start": v(-76.14, 4.9) * mm, "end": v(-75.45, 4.89) * mm});
            skLineSegment(sketch, "E2903", {"start": v(-75.45, 4.89) * mm, "end": v(-74.76, 4.88) * mm});
            skLineSegment(sketch, "E2904", {"start": v(-74.76, 4.88) * mm, "end": v(-74.08, 4.87) * mm});
            skLineSegment(sketch, "E2905", {"start": v(-74.08, 4.87) * mm, "end": v(-73.4, 4.86) * mm});
            skLineSegment(sketch, "E2906", {"start": v(-73.4, 4.86) * mm, "end": v(-72.59, 4.85) * mm});
            skLineSegment(sketch, "E2907", {"start": v(-72.59, 4.85) * mm, "end": v(-71.83, 4.83) * mm});
            skLineSegment(sketch, "E2908", {"start": v(-71.83, 4.83) * mm, "end": v(-71.1, 4.79) * mm});
            skLineSegment(sketch, "E2909", {"start": v(-71.1, 4.79) * mm, "end": v(-70.42, 4.73) * mm});
            skLineSegment(sketch, "E2910", {"start": v(-70.42, 4.73) * mm, "end": v(-69.78, 4.66) * mm});
            skLineSegment(sketch, "E2911", {"start": v(-69.78, 4.66) * mm, "end": v(-69.18, 4.57) * mm});
            skLineSegment(sketch, "E2912", {"start": v(-69.18, 4.57) * mm, "end": v(-68.62, 4.46) * mm});
            skLineSegment(sketch, "E2913", {"start": v(-68.62, 4.46) * mm, "end": v(-68.1, 4.34) * mm});
            skLineSegment(sketch, "E2914", {"start": v(-68.1, 4.34) * mm, "end": v(-67.61, 4.2) * mm});
            skLineSegment(sketch, "E2915", {"start": v(-67.61, 4.2) * mm, "end": v(-67.16, 4.02) * mm});
            skLineSegment(sketch, "E2916", {"start": v(-67.16, 4.02) * mm, "end": v(-66.75, 3.82) * mm});
            skLineSegment(sketch, "E2917", {"start": v(-66.75, 3.82) * mm, "end": v(-66.38, 3.6) * mm});
            skLineSegment(sketch, "E2918", {"start": v(-66.38, 3.6) * mm, "end": v(-66.04, 3.35) * mm});
            skLineSegment(sketch, "E2919", {"start": v(-66.04, 3.35) * mm, "end": v(-65.74, 3.07) * mm});
            skLineSegment(sketch, "E2920", {"start": v(-65.74, 3.07) * mm, "end": v(-65.48, 2.76) * mm});
            skLineSegment(sketch, "E2921", {"start": v(-65.48, 2.76) * mm, "end": v(-65.25, 2.42) * mm});
            skLineSegment(sketch, "E2922", {"start": v(-65.25, 2.42) * mm, "end": v(-65.05, 2.08) * mm});
            skLineSegment(sketch, "E2923", {"start": v(-65.05, 2.08) * mm, "end": v(-64.87, 1.74) * mm});
            skLineSegment(sketch, "E2924", {"start": v(-64.87, 1.74) * mm, "end": v(-64.71, 1.42) * mm});
            skLineSegment(sketch, "E2925", {"start": v(-64.71, 1.42) * mm, "end": v(-64.57, 1.1) * mm});
            skLineSegment(sketch, "E2926", {"start": v(-64.57, 1.1) * mm, "end": v(-64.45, 0.79) * mm});
            skLineSegment(sketch, "E2927", {"start": v(-64.45, 0.79) * mm, "end": v(-64.34, 0.49) * mm});
            skLineSegment(sketch, "E2928", {"start": v(-64.34, 0.49) * mm, "end": v(-64.26, 0.2) * mm});
            skLineSegment(sketch, "E2929", {"start": v(-64.26, 0.2) * mm, "end": v(-64.19, -0.09) * mm});
            skLineSegment(sketch, "E2930", {"start": v(-64.19, -0.09) * mm, "end": v(-64.13, -0.45) * mm});
            skLineSegment(sketch, "E2931", {"start": v(-64.13, -0.45) * mm, "end": v(-64.09, -0.95) * mm});
            skLineSegment(sketch, "E2932", {"start": v(-64.09, -0.95) * mm, "end": v(-64.05, -1.55) * mm});
            skLineSegment(sketch, "E2933", {"start": v(-64.05, -1.55) * mm, "end": v(-64.01, -2.21) * mm});
            skLineSegment(sketch, "E2934", {"start": v(-64.01, -2.21) * mm, "end": v(-63.99, -2.9) * mm});
            skLineSegment(sketch, "E2935", {"start": v(-63.99, -2.9) * mm, "end": v(-63.97, -3.58) * mm});
            skLineSegment(sketch, "E2936", {"start": v(-63.97, -3.58) * mm, "end": v(-63.96, -4.21) * mm});
            skLineSegment(sketch, "E2937", {"start": v(-63.96, -4.21) * mm, "end": v(-63.96, -4.76) * mm});
            skLineSegment(sketch, "E2938", {"start": v(-63.96, -4.76) * mm, "end": v(-64.04, -4.59) * mm});
            skLineSegment(sketch, "E2939", {"start": v(-64.04, -4.59) * mm, "end": v(-64.35, -4.13) * mm});
            skLineSegment(sketch, "E2940", {"start": v(-64.35, -4.13) * mm, "end": v(-64.95, -3.5) * mm});
            skLineSegment(sketch, "E2941", {"start": v(-64.95, -3.5) * mm, "end": v(-65.9, -2.75) * mm});
            skLineSegment(sketch, "E2942", {"start": v(-65.9, -2.75) * mm, "end": v(-67.29, -2.02) * mm});
            skLineSegment(sketch, "E2943", {"start": v(-67.29, -2.02) * mm, "end": v(-69.16, -1.37) * mm});
            skLineSegment(sketch, "E2944", {"start": v(-69.16, -1.37) * mm, "end": v(-71.6, -0.92) * mm});
            skLineSegment(sketch, "E2945", {"start": v(-71.6, -0.92) * mm, "end": v(-74.67, -0.75) * mm});
            skLineSegment(sketch, "E2946", {"start": v(-74.67, -0.75) * mm, "end": v(-75.14, -0.74) * mm});
            skLineSegment(sketch, "E2947", {"start": v(-75.14, -0.74) * mm, "end": v(-75.62, -0.74) * mm});
            skLineSegment(sketch, "E2948", {"start": v(-75.62, -0.74) * mm, "end": v(-76.09, -0.73) * mm});
            skLineSegment(sketch, "E2949", {"start": v(-76.09, -0.73) * mm, "end": v(-76.56, -0.73) * mm});
            skLineSegment(sketch, "E2950", {"start": v(-76.56, -0.73) * mm, "end": v(-77.04, -0.72) * mm});
            skLineSegment(sketch, "E2951", {"start": v(-77.04, -0.72) * mm, "end": v(-77.51, -0.72) * mm});
            skLineSegment(sketch, "E2952", {"start": v(-77.51, -0.72) * mm, "end": v(-77.98, -0.71) * mm});
            skLineSegment(sketch, "E2953", {"start": v(-77.98, -0.71) * mm, "end": v(-78.46, -0.7) * mm});
            skLineSegment(sketch, "E2954", {"start": v(-78.46, -0.7) * mm, "end": v(-79.2, -0.73) * mm});
            skLineSegment(sketch, "E2955", {"start": v(-79.2, -0.73) * mm, "end": v(-79.96, -0.76) * mm});
            skLineSegment(sketch, "E2956", {"start": v(-79.96, -0.76) * mm, "end": v(-80.7, -0.78) * mm});
            skLineSegment(sketch, "E2957", {"start": v(-80.7, -0.78) * mm, "end": v(-81.45, -0.8) * mm});
            skLineSegment(sketch, "E2958", {"start": v(-81.45, -0.8) * mm, "end": v(-82.2, -0.83) * mm});
            skLineSegment(sketch, "E2959", {"start": v(-82.2, -0.83) * mm, "end": v(-82.95, -0.85) * mm});
            skLineSegment(sketch, "E2960", {"start": v(-82.95, -0.85) * mm, "end": v(-83.7, -0.88) * mm});
            skLineSegment(sketch, "E2961", {"start": v(-83.7, -0.88) * mm, "end": v(-84.45, -0.9) * mm});
            skLineSegment(sketch, "E2962", {"start": v(-84.45, -0.9) * mm, "end": v(-84.75, -0.9) * mm});
            skLineSegment(sketch, "E2963", {"start": v(-84.75, -0.9) * mm, "end": v(-85.03, -0.93) * mm});
            skLineSegment(sketch, "E2964", {"start": v(-85.03, -0.93) * mm, "end": v(-85.3, -0.96) * mm});
            skLineSegment(sketch, "E2965", {"start": v(-85.3, -0.96) * mm, "end": v(-85.56, -1.01) * mm});
            skLineSegment(sketch, "E2966", {"start": v(-85.56, -1.01) * mm, "end": v(-85.8, -1.08) * mm});
            skLineSegment(sketch, "E2967", {"start": v(-85.8, -1.08) * mm, "end": v(-86.04, -1.15) * mm});
            skLineSegment(sketch, "E2968", {"start": v(-86.04, -1.15) * mm, "end": v(-86.27, -1.24) * mm});
            skLineSegment(sketch, "E2969", {"start": v(-86.27, -1.24) * mm, "end": v(-86.48, -1.35) * mm});
            skLineSegment(sketch, "E2970", {"start": v(-86.48, -1.35) * mm, "end": v(-86.68, -1.47) * mm});
            skLineSegment(sketch, "E2971", {"start": v(-86.68, -1.47) * mm, "end": v(-86.85, -1.6) * mm});
            skLineSegment(sketch, "E2972", {"start": v(-86.85, -1.6) * mm, "end": v(-86.99, -1.77) * mm});
            skLineSegment(sketch, "E2973", {"start": v(-86.99, -1.77) * mm, "end": v(-87.1, -1.94) * mm});
            skLineSegment(sketch, "E2974", {"start": v(-87.1, -1.94) * mm, "end": v(-87.2, -2.14) * mm});
            skLineSegment(sketch, "E2975", {"start": v(-87.2, -2.14) * mm, "end": v(-87.26, -2.35) * mm});
            skLineSegment(sketch, "E2976", {"start": v(-87.26, -2.35) * mm, "end": v(-87.3, -2.58) * mm});
            skLineSegment(sketch, "E2977", {"start": v(-87.3, -2.58) * mm, "end": v(-87.31, -2.84) * mm});
            skLineSegment(sketch, "E2978", {"start": v(-87.31, -2.84) * mm, "end": v(-87.3, -3.18) * mm});
            skLineSegment(sketch, "E2979", {"start": v(-87.3, -3.18) * mm, "end": v(-87.25, -3.49) * mm});
            skLineSegment(sketch, "E2980", {"start": v(-87.25, -3.49) * mm, "end": v(-87.17, -3.77) * mm});
            skLineSegment(sketch, "E2981", {"start": v(-87.17, -3.77) * mm, "end": v(-87.07, -4.02) * mm});
            skLineSegment(sketch, "E2982", {"start": v(-87.07, -4.02) * mm, "end": v(-86.93, -4.24) * mm});
            skLineSegment(sketch, "E2983", {"start": v(-86.93, -4.24) * mm, "end": v(-86.76, -4.43) * mm});
            skLineSegment(sketch, "E2984", {"start": v(-86.76, -4.43) * mm, "end": v(-86.56, -4.58) * mm});
            skLineSegment(sketch, "E2985", {"start": v(-86.56, -4.58) * mm, "end": v(-86.33, -4.71) * mm});
            skLineSegment(sketch, "E2986", {"start": v(-86.33, -4.71) * mm, "end": v(-86.07, -4.82) * mm});
            skLineSegment(sketch, "E2987", {"start": v(-86.07, -4.82) * mm, "end": v(-85.79, -4.9) * mm});
            skLineSegment(sketch, "E2988", {"start": v(-85.79, -4.9) * mm, "end": v(-85.49, -4.98) * mm});
            skLineSegment(sketch, "E2989", {"start": v(-85.49, -4.98) * mm, "end": v(-85.16, -5.04) * mm});
            skLineSegment(sketch, "E2990", {"start": v(-85.16, -5.04) * mm, "end": v(-84.82, -5.1) * mm});
            skLineSegment(sketch, "E2991", {"start": v(-84.82, -5.1) * mm, "end": v(-84.45, -5.13) * mm});
            skLineSegment(sketch, "E2992", {"start": v(-84.45, -5.13) * mm, "end": v(-84.05, -5.15) * mm});
            skLineSegment(sketch, "E2993", {"start": v(-84.05, -5.15) * mm, "end": v(-83.64, -5.16) * mm});
            skLineSegment(sketch, "E2994", {"start": v(-83.64, -5.16) * mm, "end": v(-83.54, -5.16) * mm});
            skLineSegment(sketch, "E2995", {"start": v(-83.54, -5.16) * mm, "end": v(-83.44, -5.16) * mm});
            skLineSegment(sketch, "E2996", {"start": v(-83.44, -5.16) * mm, "end": v(-83.34, -5.16) * mm});
            skLineSegment(sketch, "E2997", {"start": v(-83.34, -5.16) * mm, "end": v(-83.23, -5.16) * mm});
            skLineSegment(sketch, "E2998", {"start": v(-83.23, -5.16) * mm, "end": v(-83.13, -5.16) * mm});
            skLineSegment(sketch, "E2999", {"start": v(-83.13, -5.16) * mm, "end": v(-83.03, -5.16) * mm});
            skLineSegment(sketch, "E3000", {"start": v(-83.03, -5.16) * mm, "end": v(-82.93, -5.16) * mm});
            skLineSegment(sketch, "E3001", {"start": v(-82.93, -5.16) * mm, "end": v(-82.83, -5.16) * mm});
            skLineSegment(sketch, "E3002", {"start": v(-82.83, -5.16) * mm, "end": v(-82.17, -5.17) * mm});
            skLineSegment(sketch, "E3003", {"start": v(-82.17, -5.17) * mm, "end": v(-81.51, -5.18) * mm});
            skLineSegment(sketch, "E3004", {"start": v(-81.51, -5.18) * mm, "end": v(-80.86, -5.19) * mm});
            skLineSegment(sketch, "E3005", {"start": v(-80.86, -5.19) * mm, "end": v(-80.2, -5.2) * mm});
            skLineSegment(sketch, "E3006", {"start": v(-80.2, -5.2) * mm, "end": v(-79.54, -5.2) * mm});
            skLineSegment(sketch, "E3007", {"start": v(-79.54, -5.2) * mm, "end": v(-78.88, -5.21) * mm});
            skLineSegment(sketch, "E3008", {"start": v(-78.88, -5.21) * mm, "end": v(-78.22, -5.22) * mm});
            skLineSegment(sketch, "E3009", {"start": v(-78.22, -5.22) * mm, "end": v(-77.57, -5.23) * mm});
            skLineSegment(sketch, "E3010", {"start": v(-77.57, -5.23) * mm, "end": v(-76.92, -5.24) * mm});
            skLineSegment(sketch, "E3011", {"start": v(-76.92, -5.24) * mm, "end": v(-76.27, -5.24) * mm});
            skLineSegment(sketch, "E3012", {"start": v(-76.27, -5.24) * mm, "end": v(-75.62, -5.25) * mm});
            skLineSegment(sketch, "E3013", {"start": v(-75.62, -5.25) * mm, "end": v(-74.98, -5.25) * mm});
            skLineSegment(sketch, "E3014", {"start": v(-74.98, -5.25) * mm, "end": v(-74.33, -5.26) * mm});
            skLineSegment(sketch, "E3015", {"start": v(-74.33, -5.26) * mm, "end": v(-73.68, -5.26) * mm});
            skLineSegment(sketch, "E3016", {"start": v(-73.68, -5.26) * mm, "end": v(-73.03, -5.27) * mm});
            skLineSegment(sketch, "E3017", {"start": v(-73.03, -5.27) * mm, "end": v(-72.39, -5.27) * mm});
            skLineSegment(sketch, "E3018", {"start": v(-72.39, -5.27) * mm, "end": v(-71.18, -5.3) * mm});
            skLineSegment(sketch, "E3019", {"start": v(-71.18, -5.3) * mm, "end": v(-70.06, -5.37) * mm});
            skLineSegment(sketch, "E3020", {"start": v(-70.06, -5.37) * mm, "end": v(-69.03, -5.5) * mm});
            skLineSegment(sketch, "E3021", {"start": v(-69.03, -5.5) * mm, "end": v(-68.08, -5.66) * mm});
            skLineSegment(sketch, "E3022", {"start": v(-68.08, -5.66) * mm, "end": v(-67.21, -5.88) * mm});
            skLineSegment(sketch, "E3023", {"start": v(-67.21, -5.88) * mm, "end": v(-66.44, -6.15) * mm});
            skLineSegment(sketch, "E3024", {"start": v(-66.44, -6.15) * mm, "end": v(-65.74, -6.47) * mm});
            skLineSegment(sketch, "E3025", {"start": v(-65.74, -6.47) * mm, "end": v(-65.14, -6.84) * mm});
            skLineSegment(sketch, "E3026", {"start": v(-65.14, -6.84) * mm, "end": v(-64.6, -7.28) * mm});
            skLineSegment(sketch, "E3027", {"start": v(-64.6, -7.28) * mm, "end": v(-64.15, -7.82) * mm});
            skLineSegment(sketch, "E3028", {"start": v(-64.15, -7.82) * mm, "end": v(-63.76, -8.46) * mm});
            skLineSegment(sketch, "E3029", {"start": v(-63.76, -8.46) * mm, "end": v(-63.44, -9.2) * mm});
            skLineSegment(sketch, "E3030", {"start": v(-63.44, -9.2) * mm, "end": v(-63.2, -10.03) * mm});
            skLineSegment(sketch, "E3031", {"start": v(-63.2, -10.03) * mm, "end": v(-63.01, -10.96) * mm});
            skLineSegment(sketch, "E3032", {"start": v(-63.01, -10.96) * mm, "end": v(-62.9, -12) * mm});
            skLineSegment(sketch, "E3033", {"start": v(-62.9, -12) * mm, "end": v(-62.87, -13.12) * mm});
            skLineSegment(sketch, "E3034", {"start": v(-62.87, -13.12) * mm, "end": v(-62.9, -14.22) * mm});
            skLineSegment(sketch, "E3035", {"start": v(-62.9, -14.22) * mm, "end": v(-63, -15.22) * mm});
            skLineSegment(sketch, "E3036", {"start": v(-63, -15.22) * mm, "end": v(-63.16, -16.14) * mm});
            skLineSegment(sketch, "E3037", {"start": v(-63.16, -16.14) * mm, "end": v(-63.38, -16.97) * mm});
            skLineSegment(sketch, "E3038", {"start": v(-63.38, -16.97) * mm, "end": v(-63.67, -17.7) * mm});
            skLineSegment(sketch, "E3039", {"start": v(-63.67, -17.7) * mm, "end": v(-64.01, -18.36) * mm});
            skLineSegment(sketch, "E3040", {"start": v(-64.01, -18.36) * mm, "end": v(-64.43, -18.92) * mm});
            skLineSegment(sketch, "E3041", {"start": v(-64.43, -18.92) * mm, "end": v(-64.9, -19.39) * mm});
            skLineSegment(sketch, "E3042", {"start": v(-64.9, -19.39) * mm, "end": v(-65.45, -19.79) * mm});
            skLineSegment(sketch, "E3043", {"start": v(-65.45, -19.79) * mm, "end": v(-66.08, -20.13) * mm});
            skLineSegment(sketch, "E3044", {"start": v(-66.08, -20.13) * mm, "end": v(-66.8, -20.42) * mm});
            skLineSegment(sketch, "E3045", {"start": v(-66.8, -20.42) * mm, "end": v(-67.6, -20.66) * mm});
            skLineSegment(sketch, "E3046", {"start": v(-67.6, -20.66) * mm, "end": v(-68.48, -20.85) * mm});
            skLineSegment(sketch, "E3047", {"start": v(-68.48, -20.85) * mm, "end": v(-69.44, -20.98) * mm});
            skLineSegment(sketch, "E3048", {"start": v(-69.44, -20.98) * mm, "end": v(-70.48, -21.06) * mm});
            skLineSegment(sketch, "E3049", {"start": v(-70.48, -21.06) * mm, "end": v(-71.61, -21.09) * mm});
            skLineSegment(sketch, "E3050", {"start": v(-71.61, -21.09) * mm, "end": v(-72.87, -21.12) * mm});
            skLineSegment(sketch, "E3051", {"start": v(-72.87, -21.12) * mm, "end": v(-74.13, -21.16) * mm});
            skLineSegment(sketch, "E3052", {"start": v(-74.13, -21.16) * mm, "end": v(-75.38, -21.2) * mm});
            skLineSegment(sketch, "E3053", {"start": v(-75.38, -21.2) * mm, "end": v(-76.64, -21.22) * mm});
            skLineSegment(sketch, "E3054", {"start": v(-76.64, -21.22) * mm, "end": v(-77.9, -21.26) * mm});
            skLineSegment(sketch, "E3055", {"start": v(-77.9, -21.26) * mm, "end": v(-79.15, -21.3) * mm});
            skLineSegment(sketch, "E3056", {"start": v(-79.15, -21.3) * mm, "end": v(-80.41, -21.33) * mm});
            skLineSegment(sketch, "E3057", {"start": v(-80.41, -21.33) * mm, "end": v(-81.67, -21.36) * mm});
            skLineSegment(sketch, "E3058", {"start": v(-81.67, -21.36) * mm, "end": v(-82.32, -21.35) * mm});
            skLineSegment(sketch, "E3059", {"start": v(-82.32, -21.35) * mm, "end": v(-82.98, -21.33) * mm});
            skLineSegment(sketch, "E3060", {"start": v(-82.98, -21.33) * mm, "end": v(-83.64, -21.32) * mm});
            skLineSegment(sketch, "E3061", {"start": v(-83.64, -21.32) * mm, "end": v(-84.3, -21.3) * mm});
            skLineSegment(sketch, "E3062", {"start": v(-84.3, -21.3) * mm, "end": v(-84.95, -21.29) * mm});
            skLineSegment(sketch, "E3063", {"start": v(-84.95, -21.29) * mm, "end": v(-85.61, -21.27) * mm});
            skLineSegment(sketch, "E3064", {"start": v(-85.61, -21.27) * mm, "end": v(-86.27, -21.26) * mm});
            skLineSegment(sketch, "E3065", {"start": v(-86.27, -21.26) * mm, "end": v(-86.93, -21.24) * mm});
            skLineSegment(sketch, "E3066", {"start": v(-86.93, -21.24) * mm, "end": v(-87.94, -21.22) * mm});
            skLineSegment(sketch, "E3067", {"start": v(-87.94, -21.22) * mm, "end": v(-88.88, -21.16) * mm});
            skLineSegment(sketch, "E3068", {"start": v(-88.88, -21.16) * mm, "end": v(-89.75, -21.05) * mm});
            skLineSegment(sketch, "E3069", {"start": v(-89.75, -21.05) * mm, "end": v(-90.55, -20.9) * mm});
            skLineSegment(sketch, "E3070", {"start": v(-90.55, -20.9) * mm, "end": v(-91.29, -20.71) * mm});
            skLineSegment(sketch, "E3071", {"start": v(-91.29, -20.71) * mm, "end": v(-91.95, -20.48) * mm});
            skLineSegment(sketch, "E3072", {"start": v(-91.95, -20.48) * mm, "end": v(-92.55, -20.2) * mm});
            skLineSegment(sketch, "E3073", {"start": v(-92.55, -20.2) * mm, "end": v(-93.07, -19.89) * mm});
            skLineSegment(sketch, "E3074", {"start": v(-93.07, -19.89) * mm, "end": v(-93.54, -19.5) * mm});
            skLineSegment(sketch, "E3075", {"start": v(-93.54, -19.5) * mm, "end": v(-93.94, -19.04) * mm});
            skLineSegment(sketch, "E3076", {"start": v(-93.94, -19.04) * mm, "end": v(-94.28, -18.49) * mm});
            skLineSegment(sketch, "E3077", {"start": v(-94.28, -18.49) * mm, "end": v(-94.55, -17.85) * mm});
            skLineSegment(sketch, "E3078", {"start": v(-94.55, -17.85) * mm, "end": v(-94.77, -17.13) * mm});
            skLineSegment(sketch, "E3079", {"start": v(-94.77, -17.13) * mm, "end": v(-94.92, -16.32) * mm});
            skLineSegment(sketch, "E3080", {"start": v(-94.92, -16.32) * mm, "end": v(-95.02, -15.42) * mm});
            skLineSegment(sketch, "E3081", {"start": v(-95.02, -15.42) * mm, "end": v(-95.05, -14.44) * mm});
            skLineSegment(sketch, "E3082", {"start": v(-95.05, -14.44) * mm, "end": v(-95.05, -14.11) * mm});
            skLineSegment(sketch, "E3083", {"start": v(-95.05, -14.11) * mm, "end": v(-95.05, -13.8) * mm});
            skLineSegment(sketch, "E3084", {"start": v(-95.05, -13.8) * mm, "end": v(-95.05, -13.47) * mm});
            skLineSegment(sketch, "E3085", {"start": v(-95.05, -13.47) * mm, "end": v(-95.05, -13.15) * mm});
            skLineSegment(sketch, "E3086", {"start": v(-95.05, -13.15) * mm, "end": v(-95.05, -12.83) * mm});
            skLineSegment(sketch, "E3087", {"start": v(-95.05, -12.83) * mm, "end": v(-95.05, -12.5) * mm});
            skLineSegment(sketch, "E3088", {"start": v(-95.05, -12.5) * mm, "end": v(-95.05, -12.18) * mm});
            skLineSegment(sketch, "E3089", {"start": v(-95.05, -12.18) * mm, "end": v(-95.05, -11.86) * mm});
            skLineSegment(sketch, "E3090", {"start": v(-95.05, -11.86) * mm, "end": v(-94.95, -12.03) * mm});
            skLineSegment(sketch, "E3091", {"start": v(-94.95, -12.03) * mm, "end": v(-94.61, -12.46) * mm});
            skLineSegment(sketch, "E3092", {"start": v(-94.61, -12.46) * mm, "end": v(-93.96, -13.08) * mm});
            skLineSegment(sketch, "E3093", {"start": v(-93.96, -13.08) * mm, "end": v(-92.91, -13.79) * mm});
            skLineSegment(sketch, "E3094", {"start": v(-92.91, -13.79) * mm, "end": v(-91.4, -14.5) * mm});
            skLineSegment(sketch, "E3095", {"start": v(-91.4, -14.5) * mm, "end": v(-89.33, -15.11) * mm});
            skLineSegment(sketch, "E3096", {"start": v(-89.33, -15.11) * mm, "end": v(-86.64, -15.55) * mm});
            skLineSegment(sketch, "E3097", {"start": v(-86.64, -15.55) * mm, "end": v(-83.25, -15.71) * mm});
            skLineSegment(sketch, "E3098", {"start": v(-93.57, -15.1) * mm, "end": v(-93.53, -15.63) * mm});
            skLineSegment(sketch, "E3099", {"start": v(-93.53, -15.63) * mm, "end": v(-93.46, -16.15) * mm});
            skLineSegment(sketch, "E3100", {"start": v(-93.46, -16.15) * mm, "end": v(-93.37, -16.67) * mm});
            skLineSegment(sketch, "E3101", {"start": v(-93.37, -16.67) * mm, "end": v(-93.23, -17.17) * mm});
            skLineSegment(sketch, "E3102", {"start": v(-93.23, -17.17) * mm, "end": v(-93.06, -17.63) * mm});
            skLineSegment(sketch, "E3103", {"start": v(-93.06, -17.63) * mm, "end": v(-92.84, -18.04) * mm});
            skLineSegment(sketch, "E3104", {"start": v(-92.84, -18.04) * mm, "end": v(-92.57, -18.4) * mm});
            skLineSegment(sketch, "E3105", {"start": v(-92.57, -18.4) * mm, "end": v(-92.24, -18.68) * mm});
            skLineSegment(sketch, "E3106", {"start": v(-92.24, -18.68) * mm, "end": v(-91.81, -18.94) * mm});
            skLineSegment(sketch, "E3107", {"start": v(-91.81, -18.94) * mm, "end": v(-91.31, -19.16) * mm});
            skLineSegment(sketch, "E3108", {"start": v(-91.31, -19.16) * mm, "end": v(-90.75, -19.35) * mm});
            skLineSegment(sketch, "E3109", {"start": v(-90.75, -19.35) * mm, "end": v(-90.11, -19.5) * mm});
            skLineSegment(sketch, "E3110", {"start": v(-90.11, -19.5) * mm, "end": v(-89.41, -19.62) * mm});
            skLineSegment(sketch, "E3111", {"start": v(-89.41, -19.62) * mm, "end": v(-88.65, -19.7) * mm});
            skLineSegment(sketch, "E3112", {"start": v(-88.65, -19.7) * mm, "end": v(-87.82, -19.76) * mm});
            skLineSegment(sketch, "E3113", {"start": v(-87.82, -19.76) * mm, "end": v(-86.93, -19.78) * mm});
            skLineSegment(sketch, "E3114", {"start": v(-86.93, -19.78) * mm, "end": v(-86.27, -19.8) * mm});
            skLineSegment(sketch, "E3115", {"start": v(-86.27, -19.8) * mm, "end": v(-85.61, -19.8) * mm});
            skLineSegment(sketch, "E3116", {"start": v(-85.61, -19.8) * mm, "end": v(-84.95, -19.82) * mm});
            skLineSegment(sketch, "E3117", {"start": v(-84.95, -19.82) * mm, "end": v(-84.3, -19.83) * mm});
            skLineSegment(sketch, "E3118", {"start": v(-84.3, -19.83) * mm, "end": v(-83.64, -19.85) * mm});
            skLineSegment(sketch, "E3119", {"start": v(-83.64, -19.85) * mm, "end": v(-82.98, -19.86) * mm});
            skLineSegment(sketch, "E3120", {"start": v(-82.98, -19.86) * mm, "end": v(-82.33, -19.88) * mm});
            skLineSegment(sketch, "E3121", {"start": v(-82.33, -19.88) * mm, "end": v(-81.67, -19.9) * mm});
            skLineSegment(sketch, "E3122", {"start": v(-81.67, -19.9) * mm, "end": v(-80.42, -19.86) * mm});
            skLineSegment(sketch, "E3123", {"start": v(-80.42, -19.86) * mm, "end": v(-79.17, -19.82) * mm});
            skLineSegment(sketch, "E3124", {"start": v(-79.17, -19.82) * mm, "end": v(-77.91, -19.8) * mm});
            skLineSegment(sketch, "E3125", {"start": v(-77.91, -19.8) * mm, "end": v(-76.66, -19.76) * mm});
            skLineSegment(sketch, "E3126", {"start": v(-76.66, -19.76) * mm, "end": v(-75.4, -19.72) * mm});
            skLineSegment(sketch, "E3127", {"start": v(-75.4, -19.72) * mm, "end": v(-74.16, -19.69) * mm});
            skLineSegment(sketch, "E3128", {"start": v(-74.16, -19.69) * mm, "end": v(-72.9, -19.66) * mm});
            skLineSegment(sketch, "E3129", {"start": v(-72.9, -19.66) * mm, "end": v(-71.65, -19.62) * mm});
            skLineSegment(sketch, "E3130", {"start": v(-71.65, -19.62) * mm, "end": v(-71.65, -19.62) * mm});
            skLineSegment(sketch, "E3131", {"start": v(-71.65, -19.62) * mm, "end": v(-71.64, -19.62) * mm});
            skLineSegment(sketch, "E3132", {"start": v(-71.64, -19.62) * mm, "end": v(-71.64, -19.62) * mm});
            skLineSegment(sketch, "E3133", {"start": v(-71.64, -19.62) * mm, "end": v(-71.63, -19.62) * mm});
            skLineSegment(sketch, "E3134", {"start": v(-71.63, -19.62) * mm, "end": v(-71.63, -19.62) * mm});
            skLineSegment(sketch, "E3135", {"start": v(-71.63, -19.62) * mm, "end": v(-71.62, -19.62) * mm});
            skLineSegment(sketch, "E3136", {"start": v(-71.62, -19.62) * mm, "end": v(-71.62, -19.62) * mm});
            skLineSegment(sketch, "E3137", {"start": v(-71.62, -19.62) * mm, "end": v(-71.61, -19.62) * mm});
            skLineSegment(sketch, "E3138", {"start": v(-71.61, -19.62) * mm, "end": v(-70.63, -19.6) * mm});
            skLineSegment(sketch, "E3139", {"start": v(-70.63, -19.6) * mm, "end": v(-69.72, -19.53) * mm});
            skLineSegment(sketch, "E3140", {"start": v(-69.72, -19.53) * mm, "end": v(-68.88, -19.43) * mm});
            skLineSegment(sketch, "E3141", {"start": v(-68.88, -19.43) * mm, "end": v(-68.1, -19.28) * mm});
            skLineSegment(sketch, "E3142", {"start": v(-68.1, -19.28) * mm, "end": v(-67.42, -19.08) * mm});
            skLineSegment(sketch, "E3143", {"start": v(-67.42, -19.08) * mm, "end": v(-66.81, -18.85) * mm});
            skLineSegment(sketch, "E3144", {"start": v(-66.81, -18.85) * mm, "end": v(-66.29, -18.58) * mm});
            skLineSegment(sketch, "E3145", {"start": v(-66.29, -18.58) * mm, "end": v(-65.85, -18.26) * mm});
            skLineSegment(sketch, "E3146", {"start": v(-65.85, -18.26) * mm, "end": v(-65.5, -17.9) * mm});
            skLineSegment(sketch, "E3147", {"start": v(-65.5, -17.9) * mm, "end": v(-65.2, -17.47) * mm});
            skLineSegment(sketch, "E3148", {"start": v(-65.2, -17.47) * mm, "end": v(-64.94, -16.94) * mm});
            skLineSegment(sketch, "E3149", {"start": v(-64.94, -16.94) * mm, "end": v(-64.72, -16.33) * mm});
            skLineSegment(sketch, "E3150", {"start": v(-64.72, -16.33) * mm, "end": v(-64.56, -15.65) * mm});
            skLineSegment(sketch, "E3151", {"start": v(-64.56, -15.65) * mm, "end": v(-64.44, -14.88) * mm});
            skLineSegment(sketch, "E3152", {"start": v(-64.44, -14.88) * mm, "end": v(-64.36, -14.04) * mm});
            skLineSegment(sketch, "E3153", {"start": v(-64.36, -14.04) * mm, "end": v(-64.34, -13.12) * mm});
            skLineSegment(sketch, "E3154", {"start": v(-64.34, -13.12) * mm, "end": v(-64.35, -12.42) * mm});
            skLineSegment(sketch, "E3155", {"start": v(-64.35, -12.42) * mm, "end": v(-64.4, -11.7) * mm});
            skLineSegment(sketch, "E3156", {"start": v(-64.4, -11.7) * mm, "end": v(-64.5, -10.97) * mm});
            skLineSegment(sketch, "E3157", {"start": v(-64.5, -10.97) * mm, "end": v(-64.65, -10.26) * mm});
            skLineSegment(sketch, "E3158", {"start": v(-64.65, -10.26) * mm, "end": v(-64.86, -9.59) * mm});
            skLineSegment(sketch, "E3159", {"start": v(-64.86, -9.59) * mm, "end": v(-65.15, -8.98) * mm});
            skLineSegment(sketch, "E3160", {"start": v(-65.15, -8.98) * mm, "end": v(-65.51, -8.46) * mm});
            skLineSegment(sketch, "E3161", {"start": v(-65.51, -8.46) * mm, "end": v(-65.97, -8.05) * mm});
            skLineSegment(sketch, "E3162", {"start": v(-65.97, -8.05) * mm, "end": v(-66.48, -7.74) * mm});
            skLineSegment(sketch, "E3163", {"start": v(-66.48, -7.74) * mm, "end": v(-67.08, -7.48) * mm});
            skLineSegment(sketch, "E3164", {"start": v(-67.08, -7.48) * mm, "end": v(-67.76, -7.25) * mm});
            skLineSegment(sketch, "E3165", {"start": v(-67.76, -7.25) * mm, "end": v(-68.52, -7.07) * mm});
            skLineSegment(sketch, "E3166", {"start": v(-68.52, -7.07) * mm, "end": v(-69.36, -6.92) * mm});
            skLineSegment(sketch, "E3167", {"start": v(-69.36, -6.92) * mm, "end": v(-70.3, -6.82) * mm});
            skLineSegment(sketch, "E3168", {"start": v(-70.3, -6.82) * mm, "end": v(-71.3, -6.76) * mm});
            skLineSegment(sketch, "E3169", {"start": v(-71.3, -6.76) * mm, "end": v(-72.39, -6.74) * mm});
            skLineSegment(sketch, "E3170", {"start": v(-72.39, -6.74) * mm, "end": v(-73.04, -6.73) * mm});
            skLineSegment(sketch, "E3171", {"start": v(-73.04, -6.73) * mm, "end": v(-73.68, -6.73) * mm});
            skLineSegment(sketch, "E3172", {"start": v(-73.68, -6.73) * mm, "end": v(-74.33, -6.72) * mm});
            skLineSegment(sketch, "E3173", {"start": v(-74.33, -6.72) * mm, "end": v(-74.98, -6.72) * mm});
            skLineSegment(sketch, "E3174", {"start": v(-74.98, -6.72) * mm, "end": v(-75.63, -6.71) * mm});
            skLineSegment(sketch, "E3175", {"start": v(-75.63, -6.71) * mm, "end": v(-76.28, -6.71) * mm});
            skLineSegment(sketch, "E3176", {"start": v(-76.28, -6.71) * mm, "end": v(-76.93, -6.7) * mm});
            skLineSegment(sketch, "E3177", {"start": v(-76.93, -6.7) * mm, "end": v(-77.58, -6.7) * mm});
            skLineSegment(sketch, "E3178", {"start": v(-77.58, -6.7) * mm, "end": v(-78.34, -6.7) * mm});
            skLineSegment(sketch, "E3179", {"start": v(-78.34, -6.7) * mm, "end": v(-79.1, -6.68) * mm});
            skLineSegment(sketch, "E3180", {"start": v(-79.1, -6.68) * mm, "end": v(-79.85, -6.67) * mm});
            skLineSegment(sketch, "E3181", {"start": v(-79.85, -6.67) * mm, "end": v(-80.6, -6.66) * mm});
            skLineSegment(sketch, "E3182", {"start": v(-80.6, -6.66) * mm, "end": v(-81.37, -6.65) * mm});
            skLineSegment(sketch, "E3183", {"start": v(-81.37, -6.65) * mm, "end": v(-82.13, -6.64) * mm});
            skLineSegment(sketch, "E3184", {"start": v(-82.13, -6.64) * mm, "end": v(-82.88, -6.63) * mm});
            skLineSegment(sketch, "E3185", {"start": v(-82.88, -6.63) * mm, "end": v(-83.64, -6.62) * mm});
            skLineSegment(sketch, "E3186", {"start": v(-83.64, -6.62) * mm, "end": v(-84.14, -6.61) * mm});
            skLineSegment(sketch, "E3187", {"start": v(-84.14, -6.61) * mm, "end": v(-84.6, -6.59) * mm});
            skLineSegment(sketch, "E3188", {"start": v(-84.6, -6.59) * mm, "end": v(-85.05, -6.54) * mm});
            skLineSegment(sketch, "E3189", {"start": v(-85.05, -6.54) * mm, "end": v(-85.47, -6.48) * mm});
            skLineSegment(sketch, "E3190", {"start": v(-85.47, -6.48) * mm, "end": v(-85.87, -6.4) * mm});
            skLineSegment(sketch, "E3191", {"start": v(-85.87, -6.4) * mm, "end": v(-86.24, -6.3) * mm});
            skLineSegment(sketch, "E3192", {"start": v(-86.24, -6.3) * mm, "end": v(-86.6, -6.19) * mm});
            skLineSegment(sketch, "E3193", {"start": v(-86.6, -6.19) * mm, "end": v(-86.93, -6.05) * mm});
            skLineSegment(sketch, "E3194", {"start": v(-86.93, -6.05) * mm, "end": v(-87.2, -5.9) * mm});
            skLineSegment(sketch, "E3195", {"start": v(-87.2, -5.9) * mm, "end": v(-87.51, -5.7) * mm});
            skLineSegment(sketch, "E3196", {"start": v(-87.51, -5.7) * mm, "end": v(-87.82, -5.44) * mm});
            skLineSegment(sketch, "E3197", {"start": v(-87.82, -5.44) * mm, "end": v(-88.11, -5.1) * mm});
            skLineSegment(sketch, "E3198", {"start": v(-88.11, -5.1) * mm, "end": v(-88.38, -4.68) * mm});
            skLineSegment(sketch, "E3199", {"start": v(-88.38, -4.68) * mm, "end": v(-88.59, -4.17) * mm});
            skLineSegment(sketch, "E3200", {"start": v(-88.59, -4.17) * mm, "end": v(-88.73, -3.55) * mm});
            skLineSegment(sketch, "E3201", {"start": v(-88.73, -3.55) * mm, "end": v(-88.78, -2.84) * mm});
            skLineSegment(sketch, "E3202", {"start": v(-88.78, -2.84) * mm, "end": v(-88.75, -2.38) * mm});
            skLineSegment(sketch, "E3203", {"start": v(-88.75, -2.38) * mm, "end": v(-88.68, -1.96) * mm});
            skLineSegment(sketch, "E3204", {"start": v(-88.68, -1.96) * mm, "end": v(-88.55, -1.56) * mm});
            skLineSegment(sketch, "E3205", {"start": v(-88.55, -1.56) * mm, "end": v(-88.37, -1.19) * mm});
            skLineSegment(sketch, "E3206", {"start": v(-88.37, -1.19) * mm, "end": v(-88.14, -0.85) * mm});
            skLineSegment(sketch, "E3207", {"start": v(-88.14, -0.85) * mm, "end": v(-87.86, -0.55) * mm});
            skLineSegment(sketch, "E3208", {"start": v(-87.86, -0.55) * mm, "end": v(-87.54, -0.28) * mm});
            skLineSegment(sketch, "E3209", {"start": v(-87.54, -0.28) * mm, "end": v(-87.17, -0.05) * mm});
            skLineSegment(sketch, "E3210", {"start": v(-87.17, -0.05) * mm, "end": v(-86.88, 0.1) * mm});
            skLineSegment(sketch, "E3211", {"start": v(-86.88, 0.1) * mm, "end": v(-86.57, 0.22) * mm});
            skLineSegment(sketch, "E3212", {"start": v(-86.57, 0.22) * mm, "end": v(-86.25, 0.32) * mm});
            skLineSegment(sketch, "E3213", {"start": v(-86.25, 0.32) * mm, "end": v(-85.92, 0.4) * mm});
            skLineSegment(sketch, "E3214", {"start": v(-85.92, 0.4) * mm, "end": v(-85.58, 0.48) * mm});
            skLineSegment(sketch, "E3215", {"start": v(-85.58, 0.48) * mm, "end": v(-85.22, 0.53) * mm});
            skLineSegment(sketch, "E3216", {"start": v(-85.22, 0.53) * mm, "end": v(-84.85, 0.56) * mm});
            skLineSegment(sketch, "E3217", {"start": v(-84.85, 0.56) * mm, "end": v(-84.48, 0.57) * mm});
            skLineSegment(sketch, "E3218", {"start": v(-84.48, 0.57) * mm, "end": v(-83.73, 0.6) * mm});
            skLineSegment(sketch, "E3219", {"start": v(-83.73, 0.6) * mm, "end": v(-82.98, 0.61) * mm});
            skLineSegment(sketch, "E3220", {"start": v(-82.98, 0.61) * mm, "end": v(-82.24, 0.64) * mm});
            skLineSegment(sketch, "E3221", {"start": v(-82.24, 0.64) * mm, "end": v(-81.49, 0.66) * mm});
            skLineSegment(sketch, "E3222", {"start": v(-81.49, 0.66) * mm, "end": v(-80.74, 0.69) * mm});
            skLineSegment(sketch, "E3223", {"start": v(-80.74, 0.69) * mm, "end": v(-80, 0.71) * mm});
            skLineSegment(sketch, "E3224", {"start": v(-80, 0.71) * mm, "end": v(-79.25, 0.73) * mm});
            skLineSegment(sketch, "E3225", {"start": v(-79.25, 0.73) * mm, "end": v(-78.5, 0.76) * mm});
            skLineSegment(sketch, "E3226", {"start": v(-78.5, 0.76) * mm, "end": v(-78.5, 0.76) * mm});
            skLineSegment(sketch, "E3227", {"start": v(-78.5, 0.76) * mm, "end": v(-78.49, 0.76) * mm});
            skLineSegment(sketch, "E3228", {"start": v(-78.49, 0.76) * mm, "end": v(-78.48, 0.76) * mm});
            skLineSegment(sketch, "E3229", {"start": v(-78.48, 0.76) * mm, "end": v(-78.47, 0.76) * mm});
            skLineSegment(sketch, "E3230", {"start": v(-78.47, 0.76) * mm, "end": v(-78.46, 0.76) * mm});
            skLineSegment(sketch, "E3231", {"start": v(-78.46, 0.76) * mm, "end": v(-78.46, 0.76) * mm});
            skLineSegment(sketch, "E3232", {"start": v(-78.46, 0.76) * mm, "end": v(-78.45, 0.76) * mm});
            skLineSegment(sketch, "E3233", {"start": v(-78.45, 0.76) * mm, "end": v(-78.44, 0.76) * mm});
            skLineSegment(sketch, "E3234", {"start": v(-78.44, 0.76) * mm, "end": v(-77.97, 0.75) * mm});
            skLineSegment(sketch, "E3235", {"start": v(-77.97, 0.75) * mm, "end": v(-77.5, 0.75) * mm});
            skLineSegment(sketch, "E3236", {"start": v(-77.5, 0.75) * mm, "end": v(-77.02, 0.75) * mm});
            skLineSegment(sketch, "E3237", {"start": v(-77.02, 0.75) * mm, "end": v(-76.55, 0.74) * mm});
            skLineSegment(sketch, "E3238", {"start": v(-76.55, 0.74) * mm, "end": v(-76.07, 0.74) * mm});
            skLineSegment(sketch, "E3239", {"start": v(-76.07, 0.74) * mm, "end": v(-75.6, 0.73) * mm});
            skLineSegment(sketch, "E3240", {"start": v(-75.6, 0.73) * mm, "end": v(-75.13, 0.73) * mm});
            skLineSegment(sketch, "E3241", {"start": v(-75.13, 0.73) * mm, "end": v(-74.65, 0.72) * mm});
            skLineSegment(sketch, "E3242", {"start": v(-74.65, 0.72) * mm, "end": v(-73.06, 0.68) * mm});
            skLineSegment(sketch, "E3243", {"start": v(-73.06, 0.68) * mm, "end": v(-71.6, 0.56) * mm});
            skLineSegment(sketch, "E3244", {"start": v(-71.6, 0.56) * mm, "end": v(-70.29, 0.38) * mm});
            skLineSegment(sketch, "E3245", {"start": v(-70.29, 0.38) * mm, "end": v(-69.1, 0.13) * mm});
            skLineSegment(sketch, "E3246", {"start": v(-69.1, 0.13) * mm, "end": v(-68.04, -0.16) * mm});
            skLineSegment(sketch, "E3247", {"start": v(-68.04, -0.16) * mm, "end": v(-67.1, -0.5) * mm});
            skLineSegment(sketch, "E3248", {"start": v(-67.1, -0.5) * mm, "end": v(-66.26, -0.86) * mm});
            skLineSegment(sketch, "E3249", {"start": v(-66.26, -0.86) * mm, "end": v(-65.54, -1.25) * mm});
            skLineSegment(sketch, "E3250", {"start": v(-65.54, -1.25) * mm, "end": v(-65.55, -1.1) * mm});
            skLineSegment(sketch, "E3251", {"start": v(-65.55, -1.1) * mm, "end": v(-65.56, -0.97) * mm});
            skLineSegment(sketch, "E3252", {"start": v(-65.56, -0.97) * mm, "end": v(-65.57, -0.84) * mm});
            skLineSegment(sketch, "E3253", {"start": v(-65.57, -0.84) * mm, "end": v(-65.58, -0.72) * mm});
            skLineSegment(sketch, "E3254", {"start": v(-65.58, -0.72) * mm, "end": v(-65.6, -0.62) * mm});
            skLineSegment(sketch, "E3255", {"start": v(-65.6, -0.62) * mm, "end": v(-65.6, -0.53) * mm});
            skLineSegment(sketch, "E3256", {"start": v(-65.6, -0.53) * mm, "end": v(-65.61, -0.45) * mm});
            skLineSegment(sketch, "E3257", {"start": v(-65.61, -0.45) * mm, "end": v(-65.62, -0.38) * mm});
            skLineSegment(sketch, "E3258", {"start": v(-65.62, -0.38) * mm, "end": v(-65.68, -0.16) * mm});
            skLineSegment(sketch, "E3259", {"start": v(-65.68, -0.16) * mm, "end": v(-65.75, 0.07) * mm});
            skLineSegment(sketch, "E3260", {"start": v(-65.75, 0.07) * mm, "end": v(-65.83, 0.31) * mm});
            skLineSegment(sketch, "E3261", {"start": v(-65.83, 0.31) * mm, "end": v(-65.94, 0.57) * mm});
            skLineSegment(sketch, "E3262", {"start": v(-65.94, 0.57) * mm, "end": v(-66.06, 0.83) * mm});
            skLineSegment(sketch, "E3263", {"start": v(-66.06, 0.83) * mm, "end": v(-66.2, 1.1) * mm});
            skLineSegment(sketch, "E3264", {"start": v(-66.2, 1.1) * mm, "end": v(-66.34, 1.38) * mm});
            skLineSegment(sketch, "E3265", {"start": v(-66.34, 1.38) * mm, "end": v(-66.51, 1.67) * mm});
            skLineSegment(sketch, "E3266", {"start": v(-66.51, 1.67) * mm, "end": v(-66.66, 1.88) * mm});
            skLineSegment(sketch, "E3267", {"start": v(-66.66, 1.88) * mm, "end": v(-66.83, 2.08) * mm});
            skLineSegment(sketch, "E3268", {"start": v(-66.83, 2.08) * mm, "end": v(-67.03, 2.26) * mm});
            skLineSegment(sketch, "E3269", {"start": v(-67.03, 2.26) * mm, "end": v(-67.26, 2.42) * mm});
            skLineSegment(sketch, "E3270", {"start": v(-67.26, 2.42) * mm, "end": v(-67.52, 2.57) * mm});
            skLineSegment(sketch, "E3271", {"start": v(-67.52, 2.57) * mm, "end": v(-67.8, 2.7) * mm});
            skLineSegment(sketch, "E3272", {"start": v(-67.8, 2.7) * mm, "end": v(-68.12, 2.82) * mm});
            skLineSegment(sketch, "E3273", {"start": v(-68.12, 2.82) * mm, "end": v(-68.46, 2.92) * mm});
            skLineSegment(sketch, "E3274", {"start": v(-68.46, 2.92) * mm, "end": v(-68.94, 3.03) * mm});
            skLineSegment(sketch, "E3275", {"start": v(-68.94, 3.03) * mm, "end": v(-69.46, 3.13) * mm});
            skLineSegment(sketch, "E3276", {"start": v(-69.46, 3.13) * mm, "end": v(-70.02, 3.2) * mm});
            skLineSegment(sketch, "E3277", {"start": v(-70.02, 3.2) * mm, "end": v(-70.62, 3.28) * mm});
            skLineSegment(sketch, "E3278", {"start": v(-70.62, 3.28) * mm, "end": v(-71.25, 3.33) * mm});
            skLineSegment(sketch, "E3279", {"start": v(-71.25, 3.33) * mm, "end": v(-71.93, 3.36) * mm});
            skLineSegment(sketch, "E3280", {"start": v(-71.93, 3.36) * mm, "end": v(-72.64, 3.39) * mm});
            skLineSegment(sketch, "E3281", {"start": v(-72.64, 3.39) * mm, "end": v(-73.4, 3.4) * mm});
            skLineSegment(sketch, "E3282", {"start": v(-73.4, 3.4) * mm, "end": v(-74.08, 3.4) * mm});
            skLineSegment(sketch, "E3283", {"start": v(-74.08, 3.4) * mm, "end": v(-74.77, 3.41) * mm});
            skLineSegment(sketch, "E3284", {"start": v(-74.77, 3.41) * mm, "end": v(-75.46, 3.42) * mm});
            skLineSegment(sketch, "E3285", {"start": v(-75.46, 3.42) * mm, "end": v(-76.15, 3.43) * mm});
            skLineSegment(sketch, "E3286", {"start": v(-76.15, 3.43) * mm, "end": v(-76.84, 3.44) * mm});
            skLineSegment(sketch, "E3287", {"start": v(-76.84, 3.44) * mm, "end": v(-77.52, 3.45) * mm});
            skLineSegment(sketch, "E3288", {"start": v(-77.52, 3.45) * mm, "end": v(-78.21, 3.46) * mm});
            skLineSegment(sketch, "E3289", {"start": v(-78.21, 3.46) * mm, "end": v(-78.9, 3.47) * mm});
            skLineSegment(sketch, "E3290", {"start": v(-78.9, 3.47) * mm, "end": v(-79.29, 3.47) * mm});
            skLineSegment(sketch, "E3291", {"start": v(-79.29, 3.47) * mm, "end": v(-79.76, 3.46) * mm});
            skLineSegment(sketch, "E3292", {"start": v(-79.76, 3.46) * mm, "end": v(-80.32, 3.45) * mm});
            skLineSegment(sketch, "E3293", {"start": v(-80.32, 3.45) * mm, "end": v(-80.96, 3.44) * mm});
            skLineSegment(sketch, "E3294", {"start": v(-80.96, 3.44) * mm, "end": v(-81.68, 3.42) * mm});
            skLineSegment(sketch, "E3295", {"start": v(-81.68, 3.42) * mm, "end": v(-82.47, 3.4) * mm});
            skLineSegment(sketch, "E3296", {"start": v(-82.47, 3.4) * mm, "end": v(-83.34, 3.38) * mm});
            skLineSegment(sketch, "E3297", {"start": v(-83.34, 3.38) * mm, "end": v(-84.27, 3.35) * mm});
            skLineSegment(sketch, "E3298", {"start": v(-84.27, 3.35) * mm, "end": v(-85.22, 3.32) * mm});
            skLineSegment(sketch, "E3299", {"start": v(-85.22, 3.32) * mm, "end": v(-86.11, 3.27) * mm});
            skLineSegment(sketch, "E3300", {"start": v(-86.11, 3.27) * mm, "end": v(-86.96, 3.2) * mm});
            skLineSegment(sketch, "E3301", {"start": v(-86.96, 3.2) * mm, "end": v(-87.76, 3.12) * mm});
            skLineSegment(sketch, "E3302", {"start": v(-87.76, 3.12) * mm, "end": v(-88.52, 3.03) * mm});
            skLineSegment(sketch, "E3303", {"start": v(-88.52, 3.03) * mm, "end": v(-89.22, 2.92) * mm});
            skLineSegment(sketch, "E3304", {"start": v(-89.22, 2.92) * mm, "end": v(-89.88, 2.79) * mm});
            skLineSegment(sketch, "E3305", {"start": v(-89.88, 2.79) * mm, "end": v(-90.49, 2.65) * mm});
            skLineSegment(sketch, "E3306", {"start": v(-90.49, 2.65) * mm, "end": v(-90.94, 2.52) * mm});
            skLineSegment(sketch, "E3307", {"start": v(-90.94, 2.52) * mm, "end": v(-91.35, 2.36) * mm});
            skLineSegment(sketch, "E3308", {"start": v(-91.35, 2.36) * mm, "end": v(-91.72, 2.19) * mm});
            skLineSegment(sketch, "E3309", {"start": v(-91.72, 2.19) * mm, "end": v(-92.05, 1.99) * mm});
            skLineSegment(sketch, "E3310", {"start": v(-92.05, 1.99) * mm, "end": v(-92.34, 1.77) * mm});
            skLineSegment(sketch, "E3311", {"start": v(-92.34, 1.77) * mm, "end": v(-92.6, 1.52) * mm});
            skLineSegment(sketch, "E3312", {"start": v(-92.6, 1.52) * mm, "end": v(-92.82, 1.25) * mm});
            skLineSegment(sketch, "E3313", {"start": v(-92.82, 1.25) * mm, "end": v(-93, 0.96) * mm});
            skLineSegment(sketch, "E3314", {"start": v(-93, 0.96) * mm, "end": v(-93.18, 0.58) * mm});
            skLineSegment(sketch, "E3315", {"start": v(-93.18, 0.58) * mm, "end": v(-93.34, 0.15) * mm});
            skLineSegment(sketch, "E3316", {"start": v(-93.34, 0.15) * mm, "end": v(-93.47, -0.33) * mm});
            skLineSegment(sketch, "E3317", {"start": v(-93.47, -0.33) * mm, "end": v(-93.58, -0.84) * mm});
            skLineSegment(sketch, "E3318", {"start": v(-93.58, -0.84) * mm, "end": v(-93.66, -1.4) * mm});
            skLineSegment(sketch, "E3319", {"start": v(-93.66, -1.4) * mm, "end": v(-93.72, -2) * mm});
            skLineSegment(sketch, "E3320", {"start": v(-93.72, -2) * mm, "end": v(-93.76, -2.65) * mm});
            skLineSegment(sketch, "E3321", {"start": v(-93.76, -2.65) * mm, "end": v(-93.77, -3.34) * mm});
            skLineSegment(sketch, "E3322", {"start": v(-93.77, -3.34) * mm, "end": v(-93.75, -4.12) * mm});
            skLineSegment(sketch, "E3323", {"start": v(-93.75, -4.12) * mm, "end": v(-93.7, -4.85) * mm});
            skLineSegment(sketch, "E3324", {"start": v(-93.7, -4.85) * mm, "end": v(-93.6, -5.53) * mm});
            skLineSegment(sketch, "E3325", {"start": v(-93.6, -5.53) * mm, "end": v(-93.48, -6.15) * mm});
            skLineSegment(sketch, "E3326", {"start": v(-93.48, -6.15) * mm, "end": v(-93.32, -6.7) * mm});
            skLineSegment(sketch, "E3327", {"start": v(-93.32, -6.7) * mm, "end": v(-93.12, -7.2) * mm});
            skLineSegment(sketch, "E3328", {"start": v(-93.12, -7.2) * mm, "end": v(-92.88, -7.65) * mm});
            skLineSegment(sketch, "E3329", {"start": v(-92.88, -7.65) * mm, "end": v(-92.61, -8.04) * mm});
            skLineSegment(sketch, "E3330", {"start": v(-92.61, -8.04) * mm, "end": v(-92.32, -8.34) * mm});
            skLineSegment(sketch, "E3331", {"start": v(-92.32, -8.34) * mm, "end": v(-91.97, -8.6) * mm});
            skLineSegment(sketch, "E3332", {"start": v(-91.97, -8.6) * mm, "end": v(-91.56, -8.83) * mm});
            skLineSegment(sketch, "E3333", {"start": v(-91.56, -8.83) * mm, "end": v(-91.1, -9) * mm});
            skLineSegment(sketch, "E3334", {"start": v(-91.1, -9) * mm, "end": v(-90.56, -9.15) * mm});
            skLineSegment(sketch, "E3335", {"start": v(-90.56, -9.15) * mm, "end": v(-89.98, -9.25) * mm});
            skLineSegment(sketch, "E3336", {"start": v(-89.98, -9.25) * mm, "end": v(-89.33, -9.31) * mm});
            skLineSegment(sketch, "E3337", {"start": v(-89.33, -9.31) * mm, "end": v(-88.63, -9.33) * mm});
            skLineSegment(sketch, "E3338", {"start": v(-88.63, -9.33) * mm, "end": v(-87.01, -9.37) * mm});
            skLineSegment(sketch, "E3339", {"start": v(-87.01, -9.37) * mm, "end": v(-85.4, -9.4) * mm});
            skLineSegment(sketch, "E3340", {"start": v(-85.4, -9.4) * mm, "end": v(-83.77, -9.43) * mm});
            skLineSegment(sketch, "E3341", {"start": v(-83.77, -9.43) * mm, "end": v(-82.16, -9.47) * mm});
            skLineSegment(sketch, "E3342", {"start": v(-82.16, -9.47) * mm, "end": v(-80.54, -9.5) * mm});
            skLineSegment(sketch, "E3343", {"start": v(-80.54, -9.5) * mm, "end": v(-78.92, -9.54) * mm});
            skLineSegment(sketch, "E3344", {"start": v(-78.92, -9.54) * mm, "end": v(-77.3, -9.57) * mm});
            skLineSegment(sketch, "E3345", {"start": v(-77.3, -9.57) * mm, "end": v(-75.68, -9.6) * mm});
            skLineSegment(sketch, "E3346", {"start": v(-75.68, -9.6) * mm, "end": v(-75.53, -9.6) * mm});
            skLineSegment(sketch, "E3347", {"start": v(-75.53, -9.6) * mm, "end": v(-75.37, -9.6) * mm});
            skLineSegment(sketch, "E3348", {"start": v(-75.37, -9.6) * mm, "end": v(-75.21, -9.6) * mm});
            skLineSegment(sketch, "E3349", {"start": v(-75.21, -9.6) * mm, "end": v(-75.06, -9.6) * mm});
            skLineSegment(sketch, "E3350", {"start": v(-75.06, -9.6) * mm, "end": v(-74.9, -9.6) * mm});
            skLineSegment(sketch, "E3351", {"start": v(-74.9, -9.6) * mm, "end": v(-74.75, -9.6) * mm});
            skLineSegment(sketch, "E3352", {"start": v(-74.75, -9.6) * mm, "end": v(-74.6, -9.6) * mm});
            skLineSegment(sketch, "E3353", {"start": v(-74.6, -9.6) * mm, "end": v(-74.43, -9.6) * mm});
            skLineSegment(sketch, "E3354", {"start": v(-74.43, -9.6) * mm, "end": v(-73.78, -9.62) * mm});
            skLineSegment(sketch, "E3355", {"start": v(-73.78, -9.62) * mm, "end": v(-73.19, -9.66) * mm});
            skLineSegment(sketch, "E3356", {"start": v(-73.19, -9.66) * mm, "end": v(-72.64, -9.73) * mm});
            skLineSegment(sketch, "E3357", {"start": v(-72.64, -9.73) * mm, "end": v(-72.15, -9.84) * mm});
            skLineSegment(sketch, "E3358", {"start": v(-72.15, -9.84) * mm, "end": v(-71.7, -9.97) * mm});
            skLineSegment(sketch, "E3359", {"start": v(-71.7, -9.97) * mm, "end": v(-71.3, -10.14) * mm});
            skLineSegment(sketch, "E3360", {"start": v(-71.3, -10.14) * mm, "end": v(-70.94, -10.33) * mm});
            skLineSegment(sketch, "E3361", {"start": v(-70.94, -10.33) * mm, "end": v(-70.62, -10.56) * mm});
            skLineSegment(sketch, "E3362", {"start": v(-70.62, -10.56) * mm, "end": v(-70.32, -10.83) * mm});
            skLineSegment(sketch, "E3363", {"start": v(-70.32, -10.83) * mm, "end": v(-70.06, -11.13) * mm});
            skLineSegment(sketch, "E3364", {"start": v(-70.06, -11.13) * mm, "end": v(-69.84, -11.45) * mm});
            skLineSegment(sketch, "E3365", {"start": v(-69.84, -11.45) * mm, "end": v(-69.66, -11.79) * mm});
            skLineSegment(sketch, "E3366", {"start": v(-69.66, -11.79) * mm, "end": v(-69.52, -12.15) * mm});
            skLineSegment(sketch, "E3367", {"start": v(-69.52, -12.15) * mm, "end": v(-69.42, -12.53) * mm});
            skLineSegment(sketch, "E3368", {"start": v(-69.42, -12.53) * mm, "end": v(-69.35, -12.93) * mm});
            skLineSegment(sketch, "E3369", {"start": v(-69.35, -12.93) * mm, "end": v(-69.33, -13.35) * mm});
            skLineSegment(sketch, "E3370", {"start": v(-69.33, -13.35) * mm, "end": v(-69.36, -13.9) * mm});
            skLineSegment(sketch, "E3371", {"start": v(-69.36, -13.9) * mm, "end": v(-69.44, -14.38) * mm});
            skLineSegment(sketch, "E3372", {"start": v(-69.44, -14.38) * mm, "end": v(-69.57, -14.8) * mm});
            skLineSegment(sketch, "E3373", {"start": v(-69.57, -14.8) * mm, "end": v(-69.72, -15.18) * mm});
            skLineSegment(sketch, "E3374", {"start": v(-69.72, -15.18) * mm, "end": v(-69.9, -15.5) * mm});
            skLineSegment(sketch, "E3375", {"start": v(-69.9, -15.5) * mm, "end": v(-70.1, -15.77) * mm});
            skLineSegment(sketch, "E3376", {"start": v(-70.1, -15.77) * mm, "end": v(-70.32, -16) * mm});
            skLineSegment(sketch, "E3377", {"start": v(-70.32, -16) * mm, "end": v(-70.52, -16.19) * mm});
            skLineSegment(sketch, "E3378", {"start": v(-70.52, -16.19) * mm, "end": v(-70.82, -16.4) * mm});
            skLineSegment(sketch, "E3379", {"start": v(-70.82, -16.4) * mm, "end": v(-71.15, -16.58) * mm});
            skLineSegment(sketch, "E3380", {"start": v(-71.15, -16.58) * mm, "end": v(-71.54, -16.73) * mm});
            skLineSegment(sketch, "E3381", {"start": v(-71.54, -16.73) * mm, "end": v(-71.97, -16.85) * mm});
            skLineSegment(sketch, "E3382", {"start": v(-71.97, -16.85) * mm, "end": v(-72.46, -16.94) * mm});
            skLineSegment(sketch, "E3383", {"start": v(-72.46, -16.94) * mm, "end": v(-73, -17.01) * mm});
            skLineSegment(sketch, "E3384", {"start": v(-73, -17.01) * mm, "end": v(-73.6, -17.05) * mm});
            skLineSegment(sketch, "E3385", {"start": v(-73.6, -17.05) * mm, "end": v(-74.26, -17.06) * mm});
            skLineSegment(sketch, "E3386", {"start": v(-74.26, -17.06) * mm, "end": v(-74.91, -17.08) * mm});
            skLineSegment(sketch, "E3387", {"start": v(-74.91, -17.08) * mm, "end": v(-75.57, -17.1) * mm});
            skLineSegment(sketch, "E3388", {"start": v(-75.57, -17.1) * mm, "end": v(-76.22, -17.12) * mm});
            skLineSegment(sketch, "E3389", {"start": v(-76.22, -17.12) * mm, "end": v(-76.88, -17.14) * mm});
            skLineSegment(sketch, "E3390", {"start": v(-76.88, -17.14) * mm, "end": v(-77.53, -17.16) * mm});
            skLineSegment(sketch, "E3391", {"start": v(-77.53, -17.16) * mm, "end": v(-78.19, -17.18) * mm});
            skLineSegment(sketch, "E3392", {"start": v(-78.19, -17.18) * mm, "end": v(-78.84, -17.2) * mm});
            skLineSegment(sketch, "E3393", {"start": v(-78.84, -17.2) * mm, "end": v(-79.5, -17.22) * mm});
            skLineSegment(sketch, "E3394", {"start": v(-79.5, -17.22) * mm, "end": v(-79.5, -17.22) * mm});
            skLineSegment(sketch, "E3395", {"start": v(-79.5, -17.22) * mm, "end": v(-79.51, -17.22) * mm});
            skLineSegment(sketch, "E3396", {"start": v(-79.51, -17.22) * mm, "end": v(-79.52, -17.22) * mm});
            skLineSegment(sketch, "E3397", {"start": v(-79.52, -17.22) * mm, "end": v(-79.53, -17.22) * mm});
            skLineSegment(sketch, "E3398", {"start": v(-79.53, -17.22) * mm, "end": v(-79.53, -17.22) * mm});
            skLineSegment(sketch, "E3399", {"start": v(-79.53, -17.22) * mm, "end": v(-79.54, -17.22) * mm});
            skLineSegment(sketch, "E3400", {"start": v(-79.54, -17.22) * mm, "end": v(-79.55, -17.22) * mm});
            skLineSegment(sketch, "E3401", {"start": v(-79.55, -17.22) * mm, "end": v(-79.55, -17.22) * mm});
            skLineSegment(sketch, "E3402", {"start": v(-79.55, -17.22) * mm, "end": v(-80.02, -17.21) * mm});
            skLineSegment(sketch, "E3403", {"start": v(-80.02, -17.21) * mm, "end": v(-80.48, -17.2) * mm});
            skLineSegment(sketch, "E3404", {"start": v(-80.48, -17.2) * mm, "end": v(-80.95, -17.2) * mm});
            skLineSegment(sketch, "E3405", {"start": v(-80.95, -17.2) * mm, "end": v(-81.41, -17.2) * mm});
            skLineSegment(sketch, "E3406", {"start": v(-81.41, -17.2) * mm, "end": v(-81.88, -17.2) * mm});
            skLineSegment(sketch, "E3407", {"start": v(-81.88, -17.2) * mm, "end": v(-82.34, -17.19) * mm});
            skLineSegment(sketch, "E3408", {"start": v(-82.34, -17.19) * mm, "end": v(-82.8, -17.19) * mm});
            skLineSegment(sketch, "E3409", {"start": v(-82.8, -17.19) * mm, "end": v(-83.27, -17.18) * mm});
            skLineSegment(sketch, "E3410", {"start": v(-83.27, -17.18) * mm, "end": v(-85.11, -17.14) * mm});
            skLineSegment(sketch, "E3411", {"start": v(-85.11, -17.14) * mm, "end": v(-86.79, -17) * mm});
            skLineSegment(sketch, "E3412", {"start": v(-86.79, -17) * mm, "end": v(-88.29, -16.8) * mm});
            skLineSegment(sketch, "E3413", {"start": v(-88.29, -16.8) * mm, "end": v(-89.63, -16.55) * mm});
            skLineSegment(sketch, "E3414", {"start": v(-89.63, -16.55) * mm, "end": v(-90.82, -16.24) * mm});
            skLineSegment(sketch, "E3415", {"start": v(-90.82, -16.24) * mm, "end": v(-91.87, -15.88) * mm});
            skLineSegment(sketch, "E3416", {"start": v(-91.87, -15.88) * mm, "end": v(-92.78, -15.5) * mm});
            skLineSegment(sketch, "E3417", {"start": v(-92.78, -15.5) * mm, "end": v(-93.57, -15.1) * mm});
            skLineSegment(sketch, "E3418", {"start": v(-66.38, -3.64) * mm, "end": v(-66.73, -3.46) * mm});
            skLineSegment(sketch, "E3419", {"start": v(-66.73, -3.46) * mm, "end": v(-67.23, -3.25) * mm});
            skLineSegment(sketch, "E3420", {"start": v(-67.23, -3.25) * mm, "end": v(-67.9, -3.02) * mm});
            skLineSegment(sketch, "E3421", {"start": v(-67.9, -3.02) * mm, "end": v(-68.77, -2.78) * mm});
            skLineSegment(sketch, "E3422", {"start": v(-68.77, -2.78) * mm, "end": v(-69.85, -2.56) * mm});
            skLineSegment(sketch, "E3423", {"start": v(-69.85, -2.56) * mm, "end": v(-71.18, -2.38) * mm});
            skLineSegment(sketch, "E3424", {"start": v(-71.18, -2.38) * mm, "end": v(-72.78, -2.26) * mm});
            skLineSegment(sketch, "E3425", {"start": v(-72.78, -2.26) * mm, "end": v(-74.67, -2.21) * mm});
            skLineSegment(sketch, "E3426", {"start": v(-74.67, -2.21) * mm, "end": v(-75.14, -2.2) * mm});
            skLineSegment(sketch, "E3427", {"start": v(-75.14, -2.2) * mm, "end": v(-75.61, -2.2) * mm});
            skLineSegment(sketch, "E3428", {"start": v(-75.61, -2.2) * mm, "end": v(-76.08, -2.2) * mm});
            skLineSegment(sketch, "E3429", {"start": v(-76.08, -2.2) * mm, "end": v(-76.55, -2.2) * mm});
            skLineSegment(sketch, "E3430", {"start": v(-76.55, -2.2) * mm, "end": v(-77.03, -2.19) * mm});
            skLineSegment(sketch, "E3431", {"start": v(-77.03, -2.19) * mm, "end": v(-77.5, -2.18) * mm});
            skLineSegment(sketch, "E3432", {"start": v(-77.5, -2.18) * mm, "end": v(-77.97, -2.18) * mm});
            skLineSegment(sketch, "E3433", {"start": v(-77.97, -2.18) * mm, "end": v(-78.44, -2.18) * mm});
            skLineSegment(sketch, "E3434", {"start": v(-78.44, -2.18) * mm, "end": v(-79.19, -2.2) * mm});
            skLineSegment(sketch, "E3435", {"start": v(-79.19, -2.2) * mm, "end": v(-79.93, -2.22) * mm});
            skLineSegment(sketch, "E3436", {"start": v(-79.93, -2.22) * mm, "end": v(-80.68, -2.25) * mm});
            skLineSegment(sketch, "E3437", {"start": v(-80.68, -2.25) * mm, "end": v(-81.42, -2.27) * mm});
            skLineSegment(sketch, "E3438", {"start": v(-81.42, -2.27) * mm, "end": v(-82.17, -2.3) * mm});
            skLineSegment(sketch, "E3439", {"start": v(-82.17, -2.3) * mm, "end": v(-82.91, -2.32) * mm});
            skLineSegment(sketch, "E3440", {"start": v(-82.91, -2.32) * mm, "end": v(-83.66, -2.34) * mm});
            skLineSegment(sketch, "E3441", {"start": v(-83.66, -2.34) * mm, "end": v(-84.4, -2.37) * mm});
            skLineSegment(sketch, "E3442", {"start": v(-84.4, -2.37) * mm, "end": v(-84.41, -2.37) * mm});
            skLineSegment(sketch, "E3443", {"start": v(-84.41, -2.37) * mm, "end": v(-84.42, -2.37) * mm});
            skLineSegment(sketch, "E3444", {"start": v(-84.42, -2.37) * mm, "end": v(-84.42, -2.37) * mm});
            skLineSegment(sketch, "E3445", {"start": v(-84.42, -2.37) * mm, "end": v(-84.43, -2.37) * mm});
            skLineSegment(sketch, "E3446", {"start": v(-84.43, -2.37) * mm, "end": v(-84.43, -2.37) * mm});
            skLineSegment(sketch, "E3447", {"start": v(-84.43, -2.37) * mm, "end": v(-84.44, -2.37) * mm});
            skLineSegment(sketch, "E3448", {"start": v(-84.44, -2.37) * mm, "end": v(-84.45, -2.37) * mm});
            skLineSegment(sketch, "E3449", {"start": v(-84.45, -2.37) * mm, "end": v(-84.45, -2.37) * mm});
            skLineSegment(sketch, "E3450", {"start": v(-84.45, -2.37) * mm, "end": v(-84.67, -2.37) * mm});
            skLineSegment(sketch, "E3451", {"start": v(-84.67, -2.37) * mm, "end": v(-84.9, -2.39) * mm});
            skLineSegment(sketch, "E3452", {"start": v(-84.9, -2.39) * mm, "end": v(-85.13, -2.42) * mm});
            skLineSegment(sketch, "E3453", {"start": v(-85.13, -2.42) * mm, "end": v(-85.35, -2.48) * mm});
            skLineSegment(sketch, "E3454", {"start": v(-85.35, -2.48) * mm, "end": v(-85.55, -2.56) * mm});
            skLineSegment(sketch, "E3455", {"start": v(-85.55, -2.56) * mm, "end": v(-85.7, -2.67) * mm});
            skLineSegment(sketch, "E3456", {"start": v(-85.7, -2.67) * mm, "end": v(-85.8, -2.81) * mm});
            skLineSegment(sketch, "E3457", {"start": v(-85.8, -2.81) * mm, "end": v(-85.84, -3) * mm});
            skLineSegment(sketch, "E3458", {"start": v(-85.84, -3) * mm, "end": v(-85.8, -3.2) * mm});
            skLineSegment(sketch, "E3459", {"start": v(-85.8, -3.2) * mm, "end": v(-85.66, -3.37) * mm});
            skLineSegment(sketch, "E3460", {"start": v(-85.66, -3.37) * mm, "end": v(-85.45, -3.5) * mm});
            skLineSegment(sketch, "E3461", {"start": v(-85.45, -3.5) * mm, "end": v(-85.17, -3.58) * mm});
            skLineSegment(sketch, "E3462", {"start": v(-85.17, -3.58) * mm, "end": v(-84.84, -3.63) * mm});
            skLineSegment(sketch, "E3463", {"start": v(-84.84, -3.63) * mm, "end": v(-84.47, -3.67) * mm});
            skLineSegment(sketch, "E3464", {"start": v(-84.47, -3.67) * mm, "end": v(-84.06, -3.68) * mm});
            skLineSegment(sketch, "E3465", {"start": v(-84.06, -3.68) * mm, "end": v(-83.64, -3.69) * mm});
            skLineSegment(sketch, "E3466", {"start": v(-83.64, -3.69) * mm, "end": v(-83.54, -3.69) * mm});
            skLineSegment(sketch, "E3467", {"start": v(-83.54, -3.69) * mm, "end": v(-83.44, -3.69) * mm});
            skLineSegment(sketch, "E3468", {"start": v(-83.44, -3.69) * mm, "end": v(-83.34, -3.69) * mm});
            skLineSegment(sketch, "E3469", {"start": v(-83.34, -3.69) * mm, "end": v(-83.23, -3.69) * mm});
            skLineSegment(sketch, "E3470", {"start": v(-83.23, -3.69) * mm, "end": v(-83.13, -3.69) * mm});
            skLineSegment(sketch, "E3471", {"start": v(-83.13, -3.69) * mm, "end": v(-83.03, -3.69) * mm});
            skLineSegment(sketch, "E3472", {"start": v(-83.03, -3.69) * mm, "end": v(-82.93, -3.69) * mm});
            skLineSegment(sketch, "E3473", {"start": v(-82.93, -3.69) * mm, "end": v(-82.83, -3.69) * mm});
            skLineSegment(sketch, "E3474", {"start": v(-82.83, -3.69) * mm, "end": v(-82.17, -3.7) * mm});
            skLineSegment(sketch, "E3475", {"start": v(-82.17, -3.7) * mm, "end": v(-81.5, -3.7) * mm});
            skLineSegment(sketch, "E3476", {"start": v(-81.5, -3.7) * mm, "end": v(-80.85, -3.72) * mm});
            skLineSegment(sketch, "E3477", {"start": v(-80.85, -3.72) * mm, "end": v(-80.19, -3.73) * mm});
            skLineSegment(sketch, "E3478", {"start": v(-80.19, -3.73) * mm, "end": v(-79.53, -3.74) * mm});
            skLineSegment(sketch, "E3479", {"start": v(-79.53, -3.74) * mm, "end": v(-78.87, -3.75) * mm});
            skLineSegment(sketch, "E3480", {"start": v(-78.87, -3.75) * mm, "end": v(-78.2, -3.76) * mm});
            skLineSegment(sketch, "E3481", {"start": v(-78.2, -3.76) * mm, "end": v(-77.54, -3.77) * mm});
            skLineSegment(sketch, "E3482", {"start": v(-77.54, -3.77) * mm, "end": v(-76.9, -3.77) * mm});
            skLineSegment(sketch, "E3483", {"start": v(-76.9, -3.77) * mm, "end": v(-76.25, -3.78) * mm});
            skLineSegment(sketch, "E3484", {"start": v(-76.25, -3.78) * mm, "end": v(-75.6, -3.78) * mm});
            skLineSegment(sketch, "E3485", {"start": v(-75.6, -3.78) * mm, "end": v(-74.96, -3.79) * mm});
            skLineSegment(sketch, "E3486", {"start": v(-74.96, -3.79) * mm, "end": v(-74.31, -3.8) * mm});
            skLineSegment(sketch, "E3487", {"start": v(-74.31, -3.8) * mm, "end": v(-73.67, -3.8) * mm});
            skLineSegment(sketch, "E3488", {"start": v(-73.67, -3.8) * mm, "end": v(-73.02, -3.8) * mm});
            skLineSegment(sketch, "E3489", {"start": v(-73.02, -3.8) * mm, "end": v(-72.38, -3.8) * mm});
            skLineSegment(sketch, "E3490", {"start": v(-72.38, -3.8) * mm, "end": v(-71.39, -3.82) * mm});
            skLineSegment(sketch, "E3491", {"start": v(-71.39, -3.82) * mm, "end": v(-70.45, -3.88) * mm});
            skLineSegment(sketch, "E3492", {"start": v(-70.45, -3.88) * mm, "end": v(-69.56, -3.96) * mm});
            skLineSegment(sketch, "E3493", {"start": v(-69.56, -3.96) * mm, "end": v(-68.72, -4.09) * mm});
            skLineSegment(sketch, "E3494", {"start": v(-68.72, -4.09) * mm, "end": v(-67.94, -4.24) * mm});
            skLineSegment(sketch, "E3495", {"start": v(-67.94, -4.24) * mm, "end": v(-67.2, -4.42) * mm});
            skLineSegment(sketch, "E3496", {"start": v(-67.2, -4.42) * mm, "end": v(-66.5, -4.63) * mm});
            skLineSegment(sketch, "E3497", {"start": v(-66.5, -4.63) * mm, "end": v(-65.86, -4.87) * mm});
            skLineSegment(sketch, "E3498", {"start": v(-65.86, -4.87) * mm, "end": v(-65.78, -4.91) * mm});
            skLineSegment(sketch, "E3499", {"start": v(-65.78, -4.91) * mm, "end": v(-65.58, -5.03) * mm});
            skLineSegment(sketch, "E3500", {"start": v(-65.58, -5.03) * mm, "end": v(-65.28, -5.2) * mm});
            skLineSegment(sketch, "E3501", {"start": v(-65.28, -5.2) * mm, "end": v(-64.91, -5.42) * mm});
            skLineSegment(sketch, "E3502", {"start": v(-64.91, -5.42) * mm, "end": v(-64.53, -5.66) * mm});
            skLineSegment(sketch, "E3503", {"start": v(-64.53, -5.66) * mm, "end": v(-64.15, -5.93) * mm});
            skLineSegment(sketch, "E3504", {"start": v(-64.15, -5.93) * mm, "end": v(-63.82, -6.2) * mm});
            skLineSegment(sketch, "E3505", {"start": v(-63.82, -6.2) * mm, "end": v(-63.57, -6.45) * mm});
            skLineSegment(sketch, "E3506", {"start": v(-63.57, -6.45) * mm, "end": v(-63.12, -7.05) * mm});
            skLineSegment(sketch, "E3507", {"start": v(-63.12, -7.05) * mm, "end": v(-62.7, -7.7) * mm});
            skLineSegment(sketch, "E3508", {"start": v(-62.7, -7.7) * mm, "end": v(-62.34, -8.42) * mm});
            skLineSegment(sketch, "E3509", {"start": v(-62.34, -8.42) * mm, "end": v(-62.02, -9.2) * mm});
            skLineSegment(sketch, "E3510", {"start": v(-62.02, -9.2) * mm, "end": v(-61.76, -10.07) * mm});
            skLineSegment(sketch, "E3511", {"start": v(-61.76, -10.07) * mm, "end": v(-61.57, -11) * mm});
            skLineSegment(sketch, "E3512", {"start": v(-61.57, -11) * mm, "end": v(-61.45, -12.02) * mm});
            skLineSegment(sketch, "E3513", {"start": v(-61.45, -12.02) * mm, "end": v(-61.4, -13.12) * mm});
            skLineSegment(sketch, "E3514", {"start": v(-61.4, -13.12) * mm, "end": v(-61.44, -14.4) * mm});
            skLineSegment(sketch, "E3515", {"start": v(-61.44, -14.4) * mm, "end": v(-61.56, -15.56) * mm});
            skLineSegment(sketch, "E3516", {"start": v(-61.56, -15.56) * mm, "end": v(-61.76, -16.63) * mm});
            skLineSegment(sketch, "E3517", {"start": v(-61.76, -16.63) * mm, "end": v(-62.04, -17.6) * mm});
            skLineSegment(sketch, "E3518", {"start": v(-62.04, -17.6) * mm, "end": v(-62.4, -18.47) * mm});
            skLineSegment(sketch, "E3519", {"start": v(-62.4, -18.47) * mm, "end": v(-62.84, -19.25) * mm});
            skLineSegment(sketch, "E3520", {"start": v(-62.84, -19.25) * mm, "end": v(-63.36, -19.93) * mm});
            skLineSegment(sketch, "E3521", {"start": v(-63.36, -19.93) * mm, "end": v(-63.96, -20.51) * mm});
            skLineSegment(sketch, "E3522", {"start": v(-63.96, -20.51) * mm, "end": v(-64.62, -21) * mm});
            skLineSegment(sketch, "E3523", {"start": v(-64.62, -21) * mm, "end": v(-65.35, -21.41) * mm});
            skLineSegment(sketch, "E3524", {"start": v(-65.35, -21.41) * mm, "end": v(-66.17, -21.76) * mm});
            skLineSegment(sketch, "E3525", {"start": v(-66.17, -21.76) * mm, "end": v(-67.08, -22.05) * mm});
            skLineSegment(sketch, "E3526", {"start": v(-67.08, -22.05) * mm, "end": v(-68.07, -22.27) * mm});
            skLineSegment(sketch, "E3527", {"start": v(-68.07, -22.27) * mm, "end": v(-69.15, -22.43) * mm});
            skLineSegment(sketch, "E3528", {"start": v(-69.15, -22.43) * mm, "end": v(-70.33, -22.52) * mm});
            skLineSegment(sketch, "E3529", {"start": v(-70.33, -22.52) * mm, "end": v(-71.6, -22.56) * mm});
            skLineSegment(sketch, "E3530", {"start": v(-71.6, -22.56) * mm, "end": v(-72.85, -22.6) * mm});
            skLineSegment(sketch, "E3531", {"start": v(-72.85, -22.6) * mm, "end": v(-74.1, -22.62) * mm});
            skLineSegment(sketch, "E3532", {"start": v(-74.1, -22.62) * mm, "end": v(-75.36, -22.66) * mm});
            skLineSegment(sketch, "E3533", {"start": v(-75.36, -22.66) * mm, "end": v(-76.61, -22.7) * mm});
            skLineSegment(sketch, "E3534", {"start": v(-76.61, -22.7) * mm, "end": v(-77.86, -22.73) * mm});
            skLineSegment(sketch, "E3535", {"start": v(-77.86, -22.73) * mm, "end": v(-79.12, -22.76) * mm});
            skLineSegment(sketch, "E3536", {"start": v(-79.12, -22.76) * mm, "end": v(-80.37, -22.8) * mm});
            skLineSegment(sketch, "E3537", {"start": v(-80.37, -22.8) * mm, "end": v(-81.63, -22.83) * mm});
            skLineSegment(sketch, "E3538", {"start": v(-81.63, -22.83) * mm, "end": v(-81.63, -22.83) * mm});
            skLineSegment(sketch, "E3539", {"start": v(-81.63, -22.83) * mm, "end": v(-81.64, -22.83) * mm});
            skLineSegment(sketch, "E3540", {"start": v(-81.64, -22.83) * mm, "end": v(-81.64, -22.83) * mm});
            skLineSegment(sketch, "E3541", {"start": v(-81.64, -22.83) * mm, "end": v(-81.65, -22.83) * mm});
            skLineSegment(sketch, "E3542", {"start": v(-81.65, -22.83) * mm, "end": v(-81.65, -22.83) * mm});
            skLineSegment(sketch, "E3543", {"start": v(-81.65, -22.83) * mm, "end": v(-81.66, -22.83) * mm});
            skLineSegment(sketch, "E3544", {"start": v(-81.66, -22.83) * mm, "end": v(-81.66, -22.83) * mm});
            skLineSegment(sketch, "E3545", {"start": v(-81.66, -22.83) * mm, "end": v(-81.67, -22.83) * mm});
            skLineSegment(sketch, "E3546", {"start": v(-81.67, -22.83) * mm, "end": v(-81.67, -22.83) * mm});
            skLineSegment(sketch, "E3547", {"start": v(-81.67, -22.83) * mm, "end": v(-81.68, -22.83) * mm});
            skLineSegment(sketch, "E3548", {"start": v(-81.68, -22.83) * mm, "end": v(-81.68, -22.83) * mm});
            skLineSegment(sketch, "E3549", {"start": v(-81.68, -22.83) * mm, "end": v(-81.69, -22.83) * mm});
            skLineSegment(sketch, "E3550", {"start": v(-81.69, -22.83) * mm, "end": v(-81.7, -22.83) * mm});
            skLineSegment(sketch, "E3551", {"start": v(-81.7, -22.83) * mm, "end": v(-81.7, -22.83) * mm});
            skLineSegment(sketch, "E3552", {"start": v(-81.7, -22.83) * mm, "end": v(-82.36, -22.81) * mm});
            skLineSegment(sketch, "E3553", {"start": v(-82.36, -22.81) * mm, "end": v(-83.01, -22.8) * mm});
            skLineSegment(sketch, "E3554", {"start": v(-83.01, -22.8) * mm, "end": v(-83.67, -22.78) * mm});
            skLineSegment(sketch, "E3555", {"start": v(-83.67, -22.78) * mm, "end": v(-84.33, -22.77) * mm});
            skLineSegment(sketch, "E3556", {"start": v(-84.33, -22.77) * mm, "end": v(-84.99, -22.75) * mm});
            skLineSegment(sketch, "E3557", {"start": v(-84.99, -22.75) * mm, "end": v(-85.64, -22.74) * mm});
            skLineSegment(sketch, "E3558", {"start": v(-85.64, -22.74) * mm, "end": v(-86.3, -22.72) * mm});
            skLineSegment(sketch, "E3559", {"start": v(-86.3, -22.72) * mm, "end": v(-86.96, -22.7) * mm});
            skLineSegment(sketch, "E3560", {"start": v(-86.96, -22.7) * mm, "end": v(-86.96, -22.7) * mm});
            skLineSegment(sketch, "E3561", {"start": v(-86.96, -22.7) * mm, "end": v(-88.08, -22.69) * mm});
            skLineSegment(sketch, "E3562", {"start": v(-88.08, -22.69) * mm, "end": v(-89.13, -22.61) * mm});
            skLineSegment(sketch, "E3563", {"start": v(-89.13, -22.61) * mm, "end": v(-90.1, -22.49) * mm});
            skLineSegment(sketch, "E3564", {"start": v(-90.1, -22.49) * mm, "end": v(-91, -22.31) * mm});
            skLineSegment(sketch, "E3565", {"start": v(-91, -22.31) * mm, "end": v(-91.83, -22.08) * mm});
            skLineSegment(sketch, "E3566", {"start": v(-91.83, -22.08) * mm, "end": v(-92.59, -21.8) * mm});
            skLineSegment(sketch, "E3567", {"start": v(-92.59, -21.8) * mm, "end": v(-93.28, -21.48) * mm});
            skLineSegment(sketch, "E3568", {"start": v(-93.28, -21.48) * mm, "end": v(-93.9, -21.1) * mm});
            skLineSegment(sketch, "E3569", {"start": v(-93.9, -21.1) * mm, "end": v(-94.51, -20.6) * mm});
            skLineSegment(sketch, "E3570", {"start": v(-94.51, -20.6) * mm, "end": v(-95.04, -20.01) * mm});
            skLineSegment(sketch, "E3571", {"start": v(-95.04, -20.01) * mm, "end": v(-95.5, -19.32) * mm});
            skLineSegment(sketch, "E3572", {"start": v(-95.5, -19.32) * mm, "end": v(-95.86, -18.53) * mm});
            skLineSegment(sketch, "E3573", {"start": v(-95.86, -18.53) * mm, "end": v(-96.15, -17.65) * mm});
            skLineSegment(sketch, "E3574", {"start": v(-96.15, -17.65) * mm, "end": v(-96.35, -16.67) * mm});
            skLineSegment(sketch, "E3575", {"start": v(-96.35, -16.67) * mm, "end": v(-96.47, -15.6) * mm});
            skLineSegment(sketch, "E3576", {"start": v(-96.47, -15.6) * mm, "end": v(-96.51, -14.44) * mm});
            skLineSegment(sketch, "E3577", {"start": v(-96.51, -14.44) * mm, "end": v(-96.51, -14.11) * mm});
            skLineSegment(sketch, "E3578", {"start": v(-96.51, -14.11) * mm, "end": v(-96.51, -13.8) * mm});
            skLineSegment(sketch, "E3579", {"start": v(-96.51, -13.8) * mm, "end": v(-96.51, -13.47) * mm});
            skLineSegment(sketch, "E3580", {"start": v(-96.51, -13.47) * mm, "end": v(-96.51, -13.15) * mm});
            skLineSegment(sketch, "E3581", {"start": v(-96.51, -13.15) * mm, "end": v(-96.51, -12.83) * mm});
            skLineSegment(sketch, "E3582", {"start": v(-96.51, -12.83) * mm, "end": v(-96.51, -12.5) * mm});
            skLineSegment(sketch, "E3583", {"start": v(-96.51, -12.5) * mm, "end": v(-96.51, -12.18) * mm});
            skLineSegment(sketch, "E3584", {"start": v(-96.51, -12.18) * mm, "end": v(-96.51, -11.86) * mm});
            skLineSegment(sketch, "E3585", {"start": v(-96.51, -11.86) * mm, "end": v(-96.51, -11.55) * mm});
            skLineSegment(sketch, "E3586", {"start": v(-96.51, -11.55) * mm, "end": v(-96.51, -11.17) * mm});
            skLineSegment(sketch, "E3587", {"start": v(-96.51, -11.17) * mm, "end": v(-96.5, -10.75) * mm});
            skLineSegment(sketch, "E3588", {"start": v(-96.5, -10.75) * mm, "end": v(-96.5, -10.34) * mm});
            skLineSegment(sketch, "E3589", {"start": v(-96.5, -10.34) * mm, "end": v(-96.5, -9.95) * mm});
            skLineSegment(sketch, "E3590", {"start": v(-96.5, -9.95) * mm, "end": v(-96.5, -9.64) * mm});
            skLineSegment(sketch, "E3591", {"start": v(-96.5, -9.64) * mm, "end": v(-96.5, -9.42) * mm});
            skLineSegment(sketch, "E3592", {"start": v(-96.5, -9.42) * mm, "end": v(-96.5, -9.34) * mm});
            skLineSegment(sketch, "E3593", {"start": v(-96.5, -9.34) * mm, "end": v(-96.43, -9.44) * mm});
            skLineSegment(sketch, "E3594", {"start": v(-96.43, -9.44) * mm, "end": v(-96.24, -9.7) * mm});
            skLineSegment(sketch, "E3595", {"start": v(-96.24, -9.7) * mm, "end": v(-95.9, -10.1) * mm});
            skLineSegment(sketch, "E3596", {"start": v(-95.9, -10.1) * mm, "end": v(-95.41, -10.61) * mm});
            skLineSegment(sketch, "E3597", {"start": v(-95.41, -10.61) * mm, "end": v(-94.75, -11.2) * mm});
            skLineSegment(sketch, "E3598", {"start": v(-94.75, -11.2) * mm, "end": v(-93.9, -11.85) * mm});
            skLineSegment(sketch, "E3599", {"start": v(-93.9, -11.85) * mm, "end": v(-92.86, -12.52) * mm});
            skLineSegment(sketch, "E3600", {"start": v(-92.86, -12.52) * mm, "end": v(-91.6, -13.19) * mm});
            skLineSegment(sketch, "E3601", {"start": v(-91.6, -13.19) * mm, "end": v(-90.83, -13.5) * mm});
            skLineSegment(sketch, "E3602", {"start": v(-90.83, -13.5) * mm, "end": v(-89.97, -13.75) * mm});
            skLineSegment(sketch, "E3603", {"start": v(-89.97, -13.75) * mm, "end": v(-89.03, -13.93) * mm});
            skLineSegment(sketch, "E3604", {"start": v(-89.03, -13.93) * mm, "end": v(-88.01, -14.07) * mm});
            skLineSegment(sketch, "E3605", {"start": v(-88.01, -14.07) * mm, "end": v(-86.92, -14.16) * mm});
            skLineSegment(sketch, "E3606", {"start": v(-86.92, -14.16) * mm, "end": v(-85.76, -14.21) * mm});
            skLineSegment(sketch, "E3607", {"start": v(-85.76, -14.21) * mm, "end": v(-84.54, -14.24) * mm});
            skLineSegment(sketch, "E3608", {"start": v(-84.54, -14.24) * mm, "end": v(-83.25, -14.25) * mm});
            skLineSegment(sketch, "E3609", {"start": v(-83.25, -14.25) * mm, "end": v(-82.79, -14.25) * mm});
            skLineSegment(sketch, "E3610", {"start": v(-82.79, -14.25) * mm, "end": v(-82.33, -14.26) * mm});
            skLineSegment(sketch, "E3611", {"start": v(-82.33, -14.26) * mm, "end": v(-81.86, -14.26) * mm});
            skLineSegment(sketch, "E3612", {"start": v(-81.86, -14.26) * mm, "end": v(-81.4, -14.26) * mm});
            skLineSegment(sketch, "E3613", {"start": v(-81.4, -14.26) * mm, "end": v(-80.94, -14.27) * mm});
            skLineSegment(sketch, "E3614", {"start": v(-80.94, -14.27) * mm, "end": v(-80.48, -14.27) * mm});
            skLineSegment(sketch, "E3615", {"start": v(-80.48, -14.27) * mm, "end": v(-80.02, -14.28) * mm});
            skLineSegment(sketch, "E3616", {"start": v(-80.02, -14.28) * mm, "end": v(-79.55, -14.28) * mm});
            skLineSegment(sketch, "E3617", {"start": v(-79.55, -14.28) * mm, "end": v(-78.9, -14.26) * mm});
            skLineSegment(sketch, "E3618", {"start": v(-78.9, -14.26) * mm, "end": v(-78.25, -14.25) * mm});
            skLineSegment(sketch, "E3619", {"start": v(-78.25, -14.25) * mm, "end": v(-77.6, -14.23) * mm});
            skLineSegment(sketch, "E3620", {"start": v(-77.6, -14.23) * mm, "end": v(-76.94, -14.2) * mm});
            skLineSegment(sketch, "E3621", {"start": v(-76.94, -14.2) * mm, "end": v(-76.28, -14.19) * mm});
            skLineSegment(sketch, "E3622", {"start": v(-76.28, -14.19) * mm, "end": v(-75.63, -14.17) * mm});
            skLineSegment(sketch, "E3623", {"start": v(-75.63, -14.17) * mm, "end": v(-74.98, -14.15) * mm});
            skLineSegment(sketch, "E3624", {"start": v(-74.98, -14.15) * mm, "end": v(-74.32, -14.13) * mm});
            skLineSegment(sketch, "E3625", {"start": v(-74.32, -14.13) * mm, "end": v(-74.32, -14.13) * mm});
            skLineSegment(sketch, "E3626", {"start": v(-74.32, -14.13) * mm, "end": v(-74.31, -14.13) * mm});
            skLineSegment(sketch, "E3627", {"start": v(-74.31, -14.13) * mm, "end": v(-74.3, -14.13) * mm});
            skLineSegment(sketch, "E3628", {"start": v(-74.3, -14.13) * mm, "end": v(-74.3, -14.13) * mm});
            skLineSegment(sketch, "E3629", {"start": v(-74.3, -14.13) * mm, "end": v(-74.29, -14.13) * mm});
            skLineSegment(sketch, "E3630", {"start": v(-74.29, -14.13) * mm, "end": v(-74.28, -14.13) * mm});
            skLineSegment(sketch, "E3631", {"start": v(-74.28, -14.13) * mm, "end": v(-73.8, -14.12) * mm});
            skLineSegment(sketch, "E3632", {"start": v(-73.8, -14.12) * mm, "end": v(-73.39, -14.08) * mm});
            skLineSegment(sketch, "E3633", {"start": v(-73.39, -14.08) * mm, "end": v(-73.04, -14.02) * mm});
            skLineSegment(sketch, "E3634", {"start": v(-73.04, -14.02) * mm, "end": v(-72.76, -13.94) * mm});
            skLineSegment(sketch, "E3635", {"start": v(-72.76, -13.94) * mm, "end": v(-72.54, -13.83) * mm});
            skLineSegment(sketch, "E3636", {"start": v(-72.54, -13.83) * mm, "end": v(-72.39, -13.7) * mm});
            skLineSegment(sketch, "E3637", {"start": v(-72.39, -13.7) * mm, "end": v(-72.3, -13.54) * mm});
            skLineSegment(sketch, "E3638", {"start": v(-72.3, -13.54) * mm, "end": v(-72.27, -13.35) * mm});
            skLineSegment(sketch, "E3639", {"start": v(-72.27, -13.35) * mm, "end": v(-72.3, -13.17) * mm});
            skLineSegment(sketch, "E3640", {"start": v(-72.3, -13.17) * mm, "end": v(-72.39, -13) * mm});
            skLineSegment(sketch, "E3641", {"start": v(-72.39, -13) * mm, "end": v(-72.54, -12.86) * mm});
            skLineSegment(sketch, "E3642", {"start": v(-72.54, -12.86) * mm, "end": v(-72.77, -12.75) * mm});
            skLineSegment(sketch, "E3643", {"start": v(-72.77, -12.75) * mm, "end": v(-73.06, -12.66) * mm});
            skLineSegment(sketch, "E3644", {"start": v(-73.06, -12.66) * mm, "end": v(-73.44, -12.6) * mm});
            skLineSegment(sketch, "E3645", {"start": v(-73.44, -12.6) * mm, "end": v(-73.9, -12.55) * mm});
            skLineSegment(sketch, "E3646", {"start": v(-73.9, -12.55) * mm, "end": v(-74.43, -12.54) * mm});
            skLineSegment(sketch, "E3647", {"start": v(-74.43, -12.54) * mm, "end": v(-74.6, -12.54) * mm});
            skLineSegment(sketch, "E3648", {"start": v(-74.6, -12.54) * mm, "end": v(-74.75, -12.54) * mm});
            skLineSegment(sketch, "E3649", {"start": v(-74.75, -12.54) * mm, "end": v(-74.91, -12.54) * mm});
            skLineSegment(sketch, "E3650", {"start": v(-74.91, -12.54) * mm, "end": v(-75.07, -12.54) * mm});
            skLineSegment(sketch, "E3651", {"start": v(-75.07, -12.54) * mm, "end": v(-75.23, -12.54) * mm});
            skLineSegment(sketch, "E3652", {"start": v(-75.23, -12.54) * mm, "end": v(-75.4, -12.54) * mm});
            skLineSegment(sketch, "E3653", {"start": v(-75.4, -12.54) * mm, "end": v(-75.55, -12.54) * mm});
            skLineSegment(sketch, "E3654", {"start": v(-75.55, -12.54) * mm, "end": v(-75.71, -12.54) * mm});
            skLineSegment(sketch, "E3655", {"start": v(-75.71, -12.54) * mm, "end": v(-77.33, -12.5) * mm});
            skLineSegment(sketch, "E3656", {"start": v(-77.33, -12.5) * mm, "end": v(-78.95, -12.47) * mm});
            skLineSegment(sketch, "E3657", {"start": v(-78.95, -12.47) * mm, "end": v(-80.57, -12.44) * mm});
            skLineSegment(sketch, "E3658", {"start": v(-80.57, -12.44) * mm, "end": v(-82.19, -12.4) * mm});
            skLineSegment(sketch, "E3659", {"start": v(-82.19, -12.4) * mm, "end": v(-83.8, -12.37) * mm});
            skLineSegment(sketch, "E3660", {"start": v(-83.8, -12.37) * mm, "end": v(-85.42, -12.34) * mm});
            skLineSegment(sketch, "E3661", {"start": v(-85.42, -12.34) * mm, "end": v(-87.04, -12.3) * mm});
            skLineSegment(sketch, "E3662", {"start": v(-87.04, -12.3) * mm, "end": v(-88.66, -12.27) * mm});
            skLineSegment(sketch, "E3663", {"start": v(-88.66, -12.27) * mm, "end": v(-88.66, -12.27) * mm});
            skLineSegment(sketch, "E3664", {"start": v(-88.66, -12.27) * mm, "end": v(-89.7, -12.23) * mm});
            skLineSegment(sketch, "E3665", {"start": v(-89.7, -12.23) * mm, "end": v(-90.66, -12.12) * mm});
            skLineSegment(sketch, "E3666", {"start": v(-90.66, -12.12) * mm, "end": v(-91.55, -11.93) * mm});
            skLineSegment(sketch, "E3667", {"start": v(-91.55, -11.93) * mm, "end": v(-92.37, -11.67) * mm});
            skLineSegment(sketch, "E3668", {"start": v(-92.37, -11.67) * mm, "end": v(-93.11, -11.33) * mm});
            skLineSegment(sketch, "E3669", {"start": v(-93.11, -11.33) * mm, "end": v(-93.78, -10.92) * mm});
            skLineSegment(sketch, "E3670", {"start": v(-93.78, -10.92) * mm, "end": v(-94.37, -10.44) * mm});
            skLineSegment(sketch, "E3671", {"start": v(-94.37, -10.44) * mm, "end": v(-94.9, -9.89) * mm});
            skLineSegment(sketch, "E3672", {"start": v(-94.9, -9.89) * mm, "end": v(-95.32, -9.29) * mm});
            skLineSegment(sketch, "E3673", {"start": v(-95.32, -9.29) * mm, "end": v(-95.7, -8.63) * mm});
            skLineSegment(sketch, "E3674", {"start": v(-95.7, -8.63) * mm, "end": v(-96, -7.92) * mm});
            skLineSegment(sketch, "E3675", {"start": v(-96, -7.92) * mm, "end": v(-96.26, -7.13) * mm});
            skLineSegment(sketch, "E3676", {"start": v(-96.26, -7.13) * mm, "end": v(-96.46, -6.29) * mm});
            skLineSegment(sketch, "E3677", {"start": v(-96.46, -6.29) * mm, "end": v(-96.6, -5.37) * mm});
            skLineSegment(sketch, "E3678", {"start": v(-96.6, -5.37) * mm, "end": v(-96.68, -4.4) * mm});
            skLineSegment(sketch, "E3679", {"start": v(-96.68, -4.4) * mm, "end": v(-96.7, -3.34) * mm});
            skLineSegment(sketch, "E3680", {"start": v(-96.7, -3.34) * mm, "end": v(-96.7, -2.46) * mm});
            skLineSegment(sketch, "E3681", {"start": v(-96.7, -2.46) * mm, "end": v(-96.64, -1.63) * mm});
            skLineSegment(sketch, "E3682", {"start": v(-96.64, -1.63) * mm, "end": v(-96.55, -0.86) * mm});
            skLineSegment(sketch, "E3683", {"start": v(-96.55, -0.86) * mm, "end": v(-96.43, -0.12) * mm});
            skLineSegment(sketch, "E3684", {"start": v(-96.43, -0.12) * mm, "end": v(-96.27, 0.56) * mm});
            skLineSegment(sketch, "E3685", {"start": v(-96.27, 0.56) * mm, "end": v(-96.08, 1.2) * mm});
            skLineSegment(sketch, "E3686", {"start": v(-96.08, 1.2) * mm, "end": v(-95.85, 1.8) * mm});
            skLineSegment(sketch, "E3687", {"start": v(-95.85, 1.8) * mm, "end": v(-95.59, 2.34) * mm});
            skLineSegment(sketch, "E3688", {"start": v(-95.59, 2.34) * mm, "end": v(-95.25, 2.9) * mm});
            skLineSegment(sketch, "E3689", {"start": v(-95.25, 2.9) * mm, "end": v(-94.84, 3.42) * mm});
            skLineSegment(sketch, "E3690", {"start": v(-94.84, 3.42) * mm, "end": v(-94.38, 3.88) * mm});
            skLineSegment(sketch, "E3691", {"start": v(-94.38, 3.88) * mm, "end": v(-93.87, 4.3) * mm});
            skLineSegment(sketch, "E3692", {"start": v(-93.87, 4.3) * mm, "end": v(-93.29, 4.67) * mm});
            skLineSegment(sketch, "E3693", {"start": v(-93.29, 4.67) * mm, "end": v(-92.65, 5) * mm});
            skLineSegment(sketch, "E3694", {"start": v(-92.65, 5) * mm, "end": v(-91.96, 5.26) * mm});
            skLineSegment(sketch, "E3695", {"start": v(-91.96, 5.26) * mm, "end": v(-91.22, 5.49) * mm});
            skLineSegment(sketch, "E3696", {"start": v(-91.22, 5.49) * mm, "end": v(-90.53, 5.65) * mm});
            skLineSegment(sketch, "E3697", {"start": v(-90.53, 5.65) * mm, "end": v(-89.8, 5.8) * mm});
            skLineSegment(sketch, "E3698", {"start": v(-89.8, 5.8) * mm, "end": v(-89, 5.92) * mm});
            skLineSegment(sketch, "E3699", {"start": v(-89, 5.92) * mm, "end": v(-88.17, 6.03) * mm});
            skLineSegment(sketch, "E3700", {"start": v(-88.17, 6.03) * mm, "end": v(-87.29, 6.12) * mm});
            skLineSegment(sketch, "E3701", {"start": v(-87.29, 6.12) * mm, "end": v(-86.36, 6.2) * mm});
            skLineSegment(sketch, "E3702", {"start": v(-86.36, 6.2) * mm, "end": v(-85.38, 6.25) * mm});
            skLineSegment(sketch, "E3703", {"start": v(-85.38, 6.25) * mm, "end": v(-84.36, 6.29) * mm});
            skLineSegment(sketch, "E3704", {"start": v(-84.36, 6.29) * mm, "end": v(-83.4, 6.31) * mm});
            skLineSegment(sketch, "E3705", {"start": v(-83.4, 6.31) * mm, "end": v(-82.52, 6.34) * mm});
            skLineSegment(sketch, "E3706", {"start": v(-82.52, 6.34) * mm, "end": v(-81.71, 6.36) * mm});
            skLineSegment(sketch, "E3707", {"start": v(-81.71, 6.36) * mm, "end": v(-80.99, 6.37) * mm});
            skLineSegment(sketch, "E3708", {"start": v(-80.99, 6.37) * mm, "end": v(-80.34, 6.39) * mm});
            skLineSegment(sketch, "E3709", {"start": v(-80.34, 6.39) * mm, "end": v(-79.78, 6.4) * mm});
            skLineSegment(sketch, "E3710", {"start": v(-79.78, 6.4) * mm, "end": v(-79.29, 6.4) * mm});
            skLineSegment(sketch, "E3711", {"start": v(-79.29, 6.4) * mm, "end": v(-78.88, 6.4) * mm});
            skLineSegment(sketch, "E3712", {"start": v(-78.88, 6.4) * mm, "end": v(-78.2, 6.4) * mm});
            skLineSegment(sketch, "E3713", {"start": v(-78.2, 6.4) * mm, "end": v(-77.5, 6.39) * mm});
            skLineSegment(sketch, "E3714", {"start": v(-77.5, 6.39) * mm, "end": v(-76.82, 6.38) * mm});
            skLineSegment(sketch, "E3715", {"start": v(-76.82, 6.38) * mm, "end": v(-76.13, 6.37) * mm});
            skLineSegment(sketch, "E3716", {"start": v(-76.13, 6.37) * mm, "end": v(-75.44, 6.36) * mm});
            skLineSegment(sketch, "E3717", {"start": v(-75.44, 6.36) * mm, "end": v(-74.75, 6.35) * mm});
            skLineSegment(sketch, "E3718", {"start": v(-74.75, 6.35) * mm, "end": v(-74.06, 6.34) * mm});
            skLineSegment(sketch, "E3719", {"start": v(-74.06, 6.34) * mm, "end": v(-73.37, 6.33) * mm});
            skLineSegment(sketch, "E3720", {"start": v(-73.37, 6.33) * mm, "end": v(-73.37, 6.33) * mm});
            skLineSegment(sketch, "E3721", {"start": v(-73.37, 6.33) * mm, "end": v(-72.53, 6.32) * mm});
            skLineSegment(sketch, "E3722", {"start": v(-72.53, 6.32) * mm, "end": v(-71.73, 6.3) * mm});
            skLineSegment(sketch, "E3723", {"start": v(-71.73, 6.3) * mm, "end": v(-70.97, 6.25) * mm});
            skLineSegment(sketch, "E3724", {"start": v(-70.97, 6.25) * mm, "end": v(-70.24, 6.19) * mm});
            skLineSegment(sketch, "E3725", {"start": v(-70.24, 6.19) * mm, "end": v(-69.56, 6.1) * mm});
            skLineSegment(sketch, "E3726", {"start": v(-69.56, 6.1) * mm, "end": v(-68.9, 6) * mm});
            skLineSegment(sketch, "E3727", {"start": v(-68.9, 6) * mm, "end": v(-68.3, 5.9) * mm});
            skLineSegment(sketch, "E3728", {"start": v(-68.3, 5.9) * mm, "end": v(-67.73, 5.76) * mm});
            skLineSegment(sketch, "E3729", {"start": v(-67.73, 5.76) * mm, "end": v(-67.1, 5.57) * mm});
            skLineSegment(sketch, "E3730", {"start": v(-67.1, 5.57) * mm, "end": v(-66.53, 5.34) * mm});
            skLineSegment(sketch, "E3731", {"start": v(-66.53, 5.34) * mm, "end": v(-66, 5.06) * mm});
            skLineSegment(sketch, "E3732", {"start": v(-66, 5.06) * mm, "end": v(-65.53, 4.75) * mm});
            skLineSegment(sketch, "E3733", {"start": v(-65.53, 4.75) * mm, "end": v(-65.09, 4.4) * mm});
            skLineSegment(sketch, "E3734", {"start": v(-65.09, 4.4) * mm, "end": v(-64.69, 4.03) * mm});
            skLineSegment(sketch, "E3735", {"start": v(-64.69, 4.03) * mm, "end": v(-64.32, 3.62) * mm});
            skLineSegment(sketch, "E3736", {"start": v(-64.32, 3.62) * mm, "end": v(-64, 3.17) * mm});
            skLineSegment(sketch, "E3737", {"start": v(-64, 3.17) * mm, "end": v(-63.72, 2.67) * mm});
            skLineSegment(sketch, "E3738", {"start": v(-63.72, 2.67) * mm, "end": v(-63.5, 2.07) * mm});
            skLineSegment(sketch, "E3739", {"start": v(-63.5, 2.07) * mm, "end": v(-63.35, 1.4) * mm});
            skLineSegment(sketch, "E3740", {"start": v(-63.35, 1.4) * mm, "end": v(-63.23, 0.68) * mm});
            skLineSegment(sketch, "E3741", {"start": v(-63.23, 0.68) * mm, "end": v(-63.15, -0.03) * mm});
            skLineSegment(sketch, "E3742", {"start": v(-63.15, -0.03) * mm, "end": v(-63.1, -0.73) * mm});
            skLineSegment(sketch, "E3743", {"start": v(-63.1, -0.73) * mm, "end": v(-63.07, -1.37) * mm});
            skLineSegment(sketch, "E3744", {"start": v(-63.07, -1.37) * mm, "end": v(-63.05, -1.93) * mm});
            skLineSegment(sketch, "E3745", {"start": v(-63.05, -1.93) * mm, "end": v(-63.06, -2.58) * mm});
            skLineSegment(sketch, "E3746", {"start": v(-63.06, -2.58) * mm, "end": v(-63.1, -3.23) * mm});
            skLineSegment(sketch, "E3747", {"start": v(-63.1, -3.23) * mm, "end": v(-63.17, -3.86) * mm});
            skLineSegment(sketch, "E3748", {"start": v(-63.17, -3.86) * mm, "end": v(-63.25, -4.44) * mm});
            skLineSegment(sketch, "E3749", {"start": v(-63.25, -4.44) * mm, "end": v(-63.34, -4.93) * mm});
            skLineSegment(sketch, "E3750", {"start": v(-63.34, -4.93) * mm, "end": v(-63.41, -5.32) * mm});
            skLineSegment(sketch, "E3751", {"start": v(-63.41, -5.32) * mm, "end": v(-63.47, -5.58) * mm});
            skLineSegment(sketch, "E3752", {"start": v(-63.47, -5.58) * mm, "end": v(-63.49, -5.67) * mm});
            skLineSegment(sketch, "E3753", {"start": v(-63.49, -5.67) * mm, "end": v(-63.57, -5.6) * mm});
            skLineSegment(sketch, "E3754", {"start": v(-63.57, -5.6) * mm, "end": v(-63.8, -5.42) * mm});
            skLineSegment(sketch, "E3755", {"start": v(-63.8, -5.42) * mm, "end": v(-64.13, -5.16) * mm});
            skLineSegment(sketch, "E3756", {"start": v(-64.13, -5.16) * mm, "end": v(-64.55, -4.85) * mm});
            skLineSegment(sketch, "E3757", {"start": v(-64.55, -4.85) * mm, "end": v(-65.01, -4.51) * mm});
            skLineSegment(sketch, "E3758", {"start": v(-65.01, -4.51) * mm, "end": v(-65.5, -4.18) * mm});
            skLineSegment(sketch, "E3759", {"start": v(-65.5, -4.18) * mm, "end": v(-65.96, -3.87) * mm});
            skLineSegment(sketch, "E3760", {"start": v(-65.96, -3.87) * mm, "end": v(-66.38, -3.64) * mm});
            skLineSegment(sketch, "E3761", {"start": v(73.89, -15.71) * mm, "end": v(74.35, -15.72) * mm});
            skLineSegment(sketch, "E3762", {"start": v(74.35, -15.72) * mm, "end": v(74.82, -15.72) * mm});
            skLineSegment(sketch, "E3763", {"start": v(74.82, -15.72) * mm, "end": v(75.28, -15.73) * mm});
            skLineSegment(sketch, "E3764", {"start": v(75.28, -15.73) * mm, "end": v(75.74, -15.73) * mm});
            skLineSegment(sketch, "E3765", {"start": v(75.74, -15.73) * mm, "end": v(76.2, -15.74) * mm});
            skLineSegment(sketch, "E3766", {"start": v(76.2, -15.74) * mm, "end": v(76.67, -15.74) * mm});
            skLineSegment(sketch, "E3767", {"start": v(76.67, -15.74) * mm, "end": v(77.14, -15.75) * mm});
            skLineSegment(sketch, "E3768", {"start": v(77.14, -15.75) * mm, "end": v(77.6, -15.75) * mm});
            skLineSegment(sketch, "E3769", {"start": v(77.6, -15.75) * mm, "end": v(78.26, -15.73) * mm});
            skLineSegment(sketch, "E3770", {"start": v(78.26, -15.73) * mm, "end": v(78.92, -15.71) * mm});
            skLineSegment(sketch, "E3771", {"start": v(78.92, -15.71) * mm, "end": v(79.57, -15.7) * mm});
            skLineSegment(sketch, "E3772", {"start": v(79.57, -15.7) * mm, "end": v(80.23, -15.67) * mm});
            skLineSegment(sketch, "E3773", {"start": v(80.23, -15.67) * mm, "end": v(80.89, -15.65) * mm});
            skLineSegment(sketch, "E3774", {"start": v(80.89, -15.65) * mm, "end": v(81.55, -15.64) * mm});
            skLineSegment(sketch, "E3775", {"start": v(81.55, -15.64) * mm, "end": v(82.2, -15.62) * mm});
            skLineSegment(sketch, "E3776", {"start": v(82.2, -15.62) * mm, "end": v(82.86, -15.6) * mm});
            skLineSegment(sketch, "E3777", {"start": v(82.86, -15.6) * mm, "end": v(83.38, -15.59) * mm});
            skLineSegment(sketch, "E3778", {"start": v(83.38, -15.59) * mm, "end": v(83.85, -15.56) * mm});
            skLineSegment(sketch, "E3779", {"start": v(83.85, -15.56) * mm, "end": v(84.27, -15.52) * mm});
            skLineSegment(sketch, "E3780", {"start": v(84.27, -15.52) * mm, "end": v(84.65, -15.46) * mm});
            skLineSegment(sketch, "E3781", {"start": v(84.65, -15.46) * mm, "end": v(84.98, -15.39) * mm});
            skLineSegment(sketch, "E3782", {"start": v(84.98, -15.39) * mm, "end": v(85.26, -15.3) * mm});
            skLineSegment(sketch, "E3783", {"start": v(85.26, -15.3) * mm, "end": v(85.5, -15.18) * mm});
            skLineSegment(sketch, "E3784", {"start": v(85.5, -15.18) * mm, "end": v(85.68, -15.06) * mm});
            skLineSegment(sketch, "E3785", {"start": v(85.68, -15.06) * mm, "end": v(85.84, -14.91) * mm});
            skLineSegment(sketch, "E3786", {"start": v(85.84, -14.91) * mm, "end": v(85.97, -14.75) * mm});
            skLineSegment(sketch, "E3787", {"start": v(85.97, -14.75) * mm, "end": v(86.08, -14.56) * mm});
            skLineSegment(sketch, "E3788", {"start": v(86.08, -14.56) * mm, "end": v(86.18, -14.36) * mm});
            skLineSegment(sketch, "E3789", {"start": v(86.18, -14.36) * mm, "end": v(86.25, -14.14) * mm});
            skLineSegment(sketch, "E3790", {"start": v(86.25, -14.14) * mm, "end": v(86.3, -13.9) * mm});
            skLineSegment(sketch, "E3791", {"start": v(86.3, -13.9) * mm, "end": v(86.33, -13.63) * mm});
            skLineSegment(sketch, "E3792", {"start": v(86.33, -13.63) * mm, "end": v(86.34, -13.35) * mm});
            skLineSegment(sketch, "E3793", {"start": v(86.34, -13.35) * mm, "end": v(86.33, -13.1) * mm});
            skLineSegment(sketch, "E3794", {"start": v(86.33, -13.1) * mm, "end": v(86.3, -12.86) * mm});
            skLineSegment(sketch, "E3795", {"start": v(86.3, -12.86) * mm, "end": v(86.24, -12.63) * mm});
            skLineSegment(sketch, "E3796", {"start": v(86.24, -12.63) * mm, "end": v(86.15, -12.42) * mm});
            skLineSegment(sketch, "E3797", {"start": v(86.15, -12.42) * mm, "end": v(86.05, -12.22) * mm});
            skLineSegment(sketch, "E3798", {"start": v(86.05, -12.22) * mm, "end": v(85.92, -12.03) * mm});
            skLineSegment(sketch, "E3799", {"start": v(85.92, -12.03) * mm, "end": v(85.76, -11.85) * mm});
            skLineSegment(sketch, "E3800", {"start": v(85.76, -11.85) * mm, "end": v(85.59, -11.7) * mm});
            skLineSegment(sketch, "E3801", {"start": v(85.59, -11.7) * mm, "end": v(85.38, -11.55) * mm});
            skLineSegment(sketch, "E3802", {"start": v(85.38, -11.55) * mm, "end": v(85.12, -11.42) * mm});
            skLineSegment(sketch, "E3803", {"start": v(85.12, -11.42) * mm, "end": v(84.83, -11.31) * mm});
            skLineSegment(sketch, "E3804", {"start": v(84.83, -11.31) * mm, "end": v(84.49, -11.23) * mm});
            skLineSegment(sketch, "E3805", {"start": v(84.49, -11.23) * mm, "end": v(84.1, -11.16) * mm});
            skLineSegment(sketch, "E3806", {"start": v(84.1, -11.16) * mm, "end": v(83.68, -11.1) * mm});
            skLineSegment(sketch, "E3807", {"start": v(83.68, -11.1) * mm, "end": v(83.22, -11.08) * mm});
            skLineSegment(sketch, "E3808", {"start": v(83.22, -11.08) * mm, "end": v(82.7, -11.07) * mm});
            skLineSegment(sketch, "E3809", {"start": v(82.7, -11.07) * mm, "end": v(82.55, -11.07) * mm});
            skLineSegment(sketch, "E3810", {"start": v(82.55, -11.07) * mm, "end": v(82.39, -11.07) * mm});
            skLineSegment(sketch, "E3811", {"start": v(82.39, -11.07) * mm, "end": v(82.23, -11.07) * mm});
            skLineSegment(sketch, "E3812", {"start": v(82.23, -11.07) * mm, "end": v(82.07, -11.07) * mm});
            skLineSegment(sketch, "E3813", {"start": v(82.07, -11.07) * mm, "end": v(81.9, -11.07) * mm});
            skLineSegment(sketch, "E3814", {"start": v(81.9, -11.07) * mm, "end": v(81.75, -11.07) * mm});
            skLineSegment(sketch, "E3815", {"start": v(81.75, -11.07) * mm, "end": v(81.59, -11.07) * mm});
            skLineSegment(sketch, "E3816", {"start": v(81.59, -11.07) * mm, "end": v(81.43, -11.07) * mm});
            skLineSegment(sketch, "E3817", {"start": v(81.43, -11.07) * mm, "end": v(79.81, -11.04) * mm});
            skLineSegment(sketch, "E3818", {"start": v(79.81, -11.04) * mm, "end": v(78.2, -11) * mm});
            skLineSegment(sketch, "E3819", {"start": v(78.2, -11) * mm, "end": v(76.58, -10.97) * mm});
            skLineSegment(sketch, "E3820", {"start": v(76.58, -10.97) * mm, "end": v(74.97, -10.94) * mm});
            skLineSegment(sketch, "E3821", {"start": v(74.97, -10.94) * mm, "end": v(73.36, -10.9) * mm});
            skLineSegment(sketch, "E3822", {"start": v(73.36, -10.9) * mm, "end": v(71.74, -10.87) * mm});
            skLineSegment(sketch, "E3823", {"start": v(71.74, -10.87) * mm, "end": v(70.13, -10.83) * mm});
            skLineSegment(sketch, "E3824", {"start": v(70.13, -10.83) * mm, "end": v(68.51, -10.8) * mm});
            skLineSegment(sketch, "E3825", {"start": v(68.51, -10.8) * mm, "end": v(67.64, -10.77) * mm});
            skLineSegment(sketch, "E3826", {"start": v(67.64, -10.77) * mm, "end": v(66.83, -10.69) * mm});
            skLineSegment(sketch, "E3827", {"start": v(66.83, -10.69) * mm, "end": v(66.09, -10.54) * mm});
            skLineSegment(sketch, "E3828", {"start": v(66.09, -10.54) * mm, "end": v(65.41, -10.34) * mm});
            skLineSegment(sketch, "E3829", {"start": v(65.41, -10.34) * mm, "end": v(64.8, -10.08) * mm});
            skLineSegment(sketch, "E3830", {"start": v(64.8, -10.08) * mm, "end": v(64.27, -9.77) * mm});
            skLineSegment(sketch, "E3831", {"start": v(64.27, -9.77) * mm, "end": v(63.8, -9.4) * mm});
            skLineSegment(sketch, "E3832", {"start": v(63.8, -9.4) * mm, "end": v(63.39, -8.96) * mm});
            skLineSegment(sketch, "E3833", {"start": v(63.39, -8.96) * mm, "end": v(63.04, -8.47) * mm});
            skLineSegment(sketch, "E3834", {"start": v(63.04, -8.47) * mm, "end": v(62.74, -7.92) * mm});
            skLineSegment(sketch, "E3835", {"start": v(62.74, -7.92) * mm, "end": v(62.48, -7.31) * mm});
            skLineSegment(sketch, "E3836", {"start": v(62.48, -7.31) * mm, "end": v(62.27, -6.64) * mm});
            skLineSegment(sketch, "E3837", {"start": v(62.27, -6.64) * mm, "end": v(62.11, -5.9) * mm});
            skLineSegment(sketch, "E3838", {"start": v(62.11, -5.9) * mm, "end": v(62, -5.11) * mm});
            skLineSegment(sketch, "E3839", {"start": v(62, -5.11) * mm, "end": v(61.92, -4.26) * mm});
            skLineSegment(sketch, "E3840", {"start": v(61.92, -4.26) * mm, "end": v(61.9, -3.34) * mm});
            skLineSegment(sketch, "E3841", {"start": v(61.9, -3.34) * mm, "end": v(61.92, -2.56) * mm});
            skLineSegment(sketch, "E3842", {"start": v(61.92, -2.56) * mm, "end": v(61.96, -1.82) * mm});
            skLineSegment(sketch, "E3843", {"start": v(61.96, -1.82) * mm, "end": v(62.03, -1.13) * mm});
            skLineSegment(sketch, "E3844", {"start": v(62.03, -1.13) * mm, "end": v(62.14, -0.49) * mm});
            skLineSegment(sketch, "E3845", {"start": v(62.14, -0.49) * mm, "end": v(62.27, 0.12) * mm});
            skLineSegment(sketch, "E3846", {"start": v(62.27, 0.12) * mm, "end": v(62.43, 0.67) * mm});
            skLineSegment(sketch, "E3847", {"start": v(62.43, 0.67) * mm, "end": v(62.63, 1.18) * mm});
            skLineSegment(sketch, "E3848", {"start": v(62.63, 1.18) * mm, "end": v(62.85, 1.65) * mm});
            skLineSegment(sketch, "E3849", {"start": v(62.85, 1.65) * mm, "end": v(63.1, 2.08) * mm});
            skLineSegment(sketch, "E3850", {"start": v(63.1, 2.08) * mm, "end": v(63.42, 2.47) * mm});
            skLineSegment(sketch, "E3851", {"start": v(63.42, 2.47) * mm, "end": v(63.78, 2.82) * mm});
            skLineSegment(sketch, "E3852", {"start": v(63.78, 2.82) * mm, "end": v(64.18, 3.14) * mm});
            skLineSegment(sketch, "E3853", {"start": v(64.18, 3.14) * mm, "end": v(64.64, 3.43) * mm});
            skLineSegment(sketch, "E3854", {"start": v(64.64, 3.43) * mm, "end": v(65.14, 3.68) * mm});
            skLineSegment(sketch, "E3855", {"start": v(65.14, 3.68) * mm, "end": v(65.7, 3.9) * mm});
            skLineSegment(sketch, "E3856", {"start": v(65.7, 3.9) * mm, "end": v(66.3, 4.07) * mm});
            skLineSegment(sketch, "E3857", {"start": v(66.3, 4.07) * mm, "end": v(66.94, 4.22) * mm});
            skLineSegment(sketch, "E3858", {"start": v(66.94, 4.22) * mm, "end": v(67.63, 4.35) * mm});
            skLineSegment(sketch, "E3859", {"start": v(67.63, 4.35) * mm, "end": v(68.38, 4.47) * mm});
            skLineSegment(sketch, "E3860", {"start": v(68.38, 4.47) * mm, "end": v(69.17, 4.58) * mm});
            skLineSegment(sketch, "E3861", {"start": v(69.17, 4.58) * mm, "end": v(70.01, 4.66) * mm});
            skLineSegment(sketch, "E3862", {"start": v(70.01, 4.66) * mm, "end": v(70.9, 4.73) * mm});
            skLineSegment(sketch, "E3863", {"start": v(70.9, 4.73) * mm, "end": v(71.84, 4.78) * mm});
            skLineSegment(sketch, "E3864", {"start": v(71.84, 4.78) * mm, "end": v(72.82, 4.82) * mm});
            skLineSegment(sketch, "E3865", {"start": v(72.82, 4.82) * mm, "end": v(73.8, 4.85) * mm});
            skLineSegment(sketch, "E3866", {"start": v(73.8, 4.85) * mm, "end": v(74.68, 4.87) * mm});
            skLineSegment(sketch, "E3867", {"start": v(74.68, 4.87) * mm, "end": v(75.48, 4.9) * mm});
            skLineSegment(sketch, "E3868", {"start": v(75.48, 4.9) * mm, "end": v(76.2, 4.9) * mm});
            skLineSegment(sketch, "E3869", {"start": v(76.2, 4.9) * mm, "end": v(76.84, 4.92) * mm});
            skLineSegment(sketch, "E3870", {"start": v(76.84, 4.92) * mm, "end": v(77.4, 4.93) * mm});
            skLineSegment(sketch, "E3871", {"start": v(77.4, 4.93) * mm, "end": v(77.87, 4.94) * mm});
            skLineSegment(sketch, "E3872", {"start": v(77.87, 4.94) * mm, "end": v(78.26, 4.94) * mm});
            skLineSegment(sketch, "E3873", {"start": v(78.26, 4.94) * mm, "end": v(78.95, 4.93) * mm});
            skLineSegment(sketch, "E3874", {"start": v(78.95, 4.93) * mm, "end": v(79.63, 4.92) * mm});
            skLineSegment(sketch, "E3875", {"start": v(79.63, 4.92) * mm, "end": v(80.32, 4.9) * mm});
            skLineSegment(sketch, "E3876", {"start": v(80.32, 4.9) * mm, "end": v(81, 4.9) * mm});
            skLineSegment(sketch, "E3877", {"start": v(81, 4.9) * mm, "end": v(81.7, 4.89) * mm});
            skLineSegment(sketch, "E3878", {"start": v(81.7, 4.89) * mm, "end": v(82.38, 4.88) * mm});
            skLineSegment(sketch, "E3879", {"start": v(82.38, 4.88) * mm, "end": v(83.06, 4.87) * mm});
            skLineSegment(sketch, "E3880", {"start": v(83.06, 4.87) * mm, "end": v(83.75, 4.86) * mm});
            skLineSegment(sketch, "E3881", {"start": v(83.75, 4.86) * mm, "end": v(84.55, 4.85) * mm});
            skLineSegment(sketch, "E3882", {"start": v(84.55, 4.85) * mm, "end": v(85.31, 4.83) * mm});
            skLineSegment(sketch, "E3883", {"start": v(85.31, 4.83) * mm, "end": v(86.04, 4.79) * mm});
            skLineSegment(sketch, "E3884", {"start": v(86.04, 4.79) * mm, "end": v(86.72, 4.73) * mm});
            skLineSegment(sketch, "E3885", {"start": v(86.72, 4.73) * mm, "end": v(87.36, 4.66) * mm});
            skLineSegment(sketch, "E3886", {"start": v(87.36, 4.66) * mm, "end": v(87.96, 4.57) * mm});
            skLineSegment(sketch, "E3887", {"start": v(87.96, 4.57) * mm, "end": v(88.52, 4.46) * mm});
            skLineSegment(sketch, "E3888", {"start": v(88.52, 4.46) * mm, "end": v(89.05, 4.34) * mm});
            skLineSegment(sketch, "E3889", {"start": v(89.05, 4.34) * mm, "end": v(89.53, 4.2) * mm});
            skLineSegment(sketch, "E3890", {"start": v(89.53, 4.2) * mm, "end": v(89.98, 4.02) * mm});
            skLineSegment(sketch, "E3891", {"start": v(89.98, 4.02) * mm, "end": v(90.39, 3.82) * mm});
            skLineSegment(sketch, "E3892", {"start": v(90.39, 3.82) * mm, "end": v(90.76, 3.6) * mm});
            skLineSegment(sketch, "E3893", {"start": v(90.76, 3.6) * mm, "end": v(91.1, 3.35) * mm});
            skLineSegment(sketch, "E3894", {"start": v(91.1, 3.35) * mm, "end": v(91.4, 3.07) * mm});
            skLineSegment(sketch, "E3895", {"start": v(91.4, 3.07) * mm, "end": v(91.66, 2.76) * mm});
            skLineSegment(sketch, "E3896", {"start": v(91.66, 2.76) * mm, "end": v(91.89, 2.42) * mm});
            skLineSegment(sketch, "E3897", {"start": v(91.89, 2.42) * mm, "end": v(92.09, 2.08) * mm});
            skLineSegment(sketch, "E3898", {"start": v(92.09, 2.08) * mm, "end": v(92.27, 1.74) * mm});
            skLineSegment(sketch, "E3899", {"start": v(92.27, 1.74) * mm, "end": v(92.43, 1.42) * mm});
            skLineSegment(sketch, "E3900", {"start": v(92.43, 1.42) * mm, "end": v(92.57, 1.1) * mm});
            skLineSegment(sketch, "E3901", {"start": v(92.57, 1.1) * mm, "end": v(92.7, 0.79) * mm});
            skLineSegment(sketch, "E3902", {"start": v(92.7, 0.79) * mm, "end": v(92.8, 0.49) * mm});
            skLineSegment(sketch, "E3903", {"start": v(92.8, 0.49) * mm, "end": v(92.89, 0.2) * mm});
            skLineSegment(sketch, "E3904", {"start": v(92.89, 0.2) * mm, "end": v(92.95, -0.09) * mm});
            skLineSegment(sketch, "E3905", {"start": v(92.95, -0.09) * mm, "end": v(93, -0.45) * mm});
            skLineSegment(sketch, "E3906", {"start": v(93, -0.45) * mm, "end": v(93.05, -0.95) * mm});
            skLineSegment(sketch, "E3907", {"start": v(93.05, -0.95) * mm, "end": v(93.1, -1.55) * mm});
            skLineSegment(sketch, "E3908", {"start": v(93.1, -1.55) * mm, "end": v(93.13, -2.21) * mm});
            skLineSegment(sketch, "E3909", {"start": v(93.13, -2.21) * mm, "end": v(93.15, -2.9) * mm});
            skLineSegment(sketch, "E3910", {"start": v(93.15, -2.9) * mm, "end": v(93.17, -3.58) * mm});
            skLineSegment(sketch, "E3911", {"start": v(93.17, -3.58) * mm, "end": v(93.18, -4.21) * mm});
            skLineSegment(sketch, "E3912", {"start": v(93.18, -4.21) * mm, "end": v(93.19, -4.76) * mm});
            skLineSegment(sketch, "E3913", {"start": v(93.19, -4.76) * mm, "end": v(93.1, -4.59) * mm});
            skLineSegment(sketch, "E3914", {"start": v(93.1, -4.59) * mm, "end": v(92.79, -4.13) * mm});
            skLineSegment(sketch, "E3915", {"start": v(92.79, -4.13) * mm, "end": v(92.2, -3.5) * mm});
            skLineSegment(sketch, "E3916", {"start": v(92.2, -3.5) * mm, "end": v(91.24, -2.75) * mm});
            skLineSegment(sketch, "E3917", {"start": v(91.24, -2.75) * mm, "end": v(89.85, -2.02) * mm});
            skLineSegment(sketch, "E3918", {"start": v(89.85, -2.02) * mm, "end": v(87.98, -1.37) * mm});
            skLineSegment(sketch, "E3919", {"start": v(87.98, -1.37) * mm, "end": v(85.54, -0.92) * mm});
            skLineSegment(sketch, "E3920", {"start": v(85.54, -0.92) * mm, "end": v(82.47, -0.75) * mm});
            skLineSegment(sketch, "E3921", {"start": v(82.47, -0.75) * mm, "end": v(82, -0.74) * mm});
            skLineSegment(sketch, "E3922", {"start": v(82, -0.74) * mm, "end": v(81.53, -0.74) * mm});
            skLineSegment(sketch, "E3923", {"start": v(81.53, -0.74) * mm, "end": v(81.05, -0.73) * mm});
            skLineSegment(sketch, "E3924", {"start": v(81.05, -0.73) * mm, "end": v(80.58, -0.73) * mm});
            skLineSegment(sketch, "E3925", {"start": v(80.58, -0.73) * mm, "end": v(80.1, -0.72) * mm});
            skLineSegment(sketch, "E3926", {"start": v(80.1, -0.72) * mm, "end": v(79.63, -0.72) * mm});
            skLineSegment(sketch, "E3927", {"start": v(79.63, -0.72) * mm, "end": v(79.16, -0.71) * mm});
            skLineSegment(sketch, "E3928", {"start": v(79.16, -0.71) * mm, "end": v(78.68, -0.7) * mm});
            skLineSegment(sketch, "E3929", {"start": v(78.68, -0.7) * mm, "end": v(77.93, -0.73) * mm});
            skLineSegment(sketch, "E3930", {"start": v(77.93, -0.73) * mm, "end": v(77.19, -0.76) * mm});
            skLineSegment(sketch, "E3931", {"start": v(77.19, -0.76) * mm, "end": v(76.44, -0.78) * mm});
            skLineSegment(sketch, "E3932", {"start": v(76.44, -0.78) * mm, "end": v(75.69, -0.8) * mm});
            skLineSegment(sketch, "E3933", {"start": v(75.69, -0.8) * mm, "end": v(74.94, -0.83) * mm});
            skLineSegment(sketch, "E3934", {"start": v(74.94, -0.83) * mm, "end": v(74.19, -0.85) * mm});
            skLineSegment(sketch, "E3935", {"start": v(74.19, -0.85) * mm, "end": v(73.44, -0.88) * mm});
            skLineSegment(sketch, "E3936", {"start": v(73.44, -0.88) * mm, "end": v(72.69, -0.9) * mm});
            skLineSegment(sketch, "E3937", {"start": v(72.69, -0.9) * mm, "end": v(72.4, -0.9) * mm});
            skLineSegment(sketch, "E3938", {"start": v(72.4, -0.9) * mm, "end": v(72.11, -0.93) * mm});
            skLineSegment(sketch, "E3939", {"start": v(72.11, -0.93) * mm, "end": v(71.84, -0.96) * mm});
            skLineSegment(sketch, "E3940", {"start": v(71.84, -0.96) * mm, "end": v(71.58, -1.01) * mm});
            skLineSegment(sketch, "E3941", {"start": v(71.58, -1.01) * mm, "end": v(71.33, -1.08) * mm});
            skLineSegment(sketch, "E3942", {"start": v(71.33, -1.08) * mm, "end": v(71.1, -1.15) * mm});
            skLineSegment(sketch, "E3943", {"start": v(71.1, -1.15) * mm, "end": v(70.87, -1.24) * mm});
            skLineSegment(sketch, "E3944", {"start": v(70.87, -1.24) * mm, "end": v(70.66, -1.35) * mm});
            skLineSegment(sketch, "E3945", {"start": v(70.66, -1.35) * mm, "end": v(70.46, -1.47) * mm});
            skLineSegment(sketch, "E3946", {"start": v(70.46, -1.47) * mm, "end": v(70.3, -1.6) * mm});
            skLineSegment(sketch, "E3947", {"start": v(70.3, -1.6) * mm, "end": v(70.15, -1.77) * mm});
            skLineSegment(sketch, "E3948", {"start": v(70.15, -1.77) * mm, "end": v(70.04, -1.94) * mm});
            skLineSegment(sketch, "E3949", {"start": v(70.04, -1.94) * mm, "end": v(69.95, -2.14) * mm});
            skLineSegment(sketch, "E3950", {"start": v(69.95, -2.14) * mm, "end": v(69.88, -2.35) * mm});
            skLineSegment(sketch, "E3951", {"start": v(69.88, -2.35) * mm, "end": v(69.84, -2.58) * mm});
            skLineSegment(sketch, "E3952", {"start": v(69.84, -2.58) * mm, "end": v(69.83, -2.84) * mm});
            skLineSegment(sketch, "E3953", {"start": v(69.83, -2.84) * mm, "end": v(69.84, -3.18) * mm});
            skLineSegment(sketch, "E3954", {"start": v(69.84, -3.18) * mm, "end": v(69.9, -3.49) * mm});
            skLineSegment(sketch, "E3955", {"start": v(69.9, -3.49) * mm, "end": v(69.97, -3.77) * mm});
            skLineSegment(sketch, "E3956", {"start": v(69.97, -3.77) * mm, "end": v(70.08, -4.02) * mm});
            skLineSegment(sketch, "E3957", {"start": v(70.08, -4.02) * mm, "end": v(70.21, -4.24) * mm});
            skLineSegment(sketch, "E3958", {"start": v(70.21, -4.24) * mm, "end": v(70.38, -4.43) * mm});
            skLineSegment(sketch, "E3959", {"start": v(70.38, -4.43) * mm, "end": v(70.58, -4.58) * mm});
            skLineSegment(sketch, "E3960", {"start": v(70.58, -4.58) * mm, "end": v(70.81, -4.71) * mm});
            skLineSegment(sketch, "E3961", {"start": v(70.81, -4.71) * mm, "end": v(71.07, -4.82) * mm});
            skLineSegment(sketch, "E3962", {"start": v(71.07, -4.82) * mm, "end": v(71.35, -4.9) * mm});
            skLineSegment(sketch, "E3963", {"start": v(71.35, -4.9) * mm, "end": v(71.65, -4.98) * mm});
            skLineSegment(sketch, "E3964", {"start": v(71.65, -4.98) * mm, "end": v(71.98, -5.04) * mm});
            skLineSegment(sketch, "E3965", {"start": v(71.98, -5.04) * mm, "end": v(72.33, -5.1) * mm});
            skLineSegment(sketch, "E3966", {"start": v(72.33, -5.1) * mm, "end": v(72.7, -5.13) * mm});
            skLineSegment(sketch, "E3967", {"start": v(72.7, -5.13) * mm, "end": v(73.09, -5.15) * mm});
            skLineSegment(sketch, "E3968", {"start": v(73.09, -5.15) * mm, "end": v(73.5, -5.16) * mm});
            skLineSegment(sketch, "E3969", {"start": v(73.5, -5.16) * mm, "end": v(73.6, -5.16) * mm});
            skLineSegment(sketch, "E3970", {"start": v(73.6, -5.16) * mm, "end": v(73.7, -5.16) * mm});
            skLineSegment(sketch, "E3971", {"start": v(73.7, -5.16) * mm, "end": v(73.8, -5.16) * mm});
            skLineSegment(sketch, "E3972", {"start": v(73.8, -5.16) * mm, "end": v(73.9, -5.16) * mm});
            skLineSegment(sketch, "E3973", {"start": v(73.9, -5.16) * mm, "end": v(74, -5.16) * mm});
            skLineSegment(sketch, "E3974", {"start": v(74, -5.16) * mm, "end": v(74.1, -5.16) * mm});
            skLineSegment(sketch, "E3975", {"start": v(74.1, -5.16) * mm, "end": v(74.21, -5.16) * mm});
            skLineSegment(sketch, "E3976", {"start": v(74.21, -5.16) * mm, "end": v(74.31, -5.16) * mm});
            skLineSegment(sketch, "E3977", {"start": v(74.31, -5.16) * mm, "end": v(74.97, -5.17) * mm});
            skLineSegment(sketch, "E3978", {"start": v(74.97, -5.17) * mm, "end": v(75.63, -5.18) * mm});
            skLineSegment(sketch, "E3979", {"start": v(75.63, -5.18) * mm, "end": v(76.28, -5.19) * mm});
            skLineSegment(sketch, "E3980", {"start": v(76.28, -5.19) * mm, "end": v(76.94, -5.2) * mm});
            skLineSegment(sketch, "E3981", {"start": v(76.94, -5.2) * mm, "end": v(77.6, -5.2) * mm});
            skLineSegment(sketch, "E3982", {"start": v(77.6, -5.2) * mm, "end": v(78.26, -5.21) * mm});
            skLineSegment(sketch, "E3983", {"start": v(78.26, -5.21) * mm, "end": v(78.92, -5.22) * mm});
            skLineSegment(sketch, "E3984", {"start": v(78.92, -5.22) * mm, "end": v(79.57, -5.23) * mm});
            skLineSegment(sketch, "E3985", {"start": v(79.57, -5.23) * mm, "end": v(80.22, -5.24) * mm});
            skLineSegment(sketch, "E3986", {"start": v(80.22, -5.24) * mm, "end": v(80.87, -5.24) * mm});
            skLineSegment(sketch, "E3987", {"start": v(80.87, -5.24) * mm, "end": v(81.52, -5.25) * mm});
            skLineSegment(sketch, "E3988", {"start": v(81.52, -5.25) * mm, "end": v(82.16, -5.25) * mm});
            skLineSegment(sketch, "E3989", {"start": v(82.16, -5.25) * mm, "end": v(82.81, -5.26) * mm});
            skLineSegment(sketch, "E3990", {"start": v(82.81, -5.26) * mm, "end": v(83.46, -5.26) * mm});
            skLineSegment(sketch, "E3991", {"start": v(83.46, -5.26) * mm, "end": v(84.1, -5.27) * mm});
            skLineSegment(sketch, "E3992", {"start": v(84.1, -5.27) * mm, "end": v(84.75, -5.27) * mm});
            skLineSegment(sketch, "E3993", {"start": v(84.75, -5.27) * mm, "end": v(85.96, -5.3) * mm});
            skLineSegment(sketch, "E3994", {"start": v(85.96, -5.3) * mm, "end": v(87.08, -5.37) * mm});
            skLineSegment(sketch, "E3995", {"start": v(87.08, -5.37) * mm, "end": v(88.11, -5.5) * mm});
            skLineSegment(sketch, "E3996", {"start": v(88.11, -5.5) * mm, "end": v(89.06, -5.66) * mm});
            skLineSegment(sketch, "E3997", {"start": v(89.06, -5.66) * mm, "end": v(89.93, -5.88) * mm});
            skLineSegment(sketch, "E3998", {"start": v(89.93, -5.88) * mm, "end": v(90.7, -6.15) * mm});
            skLineSegment(sketch, "E3999", {"start": v(90.7, -6.15) * mm, "end": v(91.4, -6.47) * mm});
            skLineSegment(sketch, "E4000", {"start": v(91.4, -6.47) * mm, "end": v(92, -6.84) * mm});
            skLineSegment(sketch, "E4001", {"start": v(92, -6.84) * mm, "end": v(92.54, -7.28) * mm});
            skLineSegment(sketch, "E4002", {"start": v(92.54, -7.28) * mm, "end": v(93, -7.82) * mm});
            skLineSegment(sketch, "E4003", {"start": v(93, -7.82) * mm, "end": v(93.38, -8.46) * mm});
            skLineSegment(sketch, "E4004", {"start": v(93.38, -8.46) * mm, "end": v(93.7, -9.2) * mm});
            skLineSegment(sketch, "E4005", {"start": v(93.7, -9.2) * mm, "end": v(93.95, -10.03) * mm});
            skLineSegment(sketch, "E4006", {"start": v(93.95, -10.03) * mm, "end": v(94.13, -10.96) * mm});
            skLineSegment(sketch, "E4007", {"start": v(94.13, -10.96) * mm, "end": v(94.23, -12) * mm});
            skLineSegment(sketch, "E4008", {"start": v(94.23, -12) * mm, "end": v(94.27, -13.12) * mm});
            skLineSegment(sketch, "E4009", {"start": v(94.27, -13.12) * mm, "end": v(94.24, -14.22) * mm});
            skLineSegment(sketch, "E4010", {"start": v(94.24, -14.22) * mm, "end": v(94.14, -15.22) * mm});
            skLineSegment(sketch, "E4011", {"start": v(94.14, -15.22) * mm, "end": v(93.98, -16.14) * mm});
            skLineSegment(sketch, "E4012", {"start": v(93.98, -16.14) * mm, "end": v(93.76, -16.97) * mm});
            skLineSegment(sketch, "E4013", {"start": v(93.76, -16.97) * mm, "end": v(93.48, -17.7) * mm});
            skLineSegment(sketch, "E4014", {"start": v(93.48, -17.7) * mm, "end": v(93.13, -18.36) * mm});
            skLineSegment(sketch, "E4015", {"start": v(93.13, -18.36) * mm, "end": v(92.71, -18.92) * mm});
            skLineSegment(sketch, "E4016", {"start": v(92.71, -18.92) * mm, "end": v(92.24, -19.39) * mm});
            skLineSegment(sketch, "E4017", {"start": v(92.24, -19.39) * mm, "end": v(91.69, -19.79) * mm});
            skLineSegment(sketch, "E4018", {"start": v(91.69, -19.79) * mm, "end": v(91.06, -20.13) * mm});
            skLineSegment(sketch, "E4019", {"start": v(91.06, -20.13) * mm, "end": v(90.34, -20.42) * mm});
            skLineSegment(sketch, "E4020", {"start": v(90.34, -20.42) * mm, "end": v(89.55, -20.66) * mm});
            skLineSegment(sketch, "E4021", {"start": v(89.55, -20.66) * mm, "end": v(88.67, -20.85) * mm});
            skLineSegment(sketch, "E4022", {"start": v(88.67, -20.85) * mm, "end": v(87.7, -20.98) * mm});
            skLineSegment(sketch, "E4023", {"start": v(87.7, -20.98) * mm, "end": v(86.66, -21.06) * mm});
            skLineSegment(sketch, "E4024", {"start": v(86.66, -21.06) * mm, "end": v(85.53, -21.09) * mm});
            skLineSegment(sketch, "E4025", {"start": v(85.53, -21.09) * mm, "end": v(84.27, -21.12) * mm});
            skLineSegment(sketch, "E4026", {"start": v(84.27, -21.12) * mm, "end": v(83.01, -21.16) * mm});
            skLineSegment(sketch, "E4027", {"start": v(83.01, -21.16) * mm, "end": v(81.76, -21.2) * mm});
            skLineSegment(sketch, "E4028", {"start": v(81.76, -21.2) * mm, "end": v(80.5, -21.22) * mm});
            skLineSegment(sketch, "E4029", {"start": v(80.5, -21.22) * mm, "end": v(79.24, -21.26) * mm});
            skLineSegment(sketch, "E4030", {"start": v(79.24, -21.26) * mm, "end": v(77.99, -21.3) * mm});
            skLineSegment(sketch, "E4031", {"start": v(77.99, -21.3) * mm, "end": v(76.73, -21.33) * mm});
            skLineSegment(sketch, "E4032", {"start": v(76.73, -21.33) * mm, "end": v(75.47, -21.36) * mm});
            skLineSegment(sketch, "E4033", {"start": v(75.47, -21.36) * mm, "end": v(74.82, -21.35) * mm});
            skLineSegment(sketch, "E4034", {"start": v(74.82, -21.35) * mm, "end": v(74.16, -21.33) * mm});
            skLineSegment(sketch, "E4035", {"start": v(74.16, -21.33) * mm, "end": v(73.5, -21.32) * mm});
            skLineSegment(sketch, "E4036", {"start": v(73.5, -21.32) * mm, "end": v(72.84, -21.3) * mm});
            skLineSegment(sketch, "E4037", {"start": v(72.84, -21.3) * mm, "end": v(72.19, -21.29) * mm});
            skLineSegment(sketch, "E4038", {"start": v(72.19, -21.29) * mm, "end": v(71.53, -21.27) * mm});
            skLineSegment(sketch, "E4039", {"start": v(71.53, -21.27) * mm, "end": v(70.87, -21.26) * mm});
            skLineSegment(sketch, "E4040", {"start": v(70.87, -21.26) * mm, "end": v(70.21, -21.24) * mm});
            skLineSegment(sketch, "E4041", {"start": v(70.21, -21.24) * mm, "end": v(69.2, -21.22) * mm});
            skLineSegment(sketch, "E4042", {"start": v(69.2, -21.22) * mm, "end": v(68.27, -21.16) * mm});
            skLineSegment(sketch, "E4043", {"start": v(68.27, -21.16) * mm, "end": v(67.4, -21.05) * mm});
            skLineSegment(sketch, "E4044", {"start": v(67.4, -21.05) * mm, "end": v(66.6, -20.9) * mm});
            skLineSegment(sketch, "E4045", {"start": v(66.6, -20.9) * mm, "end": v(65.86, -20.71) * mm});
            skLineSegment(sketch, "E4046", {"start": v(65.86, -20.71) * mm, "end": v(65.2, -20.48) * mm});
            skLineSegment(sketch, "E4047", {"start": v(65.2, -20.48) * mm, "end": v(64.6, -20.2) * mm});
            skLineSegment(sketch, "E4048", {"start": v(64.6, -20.2) * mm, "end": v(64.07, -19.89) * mm});
            skLineSegment(sketch, "E4049", {"start": v(64.07, -19.89) * mm, "end": v(63.6, -19.5) * mm});
            skLineSegment(sketch, "E4050", {"start": v(63.6, -19.5) * mm, "end": v(63.2, -19.04) * mm});
            skLineSegment(sketch, "E4051", {"start": v(63.2, -19.04) * mm, "end": v(62.86, -18.49) * mm});
            skLineSegment(sketch, "E4052", {"start": v(62.86, -18.49) * mm, "end": v(62.59, -17.85) * mm});
            skLineSegment(sketch, "E4053", {"start": v(62.59, -17.85) * mm, "end": v(62.37, -17.13) * mm});
            skLineSegment(sketch, "E4054", {"start": v(62.37, -17.13) * mm, "end": v(62.22, -16.32) * mm});
            skLineSegment(sketch, "E4055", {"start": v(62.22, -16.32) * mm, "end": v(62.12, -15.42) * mm});
            skLineSegment(sketch, "E4056", {"start": v(62.12, -15.42) * mm, "end": v(62.1, -14.44) * mm});
            skLineSegment(sketch, "E4057", {"start": v(62.1, -14.44) * mm, "end": v(62.1, -14.11) * mm});
            skLineSegment(sketch, "E4058", {"start": v(62.1, -14.11) * mm, "end": v(62.1, -13.8) * mm});
            skLineSegment(sketch, "E4059", {"start": v(62.1, -13.8) * mm, "end": v(62.1, -13.47) * mm});
            skLineSegment(sketch, "E4060", {"start": v(62.1, -13.47) * mm, "end": v(62.1, -13.15) * mm});
            skLineSegment(sketch, "E4061", {"start": v(62.1, -13.15) * mm, "end": v(62.1, -12.83) * mm});
            skLineSegment(sketch, "E4062", {"start": v(62.1, -12.83) * mm, "end": v(62.1, -12.5) * mm});
            skLineSegment(sketch, "E4063", {"start": v(62.1, -12.5) * mm, "end": v(62.1, -12.18) * mm});
            skLineSegment(sketch, "E4064", {"start": v(62.1, -12.18) * mm, "end": v(62.1, -11.86) * mm});
            skLineSegment(sketch, "E4065", {"start": v(62.1, -11.86) * mm, "end": v(62.19, -12.03) * mm});
            skLineSegment(sketch, "E4066", {"start": v(62.19, -12.03) * mm, "end": v(62.53, -12.46) * mm});
            skLineSegment(sketch, "E4067", {"start": v(62.53, -12.46) * mm, "end": v(63.18, -13.08) * mm});
            skLineSegment(sketch, "E4068", {"start": v(63.18, -13.08) * mm, "end": v(64.23, -13.79) * mm});
            skLineSegment(sketch, "E4069", {"start": v(64.23, -13.79) * mm, "end": v(65.75, -14.5) * mm});
            skLineSegment(sketch, "E4070", {"start": v(65.75, -14.5) * mm, "end": v(67.81, -15.11) * mm});
            skLineSegment(sketch, "E4071", {"start": v(67.81, -15.11) * mm, "end": v(70.5, -15.55) * mm});
            skLineSegment(sketch, "E4072", {"start": v(70.5, -15.55) * mm, "end": v(73.89, -15.71) * mm});
            skLineSegment(sketch, "E4073", {"start": v(63.58, -15.1) * mm, "end": v(63.61, -15.63) * mm});
            skLineSegment(sketch, "E4074", {"start": v(63.61, -15.63) * mm, "end": v(63.68, -16.15) * mm});
            skLineSegment(sketch, "E4075", {"start": v(63.68, -16.15) * mm, "end": v(63.77, -16.67) * mm});
            skLineSegment(sketch, "E4076", {"start": v(63.77, -16.67) * mm, "end": v(63.9, -17.17) * mm});
            skLineSegment(sketch, "E4077", {"start": v(63.9, -17.17) * mm, "end": v(64.08, -17.63) * mm});
            skLineSegment(sketch, "E4078", {"start": v(64.08, -17.63) * mm, "end": v(64.3, -18.04) * mm});
            skLineSegment(sketch, "E4079", {"start": v(64.3, -18.04) * mm, "end": v(64.57, -18.4) * mm});
            skLineSegment(sketch, "E4080", {"start": v(64.57, -18.4) * mm, "end": v(64.9, -18.68) * mm});
            skLineSegment(sketch, "E4081", {"start": v(64.9, -18.68) * mm, "end": v(65.33, -18.94) * mm});
            skLineSegment(sketch, "E4082", {"start": v(65.33, -18.94) * mm, "end": v(65.83, -19.16) * mm});
            skLineSegment(sketch, "E4083", {"start": v(65.83, -19.16) * mm, "end": v(66.4, -19.35) * mm});
            skLineSegment(sketch, "E4084", {"start": v(66.4, -19.35) * mm, "end": v(67.03, -19.5) * mm});
            skLineSegment(sketch, "E4085", {"start": v(67.03, -19.5) * mm, "end": v(67.73, -19.62) * mm});
            skLineSegment(sketch, "E4086", {"start": v(67.73, -19.62) * mm, "end": v(68.5, -19.7) * mm});
            skLineSegment(sketch, "E4087", {"start": v(68.5, -19.7) * mm, "end": v(69.32, -19.76) * mm});
            skLineSegment(sketch, "E4088", {"start": v(69.32, -19.76) * mm, "end": v(70.21, -19.78) * mm});
            skLineSegment(sketch, "E4089", {"start": v(70.21, -19.78) * mm, "end": v(70.87, -19.8) * mm});
            skLineSegment(sketch, "E4090", {"start": v(70.87, -19.8) * mm, "end": v(71.53, -19.8) * mm});
            skLineSegment(sketch, "E4091", {"start": v(71.53, -19.8) * mm, "end": v(72.19, -19.82) * mm});
            skLineSegment(sketch, "E4092", {"start": v(72.19, -19.82) * mm, "end": v(72.84, -19.83) * mm});
            skLineSegment(sketch, "E4093", {"start": v(72.84, -19.83) * mm, "end": v(73.5, -19.85) * mm});
            skLineSegment(sketch, "E4094", {"start": v(73.5, -19.85) * mm, "end": v(74.16, -19.86) * mm});
            skLineSegment(sketch, "E4095", {"start": v(74.16, -19.86) * mm, "end": v(74.81, -19.88) * mm});
            skLineSegment(sketch, "E4096", {"start": v(74.81, -19.88) * mm, "end": v(75.47, -19.9) * mm});
            skLineSegment(sketch, "E4097", {"start": v(75.47, -19.9) * mm, "end": v(76.72, -19.86) * mm});
            skLineSegment(sketch, "E4098", {"start": v(76.72, -19.86) * mm, "end": v(77.97, -19.82) * mm});
            skLineSegment(sketch, "E4099", {"start": v(77.97, -19.82) * mm, "end": v(79.23, -19.8) * mm});
            skLineSegment(sketch, "E4100", {"start": v(79.23, -19.8) * mm, "end": v(80.48, -19.76) * mm});
            skLineSegment(sketch, "E4101", {"start": v(80.48, -19.76) * mm, "end": v(81.73, -19.72) * mm});
            skLineSegment(sketch, "E4102", {"start": v(81.73, -19.72) * mm, "end": v(82.98, -19.69) * mm});
            skLineSegment(sketch, "E4103", {"start": v(82.98, -19.69) * mm, "end": v(84.24, -19.66) * mm});
            skLineSegment(sketch, "E4104", {"start": v(84.24, -19.66) * mm, "end": v(85.49, -19.62) * mm});
            skLineSegment(sketch, "E4105", {"start": v(85.49, -19.62) * mm, "end": v(85.5, -19.62) * mm});
            skLineSegment(sketch, "E4106", {"start": v(85.5, -19.62) * mm, "end": v(85.5, -19.62) * mm});
            skLineSegment(sketch, "E4107", {"start": v(85.5, -19.62) * mm, "end": v(85.51, -19.62) * mm});
            skLineSegment(sketch, "E4108", {"start": v(85.51, -19.62) * mm, "end": v(85.52, -19.62) * mm});
            skLineSegment(sketch, "E4109", {"start": v(85.52, -19.62) * mm, "end": v(85.52, -19.62) * mm});
            skLineSegment(sketch, "E4110", {"start": v(85.52, -19.62) * mm, "end": v(85.53, -19.62) * mm});
            skLineSegment(sketch, "E4111", {"start": v(85.53, -19.62) * mm, "end": v(86.51, -19.6) * mm});
            skLineSegment(sketch, "E4112", {"start": v(86.51, -19.6) * mm, "end": v(87.42, -19.53) * mm});
            skLineSegment(sketch, "E4113", {"start": v(87.42, -19.53) * mm, "end": v(88.27, -19.43) * mm});
            skLineSegment(sketch, "E4114", {"start": v(88.27, -19.43) * mm, "end": v(89.03, -19.28) * mm});
            skLineSegment(sketch, "E4115", {"start": v(89.03, -19.28) * mm, "end": v(89.72, -19.08) * mm});
            skLineSegment(sketch, "E4116", {"start": v(89.72, -19.08) * mm, "end": v(90.33, -18.85) * mm});
            skLineSegment(sketch, "E4117", {"start": v(90.33, -18.85) * mm, "end": v(90.85, -18.58) * mm});
            skLineSegment(sketch, "E4118", {"start": v(90.85, -18.58) * mm, "end": v(91.3, -18.26) * mm});
            skLineSegment(sketch, "E4119", {"start": v(91.3, -18.26) * mm, "end": v(91.64, -17.9) * mm});
            skLineSegment(sketch, "E4120", {"start": v(91.64, -17.9) * mm, "end": v(91.95, -17.47) * mm});
            skLineSegment(sketch, "E4121", {"start": v(91.95, -17.47) * mm, "end": v(92.2, -16.94) * mm});
            skLineSegment(sketch, "E4122", {"start": v(92.2, -16.94) * mm, "end": v(92.42, -16.33) * mm});
            skLineSegment(sketch, "E4123", {"start": v(92.42, -16.33) * mm, "end": v(92.58, -15.65) * mm});
            skLineSegment(sketch, "E4124", {"start": v(92.58, -15.65) * mm, "end": v(92.7, -14.88) * mm});
            skLineSegment(sketch, "E4125", {"start": v(92.7, -14.88) * mm, "end": v(92.78, -14.04) * mm});
            skLineSegment(sketch, "E4126", {"start": v(92.78, -14.04) * mm, "end": v(92.8, -13.12) * mm});
            skLineSegment(sketch, "E4127", {"start": v(92.8, -13.12) * mm, "end": v(92.79, -12.42) * mm});
            skLineSegment(sketch, "E4128", {"start": v(92.79, -12.42) * mm, "end": v(92.74, -11.7) * mm});
            skLineSegment(sketch, "E4129", {"start": v(92.74, -11.7) * mm, "end": v(92.64, -10.97) * mm});
            skLineSegment(sketch, "E4130", {"start": v(92.64, -10.97) * mm, "end": v(92.5, -10.26) * mm});
            skLineSegment(sketch, "E4131", {"start": v(92.5, -10.26) * mm, "end": v(92.28, -9.59) * mm});
            skLineSegment(sketch, "E4132", {"start": v(92.28, -9.59) * mm, "end": v(92, -8.98) * mm});
            skLineSegment(sketch, "E4133", {"start": v(92, -8.98) * mm, "end": v(91.63, -8.46) * mm});
            skLineSegment(sketch, "E4134", {"start": v(91.63, -8.46) * mm, "end": v(91.17, -8.05) * mm});
            skLineSegment(sketch, "E4135", {"start": v(91.17, -8.05) * mm, "end": v(90.66, -7.74) * mm});
            skLineSegment(sketch, "E4136", {"start": v(90.66, -7.74) * mm, "end": v(90.06, -7.48) * mm});
            skLineSegment(sketch, "E4137", {"start": v(90.06, -7.48) * mm, "end": v(89.38, -7.25) * mm});
            skLineSegment(sketch, "E4138", {"start": v(89.38, -7.25) * mm, "end": v(88.62, -7.07) * mm});
            skLineSegment(sketch, "E4139", {"start": v(88.62, -7.07) * mm, "end": v(87.78, -6.92) * mm});
            skLineSegment(sketch, "E4140", {"start": v(87.78, -6.92) * mm, "end": v(86.85, -6.82) * mm});
            skLineSegment(sketch, "E4141", {"start": v(86.85, -6.82) * mm, "end": v(85.84, -6.76) * mm});
            skLineSegment(sketch, "E4142", {"start": v(85.84, -6.76) * mm, "end": v(84.75, -6.74) * mm});
            skLineSegment(sketch, "E4143", {"start": v(84.75, -6.74) * mm, "end": v(84.1, -6.73) * mm});
            skLineSegment(sketch, "E4144", {"start": v(84.1, -6.73) * mm, "end": v(83.46, -6.73) * mm});
            skLineSegment(sketch, "E4145", {"start": v(83.46, -6.73) * mm, "end": v(82.8, -6.72) * mm});
            skLineSegment(sketch, "E4146", {"start": v(82.8, -6.72) * mm, "end": v(82.16, -6.72) * mm});
            skLineSegment(sketch, "E4147", {"start": v(82.16, -6.72) * mm, "end": v(81.51, -6.71) * mm});
            skLineSegment(sketch, "E4148", {"start": v(81.51, -6.71) * mm, "end": v(80.86, -6.71) * mm});
            skLineSegment(sketch, "E4149", {"start": v(80.86, -6.71) * mm, "end": v(80.21, -6.7) * mm});
            skLineSegment(sketch, "E4150", {"start": v(80.21, -6.7) * mm, "end": v(79.56, -6.7) * mm});
            skLineSegment(sketch, "E4151", {"start": v(79.56, -6.7) * mm, "end": v(78.8, -6.7) * mm});
            skLineSegment(sketch, "E4152", {"start": v(78.8, -6.7) * mm, "end": v(78.05, -6.68) * mm});
            skLineSegment(sketch, "E4153", {"start": v(78.05, -6.68) * mm, "end": v(77.3, -6.67) * mm});
            skLineSegment(sketch, "E4154", {"start": v(77.3, -6.67) * mm, "end": v(76.53, -6.66) * mm});
            skLineSegment(sketch, "E4155", {"start": v(76.53, -6.66) * mm, "end": v(75.78, -6.65) * mm});
            skLineSegment(sketch, "E4156", {"start": v(75.78, -6.65) * mm, "end": v(75.02, -6.64) * mm});
            skLineSegment(sketch, "E4157", {"start": v(75.02, -6.64) * mm, "end": v(74.26, -6.63) * mm});
            skLineSegment(sketch, "E4158", {"start": v(74.26, -6.63) * mm, "end": v(73.5, -6.62) * mm});
            skLineSegment(sketch, "E4159", {"start": v(73.5, -6.62) * mm, "end": v(73, -6.61) * mm});
            skLineSegment(sketch, "E4160", {"start": v(73, -6.61) * mm, "end": v(72.54, -6.59) * mm});
            skLineSegment(sketch, "E4161", {"start": v(72.54, -6.59) * mm, "end": v(72.1, -6.54) * mm});
            skLineSegment(sketch, "E4162", {"start": v(72.1, -6.54) * mm, "end": v(71.67, -6.48) * mm});
            skLineSegment(sketch, "E4163", {"start": v(71.67, -6.48) * mm, "end": v(71.27, -6.4) * mm});
            skLineSegment(sketch, "E4164", {"start": v(71.27, -6.4) * mm, "end": v(70.9, -6.3) * mm});
            skLineSegment(sketch, "E4165", {"start": v(70.9, -6.3) * mm, "end": v(70.54, -6.19) * mm});
            skLineSegment(sketch, "E4166", {"start": v(70.54, -6.19) * mm, "end": v(70.21, -6.05) * mm});
            skLineSegment(sketch, "E4167", {"start": v(70.21, -6.05) * mm, "end": v(69.93, -5.9) * mm});
            skLineSegment(sketch, "E4168", {"start": v(69.93, -5.9) * mm, "end": v(69.63, -5.7) * mm});
            skLineSegment(sketch, "E4169", {"start": v(69.63, -5.7) * mm, "end": v(69.32, -5.44) * mm});
            skLineSegment(sketch, "E4170", {"start": v(69.32, -5.44) * mm, "end": v(69.03, -5.1) * mm});
            skLineSegment(sketch, "E4171", {"start": v(69.03, -5.1) * mm, "end": v(68.76, -4.68) * mm});
            skLineSegment(sketch, "E4172", {"start": v(68.76, -4.68) * mm, "end": v(68.55, -4.17) * mm});
            skLineSegment(sketch, "E4173", {"start": v(68.55, -4.17) * mm, "end": v(68.41, -3.55) * mm});
            skLineSegment(sketch, "E4174", {"start": v(68.41, -3.55) * mm, "end": v(68.36, -2.84) * mm});
            skLineSegment(sketch, "E4175", {"start": v(68.36, -2.84) * mm, "end": v(68.39, -2.38) * mm});
            skLineSegment(sketch, "E4176", {"start": v(68.39, -2.38) * mm, "end": v(68.47, -1.96) * mm});
            skLineSegment(sketch, "E4177", {"start": v(68.47, -1.96) * mm, "end": v(68.6, -1.56) * mm});
            skLineSegment(sketch, "E4178", {"start": v(68.6, -1.56) * mm, "end": v(68.78, -1.19) * mm});
            skLineSegment(sketch, "E4179", {"start": v(68.78, -1.19) * mm, "end": v(69, -0.85) * mm});
            skLineSegment(sketch, "E4180", {"start": v(69, -0.85) * mm, "end": v(69.28, -0.55) * mm});
            skLineSegment(sketch, "E4181", {"start": v(69.28, -0.55) * mm, "end": v(69.6, -0.28) * mm});
            skLineSegment(sketch, "E4182", {"start": v(69.6, -0.28) * mm, "end": v(69.97, -0.05) * mm});
            skLineSegment(sketch, "E4183", {"start": v(69.97, -0.05) * mm, "end": v(70.26, 0.1) * mm});
            skLineSegment(sketch, "E4184", {"start": v(70.26, 0.1) * mm, "end": v(70.57, 0.22) * mm});
            skLineSegment(sketch, "E4185", {"start": v(70.57, 0.22) * mm, "end": v(70.89, 0.32) * mm});
            skLineSegment(sketch, "E4186", {"start": v(70.89, 0.32) * mm, "end": v(71.22, 0.4) * mm});
            skLineSegment(sketch, "E4187", {"start": v(71.22, 0.4) * mm, "end": v(71.56, 0.48) * mm});
            skLineSegment(sketch, "E4188", {"start": v(71.56, 0.48) * mm, "end": v(71.92, 0.53) * mm});
            skLineSegment(sketch, "E4189", {"start": v(71.92, 0.53) * mm, "end": v(72.29, 0.56) * mm});
            skLineSegment(sketch, "E4190", {"start": v(72.29, 0.56) * mm, "end": v(72.66, 0.57) * mm});
            skLineSegment(sketch, "E4191", {"start": v(72.66, 0.57) * mm, "end": v(73.41, 0.6) * mm});
            skLineSegment(sketch, "E4192", {"start": v(73.41, 0.6) * mm, "end": v(74.16, 0.61) * mm});
            skLineSegment(sketch, "E4193", {"start": v(74.16, 0.61) * mm, "end": v(74.9, 0.64) * mm});
            skLineSegment(sketch, "E4194", {"start": v(74.9, 0.64) * mm, "end": v(75.65, 0.66) * mm});
            skLineSegment(sketch, "E4195", {"start": v(75.65, 0.66) * mm, "end": v(76.4, 0.69) * mm});
            skLineSegment(sketch, "E4196", {"start": v(76.4, 0.69) * mm, "end": v(77.14, 0.71) * mm});
            skLineSegment(sketch, "E4197", {"start": v(77.14, 0.71) * mm, "end": v(77.9, 0.73) * mm});
            skLineSegment(sketch, "E4198", {"start": v(77.9, 0.73) * mm, "end": v(78.64, 0.76) * mm});
            skLineSegment(sketch, "E4199", {"start": v(78.64, 0.76) * mm, "end": v(78.65, 0.76) * mm});
            skLineSegment(sketch, "E4200", {"start": v(78.65, 0.76) * mm, "end": v(78.65, 0.76) * mm});
            skLineSegment(sketch, "E4201", {"start": v(78.65, 0.76) * mm, "end": v(78.66, 0.76) * mm});
            skLineSegment(sketch, "E4202", {"start": v(78.66, 0.76) * mm, "end": v(78.67, 0.76) * mm});
            skLineSegment(sketch, "E4203", {"start": v(78.67, 0.76) * mm, "end": v(78.68, 0.76) * mm});
            skLineSegment(sketch, "E4204", {"start": v(78.68, 0.76) * mm, "end": v(78.68, 0.76) * mm});
            skLineSegment(sketch, "E4205", {"start": v(78.68, 0.76) * mm, "end": v(78.7, 0.76) * mm});
            skLineSegment(sketch, "E4206", {"start": v(78.7, 0.76) * mm, "end": v(78.7, 0.76) * mm});
            skLineSegment(sketch, "E4207", {"start": v(78.7, 0.76) * mm, "end": v(79.17, 0.75) * mm});
            skLineSegment(sketch, "E4208", {"start": v(79.17, 0.75) * mm, "end": v(79.65, 0.75) * mm});
            skLineSegment(sketch, "E4209", {"start": v(79.65, 0.75) * mm, "end": v(80.12, 0.75) * mm});
            skLineSegment(sketch, "E4210", {"start": v(80.12, 0.75) * mm, "end": v(80.6, 0.74) * mm});
            skLineSegment(sketch, "E4211", {"start": v(80.6, 0.74) * mm, "end": v(81.07, 0.74) * mm});
            skLineSegment(sketch, "E4212", {"start": v(81.07, 0.74) * mm, "end": v(81.54, 0.73) * mm});
            skLineSegment(sketch, "E4213", {"start": v(81.54, 0.73) * mm, "end": v(82.01, 0.73) * mm});
            skLineSegment(sketch, "E4214", {"start": v(82.01, 0.73) * mm, "end": v(82.49, 0.72) * mm});
            skLineSegment(sketch, "E4215", {"start": v(82.49, 0.72) * mm, "end": v(84.08, 0.68) * mm});
            skLineSegment(sketch, "E4216", {"start": v(84.08, 0.68) * mm, "end": v(85.54, 0.56) * mm});
            skLineSegment(sketch, "E4217", {"start": v(85.54, 0.56) * mm, "end": v(86.85, 0.38) * mm});
            skLineSegment(sketch, "E4218", {"start": v(86.85, 0.38) * mm, "end": v(88.04, 0.13) * mm});
            skLineSegment(sketch, "E4219", {"start": v(88.04, 0.13) * mm, "end": v(89.1, -0.16) * mm});
            skLineSegment(sketch, "E4220", {"start": v(89.1, -0.16) * mm, "end": v(90.04, -0.5) * mm});
            skLineSegment(sketch, "E4221", {"start": v(90.04, -0.5) * mm, "end": v(90.88, -0.86) * mm});
            skLineSegment(sketch, "E4222", {"start": v(90.88, -0.86) * mm, "end": v(91.6, -1.25) * mm});
            skLineSegment(sketch, "E4223", {"start": v(91.6, -1.25) * mm, "end": v(91.6, -1.1) * mm});
            skLineSegment(sketch, "E4224", {"start": v(91.6, -1.1) * mm, "end": v(91.58, -0.97) * mm});
            skLineSegment(sketch, "E4225", {"start": v(91.58, -0.97) * mm, "end": v(91.57, -0.84) * mm});
            skLineSegment(sketch, "E4226", {"start": v(91.57, -0.84) * mm, "end": v(91.56, -0.72) * mm});
            skLineSegment(sketch, "E4227", {"start": v(91.56, -0.72) * mm, "end": v(91.55, -0.62) * mm});
            skLineSegment(sketch, "E4228", {"start": v(91.55, -0.62) * mm, "end": v(91.54, -0.53) * mm});
            skLineSegment(sketch, "E4229", {"start": v(91.54, -0.53) * mm, "end": v(91.53, -0.45) * mm});
            skLineSegment(sketch, "E4230", {"start": v(91.53, -0.45) * mm, "end": v(91.52, -0.38) * mm});
            skLineSegment(sketch, "E4231", {"start": v(91.52, -0.38) * mm, "end": v(91.46, -0.16) * mm});
            skLineSegment(sketch, "E4232", {"start": v(91.46, -0.16) * mm, "end": v(91.4, 0.07) * mm});
            skLineSegment(sketch, "E4233", {"start": v(91.4, 0.07) * mm, "end": v(91.3, 0.31) * mm});
            skLineSegment(sketch, "E4234", {"start": v(91.3, 0.31) * mm, "end": v(91.2, 0.57) * mm});
            skLineSegment(sketch, "E4235", {"start": v(91.2, 0.57) * mm, "end": v(91.08, 0.83) * mm});
            skLineSegment(sketch, "E4236", {"start": v(91.08, 0.83) * mm, "end": v(90.95, 1.1) * mm});
            skLineSegment(sketch, "E4237", {"start": v(90.95, 1.1) * mm, "end": v(90.8, 1.38) * mm});
            skLineSegment(sketch, "E4238", {"start": v(90.8, 1.38) * mm, "end": v(90.63, 1.67) * mm});
            skLineSegment(sketch, "E4239", {"start": v(90.63, 1.67) * mm, "end": v(90.48, 1.88) * mm});
            skLineSegment(sketch, "E4240", {"start": v(90.48, 1.88) * mm, "end": v(90.31, 2.08) * mm});
            skLineSegment(sketch, "E4241", {"start": v(90.31, 2.08) * mm, "end": v(90.11, 2.26) * mm});
            skLineSegment(sketch, "E4242", {"start": v(90.11, 2.26) * mm, "end": v(89.88, 2.42) * mm});
            skLineSegment(sketch, "E4243", {"start": v(89.88, 2.42) * mm, "end": v(89.62, 2.57) * mm});
            skLineSegment(sketch, "E4244", {"start": v(89.62, 2.57) * mm, "end": v(89.34, 2.7) * mm});
            skLineSegment(sketch, "E4245", {"start": v(89.34, 2.7) * mm, "end": v(89.02, 2.82) * mm});
            skLineSegment(sketch, "E4246", {"start": v(89.02, 2.82) * mm, "end": v(88.68, 2.92) * mm});
            skLineSegment(sketch, "E4247", {"start": v(88.68, 2.92) * mm, "end": v(88.2, 3.03) * mm});
            skLineSegment(sketch, "E4248", {"start": v(88.2, 3.03) * mm, "end": v(87.68, 3.13) * mm});
            skLineSegment(sketch, "E4249", {"start": v(87.68, 3.13) * mm, "end": v(87.12, 3.2) * mm});
            skLineSegment(sketch, "E4250", {"start": v(87.12, 3.2) * mm, "end": v(86.52, 3.28) * mm});
            skLineSegment(sketch, "E4251", {"start": v(86.52, 3.28) * mm, "end": v(85.89, 3.33) * mm});
            skLineSegment(sketch, "E4252", {"start": v(85.89, 3.33) * mm, "end": v(85.21, 3.36) * mm});
            skLineSegment(sketch, "E4253", {"start": v(85.21, 3.36) * mm, "end": v(84.5, 3.39) * mm});
            skLineSegment(sketch, "E4254", {"start": v(84.5, 3.39) * mm, "end": v(83.75, 3.4) * mm});
            skLineSegment(sketch, "E4255", {"start": v(83.75, 3.4) * mm, "end": v(83.06, 3.4) * mm});
            skLineSegment(sketch, "E4256", {"start": v(83.06, 3.4) * mm, "end": v(82.37, 3.41) * mm});
            skLineSegment(sketch, "E4257", {"start": v(82.37, 3.41) * mm, "end": v(81.68, 3.42) * mm});
            skLineSegment(sketch, "E4258", {"start": v(81.68, 3.42) * mm, "end": v(81, 3.43) * mm});
            skLineSegment(sketch, "E4259", {"start": v(81, 3.43) * mm, "end": v(80.3, 3.44) * mm});
            skLineSegment(sketch, "E4260", {"start": v(80.3, 3.44) * mm, "end": v(79.62, 3.45) * mm});
            skLineSegment(sketch, "E4261", {"start": v(79.62, 3.45) * mm, "end": v(78.93, 3.46) * mm});
            skLineSegment(sketch, "E4262", {"start": v(78.93, 3.46) * mm, "end": v(78.24, 3.47) * mm});
            skLineSegment(sketch, "E4263", {"start": v(78.24, 3.47) * mm, "end": v(77.85, 3.47) * mm});
            skLineSegment(sketch, "E4264", {"start": v(77.85, 3.47) * mm, "end": v(77.38, 3.46) * mm});
            skLineSegment(sketch, "E4265", {"start": v(77.38, 3.46) * mm, "end": v(76.82, 3.45) * mm});
            skLineSegment(sketch, "E4266", {"start": v(76.82, 3.45) * mm, "end": v(76.18, 3.44) * mm});
            skLineSegment(sketch, "E4267", {"start": v(76.18, 3.44) * mm, "end": v(75.47, 3.42) * mm});
            skLineSegment(sketch, "E4268", {"start": v(75.47, 3.42) * mm, "end": v(74.67, 3.4) * mm});
            skLineSegment(sketch, "E4269", {"start": v(74.67, 3.4) * mm, "end": v(73.8, 3.38) * mm});
            skLineSegment(sketch, "E4270", {"start": v(73.8, 3.38) * mm, "end": v(72.87, 3.35) * mm});
            skLineSegment(sketch, "E4271", {"start": v(72.87, 3.35) * mm, "end": v(71.93, 3.32) * mm});
            skLineSegment(sketch, "E4272", {"start": v(71.93, 3.32) * mm, "end": v(71.03, 3.27) * mm});
            skLineSegment(sketch, "E4273", {"start": v(71.03, 3.27) * mm, "end": v(70.18, 3.2) * mm});
            skLineSegment(sketch, "E4274", {"start": v(70.18, 3.2) * mm, "end": v(69.38, 3.12) * mm});
            skLineSegment(sketch, "E4275", {"start": v(69.38, 3.12) * mm, "end": v(68.62, 3.03) * mm});
            skLineSegment(sketch, "E4276", {"start": v(68.62, 3.03) * mm, "end": v(67.92, 2.92) * mm});
            skLineSegment(sketch, "E4277", {"start": v(67.92, 2.92) * mm, "end": v(67.26, 2.79) * mm});
            skLineSegment(sketch, "E4278", {"start": v(67.26, 2.79) * mm, "end": v(66.66, 2.65) * mm});
            skLineSegment(sketch, "E4279", {"start": v(66.66, 2.65) * mm, "end": v(66.2, 2.52) * mm});
            skLineSegment(sketch, "E4280", {"start": v(66.2, 2.52) * mm, "end": v(65.8, 2.36) * mm});
            skLineSegment(sketch, "E4281", {"start": v(65.8, 2.36) * mm, "end": v(65.42, 2.19) * mm});
            skLineSegment(sketch, "E4282", {"start": v(65.42, 2.19) * mm, "end": v(65.1, 1.99) * mm});
            skLineSegment(sketch, "E4283", {"start": v(65.1, 1.99) * mm, "end": v(64.8, 1.77) * mm});
            skLineSegment(sketch, "E4284", {"start": v(64.8, 1.77) * mm, "end": v(64.54, 1.52) * mm});
            skLineSegment(sketch, "E4285", {"start": v(64.54, 1.52) * mm, "end": v(64.32, 1.25) * mm});
            skLineSegment(sketch, "E4286", {"start": v(64.32, 1.25) * mm, "end": v(64.14, 0.96) * mm});
            skLineSegment(sketch, "E4287", {"start": v(64.14, 0.96) * mm, "end": v(63.96, 0.58) * mm});
            skLineSegment(sketch, "E4288", {"start": v(63.96, 0.58) * mm, "end": v(63.8, 0.15) * mm});
            skLineSegment(sketch, "E4289", {"start": v(63.8, 0.15) * mm, "end": v(63.67, -0.33) * mm});
            skLineSegment(sketch, "E4290", {"start": v(63.67, -0.33) * mm, "end": v(63.56, -0.84) * mm});
            skLineSegment(sketch, "E4291", {"start": v(63.56, -0.84) * mm, "end": v(63.48, -1.4) * mm});
            skLineSegment(sketch, "E4292", {"start": v(63.48, -1.4) * mm, "end": v(63.42, -2) * mm});
            skLineSegment(sketch, "E4293", {"start": v(63.42, -2) * mm, "end": v(63.38, -2.65) * mm});
            skLineSegment(sketch, "E4294", {"start": v(63.38, -2.65) * mm, "end": v(63.37, -3.34) * mm});
            skLineSegment(sketch, "E4295", {"start": v(63.37, -3.34) * mm, "end": v(63.39, -4.12) * mm});
            skLineSegment(sketch, "E4296", {"start": v(63.39, -4.12) * mm, "end": v(63.44, -4.85) * mm});
            skLineSegment(sketch, "E4297", {"start": v(63.44, -4.85) * mm, "end": v(63.53, -5.53) * mm});
            skLineSegment(sketch, "E4298", {"start": v(63.53, -5.53) * mm, "end": v(63.66, -6.15) * mm});
            skLineSegment(sketch, "E4299", {"start": v(63.66, -6.15) * mm, "end": v(63.82, -6.7) * mm});
            skLineSegment(sketch, "E4300", {"start": v(63.82, -6.7) * mm, "end": v(64.02, -7.2) * mm});
            skLineSegment(sketch, "E4301", {"start": v(64.02, -7.2) * mm, "end": v(64.26, -7.65) * mm});
            skLineSegment(sketch, "E4302", {"start": v(64.26, -7.65) * mm, "end": v(64.53, -8.04) * mm});
            skLineSegment(sketch, "E4303", {"start": v(64.53, -8.04) * mm, "end": v(64.82, -8.34) * mm});
            skLineSegment(sketch, "E4304", {"start": v(64.82, -8.34) * mm, "end": v(65.17, -8.6) * mm});
            skLineSegment(sketch, "E4305", {"start": v(65.17, -8.6) * mm, "end": v(65.58, -8.83) * mm});
            skLineSegment(sketch, "E4306", {"start": v(65.58, -8.83) * mm, "end": v(66.05, -9) * mm});
            skLineSegment(sketch, "E4307", {"start": v(66.05, -9) * mm, "end": v(66.58, -9.15) * mm});
            skLineSegment(sketch, "E4308", {"start": v(66.58, -9.15) * mm, "end": v(67.17, -9.25) * mm});
            skLineSegment(sketch, "E4309", {"start": v(67.17, -9.25) * mm, "end": v(67.8, -9.31) * mm});
            skLineSegment(sketch, "E4310", {"start": v(67.8, -9.31) * mm, "end": v(68.51, -9.33) * mm});
            skLineSegment(sketch, "E4311", {"start": v(68.51, -9.33) * mm, "end": v(70.13, -9.37) * mm});
            skLineSegment(sketch, "E4312", {"start": v(70.13, -9.37) * mm, "end": v(71.75, -9.4) * mm});
            skLineSegment(sketch, "E4313", {"start": v(71.75, -9.4) * mm, "end": v(73.37, -9.43) * mm});
            skLineSegment(sketch, "E4314", {"start": v(73.37, -9.43) * mm, "end": v(74.99, -9.47) * mm});
            skLineSegment(sketch, "E4315", {"start": v(74.99, -9.47) * mm, "end": v(76.6, -9.5) * mm});
            skLineSegment(sketch, "E4316", {"start": v(76.6, -9.5) * mm, "end": v(78.22, -9.54) * mm});
            skLineSegment(sketch, "E4317", {"start": v(78.22, -9.54) * mm, "end": v(79.84, -9.57) * mm});
            skLineSegment(sketch, "E4318", {"start": v(79.84, -9.57) * mm, "end": v(81.46, -9.6) * mm});
            skLineSegment(sketch, "E4319", {"start": v(81.46, -9.6) * mm, "end": v(81.61, -9.6) * mm});
            skLineSegment(sketch, "E4320", {"start": v(81.61, -9.6) * mm, "end": v(81.77, -9.6) * mm});
            skLineSegment(sketch, "E4321", {"start": v(81.77, -9.6) * mm, "end": v(81.93, -9.6) * mm});
            skLineSegment(sketch, "E4322", {"start": v(81.93, -9.6) * mm, "end": v(82.08, -9.6) * mm});
            skLineSegment(sketch, "E4323", {"start": v(82.08, -9.6) * mm, "end": v(82.24, -9.6) * mm});
            skLineSegment(sketch, "E4324", {"start": v(82.24, -9.6) * mm, "end": v(82.4, -9.6) * mm});
            skLineSegment(sketch, "E4325", {"start": v(82.4, -9.6) * mm, "end": v(82.55, -9.6) * mm});
            skLineSegment(sketch, "E4326", {"start": v(82.55, -9.6) * mm, "end": v(82.7, -9.6) * mm});
            skLineSegment(sketch, "E4327", {"start": v(82.7, -9.6) * mm, "end": v(83.36, -9.62) * mm});
            skLineSegment(sketch, "E4328", {"start": v(83.36, -9.62) * mm, "end": v(83.95, -9.66) * mm});
            skLineSegment(sketch, "E4329", {"start": v(83.95, -9.66) * mm, "end": v(84.5, -9.73) * mm});
            skLineSegment(sketch, "E4330", {"start": v(84.5, -9.73) * mm, "end": v(85, -9.84) * mm});
            skLineSegment(sketch, "E4331", {"start": v(85, -9.84) * mm, "end": v(85.44, -9.97) * mm});
            skLineSegment(sketch, "E4332", {"start": v(85.44, -9.97) * mm, "end": v(85.84, -10.14) * mm});
            skLineSegment(sketch, "E4333", {"start": v(85.84, -10.14) * mm, "end": v(86.2, -10.33) * mm});
            skLineSegment(sketch, "E4334", {"start": v(86.2, -10.33) * mm, "end": v(86.52, -10.56) * mm});
            skLineSegment(sketch, "E4335", {"start": v(86.52, -10.56) * mm, "end": v(86.82, -10.83) * mm});
            skLineSegment(sketch, "E4336", {"start": v(86.82, -10.83) * mm, "end": v(87.08, -11.13) * mm});
            skLineSegment(sketch, "E4337", {"start": v(87.08, -11.13) * mm, "end": v(87.3, -11.45) * mm});
            skLineSegment(sketch, "E4338", {"start": v(87.3, -11.45) * mm, "end": v(87.48, -11.79) * mm});
            skLineSegment(sketch, "E4339", {"start": v(87.48, -11.79) * mm, "end": v(87.62, -12.15) * mm});
            skLineSegment(sketch, "E4340", {"start": v(87.62, -12.15) * mm, "end": v(87.72, -12.53) * mm});
            skLineSegment(sketch, "E4341", {"start": v(87.72, -12.53) * mm, "end": v(87.79, -12.93) * mm});
            skLineSegment(sketch, "E4342", {"start": v(87.79, -12.93) * mm, "end": v(87.8, -13.35) * mm});
            skLineSegment(sketch, "E4343", {"start": v(87.8, -13.35) * mm, "end": v(87.78, -13.9) * mm});
            skLineSegment(sketch, "E4344", {"start": v(87.78, -13.9) * mm, "end": v(87.7, -14.38) * mm});
            skLineSegment(sketch, "E4345", {"start": v(87.7, -14.38) * mm, "end": v(87.57, -14.8) * mm});
            skLineSegment(sketch, "E4346", {"start": v(87.57, -14.8) * mm, "end": v(87.42, -15.18) * mm});
            skLineSegment(sketch, "E4347", {"start": v(87.42, -15.18) * mm, "end": v(87.23, -15.5) * mm});
            skLineSegment(sketch, "E4348", {"start": v(87.23, -15.5) * mm, "end": v(87.03, -15.77) * mm});
            skLineSegment(sketch, "E4349", {"start": v(87.03, -15.77) * mm, "end": v(86.83, -16) * mm});
            skLineSegment(sketch, "E4350", {"start": v(86.83, -16) * mm, "end": v(86.62, -16.19) * mm});
            skLineSegment(sketch, "E4351", {"start": v(86.62, -16.19) * mm, "end": v(86.32, -16.4) * mm});
            skLineSegment(sketch, "E4352", {"start": v(86.32, -16.4) * mm, "end": v(85.99, -16.58) * mm});
            skLineSegment(sketch, "E4353", {"start": v(85.99, -16.58) * mm, "end": v(85.6, -16.73) * mm});
            skLineSegment(sketch, "E4354", {"start": v(85.6, -16.73) * mm, "end": v(85.17, -16.85) * mm});
            skLineSegment(sketch, "E4355", {"start": v(85.17, -16.85) * mm, "end": v(84.69, -16.94) * mm});
            skLineSegment(sketch, "E4356", {"start": v(84.69, -16.94) * mm, "end": v(84.14, -17.01) * mm});
            skLineSegment(sketch, "E4357", {"start": v(84.14, -17.01) * mm, "end": v(83.54, -17.05) * mm});
            skLineSegment(sketch, "E4358", {"start": v(83.54, -17.05) * mm, "end": v(82.88, -17.06) * mm});
            skLineSegment(sketch, "E4359", {"start": v(82.88, -17.06) * mm, "end": v(82.23, -17.08) * mm});
            skLineSegment(sketch, "E4360", {"start": v(82.23, -17.08) * mm, "end": v(81.57, -17.1) * mm});
            skLineSegment(sketch, "E4361", {"start": v(81.57, -17.1) * mm, "end": v(80.92, -17.12) * mm});
            skLineSegment(sketch, "E4362", {"start": v(80.92, -17.12) * mm, "end": v(80.26, -17.14) * mm});
            skLineSegment(sketch, "E4363", {"start": v(80.26, -17.14) * mm, "end": v(79.6, -17.16) * mm});
            skLineSegment(sketch, "E4364", {"start": v(79.6, -17.16) * mm, "end": v(78.95, -17.18) * mm});
            skLineSegment(sketch, "E4365", {"start": v(78.95, -17.18) * mm, "end": v(78.3, -17.2) * mm});
            skLineSegment(sketch, "E4366", {"start": v(78.3, -17.2) * mm, "end": v(77.64, -17.22) * mm});
            skLineSegment(sketch, "E4367", {"start": v(77.64, -17.22) * mm, "end": v(77.64, -17.22) * mm});
            skLineSegment(sketch, "E4368", {"start": v(77.64, -17.22) * mm, "end": v(77.63, -17.22) * mm});
            skLineSegment(sketch, "E4369", {"start": v(77.63, -17.22) * mm, "end": v(77.62, -17.22) * mm});
            skLineSegment(sketch, "E4370", {"start": v(77.62, -17.22) * mm, "end": v(77.62, -17.22) * mm});
            skLineSegment(sketch, "E4371", {"start": v(77.62, -17.22) * mm, "end": v(77.6, -17.22) * mm});
            skLineSegment(sketch, "E4372", {"start": v(77.6, -17.22) * mm, "end": v(77.6, -17.22) * mm});
            skLineSegment(sketch, "E4373", {"start": v(77.6, -17.22) * mm, "end": v(77.59, -17.22) * mm});
            skLineSegment(sketch, "E4374", {"start": v(77.59, -17.22) * mm, "end": v(77.12, -17.21) * mm});
            skLineSegment(sketch, "E4375", {"start": v(77.12, -17.21) * mm, "end": v(76.66, -17.2) * mm});
            skLineSegment(sketch, "E4376", {"start": v(76.66, -17.2) * mm, "end": v(76.2, -17.2) * mm});
            skLineSegment(sketch, "E4377", {"start": v(76.2, -17.2) * mm, "end": v(75.73, -17.2) * mm});
            skLineSegment(sketch, "E4378", {"start": v(75.73, -17.2) * mm, "end": v(75.27, -17.2) * mm});
            skLineSegment(sketch, "E4379", {"start": v(75.27, -17.2) * mm, "end": v(74.8, -17.19) * mm});
            skLineSegment(sketch, "E4380", {"start": v(74.8, -17.19) * mm, "end": v(74.34, -17.19) * mm});
            skLineSegment(sketch, "E4381", {"start": v(74.34, -17.19) * mm, "end": v(73.87, -17.18) * mm});
            skLineSegment(sketch, "E4382", {"start": v(73.87, -17.18) * mm, "end": v(72.03, -17.14) * mm});
            skLineSegment(sketch, "E4383", {"start": v(72.03, -17.14) * mm, "end": v(70.36, -17) * mm});
            skLineSegment(sketch, "E4384", {"start": v(70.36, -17) * mm, "end": v(68.85, -16.8) * mm});
            skLineSegment(sketch, "E4385", {"start": v(68.85, -16.8) * mm, "end": v(67.51, -16.55) * mm});
            skLineSegment(sketch, "E4386", {"start": v(67.51, -16.55) * mm, "end": v(66.32, -16.24) * mm});
            skLineSegment(sketch, "E4387", {"start": v(66.32, -16.24) * mm, "end": v(65.28, -15.88) * mm});
            skLineSegment(sketch, "E4388", {"start": v(65.28, -15.88) * mm, "end": v(64.36, -15.5) * mm});
            skLineSegment(sketch, "E4389", {"start": v(64.36, -15.5) * mm, "end": v(63.58, -15.1) * mm});
            skLineSegment(sketch, "E4390", {"start": v(-64.19, -0.09) * mm, "end": v(-64.13, -0.42) * mm});
            skLineSegment(sketch, "E4391", {"start": v(-64.13, -0.42) * mm, "end": v(-64.09, -0.84) * mm});
            skLineSegment(sketch, "E4392", {"start": v(-64.09, -0.84) * mm, "end": v(-64.05, -1.33) * mm});
            skLineSegment(sketch, "E4393", {"start": v(-64.05, -1.33) * mm, "end": v(-64.01, -1.87) * mm});
            skLineSegment(sketch, "E4394", {"start": v(-64.01, -1.87) * mm, "end": v(-63.99, -2.44) * mm});
            skLineSegment(sketch, "E4395", {"start": v(-63.99, -2.44) * mm, "end": v(-63.97, -3) * mm});
            skLineSegment(sketch, "E4396", {"start": v(-63.97, -3) * mm, "end": v(-63.96, -3.56) * mm});
            skLineSegment(sketch, "E4397", {"start": v(-63.96, -3.56) * mm, "end": v(-63.96, -4.08) * mm});
            skLineSegment(sketch, "E4398", {"start": v(-63.96, -4.08) * mm, "end": v(-64.04, -3.93) * mm});
            skLineSegment(sketch, "E4399", {"start": v(-64.04, -3.93) * mm, "end": v(-64.35, -3.56) * mm});
            skLineSegment(sketch, "E4400", {"start": v(-64.35, -3.56) * mm, "end": v(-64.95, -3.02) * mm});
            skLineSegment(sketch, "E4401", {"start": v(-64.95, -3.02) * mm, "end": v(-65.9, -2.41) * mm});
            skLineSegment(sketch, "E4402", {"start": v(-65.9, -2.41) * mm, "end": v(-67.29, -1.8) * mm});
            skLineSegment(sketch, "E4403", {"start": v(-67.29, -1.8) * mm, "end": v(-69.16, -1.27) * mm});
            skLineSegment(sketch, "E4404", {"start": v(-69.16, -1.27) * mm, "end": v(-71.6, -0.89) * mm});
            skLineSegment(sketch, "E4405", {"start": v(-71.6, -0.89) * mm, "end": v(-74.67, -0.75) * mm});
            skLineSegment(sketch, "E4406", {"start": v(-95.05, -14.44) * mm, "end": v(-95.05, -14.17) * mm});
            skLineSegment(sketch, "E4407", {"start": v(-95.05, -14.17) * mm, "end": v(-95.05, -13.91) * mm});
            skLineSegment(sketch, "E4408", {"start": v(-95.05, -13.91) * mm, "end": v(-95.05, -13.65) * mm});
            skLineSegment(sketch, "E4409", {"start": v(-95.05, -13.65) * mm, "end": v(-95.05, -13.39) * mm});
            skLineSegment(sketch, "E4410", {"start": v(-95.05, -13.39) * mm, "end": v(-95.05, -13.13) * mm});
            skLineSegment(sketch, "E4411", {"start": v(-95.05, -13.13) * mm, "end": v(-95.05, -12.86) * mm});
            skLineSegment(sketch, "E4412", {"start": v(-95.05, -12.86) * mm, "end": v(-95.05, -12.6) * mm});
            skLineSegment(sketch, "E4413", {"start": v(-95.05, -12.6) * mm, "end": v(-95.05, -12.34) * mm});
            skLineSegment(sketch, "E4414", {"start": v(-95.05, -12.34) * mm, "end": v(-94.95, -12.48) * mm});
            skLineSegment(sketch, "E4415", {"start": v(-94.95, -12.48) * mm, "end": v(-94.61, -12.87) * mm});
            skLineSegment(sketch, "E4416", {"start": v(-94.61, -12.87) * mm, "end": v(-93.96, -13.4) * mm});
            skLineSegment(sketch, "E4417", {"start": v(-93.96, -13.4) * mm, "end": v(-92.91, -14.03) * mm});
            skLineSegment(sketch, "E4418", {"start": v(-92.91, -14.03) * mm, "end": v(-91.4, -14.65) * mm});
            skLineSegment(sketch, "E4419", {"start": v(-91.4, -14.65) * mm, "end": v(-89.33, -15.19) * mm});
            skLineSegment(sketch, "E4420", {"start": v(-89.33, -15.19) * mm, "end": v(-86.64, -15.57) * mm});
            skLineSegment(sketch, "E4421", {"start": v(-86.64, -15.57) * mm, "end": v(-83.25, -15.71) * mm});
            skLineSegment(sketch, "E4422", {"start": v(92.95, -0.09) * mm, "end": v(93, -0.42) * mm});
            skLineSegment(sketch, "E4423", {"start": v(93, -0.42) * mm, "end": v(93.05, -0.84) * mm});
            skLineSegment(sketch, "E4424", {"start": v(93.05, -0.84) * mm, "end": v(93.1, -1.33) * mm});
            skLineSegment(sketch, "E4425", {"start": v(93.1, -1.33) * mm, "end": v(93.13, -1.87) * mm});
            skLineSegment(sketch, "E4426", {"start": v(93.13, -1.87) * mm, "end": v(93.15, -2.44) * mm});
            skLineSegment(sketch, "E4427", {"start": v(93.15, -2.44) * mm, "end": v(93.17, -3) * mm});
            skLineSegment(sketch, "E4428", {"start": v(93.17, -3) * mm, "end": v(93.18, -3.56) * mm});
            skLineSegment(sketch, "E4429", {"start": v(93.18, -3.56) * mm, "end": v(93.19, -4.08) * mm});
            skLineSegment(sketch, "E4430", {"start": v(93.19, -4.08) * mm, "end": v(93.1, -3.93) * mm});
            skLineSegment(sketch, "E4431", {"start": v(93.1, -3.93) * mm, "end": v(92.79, -3.56) * mm});
            skLineSegment(sketch, "E4432", {"start": v(92.79, -3.56) * mm, "end": v(92.2, -3.02) * mm});
            skLineSegment(sketch, "E4433", {"start": v(92.2, -3.02) * mm, "end": v(91.24, -2.41) * mm});
            skLineSegment(sketch, "E4434", {"start": v(91.24, -2.41) * mm, "end": v(89.85, -1.8) * mm});
            skLineSegment(sketch, "E4435", {"start": v(89.85, -1.8) * mm, "end": v(87.98, -1.27) * mm});
            skLineSegment(sketch, "E4436", {"start": v(87.98, -1.27) * mm, "end": v(85.54, -0.89) * mm});
            skLineSegment(sketch, "E4437", {"start": v(85.54, -0.89) * mm, "end": v(82.47, -0.75) * mm});
            skLineSegment(sketch, "E4438", {"start": v(62.1, -14.44) * mm, "end": v(62.1, -14.17) * mm});
            skLineSegment(sketch, "E4439", {"start": v(62.1, -14.17) * mm, "end": v(62.1, -13.91) * mm});
            skLineSegment(sketch, "E4440", {"start": v(62.1, -13.91) * mm, "end": v(62.1, -13.65) * mm});
            skLineSegment(sketch, "E4441", {"start": v(62.1, -13.65) * mm, "end": v(62.1, -13.39) * mm});
            skLineSegment(sketch, "E4442", {"start": v(62.1, -13.39) * mm, "end": v(62.1, -13.13) * mm});
            skLineSegment(sketch, "E4443", {"start": v(62.1, -13.13) * mm, "end": v(62.1, -12.86) * mm});
            skLineSegment(sketch, "E4444", {"start": v(62.1, -12.86) * mm, "end": v(62.1, -12.6) * mm});
            skLineSegment(sketch, "E4445", {"start": v(62.1, -12.6) * mm, "end": v(62.1, -12.34) * mm});
            skLineSegment(sketch, "E4446", {"start": v(62.1, -12.34) * mm, "end": v(62.19, -12.48) * mm});
            skLineSegment(sketch, "E4447", {"start": v(62.19, -12.48) * mm, "end": v(62.53, -12.87) * mm});
            skLineSegment(sketch, "E4448", {"start": v(62.53, -12.87) * mm, "end": v(63.18, -13.4) * mm});
            skLineSegment(sketch, "E4449", {"start": v(63.18, -13.4) * mm, "end": v(64.23, -14.03) * mm});
            skLineSegment(sketch, "E4450", {"start": v(64.23, -14.03) * mm, "end": v(65.75, -14.65) * mm});
            skLineSegment(sketch, "E4451", {"start": v(65.75, -14.65) * mm, "end": v(67.81, -15.19) * mm});
            skLineSegment(sketch, "E4452", {"start": v(67.81, -15.19) * mm, "end": v(70.5, -15.57) * mm});
            skLineSegment(sketch, "E4453", {"start": v(70.5, -15.57) * mm, "end": v(73.89, -15.71) * mm});
            skSolve(sketch);
        }
        {
            var Q0;
            Q0=makeQuery(id+"F0.imprint","IMPRINT",FACE,{"disambiguationData":[TD([[makeQuery(id+"F0.imprint","IMPRINT",EDGE,{"derivedFrom":sQuery(id+"F0.wireOp",EDGE,"E355")}),1.0]])]});
            var Q1;
            Q1=makeQuery(id+"F0.imprint","IMPRINT",FACE,{"disambiguationData":[TD([[makeQuery(id+"F0.imprint","IMPRINT",EDGE,{"derivedFrom":sQuery(id+"F0.wireOp",EDGE,"E491")}),-1.0]])]});
            var Q2;
            Q2=makeQuery(id+"F0.imprint","IMPRINT",FACE,{"disambiguationData":[TD([[makeQuery(id+"F0.imprint","IMPRINT",EDGE,{"derivedFrom":sQuery(id+"F0.wireOp",EDGE,"E67")}),1.0]])]});
            var Q3;
            Q3=makeQuery(id+"F0.imprint","IMPRINT",FACE,{"disambiguationData":[TD([[makeQuery(id+"F0.imprint","IMPRINT",EDGE,{"derivedFrom":sQuery(id+"F0.wireOp",EDGE,"E187")}),-1.0]])]});
            var Q4;
            Q4=makeQuery(id+"F0.imprint","IMPRINT",FACE,{"disambiguationData":[TD([[makeQuery(id+"F0.imprint","IMPRINT",EDGE,{"derivedFrom":sQuery(id+"F0.wireOp",EDGE,"E1019")}),-1.0]])]});
            var Q5;
            Q5=makeQuery(id+"F0.imprint","IMPRINT",FACE,{"disambiguationData":[TD([[makeQuery(id+"F0.imprint","IMPRINT",EDGE,{"derivedFrom":sQuery(id+"F0.wireOp",EDGE,"E1131")}),-1.0]])]});
            var Q6;
            Q6=makeQuery(id+"F0.imprint","IMPRINT",FACE,{"disambiguationData":[TD([[makeQuery(id+"F0.imprint","IMPRINT",EDGE,{"derivedFrom":sQuery(id+"F0.wireOp",EDGE,"E2298")}),-1.0]])]});
            var Q7;
            Q7=makeQuery(id+"F0.imprint","IMPRINT",FACE,{"disambiguationData":[TD([[makeQuery(id+"F0.imprint","IMPRINT",EDGE,{"derivedFrom":sQuery(id+"F0.wireOp",EDGE,"E1600")}),-1.0]])]});
            var Q8;
            Q8=makeQuery(id+"F0.imprint","IMPRINT",FACE,{"disambiguationData":[TD([[makeQuery(id+"F0.imprint","IMPRINT",EDGE,{"derivedFrom":sQuery(id+"F0.wireOp",EDGE,"E763")}),-1.0]])]});
            var Q9;
            {var subQ34=sQuery(id+"F0.wireOp",EDGE,"E2");Q9=makeQuery(id+"F0.imprint","IMPRINT",FACE,{"disambiguationData":[TD([[makeQuery(id+"F0.imprint","IMPRINT",EDGE,{"derivedFrom":subQ34}),-1.0]])]});}
            var Q10;
            {var subQ2=sQuery(id+"F0.wireOp",EDGE,"E771");Q10=makeQuery(id+"F0.imprint","IMPRINT",FACE,{"disambiguationData":[TD([[makeQuery(id+"F0.imprint","IMPRINT",EDGE,{"derivedFrom":subQ2}),1.0]])]});}
            var Q11;
            Q11=makeQuery(id+"F0.imprint","IMPRINT",FACE,{"disambiguationData":[TD([[makeQuery(id+"F0.imprint","IMPRINT",EDGE,{"derivedFrom":sQuery(id+"F0.wireOp",EDGE,"E2434")}),1.0]])]});
            var Q12;
            {var subQ14=sQuery(id+"F0.wireOp",EDGE,"E1937");Q12=makeQuery(id+"F0.imprint","IMPRINT",FACE,{"disambiguationData":[TD([[makeQuery(id+"F0.imprint","IMPRINT",EDGE,{"derivedFrom":subQ14}),1.0]])]});}
            var Q13;
            Q13=makeQuery(id+"F0.imprint","IMPRINT",FACE,{"disambiguationData":[TD([[makeQuery(id+"F0.imprint","IMPRINT",EDGE,{"derivedFrom":sQuery(id+"F0.wireOp",EDGE,"E3905")}),-1.0]])]});
            var Q14;
            {var subQ13=sQuery(id+"F0.wireOp",EDGE,"E1328");Q14=makeQuery(id+"F0.imprint","IMPRINT",FACE,{"disambiguationData":[TD([[makeQuery(id+"F0.imprint","IMPRINT",EDGE,{"derivedFrom":subQ13}),1.0]])]});}
            var Q15;
            {var subQ4=sQuery(id+"F0.wireOp",EDGE,"E827");Q15=makeQuery(id+"F0.imprint","IMPRINT",FACE,{"disambiguationData":[TD([[makeQuery(id+"F0.imprint","IMPRINT",EDGE,{"derivedFrom":subQ4}),-1.0]])]});}
            var Q16;
            {var subQ5=sQuery(id+"F0.wireOp",EDGE,"E816");Q16=makeQuery(id+"F0.imprint","IMPRINT",FACE,{"disambiguationData":[TD([[makeQuery(id+"F0.imprint","IMPRINT",EDGE,{"derivedFrom":subQ5}),1.0]])]});}
            var Q17;
            {var subQ0=sQuery(id+"F0.wireOp",EDGE,"E803");Q17=makeQuery(id+"F0.imprint","IMPRINT",FACE,{"disambiguationData":[TD([[makeQuery(id+"F0.imprint","IMPRINT",EDGE,{"derivedFrom":subQ0}),-1.0]])]});}
            var Q18;
            {var subQ0=sQuery(id+"F0.wireOp",EDGE,"E1328");Q18=makeQuery(id+"F0.imprint","IMPRINT",FACE,{"disambiguationData":[TD([[makeQuery(id+"F0.imprint","IMPRINT",EDGE,{"derivedFrom":subQ0}),-1.0]])]});}
            var Q19;
            {var subQ5=sQuery(id+"F0.wireOp",EDGE,"E771");Q19=makeQuery(id+"F0.imprint","IMPRINT",FACE,{"disambiguationData":[TD([[makeQuery(id+"F0.imprint","IMPRINT",EDGE,{"derivedFrom":subQ5}),-1.0]])]});}
            var Q20;
            {var subQ5=sQuery(id+"F0.wireOp",EDGE,"E1937");Q20=makeQuery(id+"F0.imprint","IMPRINT",FACE,{"disambiguationData":[TD([[makeQuery(id+"F0.imprint","IMPRINT",EDGE,{"derivedFrom":subQ5}),-1.0]])]});}
            var Q21;
            {var subQ0=sQuery(id+"F0.wireOp",EDGE,"E1980");Q21=makeQuery(id+"F0.imprint","IMPRINT",FACE,{"disambiguationData":[TD([[makeQuery(id+"F0.imprint","IMPRINT",EDGE,{"derivedFrom":subQ0}),-1.0]])]});}
            extrude(context, id + "F1", {"entities" : qUnion([Q0, Q1, Q2, Q3, Q4, Q5, Q6, Q7, Q8, Q9, Q10, Q11, Q12, Q13, Q14, Q15, Q16, Q17, Q18, Q19, Q20, Q21]), "depth" : 2.54 * mm, "offsetDistance" : 25.4 * mm});
        }
        {
            var Q0;
            Q0=makeQuery(id+"F0.imprint","IMPRINT",FACE,{"disambiguationData":[TD([[makeQuery(id+"F0.imprint","IMPRINT",EDGE,{"derivedFrom":sQuery(id+"F0.wireOp",EDGE,"E243")}),1.0]])]});
            var Q1;
            Q1=makeQuery(id+"F0.imprint","IMPRINT",FACE,{"disambiguationData":[TD([[makeQuery(id+"F0.imprint","IMPRINT",EDGE,{"derivedFrom":sQuery(id+"F0.wireOp",EDGE,"E323")}),1.0]])]});
            var Q2;
            Q2=makeQuery(id+"F0.imprint","IMPRINT",FACE,{"disambiguationData":[TD([[makeQuery(id+"F0.imprint","IMPRINT",EDGE,{"derivedFrom":sQuery(id+"F0.wireOp",EDGE,"E411")}),-1.0]])]});
            var Q3;
            Q3=makeQuery(id+"F0.imprint","IMPRINT",FACE,{"disambiguationData":[TD([[makeQuery(id+"F0.imprint","IMPRINT",EDGE,{"derivedFrom":sQuery(id+"F0.wireOp",EDGE,"E123")}),1.0]])]});
            var Q4;
            Q4=makeQuery(id+"F0.imprint","IMPRINT",FACE,{"disambiguationData":[TD([[makeQuery(id+"F0.imprint","IMPRINT",EDGE,{"derivedFrom":sQuery(id+"F0.wireOp",EDGE,"E3")}),-1.0]])]});
            var Q5;
            Q5=makeQuery(id+"F0.imprint","IMPRINT",FACE,{"disambiguationData":[TD([[makeQuery(id+"F0.imprint","IMPRINT",EDGE,{"derivedFrom":sQuery(id+"F0.wireOp",EDGE,"E3098")}),1.0]])]});
            var Q6;
            Q6=makeQuery(id+"F0.imprint","IMPRINT",FACE,{"disambiguationData":[TD([[makeQuery(id+"F0.imprint","IMPRINT",EDGE,{"derivedFrom":sQuery(id+"F0.wireOp",EDGE,"E2930")}),-1.0]])]});
            var Q7;
            Q7=makeQuery(id+"F0.imprint","IMPRINT",FACE,{"disambiguationData":[TD([[makeQuery(id+"F0.imprint","IMPRINT",EDGE,{"derivedFrom":sQuery(id+"F0.wireOp",EDGE,"E1424")}),-1.0]])]});
            var Q8;
            Q8=makeQuery(id+"F0.imprint","IMPRINT",FACE,{"disambiguationData":[TD([[makeQuery(id+"F0.imprint","IMPRINT",EDGE,{"derivedFrom":sQuery(id+"F0.wireOp",EDGE,"E1424")}),1.0]])]});
            var Q9;
            Q9=makeQuery(id+"F0.imprint","IMPRINT",FACE,{"disambiguationData":[TD([[makeQuery(id+"F0.imprint","IMPRINT",EDGE,{"derivedFrom":sQuery(id+"F0.wireOp",EDGE,"E1512")}),-1.0]])]});
            var Q10;
            Q10=makeQuery(id+"F0.imprint","IMPRINT",FACE,{"disambiguationData":[TD([[makeQuery(id+"F0.imprint","IMPRINT",EDGE,{"derivedFrom":sQuery(id+"F0.wireOp",EDGE,"E1075")}),-1.0]])]});
            var Q11;
            Q11=makeQuery(id+"F0.imprint","IMPRINT",FACE,{"disambiguationData":[TD([[makeQuery(id+"F0.imprint","IMPRINT",EDGE,{"derivedFrom":sQuery(id+"F0.wireOp",EDGE,"E851")}),1.0]])]});
            var Q12;
            Q12=makeQuery(id+"F0.imprint","IMPRINT",FACE,{"disambiguationData":[TD([[makeQuery(id+"F0.imprint","IMPRINT",EDGE,{"derivedFrom":sQuery(id+"F0.wireOp",EDGE,"E851")}),-1.0]])]});
            var Q13;
            Q13=makeQuery(id+"F0.imprint","IMPRINT",FACE,{"disambiguationData":[TD([[makeQuery(id+"F0.imprint","IMPRINT",EDGE,{"derivedFrom":sQuery(id+"F0.wireOp",EDGE,"E2003")}),1.0]])]});
            var Q14;
            Q14=makeQuery(id+"F0.imprint","IMPRINT",FACE,{"disambiguationData":[TD([[makeQuery(id+"F0.imprint","IMPRINT",EDGE,{"derivedFrom":sQuery(id+"F0.wireOp",EDGE,"E2003")}),-1.0]])]});
            var Q15;
            Q15=makeQuery(id+"F0.imprint","IMPRINT",FACE,{"disambiguationData":[TD([[makeQuery(id+"F0.imprint","IMPRINT",EDGE,{"derivedFrom":sQuery(id+"F0.wireOp",EDGE,"E2234")}),-1.0]])]});
            var Q16;
            Q16=makeQuery(id+"F0.imprint","IMPRINT",FACE,{"disambiguationData":[TD([[makeQuery(id+"F0.imprint","IMPRINT",EDGE,{"derivedFrom":sQuery(id+"F0.wireOp",EDGE,"E2578")}),1.0]])]});
            var Q17;
            Q17=makeQuery(id+"F0.imprint","IMPRINT",FACE,{"disambiguationData":[TD([[makeQuery(id+"F0.imprint","IMPRINT",EDGE,{"derivedFrom":sQuery(id+"F0.wireOp",EDGE,"E2434")}),-1.0]])]});
            var Q18;
            Q18=makeQuery(id+"F0.imprint","IMPRINT",FACE,{"disambiguationData":[TD([[makeQuery(id+"F0.imprint","IMPRINT",EDGE,{"derivedFrom":sQuery(id+"F0.wireOp",EDGE,"E4073")}),1.0]])]});
            var Q19;
            Q19=makeQuery(id+"F0.imprint","IMPRINT",FACE,{"disambiguationData":[TD([[makeQuery(id+"F0.imprint","IMPRINT",EDGE,{"derivedFrom":sQuery(id+"F0.wireOp",EDGE,"E963")}),-1.0]])]});
            extrude(context, id + "F2", {"entities" : qUnion([Q0, Q1, Q2, Q3, Q4, Q5, Q6, Q7, Q8, Q9, Q10, Q11, Q12, Q13, Q14, Q15, Q16, Q17, Q18, Q19]), "depth" : 3.8 * mm, "offsetDistance" : 25.4 * mm});
        }
        {
            var Q0;
            Q0=qCreatedBy(makeId("Front.planeOp"),FACE);
            var sketch = newSketch(context, id + "F3", { "sketchPlane" : qUnion([Q0])});
            skLineSegment(sketch, "E4454", {"start": v(0, 45.67) * mm, "end": v(0, 11.04) * mm, "construction": true});
            skArc(sketch, "E4455", {"start": v(0, 11.04) * mm, "mid": v(-7.43, 21.11) * mm, "end": v(-17.79, 28.13) * mm, "construction": true});
            skArc(sketch, "E4456", {"start": v(-7.48, 25.23) * mm, "mid": v(-12.5, 27.13) * mm, "end": v(-17.79, 28.13) * mm});
            skArc(sketch, "E4457", {"start": v(-7.48, 25.23) * mm, "mid": v(-12.31, 32.97) * mm, "end": v(-19.33, 38.8) * mm});
            skArc(sketch, "E4458", {"start": v(-6.4, 33.83) * mm, "mid": v(-12.4, 37.51) * mm, "end": v(-19.33, 38.8) * mm});
            skArc(sketch, "E4459", {"start": v(-6.4, 33.83) * mm, "mid": v(-1.7, 38.94) * mm, "end": v(0, 45.67) * mm});
            skArc(sketch, "E4460.MirrorCS", {"start": v(6.4, 33.83) * mm, "mid": v(1.7, 38.94) * mm, "end": v(0, 45.67) * mm});
            skArc(sketch, "E4461.MirrorCS", {"start": v(6.4, 33.83) * mm, "mid": v(12.4, 37.51) * mm, "end": v(19.33, 38.8) * mm});
            skArc(sketch, "E4462.MirrorCS", {"start": v(7.48, 25.23) * mm, "mid": v(12.31, 32.97) * mm, "end": v(19.33, 38.8) * mm});
            skArc(sketch, "E4463.MirrorCS", {"start": v(7.48, 25.23) * mm, "mid": v(12.5, 27.13) * mm, "end": v(17.79, 28.13) * mm});
            skArc(sketch, "E4464.MirrorCS", {"start": v(0, 11.04) * mm, "mid": v(7.43, 21.11) * mm, "end": v(17.79, 28.13) * mm, "construction": true});
            skArc(sketch, "E4465.MirrorCS", {"start": v(0, 11.04) * mm, "mid": v(-7.43, 21.11) * mm, "end": v(-17.79, 28.13) * mm});
            skArc(sketch, "E4466.MirrorCS", {"start": v(0, 11.04) * mm, "mid": v(7.43, 21.11) * mm, "end": v(17.79, 28.13) * mm});
            skSolve(sketch);
        }
        {
            var Q0;
            Q0 = qSketchRegion(id + "F3", true);
            extrude(context, id + "F4", {"entities" : qUnion([Q0]), "depth" : 2.54 * mm, "offsetDistance" : 25.4 * mm});
        }
        {
            var Q0;
            Q0=qCreatedBy(makeId("Front.planeOp"),FACE);
            var sketch = newSketch(context, id + "F5", { "sketchPlane" : qUnion([Q0])});
            skFitSpline(sketch, "E4467", {"points": [v(0, 56.67) * mm, v(-14.73, 59.25) * mm, v(-32.8, 58.18) * mm, v(-47.43, 54.52) * mm, v(-53.66, 52.59) * mm, v(-64.42, 53.88) * mm, v(-74.53, 54.1) * mm, v(-85.5, 56.24) * mm, v(-93.24, 57.1) * mm, v(-101.41, 55.38) * mm, v(-106.14, 49.36) * mm, v(-106.14, 41.19) * mm, v(-102.7, 34.74) * mm, v(-91.09, 22.7) * mm, v(-88.5, 16.45) * mm, v(-92.8, 11.72) * mm, v(-98.61, 8.28) * mm, v(-102.49, 0) * mm, v(-102.92, -10.86) * mm, v(-102.7, -18.6) * mm, v(-98.83, -26.13) * mm, v(-89.8, -28.5) * mm, v(-74.74, -28.5) * mm, v(-68.72, -28.28) * mm, v(-67, -31.72) * mm, v(-63.34, -39.68) * mm, v(-51.08, -51.94) * mm, v(-35.6, -60.33) * mm, v(-30.86, -59.9) * mm, v(-27.85, -56.89) * mm, v(-29.57, -51.94) * mm, v(-34.3, -46.13) * mm, v(-39.9, -39.9) * mm, v(-44.84, -30.86) * mm, v(-47, -23.12) * mm, v(-46.56, -18.6) * mm, v(-42.9, -21.4) * mm, v(-37.1, -23.98) * mm, v(-28.71, -24.84) * mm, v(-17.74, -24.2) * mm, v(-6.77, -24.2) * mm, v(0, -23.98) * mm], "startDerivative": vector(-448.26, 103.85) * mm, "endDerivative": vector(294.14, 13.03) * mm});
            skLineSegment(sketch, "E4468", {"start": v(0, 56.67) * mm, "end": v(0, -23.98) * mm, "construction": true});
            skFitSpline(sketch, "E4469.MirrorCS", {"points": [v(0, 56.67) * mm, v(14.73, 59.25) * mm, v(32.8, 58.18) * mm, v(47.43, 54.52) * mm, v(53.66, 52.59) * mm, v(64.42, 53.88) * mm, v(74.53, 54.1) * mm, v(85.5, 56.24) * mm, v(93.24, 57.1) * mm, v(101.41, 55.38) * mm, v(106.14, 49.36) * mm, v(106.14, 41.19) * mm, v(102.7, 34.74) * mm, v(91.09, 22.7) * mm, v(88.5, 16.45) * mm, v(92.8, 11.72) * mm, v(98.61, 8.28) * mm, v(102.49, 0) * mm, v(102.92, -10.86) * mm, v(102.7, -18.6) * mm, v(98.83, -26.13) * mm, v(89.8, -28.5) * mm, v(74.74, -28.5) * mm, v(68.72, -28.28) * mm, v(67, -31.72) * mm, v(63.34, -39.68) * mm, v(51.08, -51.94) * mm, v(35.6, -60.33) * mm, v(30.86, -59.9) * mm, v(27.85, -56.89) * mm, v(29.57, -51.94) * mm, v(34.3, -46.13) * mm, v(39.9, -39.9) * mm, v(44.84, -30.86) * mm, v(47, -23.12) * mm, v(46.56, -18.6) * mm, v(42.9, -21.4) * mm, v(37.1, -23.98) * mm, v(28.71, -24.84) * mm, v(17.74, -24.2) * mm, v(6.77, -24.2) * mm, v(0, -23.98) * mm], "startDerivative": vector(448.26, 103.85) * mm, "endDerivative": vector(-294.14, 13.03) * mm});
            skSolve(sketch);
        }
        {
            var Q0;
            Q0=makeQuery(id+"F5.imprint","IMPRINT",FACE,{"disambiguationData":[TD([[makeQuery(id+"F5.imprint","IMPRINT",EDGE,{"derivedFrom":sQuery(id+"F5.wireOp",EDGE,"E4467")}),1.0]])]});
            extrude(context, id + "F6", {"entities" : qUnion([Q0]), "oppositeDirection" : true, "depth" : 2.54 * mm, "offsetDistance" : 25.4 * mm});
        }
    });
